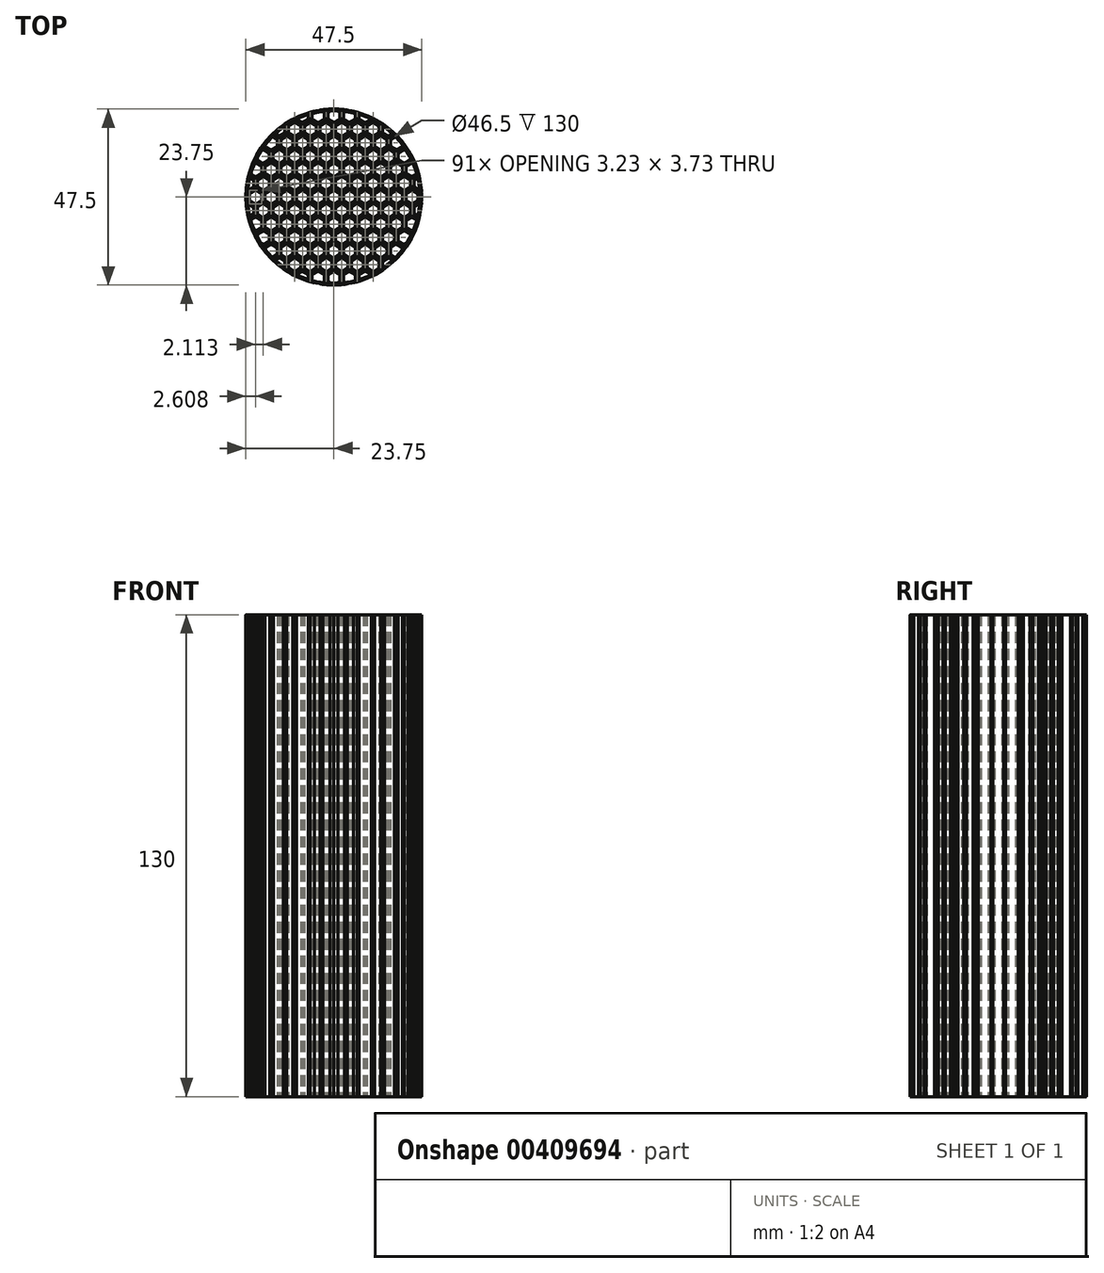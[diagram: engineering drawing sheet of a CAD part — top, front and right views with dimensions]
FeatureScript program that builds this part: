
annotation { "Feature Type Name" : "Feature", "Feature Type Description" : "" }
export const myFeature = defineFeature(function(context is Context, id is Id, definition is map)
    precondition{}
    {
        {
            var Q0;
            Q0=qCreatedBy(makeId("Top.planeOp"),FACE);
            var sketch = newSketch(context, id + "F0", { "sketchPlane" : qUnion([Q0])});
            skCircle(sketch, "E0", {"center": v(0, 0) * mm, "radius": 23.75 * mm});
            skCircle(sketch, "E1.cCircle", {"center": v(0, 0) * mm, "radius": 1.61 * mm, "construction": true});
            skLineSegment(sketch, "E1.0", {"start": v(1.61, 0.93) * mm, "end": v(1.61, -0.93) * mm});
            skLineSegment(sketch, "E1.1", {"start": v(1.61, -0.93) * mm, "end": v(0, -1.86) * mm});
            skLineSegment(sketch, "E1.2", {"start": v(0, -1.86) * mm, "end": v(-1.61, -0.93) * mm});
            skLineSegment(sketch, "E1.3", {"start": v(-1.61, -0.93) * mm, "end": v(-1.61, 0.93) * mm});
            skLineSegment(sketch, "E1.4", {"start": v(-1.61, 0.93) * mm, "end": v(0, 1.86) * mm});
            skLineSegment(sketch, "E1.5", {"start": v(0, 1.86) * mm, "end": v(1.61, 0.93) * mm});
            skPoint(sketch, "E1.0.midPoint", {"position": v(1.61, 0) * mm});
            skLineSegment(sketch, "E2", {"start": v(-1.61, 0) * mm, "end": v(1.61, 0) * mm, "construction": true});
            skCircle(sketch, "E3.cCircle", {"center": v(0, 0) * mm, "radius": 2.11 * mm, "construction": true});
            skLineSegment(sketch, "E3.0", {"start": v(2.11, 1.22) * mm, "end": v(2.11, -1.22) * mm});
            skLineSegment(sketch, "E3.1", {"start": v(2.11, -1.22) * mm, "end": v(0, -2.44) * mm});
            skLineSegment(sketch, "E3.2", {"start": v(0, -2.44) * mm, "end": v(-2.11, -1.22) * mm});
            skLineSegment(sketch, "E3.3", {"start": v(-2.11, -1.22) * mm, "end": v(-2.11, 1.22) * mm});
            skLineSegment(sketch, "E3.4", {"start": v(-2.11, 1.22) * mm, "end": v(0, 2.44) * mm});
            skLineSegment(sketch, "E3.5", {"start": v(0, 2.44) * mm, "end": v(2.11, 1.22) * mm});
            skPoint(sketch, "E3.0.midPoint", {"position": v(2.11, 0) * mm});
            skLineSegment(sketch, "E4", {"start": v(1.61, 0) * mm, "end": v(2.11, 0) * mm, "construction": true});
            skCircle(sketch, "E5", {"center": v(0, 0) * mm, "radius": 23.25 * mm});
            skLineSegment(sketch, "E6", {"start": v(23.25, 0) * mm, "end": v(23.75, 0) * mm, "construction": true});
            skSolve(sketch);
        }
        {
            var Q0;
            Q0=makeQuery(id+"F0.imprint","IMPRINT",FACE,{"disambiguationData":[TD([[makeQuery(id+"F0.imprint","IMPRINT",EDGE,{"derivedFrom":sQuery(id+"F0.wireOp",EDGE,"E1.0")}),1.0]])]});
            var Q1;
            Q1=makeQuery(id+"F0.imprint","IMPRINT",FACE,{"disambiguationData":[TD([[makeQuery(id+"F0.imprint","IMPRINT",EDGE,{"derivedFrom":sQuery(id+"F0.wireOp",EDGE,"E0")}),1.0]])]});
            extrude(context, id + "F1", {"entities" : qUnion([Q0, Q1]), "depth" : 130 * mm});
        }
        {
            var Q0;
            Q0=qCreatedBy(makeId("Top.planeOp"),FACE);
            var sketch = newSketch(context, id + "F2", { "sketchPlane" : qUnion([Q0])});
            skLineSegment(sketch, "E7", {"start": v(-33.71, 0) * mm, "end": v(22.23, 0) * mm, "construction": true});
            skLineSegment(sketch, "E8", {"start": v(0, 14.5) * mm, "end": v(0, -14.97) * mm, "construction": true});
            skLineSegment(sketch, "E9", {"start": v(0, 0) * mm, "end": v(-15.04, 15.04) * mm, "construction": true});
            skLineSegment(sketch, "E10", {"start": v(0, 0) * mm, "end": v(11.03, 11.03) * mm, "construction": true});
            skLineSegment(sketch, "E11", {"start": v(-15.04, 15.04) * mm, "end": v(21.6, -21.6) * mm, "construction": true});
            skLineSegment(sketch, "E12", {"start": v(11.03, 11.03) * mm, "end": v(-14.83, -14.83) * mm, "construction": true});
            skSolve(sketch);
        }
        {
            var Q0;
            Q0=makeQuery(id+"F1.opExtrude","SWEPT_BODY",BODY,{"disambiguationData":[OSD([sQuery(id+"F0.wireOp",EDGE,"E1.0"),sQuery(id+"F0.wireOp",EDGE,"E1.1"),sQuery(id+"F0.wireOp",EDGE,"E1.2"),sQuery(id+"F0.wireOp",EDGE,"E1.3"),sQuery(id+"F0.wireOp",EDGE,"E1.4"),sQuery(id+"F0.wireOp",EDGE,"E1.5"),sQuery(id+"F0.wireOp",EDGE,"E3.0"),sQuery(id+"F0.wireOp",EDGE,"E3.1"),sQuery(id+"F0.wireOp",EDGE,"E3.2"),sQuery(id+"F0.wireOp",EDGE,"E3.3"),sQuery(id+"F0.wireOp",EDGE,"E3.4"),sQuery(id+"F0.wireOp",EDGE,"E3.5")])]});
            var Q1;
            Q1=sQuery(id+"F2.wireOp",EDGE,"E7");
            transform(context, id + "F3", {"entities" : qUnion([Q0]), "transformType" : TransformType.TRANSLATION_3D, "dx" : 4.23 * mm, "dy" : 0 * mm, "dz" : 0 * mm, "makeCopy" : true});
        }
        {
            var Q0;
            Q0=makeQuery(id+"F1.opExtrude","SWEPT_BODY",BODY,{"disambiguationData":[OSD([sQuery(id+"F0.wireOp",EDGE,"E1.0"),sQuery(id+"F0.wireOp",EDGE,"E1.1"),sQuery(id+"F0.wireOp",EDGE,"E1.2"),sQuery(id+"F0.wireOp",EDGE,"E1.3"),sQuery(id+"F0.wireOp",EDGE,"E1.4"),sQuery(id+"F0.wireOp",EDGE,"E1.5"),sQuery(id+"F0.wireOp",EDGE,"E3.0"),sQuery(id+"F0.wireOp",EDGE,"E3.1"),sQuery(id+"F0.wireOp",EDGE,"E3.2"),sQuery(id+"F0.wireOp",EDGE,"E3.3"),sQuery(id+"F0.wireOp",EDGE,"E3.4"),sQuery(id+"F0.wireOp",EDGE,"E3.5")])]});
            var Q1;
            Q1=makeQuery(id+"F3.opPattern","COPY",BODY,{"derivedFrom":makeQuery(id+"F1.opExtrude","SWEPT_BODY",BODY,{"disambiguationData":[OSD([sQuery(id+"F0.wireOp",EDGE,"E1.0"),sQuery(id+"F0.wireOp",EDGE,"E1.1"),sQuery(id+"F0.wireOp",EDGE,"E1.2"),sQuery(id+"F0.wireOp",EDGE,"E1.3"),sQuery(id+"F0.wireOp",EDGE,"E1.4"),sQuery(id+"F0.wireOp",EDGE,"E1.5"),sQuery(id+"F0.wireOp",EDGE,"E3.0"),sQuery(id+"F0.wireOp",EDGE,"E3.1"),sQuery(id+"F0.wireOp",EDGE,"E3.2"),sQuery(id+"F0.wireOp",EDGE,"E3.3"),sQuery(id+"F0.wireOp",EDGE,"E3.4"),sQuery(id+"F0.wireOp",EDGE,"E3.5")])]}),"instanceName":"1"});
            transform(context, id + "F4", {"entities" : qUnion([Q0, Q1]), "transformType" : TransformType.TRANSLATION_3D, "dx" : 8.45 * mm, "dy" : 0 * mm, "dz" : 0 * mm, "makeCopy" : true});
        }
        {
            var Q0;
            Q0=makeQuery(id+"F4.opPattern","COPY",BODY,{"derivedFrom":makeQuery(id+"F1.opExtrude","SWEPT_BODY",BODY,{"disambiguationData":[OSD([sQuery(id+"F0.wireOp",EDGE,"E1.0"),sQuery(id+"F0.wireOp",EDGE,"E1.1"),sQuery(id+"F0.wireOp",EDGE,"E1.2"),sQuery(id+"F0.wireOp",EDGE,"E1.3"),sQuery(id+"F0.wireOp",EDGE,"E1.4"),sQuery(id+"F0.wireOp",EDGE,"E1.5"),sQuery(id+"F0.wireOp",EDGE,"E3.0"),sQuery(id+"F0.wireOp",EDGE,"E3.1"),sQuery(id+"F0.wireOp",EDGE,"E3.2"),sQuery(id+"F0.wireOp",EDGE,"E3.3"),sQuery(id+"F0.wireOp",EDGE,"E3.4"),sQuery(id+"F0.wireOp",EDGE,"E3.5")])]}),"instanceName":"1"});
            var Q1;
            Q1=makeQuery(id+"F4.opPattern","COPY",BODY,{"derivedFrom":makeQuery(id+"F3.opPattern","COPY",BODY,{"derivedFrom":makeQuery(id+"F1.opExtrude","SWEPT_BODY",BODY,{"disambiguationData":[OSD([sQuery(id+"F0.wireOp",EDGE,"E1.0"),sQuery(id+"F0.wireOp",EDGE,"E1.1"),sQuery(id+"F0.wireOp",EDGE,"E1.2"),sQuery(id+"F0.wireOp",EDGE,"E1.3"),sQuery(id+"F0.wireOp",EDGE,"E1.4"),sQuery(id+"F0.wireOp",EDGE,"E1.5"),sQuery(id+"F0.wireOp",EDGE,"E3.0"),sQuery(id+"F0.wireOp",EDGE,"E3.1"),sQuery(id+"F0.wireOp",EDGE,"E3.2"),sQuery(id+"F0.wireOp",EDGE,"E3.3"),sQuery(id+"F0.wireOp",EDGE,"E3.4"),sQuery(id+"F0.wireOp",EDGE,"E3.5")])]}),"instanceName":"1"}),"instanceName":"1"});
            transform(context, id + "F5", {"entities" : qUnion([Q0, Q1]), "transformType" : TransformType.TRANSLATION_3D, "dx" : 8.45 * mm, "dy" : 0 * mm, "dz" : 0 * mm, "makeCopy" : true});
        }
        {
            var Q0;
            Q0=makeQuery(id+"F1.opExtrude","SWEPT_BODY",BODY,{"disambiguationData":[OSD([sQuery(id+"F0.wireOp",EDGE,"E1.0"),sQuery(id+"F0.wireOp",EDGE,"E1.1"),sQuery(id+"F0.wireOp",EDGE,"E1.2"),sQuery(id+"F0.wireOp",EDGE,"E1.3"),sQuery(id+"F0.wireOp",EDGE,"E1.4"),sQuery(id+"F0.wireOp",EDGE,"E1.5"),sQuery(id+"F0.wireOp",EDGE,"E3.0"),sQuery(id+"F0.wireOp",EDGE,"E3.1"),sQuery(id+"F0.wireOp",EDGE,"E3.2"),sQuery(id+"F0.wireOp",EDGE,"E3.3"),sQuery(id+"F0.wireOp",EDGE,"E3.4"),sQuery(id+"F0.wireOp",EDGE,"E3.5")])]});
            var Q1;
            Q1=makeQuery(id+"F3.opPattern","COPY",BODY,{"derivedFrom":makeQuery(id+"F1.opExtrude","SWEPT_BODY",BODY,{"disambiguationData":[OSD([sQuery(id+"F0.wireOp",EDGE,"E1.0"),sQuery(id+"F0.wireOp",EDGE,"E1.1"),sQuery(id+"F0.wireOp",EDGE,"E1.2"),sQuery(id+"F0.wireOp",EDGE,"E1.3"),sQuery(id+"F0.wireOp",EDGE,"E1.4"),sQuery(id+"F0.wireOp",EDGE,"E1.5"),sQuery(id+"F0.wireOp",EDGE,"E3.0"),sQuery(id+"F0.wireOp",EDGE,"E3.1"),sQuery(id+"F0.wireOp",EDGE,"E3.2"),sQuery(id+"F0.wireOp",EDGE,"E3.3"),sQuery(id+"F0.wireOp",EDGE,"E3.4"),sQuery(id+"F0.wireOp",EDGE,"E3.5")])]}),"instanceName":"1"});
            var Q2;
            Q2=makeQuery(id+"F4.opPattern","COPY",BODY,{"derivedFrom":makeQuery(id+"F1.opExtrude","SWEPT_BODY",BODY,{"disambiguationData":[OSD([sQuery(id+"F0.wireOp",EDGE,"E1.0"),sQuery(id+"F0.wireOp",EDGE,"E1.1"),sQuery(id+"F0.wireOp",EDGE,"E1.2"),sQuery(id+"F0.wireOp",EDGE,"E1.3"),sQuery(id+"F0.wireOp",EDGE,"E1.4"),sQuery(id+"F0.wireOp",EDGE,"E1.5"),sQuery(id+"F0.wireOp",EDGE,"E3.0"),sQuery(id+"F0.wireOp",EDGE,"E3.1"),sQuery(id+"F0.wireOp",EDGE,"E3.2"),sQuery(id+"F0.wireOp",EDGE,"E3.3"),sQuery(id+"F0.wireOp",EDGE,"E3.4"),sQuery(id+"F0.wireOp",EDGE,"E3.5")])]}),"instanceName":"1"});
            var Q3;
            Q3=makeQuery(id+"F4.opPattern","COPY",BODY,{"derivedFrom":makeQuery(id+"F3.opPattern","COPY",BODY,{"derivedFrom":makeQuery(id+"F1.opExtrude","SWEPT_BODY",BODY,{"disambiguationData":[OSD([sQuery(id+"F0.wireOp",EDGE,"E1.0"),sQuery(id+"F0.wireOp",EDGE,"E1.1"),sQuery(id+"F0.wireOp",EDGE,"E1.2"),sQuery(id+"F0.wireOp",EDGE,"E1.3"),sQuery(id+"F0.wireOp",EDGE,"E1.4"),sQuery(id+"F0.wireOp",EDGE,"E1.5"),sQuery(id+"F0.wireOp",EDGE,"E3.0"),sQuery(id+"F0.wireOp",EDGE,"E3.1"),sQuery(id+"F0.wireOp",EDGE,"E3.2"),sQuery(id+"F0.wireOp",EDGE,"E3.3"),sQuery(id+"F0.wireOp",EDGE,"E3.4"),sQuery(id+"F0.wireOp",EDGE,"E3.5")])]}),"instanceName":"1"}),"instanceName":"1"});
            var Q4;
            Q4=makeQuery(id+"F5.opPattern","COPY",BODY,{"derivedFrom":makeQuery(id+"F4.opPattern","COPY",BODY,{"derivedFrom":makeQuery(id+"F1.opExtrude","SWEPT_BODY",BODY,{"disambiguationData":[OSD([sQuery(id+"F0.wireOp",EDGE,"E1.0"),sQuery(id+"F0.wireOp",EDGE,"E1.1"),sQuery(id+"F0.wireOp",EDGE,"E1.2"),sQuery(id+"F0.wireOp",EDGE,"E1.3"),sQuery(id+"F0.wireOp",EDGE,"E1.4"),sQuery(id+"F0.wireOp",EDGE,"E1.5"),sQuery(id+"F0.wireOp",EDGE,"E3.0"),sQuery(id+"F0.wireOp",EDGE,"E3.1"),sQuery(id+"F0.wireOp",EDGE,"E3.2"),sQuery(id+"F0.wireOp",EDGE,"E3.3"),sQuery(id+"F0.wireOp",EDGE,"E3.4"),sQuery(id+"F0.wireOp",EDGE,"E3.5")])]}),"instanceName":"1"}),"instanceName":"1"});
            var Q5;
            Q5=makeQuery(id+"F5.opPattern","COPY",BODY,{"derivedFrom":makeQuery(id+"F4.opPattern","COPY",BODY,{"derivedFrom":makeQuery(id+"F3.opPattern","COPY",BODY,{"derivedFrom":makeQuery(id+"F1.opExtrude","SWEPT_BODY",BODY,{"disambiguationData":[OSD([sQuery(id+"F0.wireOp",EDGE,"E1.0"),sQuery(id+"F0.wireOp",EDGE,"E1.1"),sQuery(id+"F0.wireOp",EDGE,"E1.2"),sQuery(id+"F0.wireOp",EDGE,"E1.3"),sQuery(id+"F0.wireOp",EDGE,"E1.4"),sQuery(id+"F0.wireOp",EDGE,"E1.5"),sQuery(id+"F0.wireOp",EDGE,"E3.0"),sQuery(id+"F0.wireOp",EDGE,"E3.1"),sQuery(id+"F0.wireOp",EDGE,"E3.2"),sQuery(id+"F0.wireOp",EDGE,"E3.3"),sQuery(id+"F0.wireOp",EDGE,"E3.4"),sQuery(id+"F0.wireOp",EDGE,"E3.5")])]}),"instanceName":"1"}),"instanceName":"1"}),"instanceName":"1"});
            transform(context, id + "F6", {"entities" : qUnion([Q0, Q1, Q2, Q3, Q4, Q5]), "transformType" : TransformType.TRANSLATION_3D, "dx" : 2.1 * mm, "dy" : 3.65 * mm, "dz" : 0 * mm, "makeCopy" : true});
        }
        {
            var Q0;
            Q0=makeQuery(id+"F6.opPattern","COPY",BODY,{"derivedFrom":makeQuery(id+"F1.opExtrude","SWEPT_BODY",BODY,{"disambiguationData":[OSD([sQuery(id+"F0.wireOp",EDGE,"E1.0"),sQuery(id+"F0.wireOp",EDGE,"E1.1"),sQuery(id+"F0.wireOp",EDGE,"E1.2"),sQuery(id+"F0.wireOp",EDGE,"E1.3"),sQuery(id+"F0.wireOp",EDGE,"E1.4"),sQuery(id+"F0.wireOp",EDGE,"E1.5"),sQuery(id+"F0.wireOp",EDGE,"E3.0"),sQuery(id+"F0.wireOp",EDGE,"E3.1"),sQuery(id+"F0.wireOp",EDGE,"E3.2"),sQuery(id+"F0.wireOp",EDGE,"E3.3"),sQuery(id+"F0.wireOp",EDGE,"E3.4"),sQuery(id+"F0.wireOp",EDGE,"E3.5")])]}),"instanceName":"1"});
            var Q1;
            Q1=makeQuery(id+"F1.opExtrude","SWEPT_BODY",BODY,{"disambiguationData":[OSD([sQuery(id+"F0.wireOp",EDGE,"E1.0"),sQuery(id+"F0.wireOp",EDGE,"E1.1"),sQuery(id+"F0.wireOp",EDGE,"E1.2"),sQuery(id+"F0.wireOp",EDGE,"E1.3"),sQuery(id+"F0.wireOp",EDGE,"E1.4"),sQuery(id+"F0.wireOp",EDGE,"E1.5"),sQuery(id+"F0.wireOp",EDGE,"E3.0"),sQuery(id+"F0.wireOp",EDGE,"E3.1"),sQuery(id+"F0.wireOp",EDGE,"E3.2"),sQuery(id+"F0.wireOp",EDGE,"E3.3"),sQuery(id+"F0.wireOp",EDGE,"E3.4"),sQuery(id+"F0.wireOp",EDGE,"E3.5")])]});
            var Q2;
            Q2=makeQuery(id+"F3.opPattern","COPY",BODY,{"derivedFrom":makeQuery(id+"F1.opExtrude","SWEPT_BODY",BODY,{"disambiguationData":[OSD([sQuery(id+"F0.wireOp",EDGE,"E1.0"),sQuery(id+"F0.wireOp",EDGE,"E1.1"),sQuery(id+"F0.wireOp",EDGE,"E1.2"),sQuery(id+"F0.wireOp",EDGE,"E1.3"),sQuery(id+"F0.wireOp",EDGE,"E1.4"),sQuery(id+"F0.wireOp",EDGE,"E1.5"),sQuery(id+"F0.wireOp",EDGE,"E3.0"),sQuery(id+"F0.wireOp",EDGE,"E3.1"),sQuery(id+"F0.wireOp",EDGE,"E3.2"),sQuery(id+"F0.wireOp",EDGE,"E3.3"),sQuery(id+"F0.wireOp",EDGE,"E3.4"),sQuery(id+"F0.wireOp",EDGE,"E3.5")])]}),"instanceName":"1"});
            var Q3;
            Q3=makeQuery(id+"F6.opPattern","COPY",BODY,{"derivedFrom":makeQuery(id+"F3.opPattern","COPY",BODY,{"derivedFrom":makeQuery(id+"F1.opExtrude","SWEPT_BODY",BODY,{"disambiguationData":[OSD([sQuery(id+"F0.wireOp",EDGE,"E1.0"),sQuery(id+"F0.wireOp",EDGE,"E1.1"),sQuery(id+"F0.wireOp",EDGE,"E1.2"),sQuery(id+"F0.wireOp",EDGE,"E1.3"),sQuery(id+"F0.wireOp",EDGE,"E1.4"),sQuery(id+"F0.wireOp",EDGE,"E1.5"),sQuery(id+"F0.wireOp",EDGE,"E3.0"),sQuery(id+"F0.wireOp",EDGE,"E3.1"),sQuery(id+"F0.wireOp",EDGE,"E3.2"),sQuery(id+"F0.wireOp",EDGE,"E3.3"),sQuery(id+"F0.wireOp",EDGE,"E3.4"),sQuery(id+"F0.wireOp",EDGE,"E3.5")])]}),"instanceName":"1"}),"instanceName":"1"});
            var Q4;
            Q4=makeQuery(id+"F6.opPattern","COPY",BODY,{"derivedFrom":makeQuery(id+"F4.opPattern","COPY",BODY,{"derivedFrom":makeQuery(id+"F1.opExtrude","SWEPT_BODY",BODY,{"disambiguationData":[OSD([sQuery(id+"F0.wireOp",EDGE,"E1.0"),sQuery(id+"F0.wireOp",EDGE,"E1.1"),sQuery(id+"F0.wireOp",EDGE,"E1.2"),sQuery(id+"F0.wireOp",EDGE,"E1.3"),sQuery(id+"F0.wireOp",EDGE,"E1.4"),sQuery(id+"F0.wireOp",EDGE,"E1.5"),sQuery(id+"F0.wireOp",EDGE,"E3.0"),sQuery(id+"F0.wireOp",EDGE,"E3.1"),sQuery(id+"F0.wireOp",EDGE,"E3.2"),sQuery(id+"F0.wireOp",EDGE,"E3.3"),sQuery(id+"F0.wireOp",EDGE,"E3.4"),sQuery(id+"F0.wireOp",EDGE,"E3.5")])]}),"instanceName":"1"}),"instanceName":"1"});
            var Q5;
            Q5=makeQuery(id+"F4.opPattern","COPY",BODY,{"derivedFrom":makeQuery(id+"F1.opExtrude","SWEPT_BODY",BODY,{"disambiguationData":[OSD([sQuery(id+"F0.wireOp",EDGE,"E1.0"),sQuery(id+"F0.wireOp",EDGE,"E1.1"),sQuery(id+"F0.wireOp",EDGE,"E1.2"),sQuery(id+"F0.wireOp",EDGE,"E1.3"),sQuery(id+"F0.wireOp",EDGE,"E1.4"),sQuery(id+"F0.wireOp",EDGE,"E1.5"),sQuery(id+"F0.wireOp",EDGE,"E3.0"),sQuery(id+"F0.wireOp",EDGE,"E3.1"),sQuery(id+"F0.wireOp",EDGE,"E3.2"),sQuery(id+"F0.wireOp",EDGE,"E3.3"),sQuery(id+"F0.wireOp",EDGE,"E3.4"),sQuery(id+"F0.wireOp",EDGE,"E3.5")])]}),"instanceName":"1"});
            var Q6;
            Q6=makeQuery(id+"F4.opPattern","COPY",BODY,{"derivedFrom":makeQuery(id+"F3.opPattern","COPY",BODY,{"derivedFrom":makeQuery(id+"F1.opExtrude","SWEPT_BODY",BODY,{"disambiguationData":[OSD([sQuery(id+"F0.wireOp",EDGE,"E1.0"),sQuery(id+"F0.wireOp",EDGE,"E1.1"),sQuery(id+"F0.wireOp",EDGE,"E1.2"),sQuery(id+"F0.wireOp",EDGE,"E1.3"),sQuery(id+"F0.wireOp",EDGE,"E1.4"),sQuery(id+"F0.wireOp",EDGE,"E1.5"),sQuery(id+"F0.wireOp",EDGE,"E3.0"),sQuery(id+"F0.wireOp",EDGE,"E3.1"),sQuery(id+"F0.wireOp",EDGE,"E3.2"),sQuery(id+"F0.wireOp",EDGE,"E3.3"),sQuery(id+"F0.wireOp",EDGE,"E3.4"),sQuery(id+"F0.wireOp",EDGE,"E3.5")])]}),"instanceName":"1"}),"instanceName":"1"});
            var Q7;
            Q7=makeQuery(id+"F6.opPattern","COPY",BODY,{"derivedFrom":makeQuery(id+"F4.opPattern","COPY",BODY,{"derivedFrom":makeQuery(id+"F3.opPattern","COPY",BODY,{"derivedFrom":makeQuery(id+"F1.opExtrude","SWEPT_BODY",BODY,{"disambiguationData":[OSD([sQuery(id+"F0.wireOp",EDGE,"E1.0"),sQuery(id+"F0.wireOp",EDGE,"E1.1"),sQuery(id+"F0.wireOp",EDGE,"E1.2"),sQuery(id+"F0.wireOp",EDGE,"E1.3"),sQuery(id+"F0.wireOp",EDGE,"E1.4"),sQuery(id+"F0.wireOp",EDGE,"E1.5"),sQuery(id+"F0.wireOp",EDGE,"E3.0"),sQuery(id+"F0.wireOp",EDGE,"E3.1"),sQuery(id+"F0.wireOp",EDGE,"E3.2"),sQuery(id+"F0.wireOp",EDGE,"E3.3"),sQuery(id+"F0.wireOp",EDGE,"E3.4"),sQuery(id+"F0.wireOp",EDGE,"E3.5")])]}),"instanceName":"1"}),"instanceName":"1"}),"instanceName":"1"});
            var Q8;
            Q8=makeQuery(id+"F6.opPattern","COPY",BODY,{"derivedFrom":makeQuery(id+"F5.opPattern","COPY",BODY,{"derivedFrom":makeQuery(id+"F4.opPattern","COPY",BODY,{"derivedFrom":makeQuery(id+"F1.opExtrude","SWEPT_BODY",BODY,{"disambiguationData":[OSD([sQuery(id+"F0.wireOp",EDGE,"E1.0"),sQuery(id+"F0.wireOp",EDGE,"E1.1"),sQuery(id+"F0.wireOp",EDGE,"E1.2"),sQuery(id+"F0.wireOp",EDGE,"E1.3"),sQuery(id+"F0.wireOp",EDGE,"E1.4"),sQuery(id+"F0.wireOp",EDGE,"E1.5"),sQuery(id+"F0.wireOp",EDGE,"E3.0"),sQuery(id+"F0.wireOp",EDGE,"E3.1"),sQuery(id+"F0.wireOp",EDGE,"E3.2"),sQuery(id+"F0.wireOp",EDGE,"E3.3"),sQuery(id+"F0.wireOp",EDGE,"E3.4"),sQuery(id+"F0.wireOp",EDGE,"E3.5")])]}),"instanceName":"1"}),"instanceName":"1"}),"instanceName":"1"});
            var Q9;
            Q9=makeQuery(id+"F5.opPattern","COPY",BODY,{"derivedFrom":makeQuery(id+"F4.opPattern","COPY",BODY,{"derivedFrom":makeQuery(id+"F1.opExtrude","SWEPT_BODY",BODY,{"disambiguationData":[OSD([sQuery(id+"F0.wireOp",EDGE,"E1.0"),sQuery(id+"F0.wireOp",EDGE,"E1.1"),sQuery(id+"F0.wireOp",EDGE,"E1.2"),sQuery(id+"F0.wireOp",EDGE,"E1.3"),sQuery(id+"F0.wireOp",EDGE,"E1.4"),sQuery(id+"F0.wireOp",EDGE,"E1.5"),sQuery(id+"F0.wireOp",EDGE,"E3.0"),sQuery(id+"F0.wireOp",EDGE,"E3.1"),sQuery(id+"F0.wireOp",EDGE,"E3.2"),sQuery(id+"F0.wireOp",EDGE,"E3.3"),sQuery(id+"F0.wireOp",EDGE,"E3.4"),sQuery(id+"F0.wireOp",EDGE,"E3.5")])]}),"instanceName":"1"}),"instanceName":"1"});
            var Q10;
            Q10=makeQuery(id+"F6.opPattern","COPY",BODY,{"derivedFrom":makeQuery(id+"F5.opPattern","COPY",BODY,{"derivedFrom":makeQuery(id+"F4.opPattern","COPY",BODY,{"derivedFrom":makeQuery(id+"F3.opPattern","COPY",BODY,{"derivedFrom":makeQuery(id+"F1.opExtrude","SWEPT_BODY",BODY,{"disambiguationData":[OSD([sQuery(id+"F0.wireOp",EDGE,"E1.0"),sQuery(id+"F0.wireOp",EDGE,"E1.1"),sQuery(id+"F0.wireOp",EDGE,"E1.2"),sQuery(id+"F0.wireOp",EDGE,"E1.3"),sQuery(id+"F0.wireOp",EDGE,"E1.4"),sQuery(id+"F0.wireOp",EDGE,"E1.5"),sQuery(id+"F0.wireOp",EDGE,"E3.0"),sQuery(id+"F0.wireOp",EDGE,"E3.1"),sQuery(id+"F0.wireOp",EDGE,"E3.2"),sQuery(id+"F0.wireOp",EDGE,"E3.3"),sQuery(id+"F0.wireOp",EDGE,"E3.4"),sQuery(id+"F0.wireOp",EDGE,"E3.5")])]}),"instanceName":"1"}),"instanceName":"1"}),"instanceName":"1"}),"instanceName":"1"});
            var Q11;
            Q11=makeQuery(id+"F5.opPattern","COPY",BODY,{"derivedFrom":makeQuery(id+"F4.opPattern","COPY",BODY,{"derivedFrom":makeQuery(id+"F3.opPattern","COPY",BODY,{"derivedFrom":makeQuery(id+"F1.opExtrude","SWEPT_BODY",BODY,{"disambiguationData":[OSD([sQuery(id+"F0.wireOp",EDGE,"E1.0"),sQuery(id+"F0.wireOp",EDGE,"E1.1"),sQuery(id+"F0.wireOp",EDGE,"E1.2"),sQuery(id+"F0.wireOp",EDGE,"E1.3"),sQuery(id+"F0.wireOp",EDGE,"E1.4"),sQuery(id+"F0.wireOp",EDGE,"E1.5"),sQuery(id+"F0.wireOp",EDGE,"E3.0"),sQuery(id+"F0.wireOp",EDGE,"E3.1"),sQuery(id+"F0.wireOp",EDGE,"E3.2"),sQuery(id+"F0.wireOp",EDGE,"E3.3"),sQuery(id+"F0.wireOp",EDGE,"E3.4"),sQuery(id+"F0.wireOp",EDGE,"E3.5")])]}),"instanceName":"1"}),"instanceName":"1"}),"instanceName":"1"});
            transform(context, id + "F7", {"entities" : qUnion([Q0, Q1, Q2, Q3, Q4, Q5, Q6, Q7, Q8, Q9, Q10, Q11]), "transformType" : TransformType.TRANSLATION_3D, "dx" : 4.23 * mm, "dy" : 7.3 * mm, "dz" : 0 * mm, "makeCopy" : true});
        }
        {
            var Q0;
            Q0=makeQuery(id+"F1.opExtrude","SWEPT_BODY",BODY,{"disambiguationData":[OSD([sQuery(id+"F0.wireOp",EDGE,"E1.0"),sQuery(id+"F0.wireOp",EDGE,"E1.1"),sQuery(id+"F0.wireOp",EDGE,"E1.2"),sQuery(id+"F0.wireOp",EDGE,"E1.3"),sQuery(id+"F0.wireOp",EDGE,"E1.4"),sQuery(id+"F0.wireOp",EDGE,"E1.5"),sQuery(id+"F0.wireOp",EDGE,"E3.0"),sQuery(id+"F0.wireOp",EDGE,"E3.1"),sQuery(id+"F0.wireOp",EDGE,"E3.2"),sQuery(id+"F0.wireOp",EDGE,"E3.3"),sQuery(id+"F0.wireOp",EDGE,"E3.4"),sQuery(id+"F0.wireOp",EDGE,"E3.5")])]});
            var Q1;
            Q1=makeQuery(id+"F7.opPattern","COPY",BODY,{"derivedFrom":makeQuery(id+"F6.opPattern","COPY",BODY,{"derivedFrom":makeQuery(id+"F3.opPattern","COPY",BODY,{"derivedFrom":makeQuery(id+"F1.opExtrude","SWEPT_BODY",BODY,{"disambiguationData":[OSD([sQuery(id+"F0.wireOp",EDGE,"E1.0"),sQuery(id+"F0.wireOp",EDGE,"E1.1"),sQuery(id+"F0.wireOp",EDGE,"E1.2"),sQuery(id+"F0.wireOp",EDGE,"E1.3"),sQuery(id+"F0.wireOp",EDGE,"E1.4"),sQuery(id+"F0.wireOp",EDGE,"E1.5"),sQuery(id+"F0.wireOp",EDGE,"E3.0"),sQuery(id+"F0.wireOp",EDGE,"E3.1"),sQuery(id+"F0.wireOp",EDGE,"E3.2"),sQuery(id+"F0.wireOp",EDGE,"E3.3"),sQuery(id+"F0.wireOp",EDGE,"E3.4"),sQuery(id+"F0.wireOp",EDGE,"E3.5")])]}),"instanceName":"1"}),"instanceName":"1"}),"instanceName":"1"});
            var Q2;
            Q2=makeQuery(id+"F7.opPattern","COPY",BODY,{"derivedFrom":makeQuery(id+"F6.opPattern","COPY",BODY,{"derivedFrom":makeQuery(id+"F1.opExtrude","SWEPT_BODY",BODY,{"disambiguationData":[OSD([sQuery(id+"F0.wireOp",EDGE,"E1.0"),sQuery(id+"F0.wireOp",EDGE,"E1.1"),sQuery(id+"F0.wireOp",EDGE,"E1.2"),sQuery(id+"F0.wireOp",EDGE,"E1.3"),sQuery(id+"F0.wireOp",EDGE,"E1.4"),sQuery(id+"F0.wireOp",EDGE,"E1.5"),sQuery(id+"F0.wireOp",EDGE,"E3.0"),sQuery(id+"F0.wireOp",EDGE,"E3.1"),sQuery(id+"F0.wireOp",EDGE,"E3.2"),sQuery(id+"F0.wireOp",EDGE,"E3.3"),sQuery(id+"F0.wireOp",EDGE,"E3.4"),sQuery(id+"F0.wireOp",EDGE,"E3.5")])]}),"instanceName":"1"}),"instanceName":"1"});
            var Q3;
            Q3=makeQuery(id+"F7.opPattern","COPY",BODY,{"derivedFrom":makeQuery(id+"F4.opPattern","COPY",BODY,{"derivedFrom":makeQuery(id+"F1.opExtrude","SWEPT_BODY",BODY,{"disambiguationData":[OSD([sQuery(id+"F0.wireOp",EDGE,"E1.0"),sQuery(id+"F0.wireOp",EDGE,"E1.1"),sQuery(id+"F0.wireOp",EDGE,"E1.2"),sQuery(id+"F0.wireOp",EDGE,"E1.3"),sQuery(id+"F0.wireOp",EDGE,"E1.4"),sQuery(id+"F0.wireOp",EDGE,"E1.5"),sQuery(id+"F0.wireOp",EDGE,"E3.0"),sQuery(id+"F0.wireOp",EDGE,"E3.1"),sQuery(id+"F0.wireOp",EDGE,"E3.2"),sQuery(id+"F0.wireOp",EDGE,"E3.3"),sQuery(id+"F0.wireOp",EDGE,"E3.4"),sQuery(id+"F0.wireOp",EDGE,"E3.5")])]}),"instanceName":"1"}),"instanceName":"1"});
            var Q4;
            Q4=makeQuery(id+"F7.opPattern","COPY",BODY,{"derivedFrom":makeQuery(id+"F3.opPattern","COPY",BODY,{"derivedFrom":makeQuery(id+"F1.opExtrude","SWEPT_BODY",BODY,{"disambiguationData":[OSD([sQuery(id+"F0.wireOp",EDGE,"E1.0"),sQuery(id+"F0.wireOp",EDGE,"E1.1"),sQuery(id+"F0.wireOp",EDGE,"E1.2"),sQuery(id+"F0.wireOp",EDGE,"E1.3"),sQuery(id+"F0.wireOp",EDGE,"E1.4"),sQuery(id+"F0.wireOp",EDGE,"E1.5"),sQuery(id+"F0.wireOp",EDGE,"E3.0"),sQuery(id+"F0.wireOp",EDGE,"E3.1"),sQuery(id+"F0.wireOp",EDGE,"E3.2"),sQuery(id+"F0.wireOp",EDGE,"E3.3"),sQuery(id+"F0.wireOp",EDGE,"E3.4"),sQuery(id+"F0.wireOp",EDGE,"E3.5")])]}),"instanceName":"1"}),"instanceName":"1"});
            var Q5;
            Q5=makeQuery(id+"F7.opPattern","COPY",BODY,{"derivedFrom":makeQuery(id+"F1.opExtrude","SWEPT_BODY",BODY,{"disambiguationData":[OSD([sQuery(id+"F0.wireOp",EDGE,"E1.0"),sQuery(id+"F0.wireOp",EDGE,"E1.1"),sQuery(id+"F0.wireOp",EDGE,"E1.2"),sQuery(id+"F0.wireOp",EDGE,"E1.3"),sQuery(id+"F0.wireOp",EDGE,"E1.4"),sQuery(id+"F0.wireOp",EDGE,"E1.5"),sQuery(id+"F0.wireOp",EDGE,"E3.0"),sQuery(id+"F0.wireOp",EDGE,"E3.1"),sQuery(id+"F0.wireOp",EDGE,"E3.2"),sQuery(id+"F0.wireOp",EDGE,"E3.3"),sQuery(id+"F0.wireOp",EDGE,"E3.4"),sQuery(id+"F0.wireOp",EDGE,"E3.5")])]}),"instanceName":"1"});
            var Q6;
            Q6=makeQuery(id+"F6.opPattern","COPY",BODY,{"derivedFrom":makeQuery(id+"F4.opPattern","COPY",BODY,{"derivedFrom":makeQuery(id+"F1.opExtrude","SWEPT_BODY",BODY,{"disambiguationData":[OSD([sQuery(id+"F0.wireOp",EDGE,"E1.0"),sQuery(id+"F0.wireOp",EDGE,"E1.1"),sQuery(id+"F0.wireOp",EDGE,"E1.2"),sQuery(id+"F0.wireOp",EDGE,"E1.3"),sQuery(id+"F0.wireOp",EDGE,"E1.4"),sQuery(id+"F0.wireOp",EDGE,"E1.5"),sQuery(id+"F0.wireOp",EDGE,"E3.0"),sQuery(id+"F0.wireOp",EDGE,"E3.1"),sQuery(id+"F0.wireOp",EDGE,"E3.2"),sQuery(id+"F0.wireOp",EDGE,"E3.3"),sQuery(id+"F0.wireOp",EDGE,"E3.4"),sQuery(id+"F0.wireOp",EDGE,"E3.5")])]}),"instanceName":"1"}),"instanceName":"1"});
            var Q7;
            Q7=makeQuery(id+"F6.opPattern","COPY",BODY,{"derivedFrom":makeQuery(id+"F3.opPattern","COPY",BODY,{"derivedFrom":makeQuery(id+"F1.opExtrude","SWEPT_BODY",BODY,{"disambiguationData":[OSD([sQuery(id+"F0.wireOp",EDGE,"E1.0"),sQuery(id+"F0.wireOp",EDGE,"E1.1"),sQuery(id+"F0.wireOp",EDGE,"E1.2"),sQuery(id+"F0.wireOp",EDGE,"E1.3"),sQuery(id+"F0.wireOp",EDGE,"E1.4"),sQuery(id+"F0.wireOp",EDGE,"E1.5"),sQuery(id+"F0.wireOp",EDGE,"E3.0"),sQuery(id+"F0.wireOp",EDGE,"E3.1"),sQuery(id+"F0.wireOp",EDGE,"E3.2"),sQuery(id+"F0.wireOp",EDGE,"E3.3"),sQuery(id+"F0.wireOp",EDGE,"E3.4"),sQuery(id+"F0.wireOp",EDGE,"E3.5")])]}),"instanceName":"1"}),"instanceName":"1"});
            var Q8;
            Q8=makeQuery(id+"F6.opPattern","COPY",BODY,{"derivedFrom":makeQuery(id+"F1.opExtrude","SWEPT_BODY",BODY,{"disambiguationData":[OSD([sQuery(id+"F0.wireOp",EDGE,"E1.0"),sQuery(id+"F0.wireOp",EDGE,"E1.1"),sQuery(id+"F0.wireOp",EDGE,"E1.2"),sQuery(id+"F0.wireOp",EDGE,"E1.3"),sQuery(id+"F0.wireOp",EDGE,"E1.4"),sQuery(id+"F0.wireOp",EDGE,"E1.5"),sQuery(id+"F0.wireOp",EDGE,"E3.0"),sQuery(id+"F0.wireOp",EDGE,"E3.1"),sQuery(id+"F0.wireOp",EDGE,"E3.2"),sQuery(id+"F0.wireOp",EDGE,"E3.3"),sQuery(id+"F0.wireOp",EDGE,"E3.4"),sQuery(id+"F0.wireOp",EDGE,"E3.5")])]}),"instanceName":"1"});
            var Q9;
            Q9=makeQuery(id+"F4.opPattern","COPY",BODY,{"derivedFrom":makeQuery(id+"F3.opPattern","COPY",BODY,{"derivedFrom":makeQuery(id+"F1.opExtrude","SWEPT_BODY",BODY,{"disambiguationData":[OSD([sQuery(id+"F0.wireOp",EDGE,"E1.0"),sQuery(id+"F0.wireOp",EDGE,"E1.1"),sQuery(id+"F0.wireOp",EDGE,"E1.2"),sQuery(id+"F0.wireOp",EDGE,"E1.3"),sQuery(id+"F0.wireOp",EDGE,"E1.4"),sQuery(id+"F0.wireOp",EDGE,"E1.5"),sQuery(id+"F0.wireOp",EDGE,"E3.0"),sQuery(id+"F0.wireOp",EDGE,"E3.1"),sQuery(id+"F0.wireOp",EDGE,"E3.2"),sQuery(id+"F0.wireOp",EDGE,"E3.3"),sQuery(id+"F0.wireOp",EDGE,"E3.4"),sQuery(id+"F0.wireOp",EDGE,"E3.5")])]}),"instanceName":"1"}),"instanceName":"1"});
            var Q10;
            Q10=makeQuery(id+"F4.opPattern","COPY",BODY,{"derivedFrom":makeQuery(id+"F1.opExtrude","SWEPT_BODY",BODY,{"disambiguationData":[OSD([sQuery(id+"F0.wireOp",EDGE,"E1.0"),sQuery(id+"F0.wireOp",EDGE,"E1.1"),sQuery(id+"F0.wireOp",EDGE,"E1.2"),sQuery(id+"F0.wireOp",EDGE,"E1.3"),sQuery(id+"F0.wireOp",EDGE,"E1.4"),sQuery(id+"F0.wireOp",EDGE,"E1.5"),sQuery(id+"F0.wireOp",EDGE,"E3.0"),sQuery(id+"F0.wireOp",EDGE,"E3.1"),sQuery(id+"F0.wireOp",EDGE,"E3.2"),sQuery(id+"F0.wireOp",EDGE,"E3.3"),sQuery(id+"F0.wireOp",EDGE,"E3.4"),sQuery(id+"F0.wireOp",EDGE,"E3.5")])]}),"instanceName":"1"});
            var Q11;
            Q11=makeQuery(id+"F3.opPattern","COPY",BODY,{"derivedFrom":makeQuery(id+"F1.opExtrude","SWEPT_BODY",BODY,{"disambiguationData":[OSD([sQuery(id+"F0.wireOp",EDGE,"E1.0"),sQuery(id+"F0.wireOp",EDGE,"E1.1"),sQuery(id+"F0.wireOp",EDGE,"E1.2"),sQuery(id+"F0.wireOp",EDGE,"E1.3"),sQuery(id+"F0.wireOp",EDGE,"E1.4"),sQuery(id+"F0.wireOp",EDGE,"E1.5"),sQuery(id+"F0.wireOp",EDGE,"E3.0"),sQuery(id+"F0.wireOp",EDGE,"E3.1"),sQuery(id+"F0.wireOp",EDGE,"E3.2"),sQuery(id+"F0.wireOp",EDGE,"E3.3"),sQuery(id+"F0.wireOp",EDGE,"E3.4"),sQuery(id+"F0.wireOp",EDGE,"E3.5")])]}),"instanceName":"1"});
            var Q12;
            Q12=makeQuery(id+"F6.opPattern","COPY",BODY,{"derivedFrom":makeQuery(id+"F4.opPattern","COPY",BODY,{"derivedFrom":makeQuery(id+"F3.opPattern","COPY",BODY,{"derivedFrom":makeQuery(id+"F1.opExtrude","SWEPT_BODY",BODY,{"disambiguationData":[OSD([sQuery(id+"F0.wireOp",EDGE,"E1.0"),sQuery(id+"F0.wireOp",EDGE,"E1.1"),sQuery(id+"F0.wireOp",EDGE,"E1.2"),sQuery(id+"F0.wireOp",EDGE,"E1.3"),sQuery(id+"F0.wireOp",EDGE,"E1.4"),sQuery(id+"F0.wireOp",EDGE,"E1.5"),sQuery(id+"F0.wireOp",EDGE,"E3.0"),sQuery(id+"F0.wireOp",EDGE,"E3.1"),sQuery(id+"F0.wireOp",EDGE,"E3.2"),sQuery(id+"F0.wireOp",EDGE,"E3.3"),sQuery(id+"F0.wireOp",EDGE,"E3.4"),sQuery(id+"F0.wireOp",EDGE,"E3.5")])]}),"instanceName":"1"}),"instanceName":"1"}),"instanceName":"1"});
            var Q13;
            Q13=makeQuery(id+"F7.opPattern","COPY",BODY,{"derivedFrom":makeQuery(id+"F4.opPattern","COPY",BODY,{"derivedFrom":makeQuery(id+"F3.opPattern","COPY",BODY,{"derivedFrom":makeQuery(id+"F1.opExtrude","SWEPT_BODY",BODY,{"disambiguationData":[OSD([sQuery(id+"F0.wireOp",EDGE,"E1.0"),sQuery(id+"F0.wireOp",EDGE,"E1.1"),sQuery(id+"F0.wireOp",EDGE,"E1.2"),sQuery(id+"F0.wireOp",EDGE,"E1.3"),sQuery(id+"F0.wireOp",EDGE,"E1.4"),sQuery(id+"F0.wireOp",EDGE,"E1.5"),sQuery(id+"F0.wireOp",EDGE,"E3.0"),sQuery(id+"F0.wireOp",EDGE,"E3.1"),sQuery(id+"F0.wireOp",EDGE,"E3.2"),sQuery(id+"F0.wireOp",EDGE,"E3.3"),sQuery(id+"F0.wireOp",EDGE,"E3.4"),sQuery(id+"F0.wireOp",EDGE,"E3.5")])]}),"instanceName":"1"}),"instanceName":"1"}),"instanceName":"1"});
            var Q14;
            Q14=makeQuery(id+"F7.opPattern","COPY",BODY,{"derivedFrom":makeQuery(id+"F6.opPattern","COPY",BODY,{"derivedFrom":makeQuery(id+"F4.opPattern","COPY",BODY,{"derivedFrom":makeQuery(id+"F1.opExtrude","SWEPT_BODY",BODY,{"disambiguationData":[OSD([sQuery(id+"F0.wireOp",EDGE,"E1.0"),sQuery(id+"F0.wireOp",EDGE,"E1.1"),sQuery(id+"F0.wireOp",EDGE,"E1.2"),sQuery(id+"F0.wireOp",EDGE,"E1.3"),sQuery(id+"F0.wireOp",EDGE,"E1.4"),sQuery(id+"F0.wireOp",EDGE,"E1.5"),sQuery(id+"F0.wireOp",EDGE,"E3.0"),sQuery(id+"F0.wireOp",EDGE,"E3.1"),sQuery(id+"F0.wireOp",EDGE,"E3.2"),sQuery(id+"F0.wireOp",EDGE,"E3.3"),sQuery(id+"F0.wireOp",EDGE,"E3.4"),sQuery(id+"F0.wireOp",EDGE,"E3.5")])]}),"instanceName":"1"}),"instanceName":"1"}),"instanceName":"1"});
            var Q15;
            Q15=makeQuery(id+"F7.opPattern","COPY",BODY,{"derivedFrom":makeQuery(id+"F6.opPattern","COPY",BODY,{"derivedFrom":makeQuery(id+"F4.opPattern","COPY",BODY,{"derivedFrom":makeQuery(id+"F3.opPattern","COPY",BODY,{"derivedFrom":makeQuery(id+"F1.opExtrude","SWEPT_BODY",BODY,{"disambiguationData":[OSD([sQuery(id+"F0.wireOp",EDGE,"E1.0"),sQuery(id+"F0.wireOp",EDGE,"E1.1"),sQuery(id+"F0.wireOp",EDGE,"E1.2"),sQuery(id+"F0.wireOp",EDGE,"E1.3"),sQuery(id+"F0.wireOp",EDGE,"E1.4"),sQuery(id+"F0.wireOp",EDGE,"E1.5"),sQuery(id+"F0.wireOp",EDGE,"E3.0"),sQuery(id+"F0.wireOp",EDGE,"E3.1"),sQuery(id+"F0.wireOp",EDGE,"E3.2"),sQuery(id+"F0.wireOp",EDGE,"E3.3"),sQuery(id+"F0.wireOp",EDGE,"E3.4"),sQuery(id+"F0.wireOp",EDGE,"E3.5")])]}),"instanceName":"1"}),"instanceName":"1"}),"instanceName":"1"}),"instanceName":"1"});
            var Q16;
            Q16=makeQuery(id+"F7.opPattern","COPY",BODY,{"derivedFrom":makeQuery(id+"F5.opPattern","COPY",BODY,{"derivedFrom":makeQuery(id+"F4.opPattern","COPY",BODY,{"derivedFrom":makeQuery(id+"F1.opExtrude","SWEPT_BODY",BODY,{"disambiguationData":[OSD([sQuery(id+"F0.wireOp",EDGE,"E1.0"),sQuery(id+"F0.wireOp",EDGE,"E1.1"),sQuery(id+"F0.wireOp",EDGE,"E1.2"),sQuery(id+"F0.wireOp",EDGE,"E1.3"),sQuery(id+"F0.wireOp",EDGE,"E1.4"),sQuery(id+"F0.wireOp",EDGE,"E1.5"),sQuery(id+"F0.wireOp",EDGE,"E3.0"),sQuery(id+"F0.wireOp",EDGE,"E3.1"),sQuery(id+"F0.wireOp",EDGE,"E3.2"),sQuery(id+"F0.wireOp",EDGE,"E3.3"),sQuery(id+"F0.wireOp",EDGE,"E3.4"),sQuery(id+"F0.wireOp",EDGE,"E3.5")])]}),"instanceName":"1"}),"instanceName":"1"}),"instanceName":"1"});
            var Q17;
            Q17=makeQuery(id+"F6.opPattern","COPY",BODY,{"derivedFrom":makeQuery(id+"F5.opPattern","COPY",BODY,{"derivedFrom":makeQuery(id+"F4.opPattern","COPY",BODY,{"derivedFrom":makeQuery(id+"F1.opExtrude","SWEPT_BODY",BODY,{"disambiguationData":[OSD([sQuery(id+"F0.wireOp",EDGE,"E1.0"),sQuery(id+"F0.wireOp",EDGE,"E1.1"),sQuery(id+"F0.wireOp",EDGE,"E1.2"),sQuery(id+"F0.wireOp",EDGE,"E1.3"),sQuery(id+"F0.wireOp",EDGE,"E1.4"),sQuery(id+"F0.wireOp",EDGE,"E1.5"),sQuery(id+"F0.wireOp",EDGE,"E3.0"),sQuery(id+"F0.wireOp",EDGE,"E3.1"),sQuery(id+"F0.wireOp",EDGE,"E3.2"),sQuery(id+"F0.wireOp",EDGE,"E3.3"),sQuery(id+"F0.wireOp",EDGE,"E3.4"),sQuery(id+"F0.wireOp",EDGE,"E3.5")])]}),"instanceName":"1"}),"instanceName":"1"}),"instanceName":"1"});
            var Q18;
            Q18=makeQuery(id+"F5.opPattern","COPY",BODY,{"derivedFrom":makeQuery(id+"F4.opPattern","COPY",BODY,{"derivedFrom":makeQuery(id+"F1.opExtrude","SWEPT_BODY",BODY,{"disambiguationData":[OSD([sQuery(id+"F0.wireOp",EDGE,"E1.0"),sQuery(id+"F0.wireOp",EDGE,"E1.1"),sQuery(id+"F0.wireOp",EDGE,"E1.2"),sQuery(id+"F0.wireOp",EDGE,"E1.3"),sQuery(id+"F0.wireOp",EDGE,"E1.4"),sQuery(id+"F0.wireOp",EDGE,"E1.5"),sQuery(id+"F0.wireOp",EDGE,"E3.0"),sQuery(id+"F0.wireOp",EDGE,"E3.1"),sQuery(id+"F0.wireOp",EDGE,"E3.2"),sQuery(id+"F0.wireOp",EDGE,"E3.3"),sQuery(id+"F0.wireOp",EDGE,"E3.4"),sQuery(id+"F0.wireOp",EDGE,"E3.5")])]}),"instanceName":"1"}),"instanceName":"1"});
            var Q19;
            Q19=makeQuery(id+"F5.opPattern","COPY",BODY,{"derivedFrom":makeQuery(id+"F4.opPattern","COPY",BODY,{"derivedFrom":makeQuery(id+"F3.opPattern","COPY",BODY,{"derivedFrom":makeQuery(id+"F1.opExtrude","SWEPT_BODY",BODY,{"disambiguationData":[OSD([sQuery(id+"F0.wireOp",EDGE,"E1.0"),sQuery(id+"F0.wireOp",EDGE,"E1.1"),sQuery(id+"F0.wireOp",EDGE,"E1.2"),sQuery(id+"F0.wireOp",EDGE,"E1.3"),sQuery(id+"F0.wireOp",EDGE,"E1.4"),sQuery(id+"F0.wireOp",EDGE,"E1.5"),sQuery(id+"F0.wireOp",EDGE,"E3.0"),sQuery(id+"F0.wireOp",EDGE,"E3.1"),sQuery(id+"F0.wireOp",EDGE,"E3.2"),sQuery(id+"F0.wireOp",EDGE,"E3.3"),sQuery(id+"F0.wireOp",EDGE,"E3.4"),sQuery(id+"F0.wireOp",EDGE,"E3.5")])]}),"instanceName":"1"}),"instanceName":"1"}),"instanceName":"1"});
            var Q20;
            Q20=makeQuery(id+"F6.opPattern","COPY",BODY,{"derivedFrom":makeQuery(id+"F5.opPattern","COPY",BODY,{"derivedFrom":makeQuery(id+"F4.opPattern","COPY",BODY,{"derivedFrom":makeQuery(id+"F3.opPattern","COPY",BODY,{"derivedFrom":makeQuery(id+"F1.opExtrude","SWEPT_BODY",BODY,{"disambiguationData":[OSD([sQuery(id+"F0.wireOp",EDGE,"E1.0"),sQuery(id+"F0.wireOp",EDGE,"E1.1"),sQuery(id+"F0.wireOp",EDGE,"E1.2"),sQuery(id+"F0.wireOp",EDGE,"E1.3"),sQuery(id+"F0.wireOp",EDGE,"E1.4"),sQuery(id+"F0.wireOp",EDGE,"E1.5"),sQuery(id+"F0.wireOp",EDGE,"E3.0"),sQuery(id+"F0.wireOp",EDGE,"E3.1"),sQuery(id+"F0.wireOp",EDGE,"E3.2"),sQuery(id+"F0.wireOp",EDGE,"E3.3"),sQuery(id+"F0.wireOp",EDGE,"E3.4"),sQuery(id+"F0.wireOp",EDGE,"E3.5")])]}),"instanceName":"1"}),"instanceName":"1"}),"instanceName":"1"}),"instanceName":"1"});
            var Q21;
            Q21=makeQuery(id+"F7.opPattern","COPY",BODY,{"derivedFrom":makeQuery(id+"F5.opPattern","COPY",BODY,{"derivedFrom":makeQuery(id+"F4.opPattern","COPY",BODY,{"derivedFrom":makeQuery(id+"F3.opPattern","COPY",BODY,{"derivedFrom":makeQuery(id+"F1.opExtrude","SWEPT_BODY",BODY,{"disambiguationData":[OSD([sQuery(id+"F0.wireOp",EDGE,"E1.0"),sQuery(id+"F0.wireOp",EDGE,"E1.1"),sQuery(id+"F0.wireOp",EDGE,"E1.2"),sQuery(id+"F0.wireOp",EDGE,"E1.3"),sQuery(id+"F0.wireOp",EDGE,"E1.4"),sQuery(id+"F0.wireOp",EDGE,"E1.5"),sQuery(id+"F0.wireOp",EDGE,"E3.0"),sQuery(id+"F0.wireOp",EDGE,"E3.1"),sQuery(id+"F0.wireOp",EDGE,"E3.2"),sQuery(id+"F0.wireOp",EDGE,"E3.3"),sQuery(id+"F0.wireOp",EDGE,"E3.4"),sQuery(id+"F0.wireOp",EDGE,"E3.5")])]}),"instanceName":"1"}),"instanceName":"1"}),"instanceName":"1"}),"instanceName":"1"});
            var Q22;
            Q22=makeQuery(id+"F7.opPattern","COPY",BODY,{"derivedFrom":makeQuery(id+"F6.opPattern","COPY",BODY,{"derivedFrom":makeQuery(id+"F5.opPattern","COPY",BODY,{"derivedFrom":makeQuery(id+"F4.opPattern","COPY",BODY,{"derivedFrom":makeQuery(id+"F1.opExtrude","SWEPT_BODY",BODY,{"disambiguationData":[OSD([sQuery(id+"F0.wireOp",EDGE,"E1.0"),sQuery(id+"F0.wireOp",EDGE,"E1.1"),sQuery(id+"F0.wireOp",EDGE,"E1.2"),sQuery(id+"F0.wireOp",EDGE,"E1.3"),sQuery(id+"F0.wireOp",EDGE,"E1.4"),sQuery(id+"F0.wireOp",EDGE,"E1.5"),sQuery(id+"F0.wireOp",EDGE,"E3.0"),sQuery(id+"F0.wireOp",EDGE,"E3.1"),sQuery(id+"F0.wireOp",EDGE,"E3.2"),sQuery(id+"F0.wireOp",EDGE,"E3.3"),sQuery(id+"F0.wireOp",EDGE,"E3.4"),sQuery(id+"F0.wireOp",EDGE,"E3.5")])]}),"instanceName":"1"}),"instanceName":"1"}),"instanceName":"1"}),"instanceName":"1"});
            transform(context, id + "F8", {"entities" : qUnion([Q0, Q1, Q2, Q3, Q4, Q5, Q6, Q7, Q8, Q9, Q10, Q11, Q12, Q13, Q14, Q15, Q16, Q17, Q18, Q19, Q20, Q21, Q22]), "transformType" : TransformType.TRANSLATION_3D, "dx" : -4.23 * mm, "dy" : -14.6 * mm, "dz" : 0 * mm, "makeCopy" : true});
        }
        {
            var Q0;
            Q0=makeQuery(id+"F8.opPattern","COPY",BODY,{"derivedFrom":makeQuery(id+"F6.opPattern","COPY",BODY,{"derivedFrom":makeQuery(id+"F1.opExtrude","SWEPT_BODY",BODY,{"disambiguationData":[OSD([sQuery(id+"F0.wireOp",EDGE,"E1.0"),sQuery(id+"F0.wireOp",EDGE,"E1.1"),sQuery(id+"F0.wireOp",EDGE,"E1.2"),sQuery(id+"F0.wireOp",EDGE,"E1.3"),sQuery(id+"F0.wireOp",EDGE,"E1.4"),sQuery(id+"F0.wireOp",EDGE,"E1.5"),sQuery(id+"F0.wireOp",EDGE,"E3.0"),sQuery(id+"F0.wireOp",EDGE,"E3.1"),sQuery(id+"F0.wireOp",EDGE,"E3.2"),sQuery(id+"F0.wireOp",EDGE,"E3.3"),sQuery(id+"F0.wireOp",EDGE,"E3.4"),sQuery(id+"F0.wireOp",EDGE,"E3.5")])]}),"instanceName":"1"}),"instanceName":"1"});
            var Q1;
            Q1=makeQuery(id+"F1.opExtrude","SWEPT_BODY",BODY,{"disambiguationData":[OSD([sQuery(id+"F0.wireOp",EDGE,"E1.0"),sQuery(id+"F0.wireOp",EDGE,"E1.1"),sQuery(id+"F0.wireOp",EDGE,"E1.2"),sQuery(id+"F0.wireOp",EDGE,"E1.3"),sQuery(id+"F0.wireOp",EDGE,"E1.4"),sQuery(id+"F0.wireOp",EDGE,"E1.5"),sQuery(id+"F0.wireOp",EDGE,"E3.0"),sQuery(id+"F0.wireOp",EDGE,"E3.1"),sQuery(id+"F0.wireOp",EDGE,"E3.2"),sQuery(id+"F0.wireOp",EDGE,"E3.3"),sQuery(id+"F0.wireOp",EDGE,"E3.4"),sQuery(id+"F0.wireOp",EDGE,"E3.5")])]});
            var Q2;
            Q2=makeQuery(id+"F8.opPattern","COPY",BODY,{"derivedFrom":makeQuery(id+"F6.opPattern","COPY",BODY,{"derivedFrom":makeQuery(id+"F3.opPattern","COPY",BODY,{"derivedFrom":makeQuery(id+"F1.opExtrude","SWEPT_BODY",BODY,{"disambiguationData":[OSD([sQuery(id+"F0.wireOp",EDGE,"E1.0"),sQuery(id+"F0.wireOp",EDGE,"E1.1"),sQuery(id+"F0.wireOp",EDGE,"E1.2"),sQuery(id+"F0.wireOp",EDGE,"E1.3"),sQuery(id+"F0.wireOp",EDGE,"E1.4"),sQuery(id+"F0.wireOp",EDGE,"E1.5"),sQuery(id+"F0.wireOp",EDGE,"E3.0"),sQuery(id+"F0.wireOp",EDGE,"E3.1"),sQuery(id+"F0.wireOp",EDGE,"E3.2"),sQuery(id+"F0.wireOp",EDGE,"E3.3"),sQuery(id+"F0.wireOp",EDGE,"E3.4"),sQuery(id+"F0.wireOp",EDGE,"E3.5")])]}),"instanceName":"1"}),"instanceName":"1"}),"instanceName":"1"});
            var Q3;
            Q3=makeQuery(id+"F8.opPattern","COPY",BODY,{"derivedFrom":makeQuery(id+"F7.opPattern","COPY",BODY,{"derivedFrom":makeQuery(id+"F4.opPattern","COPY",BODY,{"derivedFrom":makeQuery(id+"F1.opExtrude","SWEPT_BODY",BODY,{"disambiguationData":[OSD([sQuery(id+"F0.wireOp",EDGE,"E1.0"),sQuery(id+"F0.wireOp",EDGE,"E1.1"),sQuery(id+"F0.wireOp",EDGE,"E1.2"),sQuery(id+"F0.wireOp",EDGE,"E1.3"),sQuery(id+"F0.wireOp",EDGE,"E1.4"),sQuery(id+"F0.wireOp",EDGE,"E1.5"),sQuery(id+"F0.wireOp",EDGE,"E3.0"),sQuery(id+"F0.wireOp",EDGE,"E3.1"),sQuery(id+"F0.wireOp",EDGE,"E3.2"),sQuery(id+"F0.wireOp",EDGE,"E3.3"),sQuery(id+"F0.wireOp",EDGE,"E3.4"),sQuery(id+"F0.wireOp",EDGE,"E3.5")])]}),"instanceName":"1"}),"instanceName":"1"}),"instanceName":"1"});
            var Q4;
            Q4=makeQuery(id+"F7.opPattern","COPY",BODY,{"derivedFrom":makeQuery(id+"F6.opPattern","COPY",BODY,{"derivedFrom":makeQuery(id+"F3.opPattern","COPY",BODY,{"derivedFrom":makeQuery(id+"F1.opExtrude","SWEPT_BODY",BODY,{"disambiguationData":[OSD([sQuery(id+"F0.wireOp",EDGE,"E1.0"),sQuery(id+"F0.wireOp",EDGE,"E1.1"),sQuery(id+"F0.wireOp",EDGE,"E1.2"),sQuery(id+"F0.wireOp",EDGE,"E1.3"),sQuery(id+"F0.wireOp",EDGE,"E1.4"),sQuery(id+"F0.wireOp",EDGE,"E1.5"),sQuery(id+"F0.wireOp",EDGE,"E3.0"),sQuery(id+"F0.wireOp",EDGE,"E3.1"),sQuery(id+"F0.wireOp",EDGE,"E3.2"),sQuery(id+"F0.wireOp",EDGE,"E3.3"),sQuery(id+"F0.wireOp",EDGE,"E3.4"),sQuery(id+"F0.wireOp",EDGE,"E3.5")])]}),"instanceName":"1"}),"instanceName":"1"}),"instanceName":"1"});
            var Q5;
            Q5=makeQuery(id+"F8.opPattern","COPY",BODY,{"derivedFrom":makeQuery(id+"F7.opPattern","COPY",BODY,{"derivedFrom":makeQuery(id+"F3.opPattern","COPY",BODY,{"derivedFrom":makeQuery(id+"F1.opExtrude","SWEPT_BODY",BODY,{"disambiguationData":[OSD([sQuery(id+"F0.wireOp",EDGE,"E1.0"),sQuery(id+"F0.wireOp",EDGE,"E1.1"),sQuery(id+"F0.wireOp",EDGE,"E1.2"),sQuery(id+"F0.wireOp",EDGE,"E1.3"),sQuery(id+"F0.wireOp",EDGE,"E1.4"),sQuery(id+"F0.wireOp",EDGE,"E1.5"),sQuery(id+"F0.wireOp",EDGE,"E3.0"),sQuery(id+"F0.wireOp",EDGE,"E3.1"),sQuery(id+"F0.wireOp",EDGE,"E3.2"),sQuery(id+"F0.wireOp",EDGE,"E3.3"),sQuery(id+"F0.wireOp",EDGE,"E3.4"),sQuery(id+"F0.wireOp",EDGE,"E3.5")])]}),"instanceName":"1"}),"instanceName":"1"}),"instanceName":"1"});
            var Q6;
            Q6=makeQuery(id+"F8.opPattern","COPY",BODY,{"derivedFrom":makeQuery(id+"F6.opPattern","COPY",BODY,{"derivedFrom":makeQuery(id+"F4.opPattern","COPY",BODY,{"derivedFrom":makeQuery(id+"F3.opPattern","COPY",BODY,{"derivedFrom":makeQuery(id+"F1.opExtrude","SWEPT_BODY",BODY,{"disambiguationData":[OSD([sQuery(id+"F0.wireOp",EDGE,"E1.0"),sQuery(id+"F0.wireOp",EDGE,"E1.1"),sQuery(id+"F0.wireOp",EDGE,"E1.2"),sQuery(id+"F0.wireOp",EDGE,"E1.3"),sQuery(id+"F0.wireOp",EDGE,"E1.4"),sQuery(id+"F0.wireOp",EDGE,"E1.5"),sQuery(id+"F0.wireOp",EDGE,"E3.0"),sQuery(id+"F0.wireOp",EDGE,"E3.1"),sQuery(id+"F0.wireOp",EDGE,"E3.2"),sQuery(id+"F0.wireOp",EDGE,"E3.3"),sQuery(id+"F0.wireOp",EDGE,"E3.4"),sQuery(id+"F0.wireOp",EDGE,"E3.5")])]}),"instanceName":"1"}),"instanceName":"1"}),"instanceName":"1"}),"instanceName":"1"});
            var Q7;
            Q7=makeQuery(id+"F8.opPattern","COPY",BODY,{"derivedFrom":makeQuery(id+"F7.opPattern","COPY",BODY,{"derivedFrom":makeQuery(id+"F1.opExtrude","SWEPT_BODY",BODY,{"disambiguationData":[OSD([sQuery(id+"F0.wireOp",EDGE,"E1.0"),sQuery(id+"F0.wireOp",EDGE,"E1.1"),sQuery(id+"F0.wireOp",EDGE,"E1.2"),sQuery(id+"F0.wireOp",EDGE,"E1.3"),sQuery(id+"F0.wireOp",EDGE,"E1.4"),sQuery(id+"F0.wireOp",EDGE,"E1.5"),sQuery(id+"F0.wireOp",EDGE,"E3.0"),sQuery(id+"F0.wireOp",EDGE,"E3.1"),sQuery(id+"F0.wireOp",EDGE,"E3.2"),sQuery(id+"F0.wireOp",EDGE,"E3.3"),sQuery(id+"F0.wireOp",EDGE,"E3.4"),sQuery(id+"F0.wireOp",EDGE,"E3.5")])]}),"instanceName":"1"}),"instanceName":"1"});
            var Q8;
            Q8=makeQuery(id+"F8.opPattern","COPY",BODY,{"derivedFrom":makeQuery(id+"F7.opPattern","COPY",BODY,{"derivedFrom":makeQuery(id+"F6.opPattern","COPY",BODY,{"derivedFrom":makeQuery(id+"F1.opExtrude","SWEPT_BODY",BODY,{"disambiguationData":[OSD([sQuery(id+"F0.wireOp",EDGE,"E1.0"),sQuery(id+"F0.wireOp",EDGE,"E1.1"),sQuery(id+"F0.wireOp",EDGE,"E1.2"),sQuery(id+"F0.wireOp",EDGE,"E1.3"),sQuery(id+"F0.wireOp",EDGE,"E1.4"),sQuery(id+"F0.wireOp",EDGE,"E1.5"),sQuery(id+"F0.wireOp",EDGE,"E3.0"),sQuery(id+"F0.wireOp",EDGE,"E3.1"),sQuery(id+"F0.wireOp",EDGE,"E3.2"),sQuery(id+"F0.wireOp",EDGE,"E3.3"),sQuery(id+"F0.wireOp",EDGE,"E3.4"),sQuery(id+"F0.wireOp",EDGE,"E3.5")])]}),"instanceName":"1"}),"instanceName":"1"}),"instanceName":"1"});
            var Q9;
            Q9=makeQuery(id+"F7.opPattern","COPY",BODY,{"derivedFrom":makeQuery(id+"F6.opPattern","COPY",BODY,{"derivedFrom":makeQuery(id+"F1.opExtrude","SWEPT_BODY",BODY,{"disambiguationData":[OSD([sQuery(id+"F0.wireOp",EDGE,"E1.0"),sQuery(id+"F0.wireOp",EDGE,"E1.1"),sQuery(id+"F0.wireOp",EDGE,"E1.2"),sQuery(id+"F0.wireOp",EDGE,"E1.3"),sQuery(id+"F0.wireOp",EDGE,"E1.4"),sQuery(id+"F0.wireOp",EDGE,"E1.5"),sQuery(id+"F0.wireOp",EDGE,"E3.0"),sQuery(id+"F0.wireOp",EDGE,"E3.1"),sQuery(id+"F0.wireOp",EDGE,"E3.2"),sQuery(id+"F0.wireOp",EDGE,"E3.3"),sQuery(id+"F0.wireOp",EDGE,"E3.4"),sQuery(id+"F0.wireOp",EDGE,"E3.5")])]}),"instanceName":"1"}),"instanceName":"1"});
            var Q10;
            Q10=makeQuery(id+"F7.opPattern","COPY",BODY,{"derivedFrom":makeQuery(id+"F3.opPattern","COPY",BODY,{"derivedFrom":makeQuery(id+"F1.opExtrude","SWEPT_BODY",BODY,{"disambiguationData":[OSD([sQuery(id+"F0.wireOp",EDGE,"E1.0"),sQuery(id+"F0.wireOp",EDGE,"E1.1"),sQuery(id+"F0.wireOp",EDGE,"E1.2"),sQuery(id+"F0.wireOp",EDGE,"E1.3"),sQuery(id+"F0.wireOp",EDGE,"E1.4"),sQuery(id+"F0.wireOp",EDGE,"E1.5"),sQuery(id+"F0.wireOp",EDGE,"E3.0"),sQuery(id+"F0.wireOp",EDGE,"E3.1"),sQuery(id+"F0.wireOp",EDGE,"E3.2"),sQuery(id+"F0.wireOp",EDGE,"E3.3"),sQuery(id+"F0.wireOp",EDGE,"E3.4"),sQuery(id+"F0.wireOp",EDGE,"E3.5")])]}),"instanceName":"1"}),"instanceName":"1"});
            var Q11;
            Q11=makeQuery(id+"F7.opPattern","COPY",BODY,{"derivedFrom":makeQuery(id+"F1.opExtrude","SWEPT_BODY",BODY,{"disambiguationData":[OSD([sQuery(id+"F0.wireOp",EDGE,"E1.0"),sQuery(id+"F0.wireOp",EDGE,"E1.1"),sQuery(id+"F0.wireOp",EDGE,"E1.2"),sQuery(id+"F0.wireOp",EDGE,"E1.3"),sQuery(id+"F0.wireOp",EDGE,"E1.4"),sQuery(id+"F0.wireOp",EDGE,"E1.5"),sQuery(id+"F0.wireOp",EDGE,"E3.0"),sQuery(id+"F0.wireOp",EDGE,"E3.1"),sQuery(id+"F0.wireOp",EDGE,"E3.2"),sQuery(id+"F0.wireOp",EDGE,"E3.3"),sQuery(id+"F0.wireOp",EDGE,"E3.4"),sQuery(id+"F0.wireOp",EDGE,"E3.5")])]}),"instanceName":"1"});
            var Q12;
            Q12=makeQuery(id+"F6.opPattern","COPY",BODY,{"derivedFrom":makeQuery(id+"F4.opPattern","COPY",BODY,{"derivedFrom":makeQuery(id+"F1.opExtrude","SWEPT_BODY",BODY,{"disambiguationData":[OSD([sQuery(id+"F0.wireOp",EDGE,"E1.0"),sQuery(id+"F0.wireOp",EDGE,"E1.1"),sQuery(id+"F0.wireOp",EDGE,"E1.2"),sQuery(id+"F0.wireOp",EDGE,"E1.3"),sQuery(id+"F0.wireOp",EDGE,"E1.4"),sQuery(id+"F0.wireOp",EDGE,"E1.5"),sQuery(id+"F0.wireOp",EDGE,"E3.0"),sQuery(id+"F0.wireOp",EDGE,"E3.1"),sQuery(id+"F0.wireOp",EDGE,"E3.2"),sQuery(id+"F0.wireOp",EDGE,"E3.3"),sQuery(id+"F0.wireOp",EDGE,"E3.4"),sQuery(id+"F0.wireOp",EDGE,"E3.5")])]}),"instanceName":"1"}),"instanceName":"1"});
            var Q13;
            Q13=makeQuery(id+"F6.opPattern","COPY",BODY,{"derivedFrom":makeQuery(id+"F3.opPattern","COPY",BODY,{"derivedFrom":makeQuery(id+"F1.opExtrude","SWEPT_BODY",BODY,{"disambiguationData":[OSD([sQuery(id+"F0.wireOp",EDGE,"E1.0"),sQuery(id+"F0.wireOp",EDGE,"E1.1"),sQuery(id+"F0.wireOp",EDGE,"E1.2"),sQuery(id+"F0.wireOp",EDGE,"E1.3"),sQuery(id+"F0.wireOp",EDGE,"E1.4"),sQuery(id+"F0.wireOp",EDGE,"E1.5"),sQuery(id+"F0.wireOp",EDGE,"E3.0"),sQuery(id+"F0.wireOp",EDGE,"E3.1"),sQuery(id+"F0.wireOp",EDGE,"E3.2"),sQuery(id+"F0.wireOp",EDGE,"E3.3"),sQuery(id+"F0.wireOp",EDGE,"E3.4"),sQuery(id+"F0.wireOp",EDGE,"E3.5")])]}),"instanceName":"1"}),"instanceName":"1"});
            var Q14;
            Q14=makeQuery(id+"F6.opPattern","COPY",BODY,{"derivedFrom":makeQuery(id+"F1.opExtrude","SWEPT_BODY",BODY,{"disambiguationData":[OSD([sQuery(id+"F0.wireOp",EDGE,"E1.0"),sQuery(id+"F0.wireOp",EDGE,"E1.1"),sQuery(id+"F0.wireOp",EDGE,"E1.2"),sQuery(id+"F0.wireOp",EDGE,"E1.3"),sQuery(id+"F0.wireOp",EDGE,"E1.4"),sQuery(id+"F0.wireOp",EDGE,"E1.5"),sQuery(id+"F0.wireOp",EDGE,"E3.0"),sQuery(id+"F0.wireOp",EDGE,"E3.1"),sQuery(id+"F0.wireOp",EDGE,"E3.2"),sQuery(id+"F0.wireOp",EDGE,"E3.3"),sQuery(id+"F0.wireOp",EDGE,"E3.4"),sQuery(id+"F0.wireOp",EDGE,"E3.5")])]}),"instanceName":"1"});
            var Q15;
            Q15=makeQuery(id+"F4.opPattern","COPY",BODY,{"derivedFrom":makeQuery(id+"F1.opExtrude","SWEPT_BODY",BODY,{"disambiguationData":[OSD([sQuery(id+"F0.wireOp",EDGE,"E1.0"),sQuery(id+"F0.wireOp",EDGE,"E1.1"),sQuery(id+"F0.wireOp",EDGE,"E1.2"),sQuery(id+"F0.wireOp",EDGE,"E1.3"),sQuery(id+"F0.wireOp",EDGE,"E1.4"),sQuery(id+"F0.wireOp",EDGE,"E1.5"),sQuery(id+"F0.wireOp",EDGE,"E3.0"),sQuery(id+"F0.wireOp",EDGE,"E3.1"),sQuery(id+"F0.wireOp",EDGE,"E3.2"),sQuery(id+"F0.wireOp",EDGE,"E3.3"),sQuery(id+"F0.wireOp",EDGE,"E3.4"),sQuery(id+"F0.wireOp",EDGE,"E3.5")])]}),"instanceName":"1"});
            var Q16;
            Q16=makeQuery(id+"F3.opPattern","COPY",BODY,{"derivedFrom":makeQuery(id+"F1.opExtrude","SWEPT_BODY",BODY,{"disambiguationData":[OSD([sQuery(id+"F0.wireOp",EDGE,"E1.0"),sQuery(id+"F0.wireOp",EDGE,"E1.1"),sQuery(id+"F0.wireOp",EDGE,"E1.2"),sQuery(id+"F0.wireOp",EDGE,"E1.3"),sQuery(id+"F0.wireOp",EDGE,"E1.4"),sQuery(id+"F0.wireOp",EDGE,"E1.5"),sQuery(id+"F0.wireOp",EDGE,"E3.0"),sQuery(id+"F0.wireOp",EDGE,"E3.1"),sQuery(id+"F0.wireOp",EDGE,"E3.2"),sQuery(id+"F0.wireOp",EDGE,"E3.3"),sQuery(id+"F0.wireOp",EDGE,"E3.4"),sQuery(id+"F0.wireOp",EDGE,"E3.5")])]}),"instanceName":"1"});
            var Q17;
            Q17=makeQuery(id+"F8.opPattern","COPY",BODY,{"derivedFrom":makeQuery(id+"F7.opPattern","COPY",BODY,{"derivedFrom":makeQuery(id+"F6.opPattern","COPY",BODY,{"derivedFrom":makeQuery(id+"F3.opPattern","COPY",BODY,{"derivedFrom":makeQuery(id+"F1.opExtrude","SWEPT_BODY",BODY,{"disambiguationData":[OSD([sQuery(id+"F0.wireOp",EDGE,"E1.0"),sQuery(id+"F0.wireOp",EDGE,"E1.1"),sQuery(id+"F0.wireOp",EDGE,"E1.2"),sQuery(id+"F0.wireOp",EDGE,"E1.3"),sQuery(id+"F0.wireOp",EDGE,"E1.4"),sQuery(id+"F0.wireOp",EDGE,"E1.5"),sQuery(id+"F0.wireOp",EDGE,"E3.0"),sQuery(id+"F0.wireOp",EDGE,"E3.1"),sQuery(id+"F0.wireOp",EDGE,"E3.2"),sQuery(id+"F0.wireOp",EDGE,"E3.3"),sQuery(id+"F0.wireOp",EDGE,"E3.4"),sQuery(id+"F0.wireOp",EDGE,"E3.5")])]}),"instanceName":"1"}),"instanceName":"1"}),"instanceName":"1"}),"instanceName":"1"});
            var Q18;
            Q18=makeQuery(id+"F8.opPattern","COPY",BODY,{"derivedFrom":makeQuery(id+"F6.opPattern","COPY",BODY,{"derivedFrom":makeQuery(id+"F4.opPattern","COPY",BODY,{"derivedFrom":makeQuery(id+"F1.opExtrude","SWEPT_BODY",BODY,{"disambiguationData":[OSD([sQuery(id+"F0.wireOp",EDGE,"E1.0"),sQuery(id+"F0.wireOp",EDGE,"E1.1"),sQuery(id+"F0.wireOp",EDGE,"E1.2"),sQuery(id+"F0.wireOp",EDGE,"E1.3"),sQuery(id+"F0.wireOp",EDGE,"E1.4"),sQuery(id+"F0.wireOp",EDGE,"E1.5"),sQuery(id+"F0.wireOp",EDGE,"E3.0"),sQuery(id+"F0.wireOp",EDGE,"E3.1"),sQuery(id+"F0.wireOp",EDGE,"E3.2"),sQuery(id+"F0.wireOp",EDGE,"E3.3"),sQuery(id+"F0.wireOp",EDGE,"E3.4"),sQuery(id+"F0.wireOp",EDGE,"E3.5")])]}),"instanceName":"1"}),"instanceName":"1"}),"instanceName":"1"});
            var Q19;
            Q19=makeQuery(id+"F8.opPattern","COPY",BODY,{"derivedFrom":makeQuery(id+"F7.opPattern","COPY",BODY,{"derivedFrom":makeQuery(id+"F6.opPattern","COPY",BODY,{"derivedFrom":makeQuery(id+"F4.opPattern","COPY",BODY,{"derivedFrom":makeQuery(id+"F1.opExtrude","SWEPT_BODY",BODY,{"disambiguationData":[OSD([sQuery(id+"F0.wireOp",EDGE,"E1.0"),sQuery(id+"F0.wireOp",EDGE,"E1.1"),sQuery(id+"F0.wireOp",EDGE,"E1.2"),sQuery(id+"F0.wireOp",EDGE,"E1.3"),sQuery(id+"F0.wireOp",EDGE,"E1.4"),sQuery(id+"F0.wireOp",EDGE,"E1.5"),sQuery(id+"F0.wireOp",EDGE,"E3.0"),sQuery(id+"F0.wireOp",EDGE,"E3.1"),sQuery(id+"F0.wireOp",EDGE,"E3.2"),sQuery(id+"F0.wireOp",EDGE,"E3.3"),sQuery(id+"F0.wireOp",EDGE,"E3.4"),sQuery(id+"F0.wireOp",EDGE,"E3.5")])]}),"instanceName":"1"}),"instanceName":"1"}),"instanceName":"1"}),"instanceName":"1"});
            var Q20;
            Q20=makeQuery(id+"F8.opPattern","COPY",BODY,{"derivedFrom":makeQuery(id+"F1.opExtrude","SWEPT_BODY",BODY,{"disambiguationData":[OSD([sQuery(id+"F0.wireOp",EDGE,"E1.0"),sQuery(id+"F0.wireOp",EDGE,"E1.1"),sQuery(id+"F0.wireOp",EDGE,"E1.2"),sQuery(id+"F0.wireOp",EDGE,"E1.3"),sQuery(id+"F0.wireOp",EDGE,"E1.4"),sQuery(id+"F0.wireOp",EDGE,"E1.5"),sQuery(id+"F0.wireOp",EDGE,"E3.0"),sQuery(id+"F0.wireOp",EDGE,"E3.1"),sQuery(id+"F0.wireOp",EDGE,"E3.2"),sQuery(id+"F0.wireOp",EDGE,"E3.3"),sQuery(id+"F0.wireOp",EDGE,"E3.4"),sQuery(id+"F0.wireOp",EDGE,"E3.5")])]}),"instanceName":"1"});
            var Q21;
            Q21=makeQuery(id+"F8.opPattern","COPY",BODY,{"derivedFrom":makeQuery(id+"F3.opPattern","COPY",BODY,{"derivedFrom":makeQuery(id+"F1.opExtrude","SWEPT_BODY",BODY,{"disambiguationData":[OSD([sQuery(id+"F0.wireOp",EDGE,"E1.0"),sQuery(id+"F0.wireOp",EDGE,"E1.1"),sQuery(id+"F0.wireOp",EDGE,"E1.2"),sQuery(id+"F0.wireOp",EDGE,"E1.3"),sQuery(id+"F0.wireOp",EDGE,"E1.4"),sQuery(id+"F0.wireOp",EDGE,"E1.5"),sQuery(id+"F0.wireOp",EDGE,"E3.0"),sQuery(id+"F0.wireOp",EDGE,"E3.1"),sQuery(id+"F0.wireOp",EDGE,"E3.2"),sQuery(id+"F0.wireOp",EDGE,"E3.3"),sQuery(id+"F0.wireOp",EDGE,"E3.4"),sQuery(id+"F0.wireOp",EDGE,"E3.5")])]}),"instanceName":"1"}),"instanceName":"1"});
            var Q22;
            Q22=makeQuery(id+"F8.opPattern","COPY",BODY,{"derivedFrom":makeQuery(id+"F4.opPattern","COPY",BODY,{"derivedFrom":makeQuery(id+"F1.opExtrude","SWEPT_BODY",BODY,{"disambiguationData":[OSD([sQuery(id+"F0.wireOp",EDGE,"E1.0"),sQuery(id+"F0.wireOp",EDGE,"E1.1"),sQuery(id+"F0.wireOp",EDGE,"E1.2"),sQuery(id+"F0.wireOp",EDGE,"E1.3"),sQuery(id+"F0.wireOp",EDGE,"E1.4"),sQuery(id+"F0.wireOp",EDGE,"E1.5"),sQuery(id+"F0.wireOp",EDGE,"E3.0"),sQuery(id+"F0.wireOp",EDGE,"E3.1"),sQuery(id+"F0.wireOp",EDGE,"E3.2"),sQuery(id+"F0.wireOp",EDGE,"E3.3"),sQuery(id+"F0.wireOp",EDGE,"E3.4"),sQuery(id+"F0.wireOp",EDGE,"E3.5")])]}),"instanceName":"1"}),"instanceName":"1"});
            var Q23;
            Q23=makeQuery(id+"F8.opPattern","COPY",BODY,{"derivedFrom":makeQuery(id+"F4.opPattern","COPY",BODY,{"derivedFrom":makeQuery(id+"F3.opPattern","COPY",BODY,{"derivedFrom":makeQuery(id+"F1.opExtrude","SWEPT_BODY",BODY,{"disambiguationData":[OSD([sQuery(id+"F0.wireOp",EDGE,"E1.0"),sQuery(id+"F0.wireOp",EDGE,"E1.1"),sQuery(id+"F0.wireOp",EDGE,"E1.2"),sQuery(id+"F0.wireOp",EDGE,"E1.3"),sQuery(id+"F0.wireOp",EDGE,"E1.4"),sQuery(id+"F0.wireOp",EDGE,"E1.5"),sQuery(id+"F0.wireOp",EDGE,"E3.0"),sQuery(id+"F0.wireOp",EDGE,"E3.1"),sQuery(id+"F0.wireOp",EDGE,"E3.2"),sQuery(id+"F0.wireOp",EDGE,"E3.3"),sQuery(id+"F0.wireOp",EDGE,"E3.4"),sQuery(id+"F0.wireOp",EDGE,"E3.5")])]}),"instanceName":"1"}),"instanceName":"1"}),"instanceName":"1"});
            var Q24;
            Q24=makeQuery(id+"F8.opPattern","COPY",BODY,{"derivedFrom":makeQuery(id+"F5.opPattern","COPY",BODY,{"derivedFrom":makeQuery(id+"F4.opPattern","COPY",BODY,{"derivedFrom":makeQuery(id+"F3.opPattern","COPY",BODY,{"derivedFrom":makeQuery(id+"F1.opExtrude","SWEPT_BODY",BODY,{"disambiguationData":[OSD([sQuery(id+"F0.wireOp",EDGE,"E1.0"),sQuery(id+"F0.wireOp",EDGE,"E1.1"),sQuery(id+"F0.wireOp",EDGE,"E1.2"),sQuery(id+"F0.wireOp",EDGE,"E1.3"),sQuery(id+"F0.wireOp",EDGE,"E1.4"),sQuery(id+"F0.wireOp",EDGE,"E1.5"),sQuery(id+"F0.wireOp",EDGE,"E3.0"),sQuery(id+"F0.wireOp",EDGE,"E3.1"),sQuery(id+"F0.wireOp",EDGE,"E3.2"),sQuery(id+"F0.wireOp",EDGE,"E3.3"),sQuery(id+"F0.wireOp",EDGE,"E3.4"),sQuery(id+"F0.wireOp",EDGE,"E3.5")])]}),"instanceName":"1"}),"instanceName":"1"}),"instanceName":"1"}),"instanceName":"1"});
            var Q25;
            Q25=makeQuery(id+"F7.opPattern","COPY",BODY,{"derivedFrom":makeQuery(id+"F6.opPattern","COPY",BODY,{"derivedFrom":makeQuery(id+"F5.opPattern","COPY",BODY,{"derivedFrom":makeQuery(id+"F4.opPattern","COPY",BODY,{"derivedFrom":makeQuery(id+"F3.opPattern","COPY",BODY,{"derivedFrom":makeQuery(id+"F1.opExtrude","SWEPT_BODY",BODY,{"disambiguationData":[OSD([sQuery(id+"F0.wireOp",EDGE,"E1.0"),sQuery(id+"F0.wireOp",EDGE,"E1.1"),sQuery(id+"F0.wireOp",EDGE,"E1.2"),sQuery(id+"F0.wireOp",EDGE,"E1.3"),sQuery(id+"F0.wireOp",EDGE,"E1.4"),sQuery(id+"F0.wireOp",EDGE,"E1.5"),sQuery(id+"F0.wireOp",EDGE,"E3.0"),sQuery(id+"F0.wireOp",EDGE,"E3.1"),sQuery(id+"F0.wireOp",EDGE,"E3.2"),sQuery(id+"F0.wireOp",EDGE,"E3.3"),sQuery(id+"F0.wireOp",EDGE,"E3.4"),sQuery(id+"F0.wireOp",EDGE,"E3.5")])]}),"instanceName":"1"}),"instanceName":"1"}),"instanceName":"1"}),"instanceName":"1"}),"instanceName":"1"});
            var Q26;
            Q26=makeQuery(id+"F8.opPattern","COPY",BODY,{"derivedFrom":makeQuery(id+"F7.opPattern","COPY",BODY,{"derivedFrom":makeQuery(id+"F4.opPattern","COPY",BODY,{"derivedFrom":makeQuery(id+"F3.opPattern","COPY",BODY,{"derivedFrom":makeQuery(id+"F1.opExtrude","SWEPT_BODY",BODY,{"disambiguationData":[OSD([sQuery(id+"F0.wireOp",EDGE,"E1.0"),sQuery(id+"F0.wireOp",EDGE,"E1.1"),sQuery(id+"F0.wireOp",EDGE,"E1.2"),sQuery(id+"F0.wireOp",EDGE,"E1.3"),sQuery(id+"F0.wireOp",EDGE,"E1.4"),sQuery(id+"F0.wireOp",EDGE,"E1.5"),sQuery(id+"F0.wireOp",EDGE,"E3.0"),sQuery(id+"F0.wireOp",EDGE,"E3.1"),sQuery(id+"F0.wireOp",EDGE,"E3.2"),sQuery(id+"F0.wireOp",EDGE,"E3.3"),sQuery(id+"F0.wireOp",EDGE,"E3.4"),sQuery(id+"F0.wireOp",EDGE,"E3.5")])]}),"instanceName":"1"}),"instanceName":"1"}),"instanceName":"1"}),"instanceName":"1"});
            var Q27;
            Q27=makeQuery(id+"F7.opPattern","COPY",BODY,{"derivedFrom":makeQuery(id+"F6.opPattern","COPY",BODY,{"derivedFrom":makeQuery(id+"F4.opPattern","COPY",BODY,{"derivedFrom":makeQuery(id+"F1.opExtrude","SWEPT_BODY",BODY,{"disambiguationData":[OSD([sQuery(id+"F0.wireOp",EDGE,"E1.0"),sQuery(id+"F0.wireOp",EDGE,"E1.1"),sQuery(id+"F0.wireOp",EDGE,"E1.2"),sQuery(id+"F0.wireOp",EDGE,"E1.3"),sQuery(id+"F0.wireOp",EDGE,"E1.4"),sQuery(id+"F0.wireOp",EDGE,"E1.5"),sQuery(id+"F0.wireOp",EDGE,"E3.0"),sQuery(id+"F0.wireOp",EDGE,"E3.1"),sQuery(id+"F0.wireOp",EDGE,"E3.2"),sQuery(id+"F0.wireOp",EDGE,"E3.3"),sQuery(id+"F0.wireOp",EDGE,"E3.4"),sQuery(id+"F0.wireOp",EDGE,"E3.5")])]}),"instanceName":"1"}),"instanceName":"1"}),"instanceName":"1"});
            var Q28;
            Q28=makeQuery(id+"F7.opPattern","COPY",BODY,{"derivedFrom":makeQuery(id+"F6.opPattern","COPY",BODY,{"derivedFrom":makeQuery(id+"F4.opPattern","COPY",BODY,{"derivedFrom":makeQuery(id+"F3.opPattern","COPY",BODY,{"derivedFrom":makeQuery(id+"F1.opExtrude","SWEPT_BODY",BODY,{"disambiguationData":[OSD([sQuery(id+"F0.wireOp",EDGE,"E1.0"),sQuery(id+"F0.wireOp",EDGE,"E1.1"),sQuery(id+"F0.wireOp",EDGE,"E1.2"),sQuery(id+"F0.wireOp",EDGE,"E1.3"),sQuery(id+"F0.wireOp",EDGE,"E1.4"),sQuery(id+"F0.wireOp",EDGE,"E1.5"),sQuery(id+"F0.wireOp",EDGE,"E3.0"),sQuery(id+"F0.wireOp",EDGE,"E3.1"),sQuery(id+"F0.wireOp",EDGE,"E3.2"),sQuery(id+"F0.wireOp",EDGE,"E3.3"),sQuery(id+"F0.wireOp",EDGE,"E3.4"),sQuery(id+"F0.wireOp",EDGE,"E3.5")])]}),"instanceName":"1"}),"instanceName":"1"}),"instanceName":"1"}),"instanceName":"1"});
            var Q29;
            Q29=makeQuery(id+"F7.opPattern","COPY",BODY,{"derivedFrom":makeQuery(id+"F6.opPattern","COPY",BODY,{"derivedFrom":makeQuery(id+"F5.opPattern","COPY",BODY,{"derivedFrom":makeQuery(id+"F4.opPattern","COPY",BODY,{"derivedFrom":makeQuery(id+"F1.opExtrude","SWEPT_BODY",BODY,{"disambiguationData":[OSD([sQuery(id+"F0.wireOp",EDGE,"E1.0"),sQuery(id+"F0.wireOp",EDGE,"E1.1"),sQuery(id+"F0.wireOp",EDGE,"E1.2"),sQuery(id+"F0.wireOp",EDGE,"E1.3"),sQuery(id+"F0.wireOp",EDGE,"E1.4"),sQuery(id+"F0.wireOp",EDGE,"E1.5"),sQuery(id+"F0.wireOp",EDGE,"E3.0"),sQuery(id+"F0.wireOp",EDGE,"E3.1"),sQuery(id+"F0.wireOp",EDGE,"E3.2"),sQuery(id+"F0.wireOp",EDGE,"E3.3"),sQuery(id+"F0.wireOp",EDGE,"E3.4"),sQuery(id+"F0.wireOp",EDGE,"E3.5")])]}),"instanceName":"1"}),"instanceName":"1"}),"instanceName":"1"}),"instanceName":"1"});
            var Q30;
            Q30=makeQuery(id+"F8.opPattern","COPY",BODY,{"derivedFrom":makeQuery(id+"F6.opPattern","COPY",BODY,{"derivedFrom":makeQuery(id+"F5.opPattern","COPY",BODY,{"derivedFrom":makeQuery(id+"F4.opPattern","COPY",BODY,{"derivedFrom":makeQuery(id+"F3.opPattern","COPY",BODY,{"derivedFrom":makeQuery(id+"F1.opExtrude","SWEPT_BODY",BODY,{"disambiguationData":[OSD([sQuery(id+"F0.wireOp",EDGE,"E1.0"),sQuery(id+"F0.wireOp",EDGE,"E1.1"),sQuery(id+"F0.wireOp",EDGE,"E1.2"),sQuery(id+"F0.wireOp",EDGE,"E1.3"),sQuery(id+"F0.wireOp",EDGE,"E1.4"),sQuery(id+"F0.wireOp",EDGE,"E1.5"),sQuery(id+"F0.wireOp",EDGE,"E3.0"),sQuery(id+"F0.wireOp",EDGE,"E3.1"),sQuery(id+"F0.wireOp",EDGE,"E3.2"),sQuery(id+"F0.wireOp",EDGE,"E3.3"),sQuery(id+"F0.wireOp",EDGE,"E3.4"),sQuery(id+"F0.wireOp",EDGE,"E3.5")])]}),"instanceName":"1"}),"instanceName":"1"}),"instanceName":"1"}),"instanceName":"1"}),"instanceName":"1"});
            var Q31;
            Q31=makeQuery(id+"F7.opPattern","COPY",BODY,{"derivedFrom":makeQuery(id+"F5.opPattern","COPY",BODY,{"derivedFrom":makeQuery(id+"F4.opPattern","COPY",BODY,{"derivedFrom":makeQuery(id+"F1.opExtrude","SWEPT_BODY",BODY,{"disambiguationData":[OSD([sQuery(id+"F0.wireOp",EDGE,"E1.0"),sQuery(id+"F0.wireOp",EDGE,"E1.1"),sQuery(id+"F0.wireOp",EDGE,"E1.2"),sQuery(id+"F0.wireOp",EDGE,"E1.3"),sQuery(id+"F0.wireOp",EDGE,"E1.4"),sQuery(id+"F0.wireOp",EDGE,"E1.5"),sQuery(id+"F0.wireOp",EDGE,"E3.0"),sQuery(id+"F0.wireOp",EDGE,"E3.1"),sQuery(id+"F0.wireOp",EDGE,"E3.2"),sQuery(id+"F0.wireOp",EDGE,"E3.3"),sQuery(id+"F0.wireOp",EDGE,"E3.4"),sQuery(id+"F0.wireOp",EDGE,"E3.5")])]}),"instanceName":"1"}),"instanceName":"1"}),"instanceName":"1"});
            var Q32;
            Q32=makeQuery(id+"F7.opPattern","COPY",BODY,{"derivedFrom":makeQuery(id+"F4.opPattern","COPY",BODY,{"derivedFrom":makeQuery(id+"F3.opPattern","COPY",BODY,{"derivedFrom":makeQuery(id+"F1.opExtrude","SWEPT_BODY",BODY,{"disambiguationData":[OSD([sQuery(id+"F0.wireOp",EDGE,"E1.0"),sQuery(id+"F0.wireOp",EDGE,"E1.1"),sQuery(id+"F0.wireOp",EDGE,"E1.2"),sQuery(id+"F0.wireOp",EDGE,"E1.3"),sQuery(id+"F0.wireOp",EDGE,"E1.4"),sQuery(id+"F0.wireOp",EDGE,"E1.5"),sQuery(id+"F0.wireOp",EDGE,"E3.0"),sQuery(id+"F0.wireOp",EDGE,"E3.1"),sQuery(id+"F0.wireOp",EDGE,"E3.2"),sQuery(id+"F0.wireOp",EDGE,"E3.3"),sQuery(id+"F0.wireOp",EDGE,"E3.4"),sQuery(id+"F0.wireOp",EDGE,"E3.5")])]}),"instanceName":"1"}),"instanceName":"1"}),"instanceName":"1"});
            var Q33;
            Q33=makeQuery(id+"F8.opPattern","COPY",BODY,{"derivedFrom":makeQuery(id+"F5.opPattern","COPY",BODY,{"derivedFrom":makeQuery(id+"F4.opPattern","COPY",BODY,{"derivedFrom":makeQuery(id+"F1.opExtrude","SWEPT_BODY",BODY,{"disambiguationData":[OSD([sQuery(id+"F0.wireOp",EDGE,"E1.0"),sQuery(id+"F0.wireOp",EDGE,"E1.1"),sQuery(id+"F0.wireOp",EDGE,"E1.2"),sQuery(id+"F0.wireOp",EDGE,"E1.3"),sQuery(id+"F0.wireOp",EDGE,"E1.4"),sQuery(id+"F0.wireOp",EDGE,"E1.5"),sQuery(id+"F0.wireOp",EDGE,"E3.0"),sQuery(id+"F0.wireOp",EDGE,"E3.1"),sQuery(id+"F0.wireOp",EDGE,"E3.2"),sQuery(id+"F0.wireOp",EDGE,"E3.3"),sQuery(id+"F0.wireOp",EDGE,"E3.4"),sQuery(id+"F0.wireOp",EDGE,"E3.5")])]}),"instanceName":"1"}),"instanceName":"1"}),"instanceName":"1"});
            var Q34;
            Q34=makeQuery(id+"F7.opPattern","COPY",BODY,{"derivedFrom":makeQuery(id+"F5.opPattern","COPY",BODY,{"derivedFrom":makeQuery(id+"F4.opPattern","COPY",BODY,{"derivedFrom":makeQuery(id+"F3.opPattern","COPY",BODY,{"derivedFrom":makeQuery(id+"F1.opExtrude","SWEPT_BODY",BODY,{"disambiguationData":[OSD([sQuery(id+"F0.wireOp",EDGE,"E1.0"),sQuery(id+"F0.wireOp",EDGE,"E1.1"),sQuery(id+"F0.wireOp",EDGE,"E1.2"),sQuery(id+"F0.wireOp",EDGE,"E1.3"),sQuery(id+"F0.wireOp",EDGE,"E1.4"),sQuery(id+"F0.wireOp",EDGE,"E1.5"),sQuery(id+"F0.wireOp",EDGE,"E3.0"),sQuery(id+"F0.wireOp",EDGE,"E3.1"),sQuery(id+"F0.wireOp",EDGE,"E3.2"),sQuery(id+"F0.wireOp",EDGE,"E3.3"),sQuery(id+"F0.wireOp",EDGE,"E3.4"),sQuery(id+"F0.wireOp",EDGE,"E3.5")])]}),"instanceName":"1"}),"instanceName":"1"}),"instanceName":"1"}),"instanceName":"1"});
            var Q35;
            Q35=makeQuery(id+"F7.opPattern","COPY",BODY,{"derivedFrom":makeQuery(id+"F4.opPattern","COPY",BODY,{"derivedFrom":makeQuery(id+"F1.opExtrude","SWEPT_BODY",BODY,{"disambiguationData":[OSD([sQuery(id+"F0.wireOp",EDGE,"E1.0"),sQuery(id+"F0.wireOp",EDGE,"E1.1"),sQuery(id+"F0.wireOp",EDGE,"E1.2"),sQuery(id+"F0.wireOp",EDGE,"E1.3"),sQuery(id+"F0.wireOp",EDGE,"E1.4"),sQuery(id+"F0.wireOp",EDGE,"E1.5"),sQuery(id+"F0.wireOp",EDGE,"E3.0"),sQuery(id+"F0.wireOp",EDGE,"E3.1"),sQuery(id+"F0.wireOp",EDGE,"E3.2"),sQuery(id+"F0.wireOp",EDGE,"E3.3"),sQuery(id+"F0.wireOp",EDGE,"E3.4"),sQuery(id+"F0.wireOp",EDGE,"E3.5")])]}),"instanceName":"1"}),"instanceName":"1"});
            var Q36;
            Q36=makeQuery(id+"F6.opPattern","COPY",BODY,{"derivedFrom":makeQuery(id+"F4.opPattern","COPY",BODY,{"derivedFrom":makeQuery(id+"F3.opPattern","COPY",BODY,{"derivedFrom":makeQuery(id+"F1.opExtrude","SWEPT_BODY",BODY,{"disambiguationData":[OSD([sQuery(id+"F0.wireOp",EDGE,"E1.0"),sQuery(id+"F0.wireOp",EDGE,"E1.1"),sQuery(id+"F0.wireOp",EDGE,"E1.2"),sQuery(id+"F0.wireOp",EDGE,"E1.3"),sQuery(id+"F0.wireOp",EDGE,"E1.4"),sQuery(id+"F0.wireOp",EDGE,"E1.5"),sQuery(id+"F0.wireOp",EDGE,"E3.0"),sQuery(id+"F0.wireOp",EDGE,"E3.1"),sQuery(id+"F0.wireOp",EDGE,"E3.2"),sQuery(id+"F0.wireOp",EDGE,"E3.3"),sQuery(id+"F0.wireOp",EDGE,"E3.4"),sQuery(id+"F0.wireOp",EDGE,"E3.5")])]}),"instanceName":"1"}),"instanceName":"1"}),"instanceName":"1"});
            var Q37;
            Q37=makeQuery(id+"F6.opPattern","COPY",BODY,{"derivedFrom":makeQuery(id+"F5.opPattern","COPY",BODY,{"derivedFrom":makeQuery(id+"F4.opPattern","COPY",BODY,{"derivedFrom":makeQuery(id+"F1.opExtrude","SWEPT_BODY",BODY,{"disambiguationData":[OSD([sQuery(id+"F0.wireOp",EDGE,"E1.0"),sQuery(id+"F0.wireOp",EDGE,"E1.1"),sQuery(id+"F0.wireOp",EDGE,"E1.2"),sQuery(id+"F0.wireOp",EDGE,"E1.3"),sQuery(id+"F0.wireOp",EDGE,"E1.4"),sQuery(id+"F0.wireOp",EDGE,"E1.5"),sQuery(id+"F0.wireOp",EDGE,"E3.0"),sQuery(id+"F0.wireOp",EDGE,"E3.1"),sQuery(id+"F0.wireOp",EDGE,"E3.2"),sQuery(id+"F0.wireOp",EDGE,"E3.3"),sQuery(id+"F0.wireOp",EDGE,"E3.4"),sQuery(id+"F0.wireOp",EDGE,"E3.5")])]}),"instanceName":"1"}),"instanceName":"1"}),"instanceName":"1"});
            var Q38;
            Q38=makeQuery(id+"F6.opPattern","COPY",BODY,{"derivedFrom":makeQuery(id+"F5.opPattern","COPY",BODY,{"derivedFrom":makeQuery(id+"F4.opPattern","COPY",BODY,{"derivedFrom":makeQuery(id+"F3.opPattern","COPY",BODY,{"derivedFrom":makeQuery(id+"F1.opExtrude","SWEPT_BODY",BODY,{"disambiguationData":[OSD([sQuery(id+"F0.wireOp",EDGE,"E1.0"),sQuery(id+"F0.wireOp",EDGE,"E1.1"),sQuery(id+"F0.wireOp",EDGE,"E1.2"),sQuery(id+"F0.wireOp",EDGE,"E1.3"),sQuery(id+"F0.wireOp",EDGE,"E1.4"),sQuery(id+"F0.wireOp",EDGE,"E1.5"),sQuery(id+"F0.wireOp",EDGE,"E3.0"),sQuery(id+"F0.wireOp",EDGE,"E3.1"),sQuery(id+"F0.wireOp",EDGE,"E3.2"),sQuery(id+"F0.wireOp",EDGE,"E3.3"),sQuery(id+"F0.wireOp",EDGE,"E3.4"),sQuery(id+"F0.wireOp",EDGE,"E3.5")])]}),"instanceName":"1"}),"instanceName":"1"}),"instanceName":"1"}),"instanceName":"1"});
            var Q39;
            Q39=makeQuery(id+"F4.opPattern","COPY",BODY,{"derivedFrom":makeQuery(id+"F3.opPattern","COPY",BODY,{"derivedFrom":makeQuery(id+"F1.opExtrude","SWEPT_BODY",BODY,{"disambiguationData":[OSD([sQuery(id+"F0.wireOp",EDGE,"E1.0"),sQuery(id+"F0.wireOp",EDGE,"E1.1"),sQuery(id+"F0.wireOp",EDGE,"E1.2"),sQuery(id+"F0.wireOp",EDGE,"E1.3"),sQuery(id+"F0.wireOp",EDGE,"E1.4"),sQuery(id+"F0.wireOp",EDGE,"E1.5"),sQuery(id+"F0.wireOp",EDGE,"E3.0"),sQuery(id+"F0.wireOp",EDGE,"E3.1"),sQuery(id+"F0.wireOp",EDGE,"E3.2"),sQuery(id+"F0.wireOp",EDGE,"E3.3"),sQuery(id+"F0.wireOp",EDGE,"E3.4"),sQuery(id+"F0.wireOp",EDGE,"E3.5")])]}),"instanceName":"1"}),"instanceName":"1"});
            var Q40;
            Q40=makeQuery(id+"F5.opPattern","COPY",BODY,{"derivedFrom":makeQuery(id+"F4.opPattern","COPY",BODY,{"derivedFrom":makeQuery(id+"F3.opPattern","COPY",BODY,{"derivedFrom":makeQuery(id+"F1.opExtrude","SWEPT_BODY",BODY,{"disambiguationData":[OSD([sQuery(id+"F0.wireOp",EDGE,"E1.0"),sQuery(id+"F0.wireOp",EDGE,"E1.1"),sQuery(id+"F0.wireOp",EDGE,"E1.2"),sQuery(id+"F0.wireOp",EDGE,"E1.3"),sQuery(id+"F0.wireOp",EDGE,"E1.4"),sQuery(id+"F0.wireOp",EDGE,"E1.5"),sQuery(id+"F0.wireOp",EDGE,"E3.0"),sQuery(id+"F0.wireOp",EDGE,"E3.1"),sQuery(id+"F0.wireOp",EDGE,"E3.2"),sQuery(id+"F0.wireOp",EDGE,"E3.3"),sQuery(id+"F0.wireOp",EDGE,"E3.4"),sQuery(id+"F0.wireOp",EDGE,"E3.5")])]}),"instanceName":"1"}),"instanceName":"1"}),"instanceName":"1"});
            var Q41;
            Q41=makeQuery(id+"F5.opPattern","COPY",BODY,{"derivedFrom":makeQuery(id+"F4.opPattern","COPY",BODY,{"derivedFrom":makeQuery(id+"F1.opExtrude","SWEPT_BODY",BODY,{"disambiguationData":[OSD([sQuery(id+"F0.wireOp",EDGE,"E1.0"),sQuery(id+"F0.wireOp",EDGE,"E1.1"),sQuery(id+"F0.wireOp",EDGE,"E1.2"),sQuery(id+"F0.wireOp",EDGE,"E1.3"),sQuery(id+"F0.wireOp",EDGE,"E1.4"),sQuery(id+"F0.wireOp",EDGE,"E1.5"),sQuery(id+"F0.wireOp",EDGE,"E3.0"),sQuery(id+"F0.wireOp",EDGE,"E3.1"),sQuery(id+"F0.wireOp",EDGE,"E3.2"),sQuery(id+"F0.wireOp",EDGE,"E3.3"),sQuery(id+"F0.wireOp",EDGE,"E3.4"),sQuery(id+"F0.wireOp",EDGE,"E3.5")])]}),"instanceName":"1"}),"instanceName":"1"});
            var Q42;
            Q42=makeQuery(id+"F8.opPattern","COPY",BODY,{"derivedFrom":makeQuery(id+"F6.opPattern","COPY",BODY,{"derivedFrom":makeQuery(id+"F5.opPattern","COPY",BODY,{"derivedFrom":makeQuery(id+"F4.opPattern","COPY",BODY,{"derivedFrom":makeQuery(id+"F1.opExtrude","SWEPT_BODY",BODY,{"disambiguationData":[OSD([sQuery(id+"F0.wireOp",EDGE,"E1.0"),sQuery(id+"F0.wireOp",EDGE,"E1.1"),sQuery(id+"F0.wireOp",EDGE,"E1.2"),sQuery(id+"F0.wireOp",EDGE,"E1.3"),sQuery(id+"F0.wireOp",EDGE,"E1.4"),sQuery(id+"F0.wireOp",EDGE,"E1.5"),sQuery(id+"F0.wireOp",EDGE,"E3.0"),sQuery(id+"F0.wireOp",EDGE,"E3.1"),sQuery(id+"F0.wireOp",EDGE,"E3.2"),sQuery(id+"F0.wireOp",EDGE,"E3.3"),sQuery(id+"F0.wireOp",EDGE,"E3.4"),sQuery(id+"F0.wireOp",EDGE,"E3.5")])]}),"instanceName":"1"}),"instanceName":"1"}),"instanceName":"1"}),"instanceName":"1"});
            var Q43;
            Q43=makeQuery(id+"F8.opPattern","COPY",BODY,{"derivedFrom":makeQuery(id+"F7.opPattern","COPY",BODY,{"derivedFrom":makeQuery(id+"F5.opPattern","COPY",BODY,{"derivedFrom":makeQuery(id+"F4.opPattern","COPY",BODY,{"derivedFrom":makeQuery(id+"F1.opExtrude","SWEPT_BODY",BODY,{"disambiguationData":[OSD([sQuery(id+"F0.wireOp",EDGE,"E1.0"),sQuery(id+"F0.wireOp",EDGE,"E1.1"),sQuery(id+"F0.wireOp",EDGE,"E1.2"),sQuery(id+"F0.wireOp",EDGE,"E1.3"),sQuery(id+"F0.wireOp",EDGE,"E1.4"),sQuery(id+"F0.wireOp",EDGE,"E1.5"),sQuery(id+"F0.wireOp",EDGE,"E3.0"),sQuery(id+"F0.wireOp",EDGE,"E3.1"),sQuery(id+"F0.wireOp",EDGE,"E3.2"),sQuery(id+"F0.wireOp",EDGE,"E3.3"),sQuery(id+"F0.wireOp",EDGE,"E3.4"),sQuery(id+"F0.wireOp",EDGE,"E3.5")])]}),"instanceName":"1"}),"instanceName":"1"}),"instanceName":"1"}),"instanceName":"1"});
            var Q44;
            Q44=makeQuery(id+"F8.opPattern","COPY",BODY,{"derivedFrom":makeQuery(id+"F7.opPattern","COPY",BODY,{"derivedFrom":makeQuery(id+"F5.opPattern","COPY",BODY,{"derivedFrom":makeQuery(id+"F4.opPattern","COPY",BODY,{"derivedFrom":makeQuery(id+"F3.opPattern","COPY",BODY,{"derivedFrom":makeQuery(id+"F1.opExtrude","SWEPT_BODY",BODY,{"disambiguationData":[OSD([sQuery(id+"F0.wireOp",EDGE,"E1.0"),sQuery(id+"F0.wireOp",EDGE,"E1.1"),sQuery(id+"F0.wireOp",EDGE,"E1.2"),sQuery(id+"F0.wireOp",EDGE,"E1.3"),sQuery(id+"F0.wireOp",EDGE,"E1.4"),sQuery(id+"F0.wireOp",EDGE,"E1.5"),sQuery(id+"F0.wireOp",EDGE,"E3.0"),sQuery(id+"F0.wireOp",EDGE,"E3.1"),sQuery(id+"F0.wireOp",EDGE,"E3.2"),sQuery(id+"F0.wireOp",EDGE,"E3.3"),sQuery(id+"F0.wireOp",EDGE,"E3.4"),sQuery(id+"F0.wireOp",EDGE,"E3.5")])]}),"instanceName":"1"}),"instanceName":"1"}),"instanceName":"1"}),"instanceName":"1"}),"instanceName":"1"});
            var Q45;
            Q45=makeQuery(id+"F8.opPattern","COPY",BODY,{"derivedFrom":makeQuery(id+"F7.opPattern","COPY",BODY,{"derivedFrom":makeQuery(id+"F6.opPattern","COPY",BODY,{"derivedFrom":makeQuery(id+"F4.opPattern","COPY",BODY,{"derivedFrom":makeQuery(id+"F3.opPattern","COPY",BODY,{"derivedFrom":makeQuery(id+"F1.opExtrude","SWEPT_BODY",BODY,{"disambiguationData":[OSD([sQuery(id+"F0.wireOp",EDGE,"E1.0"),sQuery(id+"F0.wireOp",EDGE,"E1.1"),sQuery(id+"F0.wireOp",EDGE,"E1.2"),sQuery(id+"F0.wireOp",EDGE,"E1.3"),sQuery(id+"F0.wireOp",EDGE,"E1.4"),sQuery(id+"F0.wireOp",EDGE,"E1.5"),sQuery(id+"F0.wireOp",EDGE,"E3.0"),sQuery(id+"F0.wireOp",EDGE,"E3.1"),sQuery(id+"F0.wireOp",EDGE,"E3.2"),sQuery(id+"F0.wireOp",EDGE,"E3.3"),sQuery(id+"F0.wireOp",EDGE,"E3.4"),sQuery(id+"F0.wireOp",EDGE,"E3.5")])]}),"instanceName":"1"}),"instanceName":"1"}),"instanceName":"1"}),"instanceName":"1"}),"instanceName":"1"});
            var Q46;
            Q46=makeQuery(id+"F8.opPattern","COPY",BODY,{"derivedFrom":makeQuery(id+"F7.opPattern","COPY",BODY,{"derivedFrom":makeQuery(id+"F6.opPattern","COPY",BODY,{"derivedFrom":makeQuery(id+"F5.opPattern","COPY",BODY,{"derivedFrom":makeQuery(id+"F4.opPattern","COPY",BODY,{"derivedFrom":makeQuery(id+"F1.opExtrude","SWEPT_BODY",BODY,{"disambiguationData":[OSD([sQuery(id+"F0.wireOp",EDGE,"E1.0"),sQuery(id+"F0.wireOp",EDGE,"E1.1"),sQuery(id+"F0.wireOp",EDGE,"E1.2"),sQuery(id+"F0.wireOp",EDGE,"E1.3"),sQuery(id+"F0.wireOp",EDGE,"E1.4"),sQuery(id+"F0.wireOp",EDGE,"E1.5"),sQuery(id+"F0.wireOp",EDGE,"E3.0"),sQuery(id+"F0.wireOp",EDGE,"E3.1"),sQuery(id+"F0.wireOp",EDGE,"E3.2"),sQuery(id+"F0.wireOp",EDGE,"E3.3"),sQuery(id+"F0.wireOp",EDGE,"E3.4"),sQuery(id+"F0.wireOp",EDGE,"E3.5")])]}),"instanceName":"1"}),"instanceName":"1"}),"instanceName":"1"}),"instanceName":"1"}),"instanceName":"1"});
            transform(context, id + "F9", {"entities" : qUnion([Q0, Q1, Q2, Q3, Q4, Q5, Q6, Q7, Q8, Q9, Q10, Q11, Q12, Q13, Q14, Q15, Q16, Q17, Q18, Q19, Q20, Q21, Q22, Q23, Q24, Q25, Q26, Q27, Q28, Q29, Q30, Q31, Q32, Q33, Q34, Q35, Q36, Q37, Q38, Q39, Q40, Q41, Q42, Q43, Q44, Q45, Q46]), "transformType" : TransformType.TRANSLATION_3D, "dx" : -25.37 * mm, "dy" : 0 * mm, "dz" : 0 * mm, "makeCopy" : true});
        }
        {
            var Q0;
            Q0=makeQuery(id+"F9.opPattern","COPY",BODY,{"derivedFrom":makeQuery(id+"F8.opPattern","COPY",BODY,{"derivedFrom":makeQuery(id+"F7.opPattern","COPY",BODY,{"derivedFrom":makeQuery(id+"F6.opPattern","COPY",BODY,{"derivedFrom":makeQuery(id+"F5.opPattern","COPY",BODY,{"derivedFrom":makeQuery(id+"F4.opPattern","COPY",BODY,{"derivedFrom":makeQuery(id+"F1.opExtrude","SWEPT_BODY",BODY,{"disambiguationData":[OSD([sQuery(id+"F0.wireOp",EDGE,"E1.0"),sQuery(id+"F0.wireOp",EDGE,"E1.1"),sQuery(id+"F0.wireOp",EDGE,"E1.2"),sQuery(id+"F0.wireOp",EDGE,"E1.3"),sQuery(id+"F0.wireOp",EDGE,"E1.4"),sQuery(id+"F0.wireOp",EDGE,"E1.5"),sQuery(id+"F0.wireOp",EDGE,"E3.0"),sQuery(id+"F0.wireOp",EDGE,"E3.1"),sQuery(id+"F0.wireOp",EDGE,"E3.2"),sQuery(id+"F0.wireOp",EDGE,"E3.3"),sQuery(id+"F0.wireOp",EDGE,"E3.4"),sQuery(id+"F0.wireOp",EDGE,"E3.5")])]}),"instanceName":"1"}),"instanceName":"1"}),"instanceName":"1"}),"instanceName":"1"}),"instanceName":"1"}),"instanceName":"1"});
            transform(context, id + "F10", {"entities" : qUnion([Q0]), "transformType" : TransformType.TRANSLATION_3D, "dx" : 4.23 * mm, "dy" : 0 * mm, "dz" : 0 * mm, "makeCopy" : true});
        }
        {
            var Q0;
            Q0=makeQuery(id+"F8.opPattern","COPY",BODY,{"derivedFrom":makeQuery(id+"F1.opExtrude","SWEPT_BODY",BODY,{"disambiguationData":[OSD([sQuery(id+"F0.wireOp",EDGE,"E1.0"),sQuery(id+"F0.wireOp",EDGE,"E1.1"),sQuery(id+"F0.wireOp",EDGE,"E1.2"),sQuery(id+"F0.wireOp",EDGE,"E1.3"),sQuery(id+"F0.wireOp",EDGE,"E1.4"),sQuery(id+"F0.wireOp",EDGE,"E1.5"),sQuery(id+"F0.wireOp",EDGE,"E3.0"),sQuery(id+"F0.wireOp",EDGE,"E3.1"),sQuery(id+"F0.wireOp",EDGE,"E3.2"),sQuery(id+"F0.wireOp",EDGE,"E3.3"),sQuery(id+"F0.wireOp",EDGE,"E3.4"),sQuery(id+"F0.wireOp",EDGE,"E3.5")])]}),"instanceName":"1"});
            var Q1;
            Q1=makeQuery(id+"F8.opPattern","COPY",BODY,{"derivedFrom":makeQuery(id+"F6.opPattern","COPY",BODY,{"derivedFrom":makeQuery(id+"F1.opExtrude","SWEPT_BODY",BODY,{"disambiguationData":[OSD([sQuery(id+"F0.wireOp",EDGE,"E1.0"),sQuery(id+"F0.wireOp",EDGE,"E1.1"),sQuery(id+"F0.wireOp",EDGE,"E1.2"),sQuery(id+"F0.wireOp",EDGE,"E1.3"),sQuery(id+"F0.wireOp",EDGE,"E1.4"),sQuery(id+"F0.wireOp",EDGE,"E1.5"),sQuery(id+"F0.wireOp",EDGE,"E3.0"),sQuery(id+"F0.wireOp",EDGE,"E3.1"),sQuery(id+"F0.wireOp",EDGE,"E3.2"),sQuery(id+"F0.wireOp",EDGE,"E3.3"),sQuery(id+"F0.wireOp",EDGE,"E3.4"),sQuery(id+"F0.wireOp",EDGE,"E3.5")])]}),"instanceName":"1"}),"instanceName":"1"});
            var Q2;
            Q2=makeQuery(id+"F8.opPattern","COPY",BODY,{"derivedFrom":makeQuery(id+"F6.opPattern","COPY",BODY,{"derivedFrom":makeQuery(id+"F3.opPattern","COPY",BODY,{"derivedFrom":makeQuery(id+"F1.opExtrude","SWEPT_BODY",BODY,{"disambiguationData":[OSD([sQuery(id+"F0.wireOp",EDGE,"E1.0"),sQuery(id+"F0.wireOp",EDGE,"E1.1"),sQuery(id+"F0.wireOp",EDGE,"E1.2"),sQuery(id+"F0.wireOp",EDGE,"E1.3"),sQuery(id+"F0.wireOp",EDGE,"E1.4"),sQuery(id+"F0.wireOp",EDGE,"E1.5"),sQuery(id+"F0.wireOp",EDGE,"E3.0"),sQuery(id+"F0.wireOp",EDGE,"E3.1"),sQuery(id+"F0.wireOp",EDGE,"E3.2"),sQuery(id+"F0.wireOp",EDGE,"E3.3"),sQuery(id+"F0.wireOp",EDGE,"E3.4"),sQuery(id+"F0.wireOp",EDGE,"E3.5")])]}),"instanceName":"1"}),"instanceName":"1"}),"instanceName":"1"});
            var Q3;
            Q3=makeQuery(id+"F8.opPattern","COPY",BODY,{"derivedFrom":makeQuery(id+"F5.opPattern","COPY",BODY,{"derivedFrom":makeQuery(id+"F4.opPattern","COPY",BODY,{"derivedFrom":makeQuery(id+"F3.opPattern","COPY",BODY,{"derivedFrom":makeQuery(id+"F1.opExtrude","SWEPT_BODY",BODY,{"disambiguationData":[OSD([sQuery(id+"F0.wireOp",EDGE,"E1.0"),sQuery(id+"F0.wireOp",EDGE,"E1.1"),sQuery(id+"F0.wireOp",EDGE,"E1.2"),sQuery(id+"F0.wireOp",EDGE,"E1.3"),sQuery(id+"F0.wireOp",EDGE,"E1.4"),sQuery(id+"F0.wireOp",EDGE,"E1.5"),sQuery(id+"F0.wireOp",EDGE,"E3.0"),sQuery(id+"F0.wireOp",EDGE,"E3.1"),sQuery(id+"F0.wireOp",EDGE,"E3.2"),sQuery(id+"F0.wireOp",EDGE,"E3.3"),sQuery(id+"F0.wireOp",EDGE,"E3.4"),sQuery(id+"F0.wireOp",EDGE,"E3.5")])]}),"instanceName":"1"}),"instanceName":"1"}),"instanceName":"1"}),"instanceName":"1"});
            var Q4;
            Q4=makeQuery(id+"F8.opPattern","COPY",BODY,{"derivedFrom":makeQuery(id+"F7.opPattern","COPY",BODY,{"derivedFrom":makeQuery(id+"F4.opPattern","COPY",BODY,{"derivedFrom":makeQuery(id+"F1.opExtrude","SWEPT_BODY",BODY,{"disambiguationData":[OSD([sQuery(id+"F0.wireOp",EDGE,"E1.0"),sQuery(id+"F0.wireOp",EDGE,"E1.1"),sQuery(id+"F0.wireOp",EDGE,"E1.2"),sQuery(id+"F0.wireOp",EDGE,"E1.3"),sQuery(id+"F0.wireOp",EDGE,"E1.4"),sQuery(id+"F0.wireOp",EDGE,"E1.5"),sQuery(id+"F0.wireOp",EDGE,"E3.0"),sQuery(id+"F0.wireOp",EDGE,"E3.1"),sQuery(id+"F0.wireOp",EDGE,"E3.2"),sQuery(id+"F0.wireOp",EDGE,"E3.3"),sQuery(id+"F0.wireOp",EDGE,"E3.4"),sQuery(id+"F0.wireOp",EDGE,"E3.5")])]}),"instanceName":"1"}),"instanceName":"1"}),"instanceName":"1"});
            var Q5;
            Q5=makeQuery(id+"F8.opPattern","COPY",BODY,{"derivedFrom":makeQuery(id+"F7.opPattern","COPY",BODY,{"derivedFrom":makeQuery(id+"F4.opPattern","COPY",BODY,{"derivedFrom":makeQuery(id+"F3.opPattern","COPY",BODY,{"derivedFrom":makeQuery(id+"F1.opExtrude","SWEPT_BODY",BODY,{"disambiguationData":[OSD([sQuery(id+"F0.wireOp",EDGE,"E1.0"),sQuery(id+"F0.wireOp",EDGE,"E1.1"),sQuery(id+"F0.wireOp",EDGE,"E1.2"),sQuery(id+"F0.wireOp",EDGE,"E1.3"),sQuery(id+"F0.wireOp",EDGE,"E1.4"),sQuery(id+"F0.wireOp",EDGE,"E1.5"),sQuery(id+"F0.wireOp",EDGE,"E3.0"),sQuery(id+"F0.wireOp",EDGE,"E3.1"),sQuery(id+"F0.wireOp",EDGE,"E3.2"),sQuery(id+"F0.wireOp",EDGE,"E3.3"),sQuery(id+"F0.wireOp",EDGE,"E3.4"),sQuery(id+"F0.wireOp",EDGE,"E3.5")])]}),"instanceName":"1"}),"instanceName":"1"}),"instanceName":"1"}),"instanceName":"1"});
            var Q6;
            Q6=makeQuery(id+"F8.opPattern","COPY",BODY,{"derivedFrom":makeQuery(id+"F7.opPattern","COPY",BODY,{"derivedFrom":makeQuery(id+"F3.opPattern","COPY",BODY,{"derivedFrom":makeQuery(id+"F1.opExtrude","SWEPT_BODY",BODY,{"disambiguationData":[OSD([sQuery(id+"F0.wireOp",EDGE,"E1.0"),sQuery(id+"F0.wireOp",EDGE,"E1.1"),sQuery(id+"F0.wireOp",EDGE,"E1.2"),sQuery(id+"F0.wireOp",EDGE,"E1.3"),sQuery(id+"F0.wireOp",EDGE,"E1.4"),sQuery(id+"F0.wireOp",EDGE,"E1.5"),sQuery(id+"F0.wireOp",EDGE,"E3.0"),sQuery(id+"F0.wireOp",EDGE,"E3.1"),sQuery(id+"F0.wireOp",EDGE,"E3.2"),sQuery(id+"F0.wireOp",EDGE,"E3.3"),sQuery(id+"F0.wireOp",EDGE,"E3.4"),sQuery(id+"F0.wireOp",EDGE,"E3.5")])]}),"instanceName":"1"}),"instanceName":"1"}),"instanceName":"1"});
            var Q7;
            Q7=makeQuery(id+"F8.opPattern","COPY",BODY,{"derivedFrom":makeQuery(id+"F6.opPattern","COPY",BODY,{"derivedFrom":makeQuery(id+"F4.opPattern","COPY",BODY,{"derivedFrom":makeQuery(id+"F3.opPattern","COPY",BODY,{"derivedFrom":makeQuery(id+"F1.opExtrude","SWEPT_BODY",BODY,{"disambiguationData":[OSD([sQuery(id+"F0.wireOp",EDGE,"E1.0"),sQuery(id+"F0.wireOp",EDGE,"E1.1"),sQuery(id+"F0.wireOp",EDGE,"E1.2"),sQuery(id+"F0.wireOp",EDGE,"E1.3"),sQuery(id+"F0.wireOp",EDGE,"E1.4"),sQuery(id+"F0.wireOp",EDGE,"E1.5"),sQuery(id+"F0.wireOp",EDGE,"E3.0"),sQuery(id+"F0.wireOp",EDGE,"E3.1"),sQuery(id+"F0.wireOp",EDGE,"E3.2"),sQuery(id+"F0.wireOp",EDGE,"E3.3"),sQuery(id+"F0.wireOp",EDGE,"E3.4"),sQuery(id+"F0.wireOp",EDGE,"E3.5")])]}),"instanceName":"1"}),"instanceName":"1"}),"instanceName":"1"}),"instanceName":"1"});
            var Q8;
            Q8=makeQuery(id+"F8.opPattern","COPY",BODY,{"derivedFrom":makeQuery(id+"F6.opPattern","COPY",BODY,{"derivedFrom":makeQuery(id+"F5.opPattern","COPY",BODY,{"derivedFrom":makeQuery(id+"F4.opPattern","COPY",BODY,{"derivedFrom":makeQuery(id+"F3.opPattern","COPY",BODY,{"derivedFrom":makeQuery(id+"F1.opExtrude","SWEPT_BODY",BODY,{"disambiguationData":[OSD([sQuery(id+"F0.wireOp",EDGE,"E1.0"),sQuery(id+"F0.wireOp",EDGE,"E1.1"),sQuery(id+"F0.wireOp",EDGE,"E1.2"),sQuery(id+"F0.wireOp",EDGE,"E1.3"),sQuery(id+"F0.wireOp",EDGE,"E1.4"),sQuery(id+"F0.wireOp",EDGE,"E1.5"),sQuery(id+"F0.wireOp",EDGE,"E3.0"),sQuery(id+"F0.wireOp",EDGE,"E3.1"),sQuery(id+"F0.wireOp",EDGE,"E3.2"),sQuery(id+"F0.wireOp",EDGE,"E3.3"),sQuery(id+"F0.wireOp",EDGE,"E3.4"),sQuery(id+"F0.wireOp",EDGE,"E3.5")])]}),"instanceName":"1"}),"instanceName":"1"}),"instanceName":"1"}),"instanceName":"1"}),"instanceName":"1"});
            var Q9;
            Q9=makeQuery(id+"F8.opPattern","COPY",BODY,{"derivedFrom":makeQuery(id+"F7.opPattern","COPY",BODY,{"derivedFrom":makeQuery(id+"F1.opExtrude","SWEPT_BODY",BODY,{"disambiguationData":[OSD([sQuery(id+"F0.wireOp",EDGE,"E1.0"),sQuery(id+"F0.wireOp",EDGE,"E1.1"),sQuery(id+"F0.wireOp",EDGE,"E1.2"),sQuery(id+"F0.wireOp",EDGE,"E1.3"),sQuery(id+"F0.wireOp",EDGE,"E1.4"),sQuery(id+"F0.wireOp",EDGE,"E1.5"),sQuery(id+"F0.wireOp",EDGE,"E3.0"),sQuery(id+"F0.wireOp",EDGE,"E3.1"),sQuery(id+"F0.wireOp",EDGE,"E3.2"),sQuery(id+"F0.wireOp",EDGE,"E3.3"),sQuery(id+"F0.wireOp",EDGE,"E3.4"),sQuery(id+"F0.wireOp",EDGE,"E3.5")])]}),"instanceName":"1"}),"instanceName":"1"});
            var Q10;
            Q10=makeQuery(id+"F8.opPattern","COPY",BODY,{"derivedFrom":makeQuery(id+"F5.opPattern","COPY",BODY,{"derivedFrom":makeQuery(id+"F4.opPattern","COPY",BODY,{"derivedFrom":makeQuery(id+"F1.opExtrude","SWEPT_BODY",BODY,{"disambiguationData":[OSD([sQuery(id+"F0.wireOp",EDGE,"E1.0"),sQuery(id+"F0.wireOp",EDGE,"E1.1"),sQuery(id+"F0.wireOp",EDGE,"E1.2"),sQuery(id+"F0.wireOp",EDGE,"E1.3"),sQuery(id+"F0.wireOp",EDGE,"E1.4"),sQuery(id+"F0.wireOp",EDGE,"E1.5"),sQuery(id+"F0.wireOp",EDGE,"E3.0"),sQuery(id+"F0.wireOp",EDGE,"E3.1"),sQuery(id+"F0.wireOp",EDGE,"E3.2"),sQuery(id+"F0.wireOp",EDGE,"E3.3"),sQuery(id+"F0.wireOp",EDGE,"E3.4"),sQuery(id+"F0.wireOp",EDGE,"E3.5")])]}),"instanceName":"1"}),"instanceName":"1"}),"instanceName":"1"});
            var Q11;
            Q11=makeQuery(id+"F8.opPattern","COPY",BODY,{"derivedFrom":makeQuery(id+"F3.opPattern","COPY",BODY,{"derivedFrom":makeQuery(id+"F1.opExtrude","SWEPT_BODY",BODY,{"disambiguationData":[OSD([sQuery(id+"F0.wireOp",EDGE,"E1.0"),sQuery(id+"F0.wireOp",EDGE,"E1.1"),sQuery(id+"F0.wireOp",EDGE,"E1.2"),sQuery(id+"F0.wireOp",EDGE,"E1.3"),sQuery(id+"F0.wireOp",EDGE,"E1.4"),sQuery(id+"F0.wireOp",EDGE,"E1.5"),sQuery(id+"F0.wireOp",EDGE,"E3.0"),sQuery(id+"F0.wireOp",EDGE,"E3.1"),sQuery(id+"F0.wireOp",EDGE,"E3.2"),sQuery(id+"F0.wireOp",EDGE,"E3.3"),sQuery(id+"F0.wireOp",EDGE,"E3.4"),sQuery(id+"F0.wireOp",EDGE,"E3.5")])]}),"instanceName":"1"}),"instanceName":"1"});
            var Q12;
            Q12=makeQuery(id+"F8.opPattern","COPY",BODY,{"derivedFrom":makeQuery(id+"F4.opPattern","COPY",BODY,{"derivedFrom":makeQuery(id+"F1.opExtrude","SWEPT_BODY",BODY,{"disambiguationData":[OSD([sQuery(id+"F0.wireOp",EDGE,"E1.0"),sQuery(id+"F0.wireOp",EDGE,"E1.1"),sQuery(id+"F0.wireOp",EDGE,"E1.2"),sQuery(id+"F0.wireOp",EDGE,"E1.3"),sQuery(id+"F0.wireOp",EDGE,"E1.4"),sQuery(id+"F0.wireOp",EDGE,"E1.5"),sQuery(id+"F0.wireOp",EDGE,"E3.0"),sQuery(id+"F0.wireOp",EDGE,"E3.1"),sQuery(id+"F0.wireOp",EDGE,"E3.2"),sQuery(id+"F0.wireOp",EDGE,"E3.3"),sQuery(id+"F0.wireOp",EDGE,"E3.4"),sQuery(id+"F0.wireOp",EDGE,"E3.5")])]}),"instanceName":"1"}),"instanceName":"1"});
            var Q13;
            Q13=makeQuery(id+"F8.opPattern","COPY",BODY,{"derivedFrom":makeQuery(id+"F4.opPattern","COPY",BODY,{"derivedFrom":makeQuery(id+"F3.opPattern","COPY",BODY,{"derivedFrom":makeQuery(id+"F1.opExtrude","SWEPT_BODY",BODY,{"disambiguationData":[OSD([sQuery(id+"F0.wireOp",EDGE,"E1.0"),sQuery(id+"F0.wireOp",EDGE,"E1.1"),sQuery(id+"F0.wireOp",EDGE,"E1.2"),sQuery(id+"F0.wireOp",EDGE,"E1.3"),sQuery(id+"F0.wireOp",EDGE,"E1.4"),sQuery(id+"F0.wireOp",EDGE,"E1.5"),sQuery(id+"F0.wireOp",EDGE,"E3.0"),sQuery(id+"F0.wireOp",EDGE,"E3.1"),sQuery(id+"F0.wireOp",EDGE,"E3.2"),sQuery(id+"F0.wireOp",EDGE,"E3.3"),sQuery(id+"F0.wireOp",EDGE,"E3.4"),sQuery(id+"F0.wireOp",EDGE,"E3.5")])]}),"instanceName":"1"}),"instanceName":"1"}),"instanceName":"1"});
            var Q14;
            Q14=makeQuery(id+"F8.opPattern","COPY",BODY,{"derivedFrom":makeQuery(id+"F6.opPattern","COPY",BODY,{"derivedFrom":makeQuery(id+"F5.opPattern","COPY",BODY,{"derivedFrom":makeQuery(id+"F4.opPattern","COPY",BODY,{"derivedFrom":makeQuery(id+"F1.opExtrude","SWEPT_BODY",BODY,{"disambiguationData":[OSD([sQuery(id+"F0.wireOp",EDGE,"E1.0"),sQuery(id+"F0.wireOp",EDGE,"E1.1"),sQuery(id+"F0.wireOp",EDGE,"E1.2"),sQuery(id+"F0.wireOp",EDGE,"E1.3"),sQuery(id+"F0.wireOp",EDGE,"E1.4"),sQuery(id+"F0.wireOp",EDGE,"E1.5"),sQuery(id+"F0.wireOp",EDGE,"E3.0"),sQuery(id+"F0.wireOp",EDGE,"E3.1"),sQuery(id+"F0.wireOp",EDGE,"E3.2"),sQuery(id+"F0.wireOp",EDGE,"E3.3"),sQuery(id+"F0.wireOp",EDGE,"E3.4"),sQuery(id+"F0.wireOp",EDGE,"E3.5")])]}),"instanceName":"1"}),"instanceName":"1"}),"instanceName":"1"}),"instanceName":"1"});
            var Q15;
            Q15=makeQuery(id+"F8.opPattern","COPY",BODY,{"derivedFrom":makeQuery(id+"F6.opPattern","COPY",BODY,{"derivedFrom":makeQuery(id+"F4.opPattern","COPY",BODY,{"derivedFrom":makeQuery(id+"F1.opExtrude","SWEPT_BODY",BODY,{"disambiguationData":[OSD([sQuery(id+"F0.wireOp",EDGE,"E1.0"),sQuery(id+"F0.wireOp",EDGE,"E1.1"),sQuery(id+"F0.wireOp",EDGE,"E1.2"),sQuery(id+"F0.wireOp",EDGE,"E1.3"),sQuery(id+"F0.wireOp",EDGE,"E1.4"),sQuery(id+"F0.wireOp",EDGE,"E1.5"),sQuery(id+"F0.wireOp",EDGE,"E3.0"),sQuery(id+"F0.wireOp",EDGE,"E3.1"),sQuery(id+"F0.wireOp",EDGE,"E3.2"),sQuery(id+"F0.wireOp",EDGE,"E3.3"),sQuery(id+"F0.wireOp",EDGE,"E3.4"),sQuery(id+"F0.wireOp",EDGE,"E3.5")])]}),"instanceName":"1"}),"instanceName":"1"}),"instanceName":"1"});
            var Q16;
            Q16=makeQuery(id+"F8.opPattern","COPY",BODY,{"derivedFrom":makeQuery(id+"F7.opPattern","COPY",BODY,{"derivedFrom":makeQuery(id+"F5.opPattern","COPY",BODY,{"derivedFrom":makeQuery(id+"F4.opPattern","COPY",BODY,{"derivedFrom":makeQuery(id+"F1.opExtrude","SWEPT_BODY",BODY,{"disambiguationData":[OSD([sQuery(id+"F0.wireOp",EDGE,"E1.0"),sQuery(id+"F0.wireOp",EDGE,"E1.1"),sQuery(id+"F0.wireOp",EDGE,"E1.2"),sQuery(id+"F0.wireOp",EDGE,"E1.3"),sQuery(id+"F0.wireOp",EDGE,"E1.4"),sQuery(id+"F0.wireOp",EDGE,"E1.5"),sQuery(id+"F0.wireOp",EDGE,"E3.0"),sQuery(id+"F0.wireOp",EDGE,"E3.1"),sQuery(id+"F0.wireOp",EDGE,"E3.2"),sQuery(id+"F0.wireOp",EDGE,"E3.3"),sQuery(id+"F0.wireOp",EDGE,"E3.4"),sQuery(id+"F0.wireOp",EDGE,"E3.5")])]}),"instanceName":"1"}),"instanceName":"1"}),"instanceName":"1"}),"instanceName":"1"});
            var Q17;
            Q17=makeQuery(id+"F8.opPattern","COPY",BODY,{"derivedFrom":makeQuery(id+"F7.opPattern","COPY",BODY,{"derivedFrom":makeQuery(id+"F5.opPattern","COPY",BODY,{"derivedFrom":makeQuery(id+"F4.opPattern","COPY",BODY,{"derivedFrom":makeQuery(id+"F3.opPattern","COPY",BODY,{"derivedFrom":makeQuery(id+"F1.opExtrude","SWEPT_BODY",BODY,{"disambiguationData":[OSD([sQuery(id+"F0.wireOp",EDGE,"E1.0"),sQuery(id+"F0.wireOp",EDGE,"E1.1"),sQuery(id+"F0.wireOp",EDGE,"E1.2"),sQuery(id+"F0.wireOp",EDGE,"E1.3"),sQuery(id+"F0.wireOp",EDGE,"E1.4"),sQuery(id+"F0.wireOp",EDGE,"E1.5"),sQuery(id+"F0.wireOp",EDGE,"E3.0"),sQuery(id+"F0.wireOp",EDGE,"E3.1"),sQuery(id+"F0.wireOp",EDGE,"E3.2"),sQuery(id+"F0.wireOp",EDGE,"E3.3"),sQuery(id+"F0.wireOp",EDGE,"E3.4"),sQuery(id+"F0.wireOp",EDGE,"E3.5")])]}),"instanceName":"1"}),"instanceName":"1"}),"instanceName":"1"}),"instanceName":"1"}),"instanceName":"1"});
            var Q18;
            Q18=makeQuery(id+"F9.opPattern","COPY",BODY,{"derivedFrom":makeQuery(id+"F8.opPattern","COPY",BODY,{"derivedFrom":makeQuery(id+"F1.opExtrude","SWEPT_BODY",BODY,{"disambiguationData":[OSD([sQuery(id+"F0.wireOp",EDGE,"E1.0"),sQuery(id+"F0.wireOp",EDGE,"E1.1"),sQuery(id+"F0.wireOp",EDGE,"E1.2"),sQuery(id+"F0.wireOp",EDGE,"E1.3"),sQuery(id+"F0.wireOp",EDGE,"E1.4"),sQuery(id+"F0.wireOp",EDGE,"E1.5"),sQuery(id+"F0.wireOp",EDGE,"E3.0"),sQuery(id+"F0.wireOp",EDGE,"E3.1"),sQuery(id+"F0.wireOp",EDGE,"E3.2"),sQuery(id+"F0.wireOp",EDGE,"E3.3"),sQuery(id+"F0.wireOp",EDGE,"E3.4"),sQuery(id+"F0.wireOp",EDGE,"E3.5")])]}),"instanceName":"1"}),"instanceName":"1"});
            var Q19;
            Q19=makeQuery(id+"F9.opPattern","COPY",BODY,{"derivedFrom":makeQuery(id+"F8.opPattern","COPY",BODY,{"derivedFrom":makeQuery(id+"F3.opPattern","COPY",BODY,{"derivedFrom":makeQuery(id+"F1.opExtrude","SWEPT_BODY",BODY,{"disambiguationData":[OSD([sQuery(id+"F0.wireOp",EDGE,"E1.0"),sQuery(id+"F0.wireOp",EDGE,"E1.1"),sQuery(id+"F0.wireOp",EDGE,"E1.2"),sQuery(id+"F0.wireOp",EDGE,"E1.3"),sQuery(id+"F0.wireOp",EDGE,"E1.4"),sQuery(id+"F0.wireOp",EDGE,"E1.5"),sQuery(id+"F0.wireOp",EDGE,"E3.0"),sQuery(id+"F0.wireOp",EDGE,"E3.1"),sQuery(id+"F0.wireOp",EDGE,"E3.2"),sQuery(id+"F0.wireOp",EDGE,"E3.3"),sQuery(id+"F0.wireOp",EDGE,"E3.4"),sQuery(id+"F0.wireOp",EDGE,"E3.5")])]}),"instanceName":"1"}),"instanceName":"1"}),"instanceName":"1"});
            var Q20;
            Q20=makeQuery(id+"F9.opPattern","COPY",BODY,{"derivedFrom":makeQuery(id+"F8.opPattern","COPY",BODY,{"derivedFrom":makeQuery(id+"F4.opPattern","COPY",BODY,{"derivedFrom":makeQuery(id+"F1.opExtrude","SWEPT_BODY",BODY,{"disambiguationData":[OSD([sQuery(id+"F0.wireOp",EDGE,"E1.0"),sQuery(id+"F0.wireOp",EDGE,"E1.1"),sQuery(id+"F0.wireOp",EDGE,"E1.2"),sQuery(id+"F0.wireOp",EDGE,"E1.3"),sQuery(id+"F0.wireOp",EDGE,"E1.4"),sQuery(id+"F0.wireOp",EDGE,"E1.5"),sQuery(id+"F0.wireOp",EDGE,"E3.0"),sQuery(id+"F0.wireOp",EDGE,"E3.1"),sQuery(id+"F0.wireOp",EDGE,"E3.2"),sQuery(id+"F0.wireOp",EDGE,"E3.3"),sQuery(id+"F0.wireOp",EDGE,"E3.4"),sQuery(id+"F0.wireOp",EDGE,"E3.5")])]}),"instanceName":"1"}),"instanceName":"1"}),"instanceName":"1"});
            var Q21;
            Q21=makeQuery(id+"F9.opPattern","COPY",BODY,{"derivedFrom":makeQuery(id+"F8.opPattern","COPY",BODY,{"derivedFrom":makeQuery(id+"F4.opPattern","COPY",BODY,{"derivedFrom":makeQuery(id+"F3.opPattern","COPY",BODY,{"derivedFrom":makeQuery(id+"F1.opExtrude","SWEPT_BODY",BODY,{"disambiguationData":[OSD([sQuery(id+"F0.wireOp",EDGE,"E1.0"),sQuery(id+"F0.wireOp",EDGE,"E1.1"),sQuery(id+"F0.wireOp",EDGE,"E1.2"),sQuery(id+"F0.wireOp",EDGE,"E1.3"),sQuery(id+"F0.wireOp",EDGE,"E1.4"),sQuery(id+"F0.wireOp",EDGE,"E1.5"),sQuery(id+"F0.wireOp",EDGE,"E3.0"),sQuery(id+"F0.wireOp",EDGE,"E3.1"),sQuery(id+"F0.wireOp",EDGE,"E3.2"),sQuery(id+"F0.wireOp",EDGE,"E3.3"),sQuery(id+"F0.wireOp",EDGE,"E3.4"),sQuery(id+"F0.wireOp",EDGE,"E3.5")])]}),"instanceName":"1"}),"instanceName":"1"}),"instanceName":"1"}),"instanceName":"1"});
            var Q22;
            Q22=makeQuery(id+"F9.opPattern","COPY",BODY,{"derivedFrom":makeQuery(id+"F8.opPattern","COPY",BODY,{"derivedFrom":makeQuery(id+"F5.opPattern","COPY",BODY,{"derivedFrom":makeQuery(id+"F4.opPattern","COPY",BODY,{"derivedFrom":makeQuery(id+"F1.opExtrude","SWEPT_BODY",BODY,{"disambiguationData":[OSD([sQuery(id+"F0.wireOp",EDGE,"E1.0"),sQuery(id+"F0.wireOp",EDGE,"E1.1"),sQuery(id+"F0.wireOp",EDGE,"E1.2"),sQuery(id+"F0.wireOp",EDGE,"E1.3"),sQuery(id+"F0.wireOp",EDGE,"E1.4"),sQuery(id+"F0.wireOp",EDGE,"E1.5"),sQuery(id+"F0.wireOp",EDGE,"E3.0"),sQuery(id+"F0.wireOp",EDGE,"E3.1"),sQuery(id+"F0.wireOp",EDGE,"E3.2"),sQuery(id+"F0.wireOp",EDGE,"E3.3"),sQuery(id+"F0.wireOp",EDGE,"E3.4"),sQuery(id+"F0.wireOp",EDGE,"E3.5")])]}),"instanceName":"1"}),"instanceName":"1"}),"instanceName":"1"}),"instanceName":"1"});
            var Q23;
            Q23=makeQuery(id+"F9.opPattern","COPY",BODY,{"derivedFrom":makeQuery(id+"F8.opPattern","COPY",BODY,{"derivedFrom":makeQuery(id+"F5.opPattern","COPY",BODY,{"derivedFrom":makeQuery(id+"F4.opPattern","COPY",BODY,{"derivedFrom":makeQuery(id+"F3.opPattern","COPY",BODY,{"derivedFrom":makeQuery(id+"F1.opExtrude","SWEPT_BODY",BODY,{"disambiguationData":[OSD([sQuery(id+"F0.wireOp",EDGE,"E1.0"),sQuery(id+"F0.wireOp",EDGE,"E1.1"),sQuery(id+"F0.wireOp",EDGE,"E1.2"),sQuery(id+"F0.wireOp",EDGE,"E1.3"),sQuery(id+"F0.wireOp",EDGE,"E1.4"),sQuery(id+"F0.wireOp",EDGE,"E1.5"),sQuery(id+"F0.wireOp",EDGE,"E3.0"),sQuery(id+"F0.wireOp",EDGE,"E3.1"),sQuery(id+"F0.wireOp",EDGE,"E3.2"),sQuery(id+"F0.wireOp",EDGE,"E3.3"),sQuery(id+"F0.wireOp",EDGE,"E3.4"),sQuery(id+"F0.wireOp",EDGE,"E3.5")])]}),"instanceName":"1"}),"instanceName":"1"}),"instanceName":"1"}),"instanceName":"1"}),"instanceName":"1"});
            var Q24;
            Q24=makeQuery(id+"F9.opPattern","COPY",BODY,{"derivedFrom":makeQuery(id+"F8.opPattern","COPY",BODY,{"derivedFrom":makeQuery(id+"F6.opPattern","COPY",BODY,{"derivedFrom":makeQuery(id+"F1.opExtrude","SWEPT_BODY",BODY,{"disambiguationData":[OSD([sQuery(id+"F0.wireOp",EDGE,"E1.0"),sQuery(id+"F0.wireOp",EDGE,"E1.1"),sQuery(id+"F0.wireOp",EDGE,"E1.2"),sQuery(id+"F0.wireOp",EDGE,"E1.3"),sQuery(id+"F0.wireOp",EDGE,"E1.4"),sQuery(id+"F0.wireOp",EDGE,"E1.5"),sQuery(id+"F0.wireOp",EDGE,"E3.0"),sQuery(id+"F0.wireOp",EDGE,"E3.1"),sQuery(id+"F0.wireOp",EDGE,"E3.2"),sQuery(id+"F0.wireOp",EDGE,"E3.3"),sQuery(id+"F0.wireOp",EDGE,"E3.4"),sQuery(id+"F0.wireOp",EDGE,"E3.5")])]}),"instanceName":"1"}),"instanceName":"1"}),"instanceName":"1"});
            var Q25;
            Q25=makeQuery(id+"F9.opPattern","COPY",BODY,{"derivedFrom":makeQuery(id+"F8.opPattern","COPY",BODY,{"derivedFrom":makeQuery(id+"F6.opPattern","COPY",BODY,{"derivedFrom":makeQuery(id+"F3.opPattern","COPY",BODY,{"derivedFrom":makeQuery(id+"F1.opExtrude","SWEPT_BODY",BODY,{"disambiguationData":[OSD([sQuery(id+"F0.wireOp",EDGE,"E1.0"),sQuery(id+"F0.wireOp",EDGE,"E1.1"),sQuery(id+"F0.wireOp",EDGE,"E1.2"),sQuery(id+"F0.wireOp",EDGE,"E1.3"),sQuery(id+"F0.wireOp",EDGE,"E1.4"),sQuery(id+"F0.wireOp",EDGE,"E1.5"),sQuery(id+"F0.wireOp",EDGE,"E3.0"),sQuery(id+"F0.wireOp",EDGE,"E3.1"),sQuery(id+"F0.wireOp",EDGE,"E3.2"),sQuery(id+"F0.wireOp",EDGE,"E3.3"),sQuery(id+"F0.wireOp",EDGE,"E3.4"),sQuery(id+"F0.wireOp",EDGE,"E3.5")])]}),"instanceName":"1"}),"instanceName":"1"}),"instanceName":"1"}),"instanceName":"1"});
            var Q26;
            Q26=makeQuery(id+"F9.opPattern","COPY",BODY,{"derivedFrom":makeQuery(id+"F8.opPattern","COPY",BODY,{"derivedFrom":makeQuery(id+"F6.opPattern","COPY",BODY,{"derivedFrom":makeQuery(id+"F4.opPattern","COPY",BODY,{"derivedFrom":makeQuery(id+"F1.opExtrude","SWEPT_BODY",BODY,{"disambiguationData":[OSD([sQuery(id+"F0.wireOp",EDGE,"E1.0"),sQuery(id+"F0.wireOp",EDGE,"E1.1"),sQuery(id+"F0.wireOp",EDGE,"E1.2"),sQuery(id+"F0.wireOp",EDGE,"E1.3"),sQuery(id+"F0.wireOp",EDGE,"E1.4"),sQuery(id+"F0.wireOp",EDGE,"E1.5"),sQuery(id+"F0.wireOp",EDGE,"E3.0"),sQuery(id+"F0.wireOp",EDGE,"E3.1"),sQuery(id+"F0.wireOp",EDGE,"E3.2"),sQuery(id+"F0.wireOp",EDGE,"E3.3"),sQuery(id+"F0.wireOp",EDGE,"E3.4"),sQuery(id+"F0.wireOp",EDGE,"E3.5")])]}),"instanceName":"1"}),"instanceName":"1"}),"instanceName":"1"}),"instanceName":"1"});
            var Q27;
            Q27=makeQuery(id+"F9.opPattern","COPY",BODY,{"derivedFrom":makeQuery(id+"F8.opPattern","COPY",BODY,{"derivedFrom":makeQuery(id+"F6.opPattern","COPY",BODY,{"derivedFrom":makeQuery(id+"F4.opPattern","COPY",BODY,{"derivedFrom":makeQuery(id+"F3.opPattern","COPY",BODY,{"derivedFrom":makeQuery(id+"F1.opExtrude","SWEPT_BODY",BODY,{"disambiguationData":[OSD([sQuery(id+"F0.wireOp",EDGE,"E1.0"),sQuery(id+"F0.wireOp",EDGE,"E1.1"),sQuery(id+"F0.wireOp",EDGE,"E1.2"),sQuery(id+"F0.wireOp",EDGE,"E1.3"),sQuery(id+"F0.wireOp",EDGE,"E1.4"),sQuery(id+"F0.wireOp",EDGE,"E1.5"),sQuery(id+"F0.wireOp",EDGE,"E3.0"),sQuery(id+"F0.wireOp",EDGE,"E3.1"),sQuery(id+"F0.wireOp",EDGE,"E3.2"),sQuery(id+"F0.wireOp",EDGE,"E3.3"),sQuery(id+"F0.wireOp",EDGE,"E3.4"),sQuery(id+"F0.wireOp",EDGE,"E3.5")])]}),"instanceName":"1"}),"instanceName":"1"}),"instanceName":"1"}),"instanceName":"1"}),"instanceName":"1"});
            var Q28;
            Q28=makeQuery(id+"F9.opPattern","COPY",BODY,{"derivedFrom":makeQuery(id+"F8.opPattern","COPY",BODY,{"derivedFrom":makeQuery(id+"F6.opPattern","COPY",BODY,{"derivedFrom":makeQuery(id+"F5.opPattern","COPY",BODY,{"derivedFrom":makeQuery(id+"F4.opPattern","COPY",BODY,{"derivedFrom":makeQuery(id+"F1.opExtrude","SWEPT_BODY",BODY,{"disambiguationData":[OSD([sQuery(id+"F0.wireOp",EDGE,"E1.0"),sQuery(id+"F0.wireOp",EDGE,"E1.1"),sQuery(id+"F0.wireOp",EDGE,"E1.2"),sQuery(id+"F0.wireOp",EDGE,"E1.3"),sQuery(id+"F0.wireOp",EDGE,"E1.4"),sQuery(id+"F0.wireOp",EDGE,"E1.5"),sQuery(id+"F0.wireOp",EDGE,"E3.0"),sQuery(id+"F0.wireOp",EDGE,"E3.1"),sQuery(id+"F0.wireOp",EDGE,"E3.2"),sQuery(id+"F0.wireOp",EDGE,"E3.3"),sQuery(id+"F0.wireOp",EDGE,"E3.4"),sQuery(id+"F0.wireOp",EDGE,"E3.5")])]}),"instanceName":"1"}),"instanceName":"1"}),"instanceName":"1"}),"instanceName":"1"}),"instanceName":"1"});
            var Q29;
            Q29=makeQuery(id+"F9.opPattern","COPY",BODY,{"derivedFrom":makeQuery(id+"F8.opPattern","COPY",BODY,{"derivedFrom":makeQuery(id+"F6.opPattern","COPY",BODY,{"derivedFrom":makeQuery(id+"F5.opPattern","COPY",BODY,{"derivedFrom":makeQuery(id+"F4.opPattern","COPY",BODY,{"derivedFrom":makeQuery(id+"F3.opPattern","COPY",BODY,{"derivedFrom":makeQuery(id+"F1.opExtrude","SWEPT_BODY",BODY,{"disambiguationData":[OSD([sQuery(id+"F0.wireOp",EDGE,"E1.0"),sQuery(id+"F0.wireOp",EDGE,"E1.1"),sQuery(id+"F0.wireOp",EDGE,"E1.2"),sQuery(id+"F0.wireOp",EDGE,"E1.3"),sQuery(id+"F0.wireOp",EDGE,"E1.4"),sQuery(id+"F0.wireOp",EDGE,"E1.5"),sQuery(id+"F0.wireOp",EDGE,"E3.0"),sQuery(id+"F0.wireOp",EDGE,"E3.1"),sQuery(id+"F0.wireOp",EDGE,"E3.2"),sQuery(id+"F0.wireOp",EDGE,"E3.3"),sQuery(id+"F0.wireOp",EDGE,"E3.4"),sQuery(id+"F0.wireOp",EDGE,"E3.5")])]}),"instanceName":"1"}),"instanceName":"1"}),"instanceName":"1"}),"instanceName":"1"}),"instanceName":"1"}),"instanceName":"1"});
            var Q30;
            Q30=makeQuery(id+"F9.opPattern","COPY",BODY,{"derivedFrom":makeQuery(id+"F8.opPattern","COPY",BODY,{"derivedFrom":makeQuery(id+"F7.opPattern","COPY",BODY,{"derivedFrom":makeQuery(id+"F1.opExtrude","SWEPT_BODY",BODY,{"disambiguationData":[OSD([sQuery(id+"F0.wireOp",EDGE,"E1.0"),sQuery(id+"F0.wireOp",EDGE,"E1.1"),sQuery(id+"F0.wireOp",EDGE,"E1.2"),sQuery(id+"F0.wireOp",EDGE,"E1.3"),sQuery(id+"F0.wireOp",EDGE,"E1.4"),sQuery(id+"F0.wireOp",EDGE,"E1.5"),sQuery(id+"F0.wireOp",EDGE,"E3.0"),sQuery(id+"F0.wireOp",EDGE,"E3.1"),sQuery(id+"F0.wireOp",EDGE,"E3.2"),sQuery(id+"F0.wireOp",EDGE,"E3.3"),sQuery(id+"F0.wireOp",EDGE,"E3.4"),sQuery(id+"F0.wireOp",EDGE,"E3.5")])]}),"instanceName":"1"}),"instanceName":"1"}),"instanceName":"1"});
            var Q31;
            Q31=makeQuery(id+"F9.opPattern","COPY",BODY,{"derivedFrom":makeQuery(id+"F8.opPattern","COPY",BODY,{"derivedFrom":makeQuery(id+"F7.opPattern","COPY",BODY,{"derivedFrom":makeQuery(id+"F3.opPattern","COPY",BODY,{"derivedFrom":makeQuery(id+"F1.opExtrude","SWEPT_BODY",BODY,{"disambiguationData":[OSD([sQuery(id+"F0.wireOp",EDGE,"E1.0"),sQuery(id+"F0.wireOp",EDGE,"E1.1"),sQuery(id+"F0.wireOp",EDGE,"E1.2"),sQuery(id+"F0.wireOp",EDGE,"E1.3"),sQuery(id+"F0.wireOp",EDGE,"E1.4"),sQuery(id+"F0.wireOp",EDGE,"E1.5"),sQuery(id+"F0.wireOp",EDGE,"E3.0"),sQuery(id+"F0.wireOp",EDGE,"E3.1"),sQuery(id+"F0.wireOp",EDGE,"E3.2"),sQuery(id+"F0.wireOp",EDGE,"E3.3"),sQuery(id+"F0.wireOp",EDGE,"E3.4"),sQuery(id+"F0.wireOp",EDGE,"E3.5")])]}),"instanceName":"1"}),"instanceName":"1"}),"instanceName":"1"}),"instanceName":"1"});
            var Q32;
            Q32=makeQuery(id+"F9.opPattern","COPY",BODY,{"derivedFrom":makeQuery(id+"F8.opPattern","COPY",BODY,{"derivedFrom":makeQuery(id+"F7.opPattern","COPY",BODY,{"derivedFrom":makeQuery(id+"F4.opPattern","COPY",BODY,{"derivedFrom":makeQuery(id+"F1.opExtrude","SWEPT_BODY",BODY,{"disambiguationData":[OSD([sQuery(id+"F0.wireOp",EDGE,"E1.0"),sQuery(id+"F0.wireOp",EDGE,"E1.1"),sQuery(id+"F0.wireOp",EDGE,"E1.2"),sQuery(id+"F0.wireOp",EDGE,"E1.3"),sQuery(id+"F0.wireOp",EDGE,"E1.4"),sQuery(id+"F0.wireOp",EDGE,"E1.5"),sQuery(id+"F0.wireOp",EDGE,"E3.0"),sQuery(id+"F0.wireOp",EDGE,"E3.1"),sQuery(id+"F0.wireOp",EDGE,"E3.2"),sQuery(id+"F0.wireOp",EDGE,"E3.3"),sQuery(id+"F0.wireOp",EDGE,"E3.4"),sQuery(id+"F0.wireOp",EDGE,"E3.5")])]}),"instanceName":"1"}),"instanceName":"1"}),"instanceName":"1"}),"instanceName":"1"});
            var Q33;
            Q33=makeQuery(id+"F9.opPattern","COPY",BODY,{"derivedFrom":makeQuery(id+"F8.opPattern","COPY",BODY,{"derivedFrom":makeQuery(id+"F7.opPattern","COPY",BODY,{"derivedFrom":makeQuery(id+"F4.opPattern","COPY",BODY,{"derivedFrom":makeQuery(id+"F3.opPattern","COPY",BODY,{"derivedFrom":makeQuery(id+"F1.opExtrude","SWEPT_BODY",BODY,{"disambiguationData":[OSD([sQuery(id+"F0.wireOp",EDGE,"E1.0"),sQuery(id+"F0.wireOp",EDGE,"E1.1"),sQuery(id+"F0.wireOp",EDGE,"E1.2"),sQuery(id+"F0.wireOp",EDGE,"E1.3"),sQuery(id+"F0.wireOp",EDGE,"E1.4"),sQuery(id+"F0.wireOp",EDGE,"E1.5"),sQuery(id+"F0.wireOp",EDGE,"E3.0"),sQuery(id+"F0.wireOp",EDGE,"E3.1"),sQuery(id+"F0.wireOp",EDGE,"E3.2"),sQuery(id+"F0.wireOp",EDGE,"E3.3"),sQuery(id+"F0.wireOp",EDGE,"E3.4"),sQuery(id+"F0.wireOp",EDGE,"E3.5")])]}),"instanceName":"1"}),"instanceName":"1"}),"instanceName":"1"}),"instanceName":"1"}),"instanceName":"1"});
            var Q34;
            Q34=makeQuery(id+"F9.opPattern","COPY",BODY,{"derivedFrom":makeQuery(id+"F8.opPattern","COPY",BODY,{"derivedFrom":makeQuery(id+"F7.opPattern","COPY",BODY,{"derivedFrom":makeQuery(id+"F5.opPattern","COPY",BODY,{"derivedFrom":makeQuery(id+"F4.opPattern","COPY",BODY,{"derivedFrom":makeQuery(id+"F1.opExtrude","SWEPT_BODY",BODY,{"disambiguationData":[OSD([sQuery(id+"F0.wireOp",EDGE,"E1.0"),sQuery(id+"F0.wireOp",EDGE,"E1.1"),sQuery(id+"F0.wireOp",EDGE,"E1.2"),sQuery(id+"F0.wireOp",EDGE,"E1.3"),sQuery(id+"F0.wireOp",EDGE,"E1.4"),sQuery(id+"F0.wireOp",EDGE,"E1.5"),sQuery(id+"F0.wireOp",EDGE,"E3.0"),sQuery(id+"F0.wireOp",EDGE,"E3.1"),sQuery(id+"F0.wireOp",EDGE,"E3.2"),sQuery(id+"F0.wireOp",EDGE,"E3.3"),sQuery(id+"F0.wireOp",EDGE,"E3.4"),sQuery(id+"F0.wireOp",EDGE,"E3.5")])]}),"instanceName":"1"}),"instanceName":"1"}),"instanceName":"1"}),"instanceName":"1"}),"instanceName":"1"});
            var Q35;
            Q35=makeQuery(id+"F9.opPattern","COPY",BODY,{"derivedFrom":makeQuery(id+"F8.opPattern","COPY",BODY,{"derivedFrom":makeQuery(id+"F7.opPattern","COPY",BODY,{"derivedFrom":makeQuery(id+"F5.opPattern","COPY",BODY,{"derivedFrom":makeQuery(id+"F4.opPattern","COPY",BODY,{"derivedFrom":makeQuery(id+"F3.opPattern","COPY",BODY,{"derivedFrom":makeQuery(id+"F1.opExtrude","SWEPT_BODY",BODY,{"disambiguationData":[OSD([sQuery(id+"F0.wireOp",EDGE,"E1.0"),sQuery(id+"F0.wireOp",EDGE,"E1.1"),sQuery(id+"F0.wireOp",EDGE,"E1.2"),sQuery(id+"F0.wireOp",EDGE,"E1.3"),sQuery(id+"F0.wireOp",EDGE,"E1.4"),sQuery(id+"F0.wireOp",EDGE,"E1.5"),sQuery(id+"F0.wireOp",EDGE,"E3.0"),sQuery(id+"F0.wireOp",EDGE,"E3.1"),sQuery(id+"F0.wireOp",EDGE,"E3.2"),sQuery(id+"F0.wireOp",EDGE,"E3.3"),sQuery(id+"F0.wireOp",EDGE,"E3.4"),sQuery(id+"F0.wireOp",EDGE,"E3.5")])]}),"instanceName":"1"}),"instanceName":"1"}),"instanceName":"1"}),"instanceName":"1"}),"instanceName":"1"}),"instanceName":"1"});
            var Q36;
            Q36=makeQuery(id+"F8.opPattern","COPY",BODY,{"derivedFrom":makeQuery(id+"F7.opPattern","COPY",BODY,{"derivedFrom":makeQuery(id+"F6.opPattern","COPY",BODY,{"derivedFrom":makeQuery(id+"F1.opExtrude","SWEPT_BODY",BODY,{"disambiguationData":[OSD([sQuery(id+"F0.wireOp",EDGE,"E1.0"),sQuery(id+"F0.wireOp",EDGE,"E1.1"),sQuery(id+"F0.wireOp",EDGE,"E1.2"),sQuery(id+"F0.wireOp",EDGE,"E1.3"),sQuery(id+"F0.wireOp",EDGE,"E1.4"),sQuery(id+"F0.wireOp",EDGE,"E1.5"),sQuery(id+"F0.wireOp",EDGE,"E3.0"),sQuery(id+"F0.wireOp",EDGE,"E3.1"),sQuery(id+"F0.wireOp",EDGE,"E3.2"),sQuery(id+"F0.wireOp",EDGE,"E3.3"),sQuery(id+"F0.wireOp",EDGE,"E3.4"),sQuery(id+"F0.wireOp",EDGE,"E3.5")])]}),"instanceName":"1"}),"instanceName":"1"}),"instanceName":"1"});
            var Q37;
            Q37=makeQuery(id+"F8.opPattern","COPY",BODY,{"derivedFrom":makeQuery(id+"F7.opPattern","COPY",BODY,{"derivedFrom":makeQuery(id+"F6.opPattern","COPY",BODY,{"derivedFrom":makeQuery(id+"F3.opPattern","COPY",BODY,{"derivedFrom":makeQuery(id+"F1.opExtrude","SWEPT_BODY",BODY,{"disambiguationData":[OSD([sQuery(id+"F0.wireOp",EDGE,"E1.0"),sQuery(id+"F0.wireOp",EDGE,"E1.1"),sQuery(id+"F0.wireOp",EDGE,"E1.2"),sQuery(id+"F0.wireOp",EDGE,"E1.3"),sQuery(id+"F0.wireOp",EDGE,"E1.4"),sQuery(id+"F0.wireOp",EDGE,"E1.5"),sQuery(id+"F0.wireOp",EDGE,"E3.0"),sQuery(id+"F0.wireOp",EDGE,"E3.1"),sQuery(id+"F0.wireOp",EDGE,"E3.2"),sQuery(id+"F0.wireOp",EDGE,"E3.3"),sQuery(id+"F0.wireOp",EDGE,"E3.4"),sQuery(id+"F0.wireOp",EDGE,"E3.5")])]}),"instanceName":"1"}),"instanceName":"1"}),"instanceName":"1"}),"instanceName":"1"});
            var Q38;
            Q38=makeQuery(id+"F8.opPattern","COPY",BODY,{"derivedFrom":makeQuery(id+"F7.opPattern","COPY",BODY,{"derivedFrom":makeQuery(id+"F6.opPattern","COPY",BODY,{"derivedFrom":makeQuery(id+"F4.opPattern","COPY",BODY,{"derivedFrom":makeQuery(id+"F1.opExtrude","SWEPT_BODY",BODY,{"disambiguationData":[OSD([sQuery(id+"F0.wireOp",EDGE,"E1.0"),sQuery(id+"F0.wireOp",EDGE,"E1.1"),sQuery(id+"F0.wireOp",EDGE,"E1.2"),sQuery(id+"F0.wireOp",EDGE,"E1.3"),sQuery(id+"F0.wireOp",EDGE,"E1.4"),sQuery(id+"F0.wireOp",EDGE,"E1.5"),sQuery(id+"F0.wireOp",EDGE,"E3.0"),sQuery(id+"F0.wireOp",EDGE,"E3.1"),sQuery(id+"F0.wireOp",EDGE,"E3.2"),sQuery(id+"F0.wireOp",EDGE,"E3.3"),sQuery(id+"F0.wireOp",EDGE,"E3.4"),sQuery(id+"F0.wireOp",EDGE,"E3.5")])]}),"instanceName":"1"}),"instanceName":"1"}),"instanceName":"1"}),"instanceName":"1"});
            var Q39;
            Q39=makeQuery(id+"F8.opPattern","COPY",BODY,{"derivedFrom":makeQuery(id+"F7.opPattern","COPY",BODY,{"derivedFrom":makeQuery(id+"F6.opPattern","COPY",BODY,{"derivedFrom":makeQuery(id+"F4.opPattern","COPY",BODY,{"derivedFrom":makeQuery(id+"F3.opPattern","COPY",BODY,{"derivedFrom":makeQuery(id+"F1.opExtrude","SWEPT_BODY",BODY,{"disambiguationData":[OSD([sQuery(id+"F0.wireOp",EDGE,"E1.0"),sQuery(id+"F0.wireOp",EDGE,"E1.1"),sQuery(id+"F0.wireOp",EDGE,"E1.2"),sQuery(id+"F0.wireOp",EDGE,"E1.3"),sQuery(id+"F0.wireOp",EDGE,"E1.4"),sQuery(id+"F0.wireOp",EDGE,"E1.5"),sQuery(id+"F0.wireOp",EDGE,"E3.0"),sQuery(id+"F0.wireOp",EDGE,"E3.1"),sQuery(id+"F0.wireOp",EDGE,"E3.2"),sQuery(id+"F0.wireOp",EDGE,"E3.3"),sQuery(id+"F0.wireOp",EDGE,"E3.4"),sQuery(id+"F0.wireOp",EDGE,"E3.5")])]}),"instanceName":"1"}),"instanceName":"1"}),"instanceName":"1"}),"instanceName":"1"}),"instanceName":"1"});
            var Q40;
            Q40=makeQuery(id+"F8.opPattern","COPY",BODY,{"derivedFrom":makeQuery(id+"F7.opPattern","COPY",BODY,{"derivedFrom":makeQuery(id+"F6.opPattern","COPY",BODY,{"derivedFrom":makeQuery(id+"F5.opPattern","COPY",BODY,{"derivedFrom":makeQuery(id+"F4.opPattern","COPY",BODY,{"derivedFrom":makeQuery(id+"F1.opExtrude","SWEPT_BODY",BODY,{"disambiguationData":[OSD([sQuery(id+"F0.wireOp",EDGE,"E1.0"),sQuery(id+"F0.wireOp",EDGE,"E1.1"),sQuery(id+"F0.wireOp",EDGE,"E1.2"),sQuery(id+"F0.wireOp",EDGE,"E1.3"),sQuery(id+"F0.wireOp",EDGE,"E1.4"),sQuery(id+"F0.wireOp",EDGE,"E1.5"),sQuery(id+"F0.wireOp",EDGE,"E3.0"),sQuery(id+"F0.wireOp",EDGE,"E3.1"),sQuery(id+"F0.wireOp",EDGE,"E3.2"),sQuery(id+"F0.wireOp",EDGE,"E3.3"),sQuery(id+"F0.wireOp",EDGE,"E3.4"),sQuery(id+"F0.wireOp",EDGE,"E3.5")])]}),"instanceName":"1"}),"instanceName":"1"}),"instanceName":"1"}),"instanceName":"1"}),"instanceName":"1"});
            var Q41;
            Q41=makeQuery(id+"F9.opPattern","COPY",BODY,{"derivedFrom":makeQuery(id+"F8.opPattern","COPY",BODY,{"derivedFrom":makeQuery(id+"F7.opPattern","COPY",BODY,{"derivedFrom":makeQuery(id+"F6.opPattern","COPY",BODY,{"derivedFrom":makeQuery(id+"F1.opExtrude","SWEPT_BODY",BODY,{"disambiguationData":[OSD([sQuery(id+"F0.wireOp",EDGE,"E1.0"),sQuery(id+"F0.wireOp",EDGE,"E1.1"),sQuery(id+"F0.wireOp",EDGE,"E1.2"),sQuery(id+"F0.wireOp",EDGE,"E1.3"),sQuery(id+"F0.wireOp",EDGE,"E1.4"),sQuery(id+"F0.wireOp",EDGE,"E1.5"),sQuery(id+"F0.wireOp",EDGE,"E3.0"),sQuery(id+"F0.wireOp",EDGE,"E3.1"),sQuery(id+"F0.wireOp",EDGE,"E3.2"),sQuery(id+"F0.wireOp",EDGE,"E3.3"),sQuery(id+"F0.wireOp",EDGE,"E3.4"),sQuery(id+"F0.wireOp",EDGE,"E3.5")])]}),"instanceName":"1"}),"instanceName":"1"}),"instanceName":"1"}),"instanceName":"1"});
            var Q42;
            Q42=makeQuery(id+"F9.opPattern","COPY",BODY,{"derivedFrom":makeQuery(id+"F8.opPattern","COPY",BODY,{"derivedFrom":makeQuery(id+"F7.opPattern","COPY",BODY,{"derivedFrom":makeQuery(id+"F6.opPattern","COPY",BODY,{"derivedFrom":makeQuery(id+"F3.opPattern","COPY",BODY,{"derivedFrom":makeQuery(id+"F1.opExtrude","SWEPT_BODY",BODY,{"disambiguationData":[OSD([sQuery(id+"F0.wireOp",EDGE,"E1.0"),sQuery(id+"F0.wireOp",EDGE,"E1.1"),sQuery(id+"F0.wireOp",EDGE,"E1.2"),sQuery(id+"F0.wireOp",EDGE,"E1.3"),sQuery(id+"F0.wireOp",EDGE,"E1.4"),sQuery(id+"F0.wireOp",EDGE,"E1.5"),sQuery(id+"F0.wireOp",EDGE,"E3.0"),sQuery(id+"F0.wireOp",EDGE,"E3.1"),sQuery(id+"F0.wireOp",EDGE,"E3.2"),sQuery(id+"F0.wireOp",EDGE,"E3.3"),sQuery(id+"F0.wireOp",EDGE,"E3.4"),sQuery(id+"F0.wireOp",EDGE,"E3.5")])]}),"instanceName":"1"}),"instanceName":"1"}),"instanceName":"1"}),"instanceName":"1"}),"instanceName":"1"});
            var Q43;
            Q43=makeQuery(id+"F9.opPattern","COPY",BODY,{"derivedFrom":makeQuery(id+"F8.opPattern","COPY",BODY,{"derivedFrom":makeQuery(id+"F7.opPattern","COPY",BODY,{"derivedFrom":makeQuery(id+"F6.opPattern","COPY",BODY,{"derivedFrom":makeQuery(id+"F4.opPattern","COPY",BODY,{"derivedFrom":makeQuery(id+"F1.opExtrude","SWEPT_BODY",BODY,{"disambiguationData":[OSD([sQuery(id+"F0.wireOp",EDGE,"E1.0"),sQuery(id+"F0.wireOp",EDGE,"E1.1"),sQuery(id+"F0.wireOp",EDGE,"E1.2"),sQuery(id+"F0.wireOp",EDGE,"E1.3"),sQuery(id+"F0.wireOp",EDGE,"E1.4"),sQuery(id+"F0.wireOp",EDGE,"E1.5"),sQuery(id+"F0.wireOp",EDGE,"E3.0"),sQuery(id+"F0.wireOp",EDGE,"E3.1"),sQuery(id+"F0.wireOp",EDGE,"E3.2"),sQuery(id+"F0.wireOp",EDGE,"E3.3"),sQuery(id+"F0.wireOp",EDGE,"E3.4"),sQuery(id+"F0.wireOp",EDGE,"E3.5")])]}),"instanceName":"1"}),"instanceName":"1"}),"instanceName":"1"}),"instanceName":"1"}),"instanceName":"1"});
            var Q44;
            Q44=makeQuery(id+"F9.opPattern","COPY",BODY,{"derivedFrom":makeQuery(id+"F8.opPattern","COPY",BODY,{"derivedFrom":makeQuery(id+"F7.opPattern","COPY",BODY,{"derivedFrom":makeQuery(id+"F6.opPattern","COPY",BODY,{"derivedFrom":makeQuery(id+"F4.opPattern","COPY",BODY,{"derivedFrom":makeQuery(id+"F3.opPattern","COPY",BODY,{"derivedFrom":makeQuery(id+"F1.opExtrude","SWEPT_BODY",BODY,{"disambiguationData":[OSD([sQuery(id+"F0.wireOp",EDGE,"E1.0"),sQuery(id+"F0.wireOp",EDGE,"E1.1"),sQuery(id+"F0.wireOp",EDGE,"E1.2"),sQuery(id+"F0.wireOp",EDGE,"E1.3"),sQuery(id+"F0.wireOp",EDGE,"E1.4"),sQuery(id+"F0.wireOp",EDGE,"E1.5"),sQuery(id+"F0.wireOp",EDGE,"E3.0"),sQuery(id+"F0.wireOp",EDGE,"E3.1"),sQuery(id+"F0.wireOp",EDGE,"E3.2"),sQuery(id+"F0.wireOp",EDGE,"E3.3"),sQuery(id+"F0.wireOp",EDGE,"E3.4"),sQuery(id+"F0.wireOp",EDGE,"E3.5")])]}),"instanceName":"1"}),"instanceName":"1"}),"instanceName":"1"}),"instanceName":"1"}),"instanceName":"1"}),"instanceName":"1"});
            var Q45;
            Q45=makeQuery(id+"F9.opPattern","COPY",BODY,{"derivedFrom":makeQuery(id+"F8.opPattern","COPY",BODY,{"derivedFrom":makeQuery(id+"F7.opPattern","COPY",BODY,{"derivedFrom":makeQuery(id+"F6.opPattern","COPY",BODY,{"derivedFrom":makeQuery(id+"F5.opPattern","COPY",BODY,{"derivedFrom":makeQuery(id+"F4.opPattern","COPY",BODY,{"derivedFrom":makeQuery(id+"F1.opExtrude","SWEPT_BODY",BODY,{"disambiguationData":[OSD([sQuery(id+"F0.wireOp",EDGE,"E1.0"),sQuery(id+"F0.wireOp",EDGE,"E1.1"),sQuery(id+"F0.wireOp",EDGE,"E1.2"),sQuery(id+"F0.wireOp",EDGE,"E1.3"),sQuery(id+"F0.wireOp",EDGE,"E1.4"),sQuery(id+"F0.wireOp",EDGE,"E1.5"),sQuery(id+"F0.wireOp",EDGE,"E3.0"),sQuery(id+"F0.wireOp",EDGE,"E3.1"),sQuery(id+"F0.wireOp",EDGE,"E3.2"),sQuery(id+"F0.wireOp",EDGE,"E3.3"),sQuery(id+"F0.wireOp",EDGE,"E3.4"),sQuery(id+"F0.wireOp",EDGE,"E3.5")])]}),"instanceName":"1"}),"instanceName":"1"}),"instanceName":"1"}),"instanceName":"1"}),"instanceName":"1"}),"instanceName":"1"});
            var Q46;
            Q46=makeQuery(id+"F10.opPattern","COPY",BODY,{"derivedFrom":makeQuery(id+"F9.opPattern","COPY",BODY,{"derivedFrom":makeQuery(id+"F8.opPattern","COPY",BODY,{"derivedFrom":makeQuery(id+"F7.opPattern","COPY",BODY,{"derivedFrom":makeQuery(id+"F6.opPattern","COPY",BODY,{"derivedFrom":makeQuery(id+"F5.opPattern","COPY",BODY,{"derivedFrom":makeQuery(id+"F4.opPattern","COPY",BODY,{"derivedFrom":makeQuery(id+"F1.opExtrude","SWEPT_BODY",BODY,{"disambiguationData":[OSD([sQuery(id+"F0.wireOp",EDGE,"E1.0"),sQuery(id+"F0.wireOp",EDGE,"E1.1"),sQuery(id+"F0.wireOp",EDGE,"E1.2"),sQuery(id+"F0.wireOp",EDGE,"E1.3"),sQuery(id+"F0.wireOp",EDGE,"E1.4"),sQuery(id+"F0.wireOp",EDGE,"E1.5"),sQuery(id+"F0.wireOp",EDGE,"E3.0"),sQuery(id+"F0.wireOp",EDGE,"E3.1"),sQuery(id+"F0.wireOp",EDGE,"E3.2"),sQuery(id+"F0.wireOp",EDGE,"E3.3"),sQuery(id+"F0.wireOp",EDGE,"E3.4"),sQuery(id+"F0.wireOp",EDGE,"E3.5")])]}),"instanceName":"1"}),"instanceName":"1"}),"instanceName":"1"}),"instanceName":"1"}),"instanceName":"1"}),"instanceName":"1"}),"instanceName":"1"});
            transform(context, id + "F11", {"entities" : qUnion([Q0, Q1, Q2, Q3, Q4, Q5, Q6, Q7, Q8, Q9, Q10, Q11, Q12, Q13, Q14, Q15, Q16, Q17, Q18, Q19, Q20, Q21, Q22, Q23, Q24, Q25, Q26, Q27, Q28, Q29, Q30, Q31, Q32, Q33, Q34, Q35, Q36, Q37, Q38, Q39, Q40, Q41, Q42, Q43, Q44, Q45, Q46]), "transformType" : TransformType.TRANSLATION_3D, "dx" : 0 * mm, "dy" : -14.6 * mm, "dz" : 0 * mm, "makeCopy" : true});
        }
        {
            var Q0;
            Q0=makeQuery(id+"F7.opPattern","COPY",BODY,{"derivedFrom":makeQuery(id+"F6.opPattern","COPY",BODY,{"derivedFrom":makeQuery(id+"F5.opPattern","COPY",BODY,{"derivedFrom":makeQuery(id+"F4.opPattern","COPY",BODY,{"derivedFrom":makeQuery(id+"F3.opPattern","COPY",BODY,{"derivedFrom":makeQuery(id+"F1.opExtrude","SWEPT_BODY",BODY,{"disambiguationData":[OSD([sQuery(id+"F0.wireOp",EDGE,"E1.0"),sQuery(id+"F0.wireOp",EDGE,"E1.1"),sQuery(id+"F0.wireOp",EDGE,"E1.2"),sQuery(id+"F0.wireOp",EDGE,"E1.3"),sQuery(id+"F0.wireOp",EDGE,"E1.4"),sQuery(id+"F0.wireOp",EDGE,"E1.5"),sQuery(id+"F0.wireOp",EDGE,"E3.0"),sQuery(id+"F0.wireOp",EDGE,"E3.1"),sQuery(id+"F0.wireOp",EDGE,"E3.2"),sQuery(id+"F0.wireOp",EDGE,"E3.3"),sQuery(id+"F0.wireOp",EDGE,"E3.4"),sQuery(id+"F0.wireOp",EDGE,"E3.5")])]}),"instanceName":"1"}),"instanceName":"1"}),"instanceName":"1"}),"instanceName":"1"}),"instanceName":"1"});
            var Q1;
            Q1=makeQuery(id+"F7.opPattern","COPY",BODY,{"derivedFrom":makeQuery(id+"F6.opPattern","COPY",BODY,{"derivedFrom":makeQuery(id+"F3.opPattern","COPY",BODY,{"derivedFrom":makeQuery(id+"F1.opExtrude","SWEPT_BODY",BODY,{"disambiguationData":[OSD([sQuery(id+"F0.wireOp",EDGE,"E1.0"),sQuery(id+"F0.wireOp",EDGE,"E1.1"),sQuery(id+"F0.wireOp",EDGE,"E1.2"),sQuery(id+"F0.wireOp",EDGE,"E1.3"),sQuery(id+"F0.wireOp",EDGE,"E1.4"),sQuery(id+"F0.wireOp",EDGE,"E1.5"),sQuery(id+"F0.wireOp",EDGE,"E3.0"),sQuery(id+"F0.wireOp",EDGE,"E3.1"),sQuery(id+"F0.wireOp",EDGE,"E3.2"),sQuery(id+"F0.wireOp",EDGE,"E3.3"),sQuery(id+"F0.wireOp",EDGE,"E3.4"),sQuery(id+"F0.wireOp",EDGE,"E3.5")])]}),"instanceName":"1"}),"instanceName":"1"}),"instanceName":"1"});
            var Q2;
            Q2=makeQuery(id+"F7.opPattern","COPY",BODY,{"derivedFrom":makeQuery(id+"F6.opPattern","COPY",BODY,{"derivedFrom":makeQuery(id+"F4.opPattern","COPY",BODY,{"derivedFrom":makeQuery(id+"F1.opExtrude","SWEPT_BODY",BODY,{"disambiguationData":[OSD([sQuery(id+"F0.wireOp",EDGE,"E1.0"),sQuery(id+"F0.wireOp",EDGE,"E1.1"),sQuery(id+"F0.wireOp",EDGE,"E1.2"),sQuery(id+"F0.wireOp",EDGE,"E1.3"),sQuery(id+"F0.wireOp",EDGE,"E1.4"),sQuery(id+"F0.wireOp",EDGE,"E1.5"),sQuery(id+"F0.wireOp",EDGE,"E3.0"),sQuery(id+"F0.wireOp",EDGE,"E3.1"),sQuery(id+"F0.wireOp",EDGE,"E3.2"),sQuery(id+"F0.wireOp",EDGE,"E3.3"),sQuery(id+"F0.wireOp",EDGE,"E3.4"),sQuery(id+"F0.wireOp",EDGE,"E3.5")])]}),"instanceName":"1"}),"instanceName":"1"}),"instanceName":"1"});
            var Q3;
            Q3=makeQuery(id+"F7.opPattern","COPY",BODY,{"derivedFrom":makeQuery(id+"F6.opPattern","COPY",BODY,{"derivedFrom":makeQuery(id+"F4.opPattern","COPY",BODY,{"derivedFrom":makeQuery(id+"F3.opPattern","COPY",BODY,{"derivedFrom":makeQuery(id+"F1.opExtrude","SWEPT_BODY",BODY,{"disambiguationData":[OSD([sQuery(id+"F0.wireOp",EDGE,"E1.0"),sQuery(id+"F0.wireOp",EDGE,"E1.1"),sQuery(id+"F0.wireOp",EDGE,"E1.2"),sQuery(id+"F0.wireOp",EDGE,"E1.3"),sQuery(id+"F0.wireOp",EDGE,"E1.4"),sQuery(id+"F0.wireOp",EDGE,"E1.5"),sQuery(id+"F0.wireOp",EDGE,"E3.0"),sQuery(id+"F0.wireOp",EDGE,"E3.1"),sQuery(id+"F0.wireOp",EDGE,"E3.2"),sQuery(id+"F0.wireOp",EDGE,"E3.3"),sQuery(id+"F0.wireOp",EDGE,"E3.4"),sQuery(id+"F0.wireOp",EDGE,"E3.5")])]}),"instanceName":"1"}),"instanceName":"1"}),"instanceName":"1"}),"instanceName":"1"});
            var Q4;
            Q4=makeQuery(id+"F7.opPattern","COPY",BODY,{"derivedFrom":makeQuery(id+"F6.opPattern","COPY",BODY,{"derivedFrom":makeQuery(id+"F5.opPattern","COPY",BODY,{"derivedFrom":makeQuery(id+"F4.opPattern","COPY",BODY,{"derivedFrom":makeQuery(id+"F1.opExtrude","SWEPT_BODY",BODY,{"disambiguationData":[OSD([sQuery(id+"F0.wireOp",EDGE,"E1.0"),sQuery(id+"F0.wireOp",EDGE,"E1.1"),sQuery(id+"F0.wireOp",EDGE,"E1.2"),sQuery(id+"F0.wireOp",EDGE,"E1.3"),sQuery(id+"F0.wireOp",EDGE,"E1.4"),sQuery(id+"F0.wireOp",EDGE,"E1.5"),sQuery(id+"F0.wireOp",EDGE,"E3.0"),sQuery(id+"F0.wireOp",EDGE,"E3.1"),sQuery(id+"F0.wireOp",EDGE,"E3.2"),sQuery(id+"F0.wireOp",EDGE,"E3.3"),sQuery(id+"F0.wireOp",EDGE,"E3.4"),sQuery(id+"F0.wireOp",EDGE,"E3.5")])]}),"instanceName":"1"}),"instanceName":"1"}),"instanceName":"1"}),"instanceName":"1"});
            var Q5;
            Q5=makeQuery(id+"F7.opPattern","COPY",BODY,{"derivedFrom":makeQuery(id+"F5.opPattern","COPY",BODY,{"derivedFrom":makeQuery(id+"F4.opPattern","COPY",BODY,{"derivedFrom":makeQuery(id+"F1.opExtrude","SWEPT_BODY",BODY,{"disambiguationData":[OSD([sQuery(id+"F0.wireOp",EDGE,"E1.0"),sQuery(id+"F0.wireOp",EDGE,"E1.1"),sQuery(id+"F0.wireOp",EDGE,"E1.2"),sQuery(id+"F0.wireOp",EDGE,"E1.3"),sQuery(id+"F0.wireOp",EDGE,"E1.4"),sQuery(id+"F0.wireOp",EDGE,"E1.5"),sQuery(id+"F0.wireOp",EDGE,"E3.0"),sQuery(id+"F0.wireOp",EDGE,"E3.1"),sQuery(id+"F0.wireOp",EDGE,"E3.2"),sQuery(id+"F0.wireOp",EDGE,"E3.3"),sQuery(id+"F0.wireOp",EDGE,"E3.4"),sQuery(id+"F0.wireOp",EDGE,"E3.5")])]}),"instanceName":"1"}),"instanceName":"1"}),"instanceName":"1"});
            var Q6;
            Q6=makeQuery(id+"F7.opPattern","COPY",BODY,{"derivedFrom":makeQuery(id+"F4.opPattern","COPY",BODY,{"derivedFrom":makeQuery(id+"F3.opPattern","COPY",BODY,{"derivedFrom":makeQuery(id+"F1.opExtrude","SWEPT_BODY",BODY,{"disambiguationData":[OSD([sQuery(id+"F0.wireOp",EDGE,"E1.0"),sQuery(id+"F0.wireOp",EDGE,"E1.1"),sQuery(id+"F0.wireOp",EDGE,"E1.2"),sQuery(id+"F0.wireOp",EDGE,"E1.3"),sQuery(id+"F0.wireOp",EDGE,"E1.4"),sQuery(id+"F0.wireOp",EDGE,"E1.5"),sQuery(id+"F0.wireOp",EDGE,"E3.0"),sQuery(id+"F0.wireOp",EDGE,"E3.1"),sQuery(id+"F0.wireOp",EDGE,"E3.2"),sQuery(id+"F0.wireOp",EDGE,"E3.3"),sQuery(id+"F0.wireOp",EDGE,"E3.4"),sQuery(id+"F0.wireOp",EDGE,"E3.5")])]}),"instanceName":"1"}),"instanceName":"1"}),"instanceName":"1"});
            var Q7;
            Q7=makeQuery(id+"F7.opPattern","COPY",BODY,{"derivedFrom":makeQuery(id+"F5.opPattern","COPY",BODY,{"derivedFrom":makeQuery(id+"F4.opPattern","COPY",BODY,{"derivedFrom":makeQuery(id+"F3.opPattern","COPY",BODY,{"derivedFrom":makeQuery(id+"F1.opExtrude","SWEPT_BODY",BODY,{"disambiguationData":[OSD([sQuery(id+"F0.wireOp",EDGE,"E1.0"),sQuery(id+"F0.wireOp",EDGE,"E1.1"),sQuery(id+"F0.wireOp",EDGE,"E1.2"),sQuery(id+"F0.wireOp",EDGE,"E1.3"),sQuery(id+"F0.wireOp",EDGE,"E1.4"),sQuery(id+"F0.wireOp",EDGE,"E1.5"),sQuery(id+"F0.wireOp",EDGE,"E3.0"),sQuery(id+"F0.wireOp",EDGE,"E3.1"),sQuery(id+"F0.wireOp",EDGE,"E3.2"),sQuery(id+"F0.wireOp",EDGE,"E3.3"),sQuery(id+"F0.wireOp",EDGE,"E3.4"),sQuery(id+"F0.wireOp",EDGE,"E3.5")])]}),"instanceName":"1"}),"instanceName":"1"}),"instanceName":"1"}),"instanceName":"1"});
            var Q8;
            Q8=makeQuery(id+"F7.opPattern","COPY",BODY,{"derivedFrom":makeQuery(id+"F6.opPattern","COPY",BODY,{"derivedFrom":makeQuery(id+"F1.opExtrude","SWEPT_BODY",BODY,{"disambiguationData":[OSD([sQuery(id+"F0.wireOp",EDGE,"E1.0"),sQuery(id+"F0.wireOp",EDGE,"E1.1"),sQuery(id+"F0.wireOp",EDGE,"E1.2"),sQuery(id+"F0.wireOp",EDGE,"E1.3"),sQuery(id+"F0.wireOp",EDGE,"E1.4"),sQuery(id+"F0.wireOp",EDGE,"E1.5"),sQuery(id+"F0.wireOp",EDGE,"E3.0"),sQuery(id+"F0.wireOp",EDGE,"E3.1"),sQuery(id+"F0.wireOp",EDGE,"E3.2"),sQuery(id+"F0.wireOp",EDGE,"E3.3"),sQuery(id+"F0.wireOp",EDGE,"E3.4"),sQuery(id+"F0.wireOp",EDGE,"E3.5")])]}),"instanceName":"1"}),"instanceName":"1"});
            var Q9;
            Q9=makeQuery(id+"F7.opPattern","COPY",BODY,{"derivedFrom":makeQuery(id+"F4.opPattern","COPY",BODY,{"derivedFrom":makeQuery(id+"F1.opExtrude","SWEPT_BODY",BODY,{"disambiguationData":[OSD([sQuery(id+"F0.wireOp",EDGE,"E1.0"),sQuery(id+"F0.wireOp",EDGE,"E1.1"),sQuery(id+"F0.wireOp",EDGE,"E1.2"),sQuery(id+"F0.wireOp",EDGE,"E1.3"),sQuery(id+"F0.wireOp",EDGE,"E1.4"),sQuery(id+"F0.wireOp",EDGE,"E1.5"),sQuery(id+"F0.wireOp",EDGE,"E3.0"),sQuery(id+"F0.wireOp",EDGE,"E3.1"),sQuery(id+"F0.wireOp",EDGE,"E3.2"),sQuery(id+"F0.wireOp",EDGE,"E3.3"),sQuery(id+"F0.wireOp",EDGE,"E3.4"),sQuery(id+"F0.wireOp",EDGE,"E3.5")])]}),"instanceName":"1"}),"instanceName":"1"});
            var Q10;
            Q10=makeQuery(id+"F7.opPattern","COPY",BODY,{"derivedFrom":makeQuery(id+"F3.opPattern","COPY",BODY,{"derivedFrom":makeQuery(id+"F1.opExtrude","SWEPT_BODY",BODY,{"disambiguationData":[OSD([sQuery(id+"F0.wireOp",EDGE,"E1.0"),sQuery(id+"F0.wireOp",EDGE,"E1.1"),sQuery(id+"F0.wireOp",EDGE,"E1.2"),sQuery(id+"F0.wireOp",EDGE,"E1.3"),sQuery(id+"F0.wireOp",EDGE,"E1.4"),sQuery(id+"F0.wireOp",EDGE,"E1.5"),sQuery(id+"F0.wireOp",EDGE,"E3.0"),sQuery(id+"F0.wireOp",EDGE,"E3.1"),sQuery(id+"F0.wireOp",EDGE,"E3.2"),sQuery(id+"F0.wireOp",EDGE,"E3.3"),sQuery(id+"F0.wireOp",EDGE,"E3.4"),sQuery(id+"F0.wireOp",EDGE,"E3.5")])]}),"instanceName":"1"}),"instanceName":"1"});
            var Q11;
            Q11=makeQuery(id+"F7.opPattern","COPY",BODY,{"derivedFrom":makeQuery(id+"F1.opExtrude","SWEPT_BODY",BODY,{"disambiguationData":[OSD([sQuery(id+"F0.wireOp",EDGE,"E1.0"),sQuery(id+"F0.wireOp",EDGE,"E1.1"),sQuery(id+"F0.wireOp",EDGE,"E1.2"),sQuery(id+"F0.wireOp",EDGE,"E1.3"),sQuery(id+"F0.wireOp",EDGE,"E1.4"),sQuery(id+"F0.wireOp",EDGE,"E1.5"),sQuery(id+"F0.wireOp",EDGE,"E3.0"),sQuery(id+"F0.wireOp",EDGE,"E3.1"),sQuery(id+"F0.wireOp",EDGE,"E3.2"),sQuery(id+"F0.wireOp",EDGE,"E3.3"),sQuery(id+"F0.wireOp",EDGE,"E3.4"),sQuery(id+"F0.wireOp",EDGE,"E3.5")])]}),"instanceName":"1"});
            var Q12;
            Q12=makeQuery(id+"F9.opPattern","COPY",BODY,{"derivedFrom":makeQuery(id+"F7.opPattern","COPY",BODY,{"derivedFrom":makeQuery(id+"F1.opExtrude","SWEPT_BODY",BODY,{"disambiguationData":[OSD([sQuery(id+"F0.wireOp",EDGE,"E1.0"),sQuery(id+"F0.wireOp",EDGE,"E1.1"),sQuery(id+"F0.wireOp",EDGE,"E1.2"),sQuery(id+"F0.wireOp",EDGE,"E1.3"),sQuery(id+"F0.wireOp",EDGE,"E1.4"),sQuery(id+"F0.wireOp",EDGE,"E1.5"),sQuery(id+"F0.wireOp",EDGE,"E3.0"),sQuery(id+"F0.wireOp",EDGE,"E3.1"),sQuery(id+"F0.wireOp",EDGE,"E3.2"),sQuery(id+"F0.wireOp",EDGE,"E3.3"),sQuery(id+"F0.wireOp",EDGE,"E3.4"),sQuery(id+"F0.wireOp",EDGE,"E3.5")])]}),"instanceName":"1"}),"instanceName":"1"});
            var Q13;
            Q13=makeQuery(id+"F9.opPattern","COPY",BODY,{"derivedFrom":makeQuery(id+"F7.opPattern","COPY",BODY,{"derivedFrom":makeQuery(id+"F3.opPattern","COPY",BODY,{"derivedFrom":makeQuery(id+"F1.opExtrude","SWEPT_BODY",BODY,{"disambiguationData":[OSD([sQuery(id+"F0.wireOp",EDGE,"E1.0"),sQuery(id+"F0.wireOp",EDGE,"E1.1"),sQuery(id+"F0.wireOp",EDGE,"E1.2"),sQuery(id+"F0.wireOp",EDGE,"E1.3"),sQuery(id+"F0.wireOp",EDGE,"E1.4"),sQuery(id+"F0.wireOp",EDGE,"E1.5"),sQuery(id+"F0.wireOp",EDGE,"E3.0"),sQuery(id+"F0.wireOp",EDGE,"E3.1"),sQuery(id+"F0.wireOp",EDGE,"E3.2"),sQuery(id+"F0.wireOp",EDGE,"E3.3"),sQuery(id+"F0.wireOp",EDGE,"E3.4"),sQuery(id+"F0.wireOp",EDGE,"E3.5")])]}),"instanceName":"1"}),"instanceName":"1"}),"instanceName":"1"});
            var Q14;
            Q14=makeQuery(id+"F9.opPattern","COPY",BODY,{"derivedFrom":makeQuery(id+"F7.opPattern","COPY",BODY,{"derivedFrom":makeQuery(id+"F4.opPattern","COPY",BODY,{"derivedFrom":makeQuery(id+"F1.opExtrude","SWEPT_BODY",BODY,{"disambiguationData":[OSD([sQuery(id+"F0.wireOp",EDGE,"E1.0"),sQuery(id+"F0.wireOp",EDGE,"E1.1"),sQuery(id+"F0.wireOp",EDGE,"E1.2"),sQuery(id+"F0.wireOp",EDGE,"E1.3"),sQuery(id+"F0.wireOp",EDGE,"E1.4"),sQuery(id+"F0.wireOp",EDGE,"E1.5"),sQuery(id+"F0.wireOp",EDGE,"E3.0"),sQuery(id+"F0.wireOp",EDGE,"E3.1"),sQuery(id+"F0.wireOp",EDGE,"E3.2"),sQuery(id+"F0.wireOp",EDGE,"E3.3"),sQuery(id+"F0.wireOp",EDGE,"E3.4"),sQuery(id+"F0.wireOp",EDGE,"E3.5")])]}),"instanceName":"1"}),"instanceName":"1"}),"instanceName":"1"});
            var Q15;
            Q15=makeQuery(id+"F9.opPattern","COPY",BODY,{"derivedFrom":makeQuery(id+"F7.opPattern","COPY",BODY,{"derivedFrom":makeQuery(id+"F4.opPattern","COPY",BODY,{"derivedFrom":makeQuery(id+"F3.opPattern","COPY",BODY,{"derivedFrom":makeQuery(id+"F1.opExtrude","SWEPT_BODY",BODY,{"disambiguationData":[OSD([sQuery(id+"F0.wireOp",EDGE,"E1.0"),sQuery(id+"F0.wireOp",EDGE,"E1.1"),sQuery(id+"F0.wireOp",EDGE,"E1.2"),sQuery(id+"F0.wireOp",EDGE,"E1.3"),sQuery(id+"F0.wireOp",EDGE,"E1.4"),sQuery(id+"F0.wireOp",EDGE,"E1.5"),sQuery(id+"F0.wireOp",EDGE,"E3.0"),sQuery(id+"F0.wireOp",EDGE,"E3.1"),sQuery(id+"F0.wireOp",EDGE,"E3.2"),sQuery(id+"F0.wireOp",EDGE,"E3.3"),sQuery(id+"F0.wireOp",EDGE,"E3.4"),sQuery(id+"F0.wireOp",EDGE,"E3.5")])]}),"instanceName":"1"}),"instanceName":"1"}),"instanceName":"1"}),"instanceName":"1"});
            var Q16;
            Q16=makeQuery(id+"F9.opPattern","COPY",BODY,{"derivedFrom":makeQuery(id+"F7.opPattern","COPY",BODY,{"derivedFrom":makeQuery(id+"F5.opPattern","COPY",BODY,{"derivedFrom":makeQuery(id+"F4.opPattern","COPY",BODY,{"derivedFrom":makeQuery(id+"F1.opExtrude","SWEPT_BODY",BODY,{"disambiguationData":[OSD([sQuery(id+"F0.wireOp",EDGE,"E1.0"),sQuery(id+"F0.wireOp",EDGE,"E1.1"),sQuery(id+"F0.wireOp",EDGE,"E1.2"),sQuery(id+"F0.wireOp",EDGE,"E1.3"),sQuery(id+"F0.wireOp",EDGE,"E1.4"),sQuery(id+"F0.wireOp",EDGE,"E1.5"),sQuery(id+"F0.wireOp",EDGE,"E3.0"),sQuery(id+"F0.wireOp",EDGE,"E3.1"),sQuery(id+"F0.wireOp",EDGE,"E3.2"),sQuery(id+"F0.wireOp",EDGE,"E3.3"),sQuery(id+"F0.wireOp",EDGE,"E3.4"),sQuery(id+"F0.wireOp",EDGE,"E3.5")])]}),"instanceName":"1"}),"instanceName":"1"}),"instanceName":"1"}),"instanceName":"1"});
            var Q17;
            Q17=makeQuery(id+"F9.opPattern","COPY",BODY,{"derivedFrom":makeQuery(id+"F7.opPattern","COPY",BODY,{"derivedFrom":makeQuery(id+"F5.opPattern","COPY",BODY,{"derivedFrom":makeQuery(id+"F4.opPattern","COPY",BODY,{"derivedFrom":makeQuery(id+"F3.opPattern","COPY",BODY,{"derivedFrom":makeQuery(id+"F1.opExtrude","SWEPT_BODY",BODY,{"disambiguationData":[OSD([sQuery(id+"F0.wireOp",EDGE,"E1.0"),sQuery(id+"F0.wireOp",EDGE,"E1.1"),sQuery(id+"F0.wireOp",EDGE,"E1.2"),sQuery(id+"F0.wireOp",EDGE,"E1.3"),sQuery(id+"F0.wireOp",EDGE,"E1.4"),sQuery(id+"F0.wireOp",EDGE,"E1.5"),sQuery(id+"F0.wireOp",EDGE,"E3.0"),sQuery(id+"F0.wireOp",EDGE,"E3.1"),sQuery(id+"F0.wireOp",EDGE,"E3.2"),sQuery(id+"F0.wireOp",EDGE,"E3.3"),sQuery(id+"F0.wireOp",EDGE,"E3.4"),sQuery(id+"F0.wireOp",EDGE,"E3.5")])]}),"instanceName":"1"}),"instanceName":"1"}),"instanceName":"1"}),"instanceName":"1"}),"instanceName":"1"});
            var Q18;
            Q18=makeQuery(id+"F9.opPattern","COPY",BODY,{"derivedFrom":makeQuery(id+"F7.opPattern","COPY",BODY,{"derivedFrom":makeQuery(id+"F6.opPattern","COPY",BODY,{"derivedFrom":makeQuery(id+"F1.opExtrude","SWEPT_BODY",BODY,{"disambiguationData":[OSD([sQuery(id+"F0.wireOp",EDGE,"E1.0"),sQuery(id+"F0.wireOp",EDGE,"E1.1"),sQuery(id+"F0.wireOp",EDGE,"E1.2"),sQuery(id+"F0.wireOp",EDGE,"E1.3"),sQuery(id+"F0.wireOp",EDGE,"E1.4"),sQuery(id+"F0.wireOp",EDGE,"E1.5"),sQuery(id+"F0.wireOp",EDGE,"E3.0"),sQuery(id+"F0.wireOp",EDGE,"E3.1"),sQuery(id+"F0.wireOp",EDGE,"E3.2"),sQuery(id+"F0.wireOp",EDGE,"E3.3"),sQuery(id+"F0.wireOp",EDGE,"E3.4"),sQuery(id+"F0.wireOp",EDGE,"E3.5")])]}),"instanceName":"1"}),"instanceName":"1"}),"instanceName":"1"});
            var Q19;
            Q19=makeQuery(id+"F9.opPattern","COPY",BODY,{"derivedFrom":makeQuery(id+"F7.opPattern","COPY",BODY,{"derivedFrom":makeQuery(id+"F6.opPattern","COPY",BODY,{"derivedFrom":makeQuery(id+"F3.opPattern","COPY",BODY,{"derivedFrom":makeQuery(id+"F1.opExtrude","SWEPT_BODY",BODY,{"disambiguationData":[OSD([sQuery(id+"F0.wireOp",EDGE,"E1.0"),sQuery(id+"F0.wireOp",EDGE,"E1.1"),sQuery(id+"F0.wireOp",EDGE,"E1.2"),sQuery(id+"F0.wireOp",EDGE,"E1.3"),sQuery(id+"F0.wireOp",EDGE,"E1.4"),sQuery(id+"F0.wireOp",EDGE,"E1.5"),sQuery(id+"F0.wireOp",EDGE,"E3.0"),sQuery(id+"F0.wireOp",EDGE,"E3.1"),sQuery(id+"F0.wireOp",EDGE,"E3.2"),sQuery(id+"F0.wireOp",EDGE,"E3.3"),sQuery(id+"F0.wireOp",EDGE,"E3.4"),sQuery(id+"F0.wireOp",EDGE,"E3.5")])]}),"instanceName":"1"}),"instanceName":"1"}),"instanceName":"1"}),"instanceName":"1"});
            var Q20;
            Q20=makeQuery(id+"F9.opPattern","COPY",BODY,{"derivedFrom":makeQuery(id+"F7.opPattern","COPY",BODY,{"derivedFrom":makeQuery(id+"F6.opPattern","COPY",BODY,{"derivedFrom":makeQuery(id+"F4.opPattern","COPY",BODY,{"derivedFrom":makeQuery(id+"F1.opExtrude","SWEPT_BODY",BODY,{"disambiguationData":[OSD([sQuery(id+"F0.wireOp",EDGE,"E1.0"),sQuery(id+"F0.wireOp",EDGE,"E1.1"),sQuery(id+"F0.wireOp",EDGE,"E1.2"),sQuery(id+"F0.wireOp",EDGE,"E1.3"),sQuery(id+"F0.wireOp",EDGE,"E1.4"),sQuery(id+"F0.wireOp",EDGE,"E1.5"),sQuery(id+"F0.wireOp",EDGE,"E3.0"),sQuery(id+"F0.wireOp",EDGE,"E3.1"),sQuery(id+"F0.wireOp",EDGE,"E3.2"),sQuery(id+"F0.wireOp",EDGE,"E3.3"),sQuery(id+"F0.wireOp",EDGE,"E3.4"),sQuery(id+"F0.wireOp",EDGE,"E3.5")])]}),"instanceName":"1"}),"instanceName":"1"}),"instanceName":"1"}),"instanceName":"1"});
            var Q21;
            Q21=makeQuery(id+"F9.opPattern","COPY",BODY,{"derivedFrom":makeQuery(id+"F7.opPattern","COPY",BODY,{"derivedFrom":makeQuery(id+"F6.opPattern","COPY",BODY,{"derivedFrom":makeQuery(id+"F4.opPattern","COPY",BODY,{"derivedFrom":makeQuery(id+"F3.opPattern","COPY",BODY,{"derivedFrom":makeQuery(id+"F1.opExtrude","SWEPT_BODY",BODY,{"disambiguationData":[OSD([sQuery(id+"F0.wireOp",EDGE,"E1.0"),sQuery(id+"F0.wireOp",EDGE,"E1.1"),sQuery(id+"F0.wireOp",EDGE,"E1.2"),sQuery(id+"F0.wireOp",EDGE,"E1.3"),sQuery(id+"F0.wireOp",EDGE,"E1.4"),sQuery(id+"F0.wireOp",EDGE,"E1.5"),sQuery(id+"F0.wireOp",EDGE,"E3.0"),sQuery(id+"F0.wireOp",EDGE,"E3.1"),sQuery(id+"F0.wireOp",EDGE,"E3.2"),sQuery(id+"F0.wireOp",EDGE,"E3.3"),sQuery(id+"F0.wireOp",EDGE,"E3.4"),sQuery(id+"F0.wireOp",EDGE,"E3.5")])]}),"instanceName":"1"}),"instanceName":"1"}),"instanceName":"1"}),"instanceName":"1"}),"instanceName":"1"});
            var Q22;
            Q22=makeQuery(id+"F9.opPattern","COPY",BODY,{"derivedFrom":makeQuery(id+"F7.opPattern","COPY",BODY,{"derivedFrom":makeQuery(id+"F6.opPattern","COPY",BODY,{"derivedFrom":makeQuery(id+"F5.opPattern","COPY",BODY,{"derivedFrom":makeQuery(id+"F4.opPattern","COPY",BODY,{"derivedFrom":makeQuery(id+"F1.opExtrude","SWEPT_BODY",BODY,{"disambiguationData":[OSD([sQuery(id+"F0.wireOp",EDGE,"E1.0"),sQuery(id+"F0.wireOp",EDGE,"E1.1"),sQuery(id+"F0.wireOp",EDGE,"E1.2"),sQuery(id+"F0.wireOp",EDGE,"E1.3"),sQuery(id+"F0.wireOp",EDGE,"E1.4"),sQuery(id+"F0.wireOp",EDGE,"E1.5"),sQuery(id+"F0.wireOp",EDGE,"E3.0"),sQuery(id+"F0.wireOp",EDGE,"E3.1"),sQuery(id+"F0.wireOp",EDGE,"E3.2"),sQuery(id+"F0.wireOp",EDGE,"E3.3"),sQuery(id+"F0.wireOp",EDGE,"E3.4"),sQuery(id+"F0.wireOp",EDGE,"E3.5")])]}),"instanceName":"1"}),"instanceName":"1"}),"instanceName":"1"}),"instanceName":"1"}),"instanceName":"1"});
            var Q23;
            Q23=makeQuery(id+"F9.opPattern","COPY",BODY,{"derivedFrom":makeQuery(id+"F7.opPattern","COPY",BODY,{"derivedFrom":makeQuery(id+"F6.opPattern","COPY",BODY,{"derivedFrom":makeQuery(id+"F5.opPattern","COPY",BODY,{"derivedFrom":makeQuery(id+"F4.opPattern","COPY",BODY,{"derivedFrom":makeQuery(id+"F3.opPattern","COPY",BODY,{"derivedFrom":makeQuery(id+"F1.opExtrude","SWEPT_BODY",BODY,{"disambiguationData":[OSD([sQuery(id+"F0.wireOp",EDGE,"E1.0"),sQuery(id+"F0.wireOp",EDGE,"E1.1"),sQuery(id+"F0.wireOp",EDGE,"E1.2"),sQuery(id+"F0.wireOp",EDGE,"E1.3"),sQuery(id+"F0.wireOp",EDGE,"E1.4"),sQuery(id+"F0.wireOp",EDGE,"E1.5"),sQuery(id+"F0.wireOp",EDGE,"E3.0"),sQuery(id+"F0.wireOp",EDGE,"E3.1"),sQuery(id+"F0.wireOp",EDGE,"E3.2"),sQuery(id+"F0.wireOp",EDGE,"E3.3"),sQuery(id+"F0.wireOp",EDGE,"E3.4"),sQuery(id+"F0.wireOp",EDGE,"E3.5")])]}),"instanceName":"1"}),"instanceName":"1"}),"instanceName":"1"}),"instanceName":"1"}),"instanceName":"1"}),"instanceName":"1"});
            var Q24;
            Q24=makeQuery(id+"F9.opPattern","COPY",BODY,{"derivedFrom":makeQuery(id+"F6.opPattern","COPY",BODY,{"derivedFrom":makeQuery(id+"F1.opExtrude","SWEPT_BODY",BODY,{"disambiguationData":[OSD([sQuery(id+"F0.wireOp",EDGE,"E1.0"),sQuery(id+"F0.wireOp",EDGE,"E1.1"),sQuery(id+"F0.wireOp",EDGE,"E1.2"),sQuery(id+"F0.wireOp",EDGE,"E1.3"),sQuery(id+"F0.wireOp",EDGE,"E1.4"),sQuery(id+"F0.wireOp",EDGE,"E1.5"),sQuery(id+"F0.wireOp",EDGE,"E3.0"),sQuery(id+"F0.wireOp",EDGE,"E3.1"),sQuery(id+"F0.wireOp",EDGE,"E3.2"),sQuery(id+"F0.wireOp",EDGE,"E3.3"),sQuery(id+"F0.wireOp",EDGE,"E3.4"),sQuery(id+"F0.wireOp",EDGE,"E3.5")])]}),"instanceName":"1"}),"instanceName":"1"});
            var Q25;
            Q25=makeQuery(id+"F9.opPattern","COPY",BODY,{"derivedFrom":makeQuery(id+"F6.opPattern","COPY",BODY,{"derivedFrom":makeQuery(id+"F3.opPattern","COPY",BODY,{"derivedFrom":makeQuery(id+"F1.opExtrude","SWEPT_BODY",BODY,{"disambiguationData":[OSD([sQuery(id+"F0.wireOp",EDGE,"E1.0"),sQuery(id+"F0.wireOp",EDGE,"E1.1"),sQuery(id+"F0.wireOp",EDGE,"E1.2"),sQuery(id+"F0.wireOp",EDGE,"E1.3"),sQuery(id+"F0.wireOp",EDGE,"E1.4"),sQuery(id+"F0.wireOp",EDGE,"E1.5"),sQuery(id+"F0.wireOp",EDGE,"E3.0"),sQuery(id+"F0.wireOp",EDGE,"E3.1"),sQuery(id+"F0.wireOp",EDGE,"E3.2"),sQuery(id+"F0.wireOp",EDGE,"E3.3"),sQuery(id+"F0.wireOp",EDGE,"E3.4"),sQuery(id+"F0.wireOp",EDGE,"E3.5")])]}),"instanceName":"1"}),"instanceName":"1"}),"instanceName":"1"});
            var Q26;
            Q26=makeQuery(id+"F9.opPattern","COPY",BODY,{"derivedFrom":makeQuery(id+"F6.opPattern","COPY",BODY,{"derivedFrom":makeQuery(id+"F4.opPattern","COPY",BODY,{"derivedFrom":makeQuery(id+"F1.opExtrude","SWEPT_BODY",BODY,{"disambiguationData":[OSD([sQuery(id+"F0.wireOp",EDGE,"E1.0"),sQuery(id+"F0.wireOp",EDGE,"E1.1"),sQuery(id+"F0.wireOp",EDGE,"E1.2"),sQuery(id+"F0.wireOp",EDGE,"E1.3"),sQuery(id+"F0.wireOp",EDGE,"E1.4"),sQuery(id+"F0.wireOp",EDGE,"E1.5"),sQuery(id+"F0.wireOp",EDGE,"E3.0"),sQuery(id+"F0.wireOp",EDGE,"E3.1"),sQuery(id+"F0.wireOp",EDGE,"E3.2"),sQuery(id+"F0.wireOp",EDGE,"E3.3"),sQuery(id+"F0.wireOp",EDGE,"E3.4"),sQuery(id+"F0.wireOp",EDGE,"E3.5")])]}),"instanceName":"1"}),"instanceName":"1"}),"instanceName":"1"});
            var Q27;
            Q27=makeQuery(id+"F9.opPattern","COPY",BODY,{"derivedFrom":makeQuery(id+"F6.opPattern","COPY",BODY,{"derivedFrom":makeQuery(id+"F4.opPattern","COPY",BODY,{"derivedFrom":makeQuery(id+"F3.opPattern","COPY",BODY,{"derivedFrom":makeQuery(id+"F1.opExtrude","SWEPT_BODY",BODY,{"disambiguationData":[OSD([sQuery(id+"F0.wireOp",EDGE,"E1.0"),sQuery(id+"F0.wireOp",EDGE,"E1.1"),sQuery(id+"F0.wireOp",EDGE,"E1.2"),sQuery(id+"F0.wireOp",EDGE,"E1.3"),sQuery(id+"F0.wireOp",EDGE,"E1.4"),sQuery(id+"F0.wireOp",EDGE,"E1.5"),sQuery(id+"F0.wireOp",EDGE,"E3.0"),sQuery(id+"F0.wireOp",EDGE,"E3.1"),sQuery(id+"F0.wireOp",EDGE,"E3.2"),sQuery(id+"F0.wireOp",EDGE,"E3.3"),sQuery(id+"F0.wireOp",EDGE,"E3.4"),sQuery(id+"F0.wireOp",EDGE,"E3.5")])]}),"instanceName":"1"}),"instanceName":"1"}),"instanceName":"1"}),"instanceName":"1"});
            var Q28;
            Q28=makeQuery(id+"F9.opPattern","COPY",BODY,{"derivedFrom":makeQuery(id+"F6.opPattern","COPY",BODY,{"derivedFrom":makeQuery(id+"F5.opPattern","COPY",BODY,{"derivedFrom":makeQuery(id+"F4.opPattern","COPY",BODY,{"derivedFrom":makeQuery(id+"F1.opExtrude","SWEPT_BODY",BODY,{"disambiguationData":[OSD([sQuery(id+"F0.wireOp",EDGE,"E1.0"),sQuery(id+"F0.wireOp",EDGE,"E1.1"),sQuery(id+"F0.wireOp",EDGE,"E1.2"),sQuery(id+"F0.wireOp",EDGE,"E1.3"),sQuery(id+"F0.wireOp",EDGE,"E1.4"),sQuery(id+"F0.wireOp",EDGE,"E1.5"),sQuery(id+"F0.wireOp",EDGE,"E3.0"),sQuery(id+"F0.wireOp",EDGE,"E3.1"),sQuery(id+"F0.wireOp",EDGE,"E3.2"),sQuery(id+"F0.wireOp",EDGE,"E3.3"),sQuery(id+"F0.wireOp",EDGE,"E3.4"),sQuery(id+"F0.wireOp",EDGE,"E3.5")])]}),"instanceName":"1"}),"instanceName":"1"}),"instanceName":"1"}),"instanceName":"1"});
            var Q29;
            Q29=makeQuery(id+"F9.opPattern","COPY",BODY,{"derivedFrom":makeQuery(id+"F6.opPattern","COPY",BODY,{"derivedFrom":makeQuery(id+"F5.opPattern","COPY",BODY,{"derivedFrom":makeQuery(id+"F4.opPattern","COPY",BODY,{"derivedFrom":makeQuery(id+"F3.opPattern","COPY",BODY,{"derivedFrom":makeQuery(id+"F1.opExtrude","SWEPT_BODY",BODY,{"disambiguationData":[OSD([sQuery(id+"F0.wireOp",EDGE,"E1.0"),sQuery(id+"F0.wireOp",EDGE,"E1.1"),sQuery(id+"F0.wireOp",EDGE,"E1.2"),sQuery(id+"F0.wireOp",EDGE,"E1.3"),sQuery(id+"F0.wireOp",EDGE,"E1.4"),sQuery(id+"F0.wireOp",EDGE,"E1.5"),sQuery(id+"F0.wireOp",EDGE,"E3.0"),sQuery(id+"F0.wireOp",EDGE,"E3.1"),sQuery(id+"F0.wireOp",EDGE,"E3.2"),sQuery(id+"F0.wireOp",EDGE,"E3.3"),sQuery(id+"F0.wireOp",EDGE,"E3.4"),sQuery(id+"F0.wireOp",EDGE,"E3.5")])]}),"instanceName":"1"}),"instanceName":"1"}),"instanceName":"1"}),"instanceName":"1"}),"instanceName":"1"});
            var Q30;
            Q30=makeQuery(id+"F6.opPattern","COPY",BODY,{"derivedFrom":makeQuery(id+"F1.opExtrude","SWEPT_BODY",BODY,{"disambiguationData":[OSD([sQuery(id+"F0.wireOp",EDGE,"E1.0"),sQuery(id+"F0.wireOp",EDGE,"E1.1"),sQuery(id+"F0.wireOp",EDGE,"E1.2"),sQuery(id+"F0.wireOp",EDGE,"E1.3"),sQuery(id+"F0.wireOp",EDGE,"E1.4"),sQuery(id+"F0.wireOp",EDGE,"E1.5"),sQuery(id+"F0.wireOp",EDGE,"E3.0"),sQuery(id+"F0.wireOp",EDGE,"E3.1"),sQuery(id+"F0.wireOp",EDGE,"E3.2"),sQuery(id+"F0.wireOp",EDGE,"E3.3"),sQuery(id+"F0.wireOp",EDGE,"E3.4"),sQuery(id+"F0.wireOp",EDGE,"E3.5")])]}),"instanceName":"1"});
            var Q31;
            Q31=makeQuery(id+"F6.opPattern","COPY",BODY,{"derivedFrom":makeQuery(id+"F3.opPattern","COPY",BODY,{"derivedFrom":makeQuery(id+"F1.opExtrude","SWEPT_BODY",BODY,{"disambiguationData":[OSD([sQuery(id+"F0.wireOp",EDGE,"E1.0"),sQuery(id+"F0.wireOp",EDGE,"E1.1"),sQuery(id+"F0.wireOp",EDGE,"E1.2"),sQuery(id+"F0.wireOp",EDGE,"E1.3"),sQuery(id+"F0.wireOp",EDGE,"E1.4"),sQuery(id+"F0.wireOp",EDGE,"E1.5"),sQuery(id+"F0.wireOp",EDGE,"E3.0"),sQuery(id+"F0.wireOp",EDGE,"E3.1"),sQuery(id+"F0.wireOp",EDGE,"E3.2"),sQuery(id+"F0.wireOp",EDGE,"E3.3"),sQuery(id+"F0.wireOp",EDGE,"E3.4"),sQuery(id+"F0.wireOp",EDGE,"E3.5")])]}),"instanceName":"1"}),"instanceName":"1"});
            var Q32;
            Q32=makeQuery(id+"F6.opPattern","COPY",BODY,{"derivedFrom":makeQuery(id+"F4.opPattern","COPY",BODY,{"derivedFrom":makeQuery(id+"F1.opExtrude","SWEPT_BODY",BODY,{"disambiguationData":[OSD([sQuery(id+"F0.wireOp",EDGE,"E1.0"),sQuery(id+"F0.wireOp",EDGE,"E1.1"),sQuery(id+"F0.wireOp",EDGE,"E1.2"),sQuery(id+"F0.wireOp",EDGE,"E1.3"),sQuery(id+"F0.wireOp",EDGE,"E1.4"),sQuery(id+"F0.wireOp",EDGE,"E1.5"),sQuery(id+"F0.wireOp",EDGE,"E3.0"),sQuery(id+"F0.wireOp",EDGE,"E3.1"),sQuery(id+"F0.wireOp",EDGE,"E3.2"),sQuery(id+"F0.wireOp",EDGE,"E3.3"),sQuery(id+"F0.wireOp",EDGE,"E3.4"),sQuery(id+"F0.wireOp",EDGE,"E3.5")])]}),"instanceName":"1"}),"instanceName":"1"});
            var Q33;
            Q33=makeQuery(id+"F1.opExtrude","SWEPT_BODY",BODY,{"disambiguationData":[OSD([sQuery(id+"F0.wireOp",EDGE,"E1.0"),sQuery(id+"F0.wireOp",EDGE,"E1.1"),sQuery(id+"F0.wireOp",EDGE,"E1.2"),sQuery(id+"F0.wireOp",EDGE,"E1.3"),sQuery(id+"F0.wireOp",EDGE,"E1.4"),sQuery(id+"F0.wireOp",EDGE,"E1.5"),sQuery(id+"F0.wireOp",EDGE,"E3.0"),sQuery(id+"F0.wireOp",EDGE,"E3.1"),sQuery(id+"F0.wireOp",EDGE,"E3.2"),sQuery(id+"F0.wireOp",EDGE,"E3.3"),sQuery(id+"F0.wireOp",EDGE,"E3.4"),sQuery(id+"F0.wireOp",EDGE,"E3.5")])]});
            var Q34;
            Q34=makeQuery(id+"F6.opPattern","COPY",BODY,{"derivedFrom":makeQuery(id+"F4.opPattern","COPY",BODY,{"derivedFrom":makeQuery(id+"F3.opPattern","COPY",BODY,{"derivedFrom":makeQuery(id+"F1.opExtrude","SWEPT_BODY",BODY,{"disambiguationData":[OSD([sQuery(id+"F0.wireOp",EDGE,"E1.0"),sQuery(id+"F0.wireOp",EDGE,"E1.1"),sQuery(id+"F0.wireOp",EDGE,"E1.2"),sQuery(id+"F0.wireOp",EDGE,"E1.3"),sQuery(id+"F0.wireOp",EDGE,"E1.4"),sQuery(id+"F0.wireOp",EDGE,"E1.5"),sQuery(id+"F0.wireOp",EDGE,"E3.0"),sQuery(id+"F0.wireOp",EDGE,"E3.1"),sQuery(id+"F0.wireOp",EDGE,"E3.2"),sQuery(id+"F0.wireOp",EDGE,"E3.3"),sQuery(id+"F0.wireOp",EDGE,"E3.4"),sQuery(id+"F0.wireOp",EDGE,"E3.5")])]}),"instanceName":"1"}),"instanceName":"1"}),"instanceName":"1"});
            var Q35;
            Q35=makeQuery(id+"F6.opPattern","COPY",BODY,{"derivedFrom":makeQuery(id+"F5.opPattern","COPY",BODY,{"derivedFrom":makeQuery(id+"F4.opPattern","COPY",BODY,{"derivedFrom":makeQuery(id+"F1.opExtrude","SWEPT_BODY",BODY,{"disambiguationData":[OSD([sQuery(id+"F0.wireOp",EDGE,"E1.0"),sQuery(id+"F0.wireOp",EDGE,"E1.1"),sQuery(id+"F0.wireOp",EDGE,"E1.2"),sQuery(id+"F0.wireOp",EDGE,"E1.3"),sQuery(id+"F0.wireOp",EDGE,"E1.4"),sQuery(id+"F0.wireOp",EDGE,"E1.5"),sQuery(id+"F0.wireOp",EDGE,"E3.0"),sQuery(id+"F0.wireOp",EDGE,"E3.1"),sQuery(id+"F0.wireOp",EDGE,"E3.2"),sQuery(id+"F0.wireOp",EDGE,"E3.3"),sQuery(id+"F0.wireOp",EDGE,"E3.4"),sQuery(id+"F0.wireOp",EDGE,"E3.5")])]}),"instanceName":"1"}),"instanceName":"1"}),"instanceName":"1"});
            var Q36;
            Q36=makeQuery(id+"F6.opPattern","COPY",BODY,{"derivedFrom":makeQuery(id+"F5.opPattern","COPY",BODY,{"derivedFrom":makeQuery(id+"F4.opPattern","COPY",BODY,{"derivedFrom":makeQuery(id+"F3.opPattern","COPY",BODY,{"derivedFrom":makeQuery(id+"F1.opExtrude","SWEPT_BODY",BODY,{"disambiguationData":[OSD([sQuery(id+"F0.wireOp",EDGE,"E1.0"),sQuery(id+"F0.wireOp",EDGE,"E1.1"),sQuery(id+"F0.wireOp",EDGE,"E1.2"),sQuery(id+"F0.wireOp",EDGE,"E1.3"),sQuery(id+"F0.wireOp",EDGE,"E1.4"),sQuery(id+"F0.wireOp",EDGE,"E1.5"),sQuery(id+"F0.wireOp",EDGE,"E3.0"),sQuery(id+"F0.wireOp",EDGE,"E3.1"),sQuery(id+"F0.wireOp",EDGE,"E3.2"),sQuery(id+"F0.wireOp",EDGE,"E3.3"),sQuery(id+"F0.wireOp",EDGE,"E3.4"),sQuery(id+"F0.wireOp",EDGE,"E3.5")])]}),"instanceName":"1"}),"instanceName":"1"}),"instanceName":"1"}),"instanceName":"1"});
            var Q37;
            Q37=makeQuery(id+"F4.opPattern","COPY",BODY,{"derivedFrom":makeQuery(id+"F3.opPattern","COPY",BODY,{"derivedFrom":makeQuery(id+"F1.opExtrude","SWEPT_BODY",BODY,{"disambiguationData":[OSD([sQuery(id+"F0.wireOp",EDGE,"E1.0"),sQuery(id+"F0.wireOp",EDGE,"E1.1"),sQuery(id+"F0.wireOp",EDGE,"E1.2"),sQuery(id+"F0.wireOp",EDGE,"E1.3"),sQuery(id+"F0.wireOp",EDGE,"E1.4"),sQuery(id+"F0.wireOp",EDGE,"E1.5"),sQuery(id+"F0.wireOp",EDGE,"E3.0"),sQuery(id+"F0.wireOp",EDGE,"E3.1"),sQuery(id+"F0.wireOp",EDGE,"E3.2"),sQuery(id+"F0.wireOp",EDGE,"E3.3"),sQuery(id+"F0.wireOp",EDGE,"E3.4"),sQuery(id+"F0.wireOp",EDGE,"E3.5")])]}),"instanceName":"1"}),"instanceName":"1"});
            var Q38;
            Q38=makeQuery(id+"F5.opPattern","COPY",BODY,{"derivedFrom":makeQuery(id+"F4.opPattern","COPY",BODY,{"derivedFrom":makeQuery(id+"F3.opPattern","COPY",BODY,{"derivedFrom":makeQuery(id+"F1.opExtrude","SWEPT_BODY",BODY,{"disambiguationData":[OSD([sQuery(id+"F0.wireOp",EDGE,"E1.0"),sQuery(id+"F0.wireOp",EDGE,"E1.1"),sQuery(id+"F0.wireOp",EDGE,"E1.2"),sQuery(id+"F0.wireOp",EDGE,"E1.3"),sQuery(id+"F0.wireOp",EDGE,"E1.4"),sQuery(id+"F0.wireOp",EDGE,"E1.5"),sQuery(id+"F0.wireOp",EDGE,"E3.0"),sQuery(id+"F0.wireOp",EDGE,"E3.1"),sQuery(id+"F0.wireOp",EDGE,"E3.2"),sQuery(id+"F0.wireOp",EDGE,"E3.3"),sQuery(id+"F0.wireOp",EDGE,"E3.4"),sQuery(id+"F0.wireOp",EDGE,"E3.5")])]}),"instanceName":"1"}),"instanceName":"1"}),"instanceName":"1"});
            var Q39;
            Q39=makeQuery(id+"F4.opPattern","COPY",BODY,{"derivedFrom":makeQuery(id+"F1.opExtrude","SWEPT_BODY",BODY,{"disambiguationData":[OSD([sQuery(id+"F0.wireOp",EDGE,"E1.0"),sQuery(id+"F0.wireOp",EDGE,"E1.1"),sQuery(id+"F0.wireOp",EDGE,"E1.2"),sQuery(id+"F0.wireOp",EDGE,"E1.3"),sQuery(id+"F0.wireOp",EDGE,"E1.4"),sQuery(id+"F0.wireOp",EDGE,"E1.5"),sQuery(id+"F0.wireOp",EDGE,"E3.0"),sQuery(id+"F0.wireOp",EDGE,"E3.1"),sQuery(id+"F0.wireOp",EDGE,"E3.2"),sQuery(id+"F0.wireOp",EDGE,"E3.3"),sQuery(id+"F0.wireOp",EDGE,"E3.4"),sQuery(id+"F0.wireOp",EDGE,"E3.5")])]}),"instanceName":"1"});
            var Q40;
            Q40=makeQuery(id+"F5.opPattern","COPY",BODY,{"derivedFrom":makeQuery(id+"F4.opPattern","COPY",BODY,{"derivedFrom":makeQuery(id+"F1.opExtrude","SWEPT_BODY",BODY,{"disambiguationData":[OSD([sQuery(id+"F0.wireOp",EDGE,"E1.0"),sQuery(id+"F0.wireOp",EDGE,"E1.1"),sQuery(id+"F0.wireOp",EDGE,"E1.2"),sQuery(id+"F0.wireOp",EDGE,"E1.3"),sQuery(id+"F0.wireOp",EDGE,"E1.4"),sQuery(id+"F0.wireOp",EDGE,"E1.5"),sQuery(id+"F0.wireOp",EDGE,"E3.0"),sQuery(id+"F0.wireOp",EDGE,"E3.1"),sQuery(id+"F0.wireOp",EDGE,"E3.2"),sQuery(id+"F0.wireOp",EDGE,"E3.3"),sQuery(id+"F0.wireOp",EDGE,"E3.4"),sQuery(id+"F0.wireOp",EDGE,"E3.5")])]}),"instanceName":"1"}),"instanceName":"1"});
            var Q41;
            Q41=makeQuery(id+"F3.opPattern","COPY",BODY,{"derivedFrom":makeQuery(id+"F1.opExtrude","SWEPT_BODY",BODY,{"disambiguationData":[OSD([sQuery(id+"F0.wireOp",EDGE,"E1.0"),sQuery(id+"F0.wireOp",EDGE,"E1.1"),sQuery(id+"F0.wireOp",EDGE,"E1.2"),sQuery(id+"F0.wireOp",EDGE,"E1.3"),sQuery(id+"F0.wireOp",EDGE,"E1.4"),sQuery(id+"F0.wireOp",EDGE,"E1.5"),sQuery(id+"F0.wireOp",EDGE,"E3.0"),sQuery(id+"F0.wireOp",EDGE,"E3.1"),sQuery(id+"F0.wireOp",EDGE,"E3.2"),sQuery(id+"F0.wireOp",EDGE,"E3.3"),sQuery(id+"F0.wireOp",EDGE,"E3.4"),sQuery(id+"F0.wireOp",EDGE,"E3.5")])]}),"instanceName":"1"});
            var Q42;
            Q42=makeQuery(id+"F9.opPattern","COPY",BODY,{"derivedFrom":makeQuery(id+"F1.opExtrude","SWEPT_BODY",BODY,{"disambiguationData":[OSD([sQuery(id+"F0.wireOp",EDGE,"E1.0"),sQuery(id+"F0.wireOp",EDGE,"E1.1"),sQuery(id+"F0.wireOp",EDGE,"E1.2"),sQuery(id+"F0.wireOp",EDGE,"E1.3"),sQuery(id+"F0.wireOp",EDGE,"E1.4"),sQuery(id+"F0.wireOp",EDGE,"E1.5"),sQuery(id+"F0.wireOp",EDGE,"E3.0"),sQuery(id+"F0.wireOp",EDGE,"E3.1"),sQuery(id+"F0.wireOp",EDGE,"E3.2"),sQuery(id+"F0.wireOp",EDGE,"E3.3"),sQuery(id+"F0.wireOp",EDGE,"E3.4"),sQuery(id+"F0.wireOp",EDGE,"E3.5")])]}),"instanceName":"1"});
            var Q43;
            Q43=makeQuery(id+"F9.opPattern","COPY",BODY,{"derivedFrom":makeQuery(id+"F3.opPattern","COPY",BODY,{"derivedFrom":makeQuery(id+"F1.opExtrude","SWEPT_BODY",BODY,{"disambiguationData":[OSD([sQuery(id+"F0.wireOp",EDGE,"E1.0"),sQuery(id+"F0.wireOp",EDGE,"E1.1"),sQuery(id+"F0.wireOp",EDGE,"E1.2"),sQuery(id+"F0.wireOp",EDGE,"E1.3"),sQuery(id+"F0.wireOp",EDGE,"E1.4"),sQuery(id+"F0.wireOp",EDGE,"E1.5"),sQuery(id+"F0.wireOp",EDGE,"E3.0"),sQuery(id+"F0.wireOp",EDGE,"E3.1"),sQuery(id+"F0.wireOp",EDGE,"E3.2"),sQuery(id+"F0.wireOp",EDGE,"E3.3"),sQuery(id+"F0.wireOp",EDGE,"E3.4"),sQuery(id+"F0.wireOp",EDGE,"E3.5")])]}),"instanceName":"1"}),"instanceName":"1"});
            var Q44;
            Q44=makeQuery(id+"F9.opPattern","COPY",BODY,{"derivedFrom":makeQuery(id+"F4.opPattern","COPY",BODY,{"derivedFrom":makeQuery(id+"F1.opExtrude","SWEPT_BODY",BODY,{"disambiguationData":[OSD([sQuery(id+"F0.wireOp",EDGE,"E1.0"),sQuery(id+"F0.wireOp",EDGE,"E1.1"),sQuery(id+"F0.wireOp",EDGE,"E1.2"),sQuery(id+"F0.wireOp",EDGE,"E1.3"),sQuery(id+"F0.wireOp",EDGE,"E1.4"),sQuery(id+"F0.wireOp",EDGE,"E1.5"),sQuery(id+"F0.wireOp",EDGE,"E3.0"),sQuery(id+"F0.wireOp",EDGE,"E3.1"),sQuery(id+"F0.wireOp",EDGE,"E3.2"),sQuery(id+"F0.wireOp",EDGE,"E3.3"),sQuery(id+"F0.wireOp",EDGE,"E3.4"),sQuery(id+"F0.wireOp",EDGE,"E3.5")])]}),"instanceName":"1"}),"instanceName":"1"});
            var Q45;
            Q45=makeQuery(id+"F9.opPattern","COPY",BODY,{"derivedFrom":makeQuery(id+"F4.opPattern","COPY",BODY,{"derivedFrom":makeQuery(id+"F3.opPattern","COPY",BODY,{"derivedFrom":makeQuery(id+"F1.opExtrude","SWEPT_BODY",BODY,{"disambiguationData":[OSD([sQuery(id+"F0.wireOp",EDGE,"E1.0"),sQuery(id+"F0.wireOp",EDGE,"E1.1"),sQuery(id+"F0.wireOp",EDGE,"E1.2"),sQuery(id+"F0.wireOp",EDGE,"E1.3"),sQuery(id+"F0.wireOp",EDGE,"E1.4"),sQuery(id+"F0.wireOp",EDGE,"E1.5"),sQuery(id+"F0.wireOp",EDGE,"E3.0"),sQuery(id+"F0.wireOp",EDGE,"E3.1"),sQuery(id+"F0.wireOp",EDGE,"E3.2"),sQuery(id+"F0.wireOp",EDGE,"E3.3"),sQuery(id+"F0.wireOp",EDGE,"E3.4"),sQuery(id+"F0.wireOp",EDGE,"E3.5")])]}),"instanceName":"1"}),"instanceName":"1"}),"instanceName":"1"});
            var Q46;
            Q46=makeQuery(id+"F9.opPattern","COPY",BODY,{"derivedFrom":makeQuery(id+"F5.opPattern","COPY",BODY,{"derivedFrom":makeQuery(id+"F4.opPattern","COPY",BODY,{"derivedFrom":makeQuery(id+"F1.opExtrude","SWEPT_BODY",BODY,{"disambiguationData":[OSD([sQuery(id+"F0.wireOp",EDGE,"E1.0"),sQuery(id+"F0.wireOp",EDGE,"E1.1"),sQuery(id+"F0.wireOp",EDGE,"E1.2"),sQuery(id+"F0.wireOp",EDGE,"E1.3"),sQuery(id+"F0.wireOp",EDGE,"E1.4"),sQuery(id+"F0.wireOp",EDGE,"E1.5"),sQuery(id+"F0.wireOp",EDGE,"E3.0"),sQuery(id+"F0.wireOp",EDGE,"E3.1"),sQuery(id+"F0.wireOp",EDGE,"E3.2"),sQuery(id+"F0.wireOp",EDGE,"E3.3"),sQuery(id+"F0.wireOp",EDGE,"E3.4"),sQuery(id+"F0.wireOp",EDGE,"E3.5")])]}),"instanceName":"1"}),"instanceName":"1"}),"instanceName":"1"});
            var Q47;
            Q47=makeQuery(id+"F9.opPattern","COPY",BODY,{"derivedFrom":makeQuery(id+"F5.opPattern","COPY",BODY,{"derivedFrom":makeQuery(id+"F4.opPattern","COPY",BODY,{"derivedFrom":makeQuery(id+"F3.opPattern","COPY",BODY,{"derivedFrom":makeQuery(id+"F1.opExtrude","SWEPT_BODY",BODY,{"disambiguationData":[OSD([sQuery(id+"F0.wireOp",EDGE,"E1.0"),sQuery(id+"F0.wireOp",EDGE,"E1.1"),sQuery(id+"F0.wireOp",EDGE,"E1.2"),sQuery(id+"F0.wireOp",EDGE,"E1.3"),sQuery(id+"F0.wireOp",EDGE,"E1.4"),sQuery(id+"F0.wireOp",EDGE,"E1.5"),sQuery(id+"F0.wireOp",EDGE,"E3.0"),sQuery(id+"F0.wireOp",EDGE,"E3.1"),sQuery(id+"F0.wireOp",EDGE,"E3.2"),sQuery(id+"F0.wireOp",EDGE,"E3.3"),sQuery(id+"F0.wireOp",EDGE,"E3.4"),sQuery(id+"F0.wireOp",EDGE,"E3.5")])]}),"instanceName":"1"}),"instanceName":"1"}),"instanceName":"1"}),"instanceName":"1"});
            transform(context, id + "F12", {"entities" : qUnion([Q0, Q1, Q2, Q3, Q4, Q5, Q6, Q7, Q8, Q9, Q10, Q11, Q12, Q13, Q14, Q15, Q16, Q17, Q18, Q19, Q20, Q21, Q22, Q23, Q24, Q25, Q26, Q27, Q28, Q29, Q30, Q31, Q32, Q33, Q34, Q35, Q36, Q37, Q38, Q39, Q40, Q41, Q42, Q43, Q44, Q45, Q46, Q47]), "transformType" : TransformType.TRANSLATION_3D, "dx" : 0 * mm, "dy" : 14.6 * mm, "dz" : 0 * mm, "makeCopy" : true});
        }
        {
            var Q0;
            Q0=makeQuery(id+"F8.opPattern","COPY",BODY,{"derivedFrom":makeQuery(id+"F7.opPattern","COPY",BODY,{"derivedFrom":makeQuery(id+"F6.opPattern","COPY",BODY,{"derivedFrom":makeQuery(id+"F5.opPattern","COPY",BODY,{"derivedFrom":makeQuery(id+"F4.opPattern","COPY",BODY,{"derivedFrom":makeQuery(id+"F1.opExtrude","SWEPT_BODY",BODY,{"disambiguationData":[OSD([sQuery(id+"F0.wireOp",EDGE,"E1.0"),sQuery(id+"F0.wireOp",EDGE,"E1.1"),sQuery(id+"F0.wireOp",EDGE,"E1.2"),sQuery(id+"F0.wireOp",EDGE,"E1.3"),sQuery(id+"F0.wireOp",EDGE,"E1.4"),sQuery(id+"F0.wireOp",EDGE,"E1.5"),sQuery(id+"F0.wireOp",EDGE,"E3.0"),sQuery(id+"F0.wireOp",EDGE,"E3.1"),sQuery(id+"F0.wireOp",EDGE,"E3.2"),sQuery(id+"F0.wireOp",EDGE,"E3.3"),sQuery(id+"F0.wireOp",EDGE,"E3.4"),sQuery(id+"F0.wireOp",EDGE,"E3.5")])]}),"instanceName":"1"}),"instanceName":"1"}),"instanceName":"1"}),"instanceName":"1"}),"instanceName":"1"});
            transform(context, id + "F13", {"entities" : qUnion([Q0]), "transformType" : TransformType.TRANSLATION_3D, "dx" : 4.23 * mm, "dy" : 0 * mm, "dz" : 0 * mm, "makeCopy" : true});
        }
        {
            var Q0;
            Q0=qCreatedBy(makeId("Top.planeOp"),FACE);
            var sketch = newSketch(context, id + "F14", { "sketchPlane" : qUnion([Q0])});
            skCircle(sketch, "E13.0", {"center": v(0, 0) * mm, "radius": 23.75 * mm});
            skCircle(sketch, "E14", {"center": v(0, 0) * mm, "radius": 45.82 * mm});
            skSolve(sketch);
        }
        {
            var Q0;
            Q0=makeQuery(id+"F14.imprint","IMPRINT",FACE,{"disambiguationData":[TD([[makeQuery(id+"F14.imprint","IMPRINT",EDGE,{"derivedFrom":sQuery(id+"F14.wireOp",EDGE,"E13.0")}),-1.0]])]});
            extrude(context, id + "F15", {"entities" : qUnion([Q0]), "depth" : 130 * mm});
        }
        {
            var Q0;
            Q0=makeQuery(id+"F15.opExtrude","SWEPT_BODY",BODY,{"disambiguationData":[OSD([sQuery(id+"F14.wireOp",EDGE,"E13.0"),sQuery(id+"F14.wireOp",EDGE,"E14")])]});
            var Q1;
            Q1=makeQuery(id+"F12.opPattern","COPY",BODY,{"derivedFrom":makeQuery(id+"F7.opPattern","COPY",BODY,{"derivedFrom":makeQuery(id+"F6.opPattern","COPY",BODY,{"derivedFrom":makeQuery(id+"F5.opPattern","COPY",BODY,{"derivedFrom":makeQuery(id+"F4.opPattern","COPY",BODY,{"derivedFrom":makeQuery(id+"F1.opExtrude","SWEPT_BODY",BODY,{"disambiguationData":[OSD([sQuery(id+"F0.wireOp",EDGE,"E1.0"),sQuery(id+"F0.wireOp",EDGE,"E1.1"),sQuery(id+"F0.wireOp",EDGE,"E1.2"),sQuery(id+"F0.wireOp",EDGE,"E1.3"),sQuery(id+"F0.wireOp",EDGE,"E1.4"),sQuery(id+"F0.wireOp",EDGE,"E1.5"),sQuery(id+"F0.wireOp",EDGE,"E3.0"),sQuery(id+"F0.wireOp",EDGE,"E3.1"),sQuery(id+"F0.wireOp",EDGE,"E3.2"),sQuery(id+"F0.wireOp",EDGE,"E3.3"),sQuery(id+"F0.wireOp",EDGE,"E3.4"),sQuery(id+"F0.wireOp",EDGE,"E3.5")])]}),"instanceName":"1"}),"instanceName":"1"}),"instanceName":"1"}),"instanceName":"1"}),"instanceName":"1"});
            var Q2;
            Q2=makeQuery(id+"F12.opPattern","COPY",BODY,{"derivedFrom":makeQuery(id+"F7.opPattern","COPY",BODY,{"derivedFrom":makeQuery(id+"F5.opPattern","COPY",BODY,{"derivedFrom":makeQuery(id+"F4.opPattern","COPY",BODY,{"derivedFrom":makeQuery(id+"F1.opExtrude","SWEPT_BODY",BODY,{"disambiguationData":[OSD([sQuery(id+"F0.wireOp",EDGE,"E1.0"),sQuery(id+"F0.wireOp",EDGE,"E1.1"),sQuery(id+"F0.wireOp",EDGE,"E1.2"),sQuery(id+"F0.wireOp",EDGE,"E1.3"),sQuery(id+"F0.wireOp",EDGE,"E1.4"),sQuery(id+"F0.wireOp",EDGE,"E1.5"),sQuery(id+"F0.wireOp",EDGE,"E3.0"),sQuery(id+"F0.wireOp",EDGE,"E3.1"),sQuery(id+"F0.wireOp",EDGE,"E3.2"),sQuery(id+"F0.wireOp",EDGE,"E3.3"),sQuery(id+"F0.wireOp",EDGE,"E3.4"),sQuery(id+"F0.wireOp",EDGE,"E3.5")])]}),"instanceName":"1"}),"instanceName":"1"}),"instanceName":"1"}),"instanceName":"1"});
            var Q3;
            Q3=makeQuery(id+"F1.opExtrude","SWEPT_BODY",BODY,{"disambiguationData":[OSD([sQuery(id+"F0.wireOp",EDGE,"E0"),sQuery(id+"F0.wireOp",EDGE,"E5")])]});
            var Q4;
            Q4=makeQuery(id+"F12.opPattern","COPY",BODY,{"derivedFrom":makeQuery(id+"F7.opPattern","COPY",BODY,{"derivedFrom":makeQuery(id+"F4.opPattern","COPY",BODY,{"derivedFrom":makeQuery(id+"F3.opPattern","COPY",BODY,{"derivedFrom":makeQuery(id+"F1.opExtrude","SWEPT_BODY",BODY,{"disambiguationData":[OSD([sQuery(id+"F0.wireOp",EDGE,"E1.0"),sQuery(id+"F0.wireOp",EDGE,"E1.1"),sQuery(id+"F0.wireOp",EDGE,"E1.2"),sQuery(id+"F0.wireOp",EDGE,"E1.3"),sQuery(id+"F0.wireOp",EDGE,"E1.4"),sQuery(id+"F0.wireOp",EDGE,"E1.5"),sQuery(id+"F0.wireOp",EDGE,"E3.0"),sQuery(id+"F0.wireOp",EDGE,"E3.1"),sQuery(id+"F0.wireOp",EDGE,"E3.2"),sQuery(id+"F0.wireOp",EDGE,"E3.3"),sQuery(id+"F0.wireOp",EDGE,"E3.4"),sQuery(id+"F0.wireOp",EDGE,"E3.5")])]}),"instanceName":"1"}),"instanceName":"1"}),"instanceName":"1"}),"instanceName":"1"});
            var Q5;
            Q5=makeQuery(id+"F12.opPattern","COPY",BODY,{"derivedFrom":makeQuery(id+"F7.opPattern","COPY",BODY,{"derivedFrom":makeQuery(id+"F5.opPattern","COPY",BODY,{"derivedFrom":makeQuery(id+"F4.opPattern","COPY",BODY,{"derivedFrom":makeQuery(id+"F3.opPattern","COPY",BODY,{"derivedFrom":makeQuery(id+"F1.opExtrude","SWEPT_BODY",BODY,{"disambiguationData":[OSD([sQuery(id+"F0.wireOp",EDGE,"E1.0"),sQuery(id+"F0.wireOp",EDGE,"E1.1"),sQuery(id+"F0.wireOp",EDGE,"E1.2"),sQuery(id+"F0.wireOp",EDGE,"E1.3"),sQuery(id+"F0.wireOp",EDGE,"E1.4"),sQuery(id+"F0.wireOp",EDGE,"E1.5"),sQuery(id+"F0.wireOp",EDGE,"E3.0"),sQuery(id+"F0.wireOp",EDGE,"E3.1"),sQuery(id+"F0.wireOp",EDGE,"E3.2"),sQuery(id+"F0.wireOp",EDGE,"E3.3"),sQuery(id+"F0.wireOp",EDGE,"E3.4"),sQuery(id+"F0.wireOp",EDGE,"E3.5")])]}),"instanceName":"1"}),"instanceName":"1"}),"instanceName":"1"}),"instanceName":"1"}),"instanceName":"1"});
            var Q6;
            Q6=makeQuery(id+"F12.opPattern","COPY",BODY,{"derivedFrom":makeQuery(id+"F7.opPattern","COPY",BODY,{"derivedFrom":makeQuery(id+"F6.opPattern","COPY",BODY,{"derivedFrom":makeQuery(id+"F5.opPattern","COPY",BODY,{"derivedFrom":makeQuery(id+"F4.opPattern","COPY",BODY,{"derivedFrom":makeQuery(id+"F3.opPattern","COPY",BODY,{"derivedFrom":makeQuery(id+"F1.opExtrude","SWEPT_BODY",BODY,{"disambiguationData":[OSD([sQuery(id+"F0.wireOp",EDGE,"E1.0"),sQuery(id+"F0.wireOp",EDGE,"E1.1"),sQuery(id+"F0.wireOp",EDGE,"E1.2"),sQuery(id+"F0.wireOp",EDGE,"E1.3"),sQuery(id+"F0.wireOp",EDGE,"E1.4"),sQuery(id+"F0.wireOp",EDGE,"E1.5"),sQuery(id+"F0.wireOp",EDGE,"E3.0"),sQuery(id+"F0.wireOp",EDGE,"E3.1"),sQuery(id+"F0.wireOp",EDGE,"E3.2"),sQuery(id+"F0.wireOp",EDGE,"E3.3"),sQuery(id+"F0.wireOp",EDGE,"E3.4"),sQuery(id+"F0.wireOp",EDGE,"E3.5")])]}),"instanceName":"1"}),"instanceName":"1"}),"instanceName":"1"}),"instanceName":"1"}),"instanceName":"1"}),"instanceName":"1"});
            var Q7;
            Q7=makeQuery(id+"F12.opPattern","COPY",BODY,{"derivedFrom":makeQuery(id+"F6.opPattern","COPY",BODY,{"derivedFrom":makeQuery(id+"F4.opPattern","COPY",BODY,{"derivedFrom":makeQuery(id+"F1.opExtrude","SWEPT_BODY",BODY,{"disambiguationData":[OSD([sQuery(id+"F0.wireOp",EDGE,"E1.0"),sQuery(id+"F0.wireOp",EDGE,"E1.1"),sQuery(id+"F0.wireOp",EDGE,"E1.2"),sQuery(id+"F0.wireOp",EDGE,"E1.3"),sQuery(id+"F0.wireOp",EDGE,"E1.4"),sQuery(id+"F0.wireOp",EDGE,"E1.5"),sQuery(id+"F0.wireOp",EDGE,"E3.0"),sQuery(id+"F0.wireOp",EDGE,"E3.1"),sQuery(id+"F0.wireOp",EDGE,"E3.2"),sQuery(id+"F0.wireOp",EDGE,"E3.3"),sQuery(id+"F0.wireOp",EDGE,"E3.4"),sQuery(id+"F0.wireOp",EDGE,"E3.5")])]}),"instanceName":"1"}),"instanceName":"1"}),"instanceName":"1"});
            var Q8;
            Q8=makeQuery(id+"F12.opPattern","COPY",BODY,{"derivedFrom":makeQuery(id+"F9.opPattern","COPY",BODY,{"derivedFrom":makeQuery(id+"F4.opPattern","COPY",BODY,{"derivedFrom":makeQuery(id+"F3.opPattern","COPY",BODY,{"derivedFrom":makeQuery(id+"F1.opExtrude","SWEPT_BODY",BODY,{"disambiguationData":[OSD([sQuery(id+"F0.wireOp",EDGE,"E1.0"),sQuery(id+"F0.wireOp",EDGE,"E1.1"),sQuery(id+"F0.wireOp",EDGE,"E1.2"),sQuery(id+"F0.wireOp",EDGE,"E1.3"),sQuery(id+"F0.wireOp",EDGE,"E1.4"),sQuery(id+"F0.wireOp",EDGE,"E1.5"),sQuery(id+"F0.wireOp",EDGE,"E3.0"),sQuery(id+"F0.wireOp",EDGE,"E3.1"),sQuery(id+"F0.wireOp",EDGE,"E3.2"),sQuery(id+"F0.wireOp",EDGE,"E3.3"),sQuery(id+"F0.wireOp",EDGE,"E3.4"),sQuery(id+"F0.wireOp",EDGE,"E3.5")])]}),"instanceName":"1"}),"instanceName":"1"}),"instanceName":"1"}),"instanceName":"1"});
            var Q9;
            Q9=makeQuery(id+"F12.opPattern","COPY",BODY,{"derivedFrom":makeQuery(id+"F6.opPattern","COPY",BODY,{"derivedFrom":makeQuery(id+"F3.opPattern","COPY",BODY,{"derivedFrom":makeQuery(id+"F1.opExtrude","SWEPT_BODY",BODY,{"disambiguationData":[OSD([sQuery(id+"F0.wireOp",EDGE,"E1.0"),sQuery(id+"F0.wireOp",EDGE,"E1.1"),sQuery(id+"F0.wireOp",EDGE,"E1.2"),sQuery(id+"F0.wireOp",EDGE,"E1.3"),sQuery(id+"F0.wireOp",EDGE,"E1.4"),sQuery(id+"F0.wireOp",EDGE,"E1.5"),sQuery(id+"F0.wireOp",EDGE,"E3.0"),sQuery(id+"F0.wireOp",EDGE,"E3.1"),sQuery(id+"F0.wireOp",EDGE,"E3.2"),sQuery(id+"F0.wireOp",EDGE,"E3.3"),sQuery(id+"F0.wireOp",EDGE,"E3.4"),sQuery(id+"F0.wireOp",EDGE,"E3.5")])]}),"instanceName":"1"}),"instanceName":"1"}),"instanceName":"1"});
            var Q10;
            Q10=makeQuery(id+"F12.opPattern","COPY",BODY,{"derivedFrom":makeQuery(id+"F6.opPattern","COPY",BODY,{"derivedFrom":makeQuery(id+"F4.opPattern","COPY",BODY,{"derivedFrom":makeQuery(id+"F3.opPattern","COPY",BODY,{"derivedFrom":makeQuery(id+"F1.opExtrude","SWEPT_BODY",BODY,{"disambiguationData":[OSD([sQuery(id+"F0.wireOp",EDGE,"E1.0"),sQuery(id+"F0.wireOp",EDGE,"E1.1"),sQuery(id+"F0.wireOp",EDGE,"E1.2"),sQuery(id+"F0.wireOp",EDGE,"E1.3"),sQuery(id+"F0.wireOp",EDGE,"E1.4"),sQuery(id+"F0.wireOp",EDGE,"E1.5"),sQuery(id+"F0.wireOp",EDGE,"E3.0"),sQuery(id+"F0.wireOp",EDGE,"E3.1"),sQuery(id+"F0.wireOp",EDGE,"E3.2"),sQuery(id+"F0.wireOp",EDGE,"E3.3"),sQuery(id+"F0.wireOp",EDGE,"E3.4"),sQuery(id+"F0.wireOp",EDGE,"E3.5")])]}),"instanceName":"1"}),"instanceName":"1"}),"instanceName":"1"}),"instanceName":"1"});
            var Q11;
            Q11=makeQuery(id+"F12.opPattern","COPY",BODY,{"derivedFrom":makeQuery(id+"F9.opPattern","COPY",BODY,{"derivedFrom":makeQuery(id+"F4.opPattern","COPY",BODY,{"derivedFrom":makeQuery(id+"F1.opExtrude","SWEPT_BODY",BODY,{"disambiguationData":[OSD([sQuery(id+"F0.wireOp",EDGE,"E1.0"),sQuery(id+"F0.wireOp",EDGE,"E1.1"),sQuery(id+"F0.wireOp",EDGE,"E1.2"),sQuery(id+"F0.wireOp",EDGE,"E1.3"),sQuery(id+"F0.wireOp",EDGE,"E1.4"),sQuery(id+"F0.wireOp",EDGE,"E1.5"),sQuery(id+"F0.wireOp",EDGE,"E3.0"),sQuery(id+"F0.wireOp",EDGE,"E3.1"),sQuery(id+"F0.wireOp",EDGE,"E3.2"),sQuery(id+"F0.wireOp",EDGE,"E3.3"),sQuery(id+"F0.wireOp",EDGE,"E3.4"),sQuery(id+"F0.wireOp",EDGE,"E3.5")])]}),"instanceName":"1"}),"instanceName":"1"}),"instanceName":"1"});
            var Q12;
            Q12=makeQuery(id+"F12.opPattern","COPY",BODY,{"derivedFrom":makeQuery(id+"F9.opPattern","COPY",BODY,{"derivedFrom":makeQuery(id+"F3.opPattern","COPY",BODY,{"derivedFrom":makeQuery(id+"F1.opExtrude","SWEPT_BODY",BODY,{"disambiguationData":[OSD([sQuery(id+"F0.wireOp",EDGE,"E1.0"),sQuery(id+"F0.wireOp",EDGE,"E1.1"),sQuery(id+"F0.wireOp",EDGE,"E1.2"),sQuery(id+"F0.wireOp",EDGE,"E1.3"),sQuery(id+"F0.wireOp",EDGE,"E1.4"),sQuery(id+"F0.wireOp",EDGE,"E1.5"),sQuery(id+"F0.wireOp",EDGE,"E3.0"),sQuery(id+"F0.wireOp",EDGE,"E3.1"),sQuery(id+"F0.wireOp",EDGE,"E3.2"),sQuery(id+"F0.wireOp",EDGE,"E3.3"),sQuery(id+"F0.wireOp",EDGE,"E3.4"),sQuery(id+"F0.wireOp",EDGE,"E3.5")])]}),"instanceName":"1"}),"instanceName":"1"}),"instanceName":"1"});
            var Q13;
            Q13=makeQuery(id+"F12.opPattern","COPY",BODY,{"derivedFrom":makeQuery(id+"F9.opPattern","COPY",BODY,{"derivedFrom":makeQuery(id+"F1.opExtrude","SWEPT_BODY",BODY,{"disambiguationData":[OSD([sQuery(id+"F0.wireOp",EDGE,"E1.0"),sQuery(id+"F0.wireOp",EDGE,"E1.1"),sQuery(id+"F0.wireOp",EDGE,"E1.2"),sQuery(id+"F0.wireOp",EDGE,"E1.3"),sQuery(id+"F0.wireOp",EDGE,"E1.4"),sQuery(id+"F0.wireOp",EDGE,"E1.5"),sQuery(id+"F0.wireOp",EDGE,"E3.0"),sQuery(id+"F0.wireOp",EDGE,"E3.1"),sQuery(id+"F0.wireOp",EDGE,"E3.2"),sQuery(id+"F0.wireOp",EDGE,"E3.3"),sQuery(id+"F0.wireOp",EDGE,"E3.4"),sQuery(id+"F0.wireOp",EDGE,"E3.5")])]}),"instanceName":"1"}),"instanceName":"1"});
            var Q14;
            Q14=makeQuery(id+"F12.opPattern","COPY",BODY,{"derivedFrom":makeQuery(id+"F7.opPattern","COPY",BODY,{"derivedFrom":makeQuery(id+"F3.opPattern","COPY",BODY,{"derivedFrom":makeQuery(id+"F1.opExtrude","SWEPT_BODY",BODY,{"disambiguationData":[OSD([sQuery(id+"F0.wireOp",EDGE,"E1.0"),sQuery(id+"F0.wireOp",EDGE,"E1.1"),sQuery(id+"F0.wireOp",EDGE,"E1.2"),sQuery(id+"F0.wireOp",EDGE,"E1.3"),sQuery(id+"F0.wireOp",EDGE,"E1.4"),sQuery(id+"F0.wireOp",EDGE,"E1.5"),sQuery(id+"F0.wireOp",EDGE,"E3.0"),sQuery(id+"F0.wireOp",EDGE,"E3.1"),sQuery(id+"F0.wireOp",EDGE,"E3.2"),sQuery(id+"F0.wireOp",EDGE,"E3.3"),sQuery(id+"F0.wireOp",EDGE,"E3.4"),sQuery(id+"F0.wireOp",EDGE,"E3.5")])]}),"instanceName":"1"}),"instanceName":"1"}),"instanceName":"1"});
            var Q15;
            Q15=makeQuery(id+"F12.opPattern","COPY",BODY,{"derivedFrom":makeQuery(id+"F6.opPattern","COPY",BODY,{"derivedFrom":makeQuery(id+"F5.opPattern","COPY",BODY,{"derivedFrom":makeQuery(id+"F4.opPattern","COPY",BODY,{"derivedFrom":makeQuery(id+"F3.opPattern","COPY",BODY,{"derivedFrom":makeQuery(id+"F1.opExtrude","SWEPT_BODY",BODY,{"disambiguationData":[OSD([sQuery(id+"F0.wireOp",EDGE,"E1.0"),sQuery(id+"F0.wireOp",EDGE,"E1.1"),sQuery(id+"F0.wireOp",EDGE,"E1.2"),sQuery(id+"F0.wireOp",EDGE,"E1.3"),sQuery(id+"F0.wireOp",EDGE,"E1.4"),sQuery(id+"F0.wireOp",EDGE,"E1.5"),sQuery(id+"F0.wireOp",EDGE,"E3.0"),sQuery(id+"F0.wireOp",EDGE,"E3.1"),sQuery(id+"F0.wireOp",EDGE,"E3.2"),sQuery(id+"F0.wireOp",EDGE,"E3.3"),sQuery(id+"F0.wireOp",EDGE,"E3.4"),sQuery(id+"F0.wireOp",EDGE,"E3.5")])]}),"instanceName":"1"}),"instanceName":"1"}),"instanceName":"1"}),"instanceName":"1"}),"instanceName":"1"});
            var Q16;
            Q16=makeQuery(id+"F12.opPattern","COPY",BODY,{"derivedFrom":makeQuery(id+"F6.opPattern","COPY",BODY,{"derivedFrom":makeQuery(id+"F5.opPattern","COPY",BODY,{"derivedFrom":makeQuery(id+"F4.opPattern","COPY",BODY,{"derivedFrom":makeQuery(id+"F1.opExtrude","SWEPT_BODY",BODY,{"disambiguationData":[OSD([sQuery(id+"F0.wireOp",EDGE,"E1.0"),sQuery(id+"F0.wireOp",EDGE,"E1.1"),sQuery(id+"F0.wireOp",EDGE,"E1.2"),sQuery(id+"F0.wireOp",EDGE,"E1.3"),sQuery(id+"F0.wireOp",EDGE,"E1.4"),sQuery(id+"F0.wireOp",EDGE,"E1.5"),sQuery(id+"F0.wireOp",EDGE,"E3.0"),sQuery(id+"F0.wireOp",EDGE,"E3.1"),sQuery(id+"F0.wireOp",EDGE,"E3.2"),sQuery(id+"F0.wireOp",EDGE,"E3.3"),sQuery(id+"F0.wireOp",EDGE,"E3.4"),sQuery(id+"F0.wireOp",EDGE,"E3.5")])]}),"instanceName":"1"}),"instanceName":"1"}),"instanceName":"1"}),"instanceName":"1"});
            var Q17;
            Q17=makeQuery(id+"F12.opPattern","COPY",BODY,{"derivedFrom":makeQuery(id+"F9.opPattern","COPY",BODY,{"derivedFrom":makeQuery(id+"F6.opPattern","COPY",BODY,{"derivedFrom":makeQuery(id+"F1.opExtrude","SWEPT_BODY",BODY,{"disambiguationData":[OSD([sQuery(id+"F0.wireOp",EDGE,"E1.0"),sQuery(id+"F0.wireOp",EDGE,"E1.1"),sQuery(id+"F0.wireOp",EDGE,"E1.2"),sQuery(id+"F0.wireOp",EDGE,"E1.3"),sQuery(id+"F0.wireOp",EDGE,"E1.4"),sQuery(id+"F0.wireOp",EDGE,"E1.5"),sQuery(id+"F0.wireOp",EDGE,"E3.0"),sQuery(id+"F0.wireOp",EDGE,"E3.1"),sQuery(id+"F0.wireOp",EDGE,"E3.2"),sQuery(id+"F0.wireOp",EDGE,"E3.3"),sQuery(id+"F0.wireOp",EDGE,"E3.4"),sQuery(id+"F0.wireOp",EDGE,"E3.5")])]}),"instanceName":"1"}),"instanceName":"1"}),"instanceName":"1"});
            var Q18;
            Q18=makeQuery(id+"F12.opPattern","COPY",BODY,{"derivedFrom":makeQuery(id+"F5.opPattern","COPY",BODY,{"derivedFrom":makeQuery(id+"F4.opPattern","COPY",BODY,{"derivedFrom":makeQuery(id+"F1.opExtrude","SWEPT_BODY",BODY,{"disambiguationData":[OSD([sQuery(id+"F0.wireOp",EDGE,"E1.0"),sQuery(id+"F0.wireOp",EDGE,"E1.1"),sQuery(id+"F0.wireOp",EDGE,"E1.2"),sQuery(id+"F0.wireOp",EDGE,"E1.3"),sQuery(id+"F0.wireOp",EDGE,"E1.4"),sQuery(id+"F0.wireOp",EDGE,"E1.5"),sQuery(id+"F0.wireOp",EDGE,"E3.0"),sQuery(id+"F0.wireOp",EDGE,"E3.1"),sQuery(id+"F0.wireOp",EDGE,"E3.2"),sQuery(id+"F0.wireOp",EDGE,"E3.3"),sQuery(id+"F0.wireOp",EDGE,"E3.4"),sQuery(id+"F0.wireOp",EDGE,"E3.5")])]}),"instanceName":"1"}),"instanceName":"1"}),"instanceName":"1"});
            var Q19;
            Q19=makeQuery(id+"F12.opPattern","COPY",BODY,{"derivedFrom":makeQuery(id+"F9.opPattern","COPY",BODY,{"derivedFrom":makeQuery(id+"F6.opPattern","COPY",BODY,{"derivedFrom":makeQuery(id+"F3.opPattern","COPY",BODY,{"derivedFrom":makeQuery(id+"F1.opExtrude","SWEPT_BODY",BODY,{"disambiguationData":[OSD([sQuery(id+"F0.wireOp",EDGE,"E1.0"),sQuery(id+"F0.wireOp",EDGE,"E1.1"),sQuery(id+"F0.wireOp",EDGE,"E1.2"),sQuery(id+"F0.wireOp",EDGE,"E1.3"),sQuery(id+"F0.wireOp",EDGE,"E1.4"),sQuery(id+"F0.wireOp",EDGE,"E1.5"),sQuery(id+"F0.wireOp",EDGE,"E3.0"),sQuery(id+"F0.wireOp",EDGE,"E3.1"),sQuery(id+"F0.wireOp",EDGE,"E3.2"),sQuery(id+"F0.wireOp",EDGE,"E3.3"),sQuery(id+"F0.wireOp",EDGE,"E3.4"),sQuery(id+"F0.wireOp",EDGE,"E3.5")])]}),"instanceName":"1"}),"instanceName":"1"}),"instanceName":"1"}),"instanceName":"1"});
            var Q20;
            Q20=makeQuery(id+"F12.opPattern","COPY",BODY,{"derivedFrom":makeQuery(id+"F7.opPattern","COPY",BODY,{"derivedFrom":makeQuery(id+"F6.opPattern","COPY",BODY,{"derivedFrom":makeQuery(id+"F1.opExtrude","SWEPT_BODY",BODY,{"disambiguationData":[OSD([sQuery(id+"F0.wireOp",EDGE,"E1.0"),sQuery(id+"F0.wireOp",EDGE,"E1.1"),sQuery(id+"F0.wireOp",EDGE,"E1.2"),sQuery(id+"F0.wireOp",EDGE,"E1.3"),sQuery(id+"F0.wireOp",EDGE,"E1.4"),sQuery(id+"F0.wireOp",EDGE,"E1.5"),sQuery(id+"F0.wireOp",EDGE,"E3.0"),sQuery(id+"F0.wireOp",EDGE,"E3.1"),sQuery(id+"F0.wireOp",EDGE,"E3.2"),sQuery(id+"F0.wireOp",EDGE,"E3.3"),sQuery(id+"F0.wireOp",EDGE,"E3.4"),sQuery(id+"F0.wireOp",EDGE,"E3.5")])]}),"instanceName":"1"}),"instanceName":"1"}),"instanceName":"1"});
            var Q21;
            Q21=makeQuery(id+"F12.opPattern","COPY",BODY,{"derivedFrom":makeQuery(id+"F7.opPattern","COPY",BODY,{"derivedFrom":makeQuery(id+"F6.opPattern","COPY",BODY,{"derivedFrom":makeQuery(id+"F4.opPattern","COPY",BODY,{"derivedFrom":makeQuery(id+"F3.opPattern","COPY",BODY,{"derivedFrom":makeQuery(id+"F1.opExtrude","SWEPT_BODY",BODY,{"disambiguationData":[OSD([sQuery(id+"F0.wireOp",EDGE,"E1.0"),sQuery(id+"F0.wireOp",EDGE,"E1.1"),sQuery(id+"F0.wireOp",EDGE,"E1.2"),sQuery(id+"F0.wireOp",EDGE,"E1.3"),sQuery(id+"F0.wireOp",EDGE,"E1.4"),sQuery(id+"F0.wireOp",EDGE,"E1.5"),sQuery(id+"F0.wireOp",EDGE,"E3.0"),sQuery(id+"F0.wireOp",EDGE,"E3.1"),sQuery(id+"F0.wireOp",EDGE,"E3.2"),sQuery(id+"F0.wireOp",EDGE,"E3.3"),sQuery(id+"F0.wireOp",EDGE,"E3.4"),sQuery(id+"F0.wireOp",EDGE,"E3.5")])]}),"instanceName":"1"}),"instanceName":"1"}),"instanceName":"1"}),"instanceName":"1"}),"instanceName":"1"});
            var Q22;
            Q22=makeQuery(id+"F12.opPattern","COPY",BODY,{"derivedFrom":makeQuery(id+"F7.opPattern","COPY",BODY,{"derivedFrom":makeQuery(id+"F6.opPattern","COPY",BODY,{"derivedFrom":makeQuery(id+"F4.opPattern","COPY",BODY,{"derivedFrom":makeQuery(id+"F1.opExtrude","SWEPT_BODY",BODY,{"disambiguationData":[OSD([sQuery(id+"F0.wireOp",EDGE,"E1.0"),sQuery(id+"F0.wireOp",EDGE,"E1.1"),sQuery(id+"F0.wireOp",EDGE,"E1.2"),sQuery(id+"F0.wireOp",EDGE,"E1.3"),sQuery(id+"F0.wireOp",EDGE,"E1.4"),sQuery(id+"F0.wireOp",EDGE,"E1.5"),sQuery(id+"F0.wireOp",EDGE,"E3.0"),sQuery(id+"F0.wireOp",EDGE,"E3.1"),sQuery(id+"F0.wireOp",EDGE,"E3.2"),sQuery(id+"F0.wireOp",EDGE,"E3.3"),sQuery(id+"F0.wireOp",EDGE,"E3.4"),sQuery(id+"F0.wireOp",EDGE,"E3.5")])]}),"instanceName":"1"}),"instanceName":"1"}),"instanceName":"1"}),"instanceName":"1"});
            var Q23;
            Q23=makeQuery(id+"F12.opPattern","COPY",BODY,{"derivedFrom":makeQuery(id+"F7.opPattern","COPY",BODY,{"derivedFrom":makeQuery(id+"F6.opPattern","COPY",BODY,{"derivedFrom":makeQuery(id+"F3.opPattern","COPY",BODY,{"derivedFrom":makeQuery(id+"F1.opExtrude","SWEPT_BODY",BODY,{"disambiguationData":[OSD([sQuery(id+"F0.wireOp",EDGE,"E1.0"),sQuery(id+"F0.wireOp",EDGE,"E1.1"),sQuery(id+"F0.wireOp",EDGE,"E1.2"),sQuery(id+"F0.wireOp",EDGE,"E1.3"),sQuery(id+"F0.wireOp",EDGE,"E1.4"),sQuery(id+"F0.wireOp",EDGE,"E1.5"),sQuery(id+"F0.wireOp",EDGE,"E3.0"),sQuery(id+"F0.wireOp",EDGE,"E3.1"),sQuery(id+"F0.wireOp",EDGE,"E3.2"),sQuery(id+"F0.wireOp",EDGE,"E3.3"),sQuery(id+"F0.wireOp",EDGE,"E3.4"),sQuery(id+"F0.wireOp",EDGE,"E3.5")])]}),"instanceName":"1"}),"instanceName":"1"}),"instanceName":"1"}),"instanceName":"1"});
            var Q24;
            Q24=makeQuery(id+"F12.opPattern","COPY",BODY,{"derivedFrom":makeQuery(id+"F9.opPattern","COPY",BODY,{"derivedFrom":makeQuery(id+"F5.opPattern","COPY",BODY,{"derivedFrom":makeQuery(id+"F4.opPattern","COPY",BODY,{"derivedFrom":makeQuery(id+"F3.opPattern","COPY",BODY,{"derivedFrom":makeQuery(id+"F1.opExtrude","SWEPT_BODY",BODY,{"disambiguationData":[OSD([sQuery(id+"F0.wireOp",EDGE,"E1.0"),sQuery(id+"F0.wireOp",EDGE,"E1.1"),sQuery(id+"F0.wireOp",EDGE,"E1.2"),sQuery(id+"F0.wireOp",EDGE,"E1.3"),sQuery(id+"F0.wireOp",EDGE,"E1.4"),sQuery(id+"F0.wireOp",EDGE,"E1.5"),sQuery(id+"F0.wireOp",EDGE,"E3.0"),sQuery(id+"F0.wireOp",EDGE,"E3.1"),sQuery(id+"F0.wireOp",EDGE,"E3.2"),sQuery(id+"F0.wireOp",EDGE,"E3.3"),sQuery(id+"F0.wireOp",EDGE,"E3.4"),sQuery(id+"F0.wireOp",EDGE,"E3.5")])]}),"instanceName":"1"}),"instanceName":"1"}),"instanceName":"1"}),"instanceName":"1"}),"instanceName":"1"});
            var Q25;
            Q25=makeQuery(id+"F12.opPattern","COPY",BODY,{"derivedFrom":makeQuery(id+"F9.opPattern","COPY",BODY,{"derivedFrom":makeQuery(id+"F5.opPattern","COPY",BODY,{"derivedFrom":makeQuery(id+"F4.opPattern","COPY",BODY,{"derivedFrom":makeQuery(id+"F1.opExtrude","SWEPT_BODY",BODY,{"disambiguationData":[OSD([sQuery(id+"F0.wireOp",EDGE,"E1.0"),sQuery(id+"F0.wireOp",EDGE,"E1.1"),sQuery(id+"F0.wireOp",EDGE,"E1.2"),sQuery(id+"F0.wireOp",EDGE,"E1.3"),sQuery(id+"F0.wireOp",EDGE,"E1.4"),sQuery(id+"F0.wireOp",EDGE,"E1.5"),sQuery(id+"F0.wireOp",EDGE,"E3.0"),sQuery(id+"F0.wireOp",EDGE,"E3.1"),sQuery(id+"F0.wireOp",EDGE,"E3.2"),sQuery(id+"F0.wireOp",EDGE,"E3.3"),sQuery(id+"F0.wireOp",EDGE,"E3.4"),sQuery(id+"F0.wireOp",EDGE,"E3.5")])]}),"instanceName":"1"}),"instanceName":"1"}),"instanceName":"1"}),"instanceName":"1"});
            var Q26;
            Q26=makeQuery(id+"F12.opPattern","COPY",BODY,{"derivedFrom":makeQuery(id+"F9.opPattern","COPY",BODY,{"derivedFrom":makeQuery(id+"F6.opPattern","COPY",BODY,{"derivedFrom":makeQuery(id+"F4.opPattern","COPY",BODY,{"derivedFrom":makeQuery(id+"F1.opExtrude","SWEPT_BODY",BODY,{"disambiguationData":[OSD([sQuery(id+"F0.wireOp",EDGE,"E1.0"),sQuery(id+"F0.wireOp",EDGE,"E1.1"),sQuery(id+"F0.wireOp",EDGE,"E1.2"),sQuery(id+"F0.wireOp",EDGE,"E1.3"),sQuery(id+"F0.wireOp",EDGE,"E1.4"),sQuery(id+"F0.wireOp",EDGE,"E1.5"),sQuery(id+"F0.wireOp",EDGE,"E3.0"),sQuery(id+"F0.wireOp",EDGE,"E3.1"),sQuery(id+"F0.wireOp",EDGE,"E3.2"),sQuery(id+"F0.wireOp",EDGE,"E3.3"),sQuery(id+"F0.wireOp",EDGE,"E3.4"),sQuery(id+"F0.wireOp",EDGE,"E3.5")])]}),"instanceName":"1"}),"instanceName":"1"}),"instanceName":"1"}),"instanceName":"1"});
            var Q27;
            Q27=makeQuery(id+"F12.opPattern","COPY",BODY,{"derivedFrom":makeQuery(id+"F9.opPattern","COPY",BODY,{"derivedFrom":makeQuery(id+"F6.opPattern","COPY",BODY,{"derivedFrom":makeQuery(id+"F4.opPattern","COPY",BODY,{"derivedFrom":makeQuery(id+"F3.opPattern","COPY",BODY,{"derivedFrom":makeQuery(id+"F1.opExtrude","SWEPT_BODY",BODY,{"disambiguationData":[OSD([sQuery(id+"F0.wireOp",EDGE,"E1.0"),sQuery(id+"F0.wireOp",EDGE,"E1.1"),sQuery(id+"F0.wireOp",EDGE,"E1.2"),sQuery(id+"F0.wireOp",EDGE,"E1.3"),sQuery(id+"F0.wireOp",EDGE,"E1.4"),sQuery(id+"F0.wireOp",EDGE,"E1.5"),sQuery(id+"F0.wireOp",EDGE,"E3.0"),sQuery(id+"F0.wireOp",EDGE,"E3.1"),sQuery(id+"F0.wireOp",EDGE,"E3.2"),sQuery(id+"F0.wireOp",EDGE,"E3.3"),sQuery(id+"F0.wireOp",EDGE,"E3.4"),sQuery(id+"F0.wireOp",EDGE,"E3.5")])]}),"instanceName":"1"}),"instanceName":"1"}),"instanceName":"1"}),"instanceName":"1"}),"instanceName":"1"});
            var Q28;
            Q28=makeQuery(id+"F12.opPattern","COPY",BODY,{"derivedFrom":makeQuery(id+"F9.opPattern","COPY",BODY,{"derivedFrom":makeQuery(id+"F6.opPattern","COPY",BODY,{"derivedFrom":makeQuery(id+"F5.opPattern","COPY",BODY,{"derivedFrom":makeQuery(id+"F4.opPattern","COPY",BODY,{"derivedFrom":makeQuery(id+"F1.opExtrude","SWEPT_BODY",BODY,{"disambiguationData":[OSD([sQuery(id+"F0.wireOp",EDGE,"E1.0"),sQuery(id+"F0.wireOp",EDGE,"E1.1"),sQuery(id+"F0.wireOp",EDGE,"E1.2"),sQuery(id+"F0.wireOp",EDGE,"E1.3"),sQuery(id+"F0.wireOp",EDGE,"E1.4"),sQuery(id+"F0.wireOp",EDGE,"E1.5"),sQuery(id+"F0.wireOp",EDGE,"E3.0"),sQuery(id+"F0.wireOp",EDGE,"E3.1"),sQuery(id+"F0.wireOp",EDGE,"E3.2"),sQuery(id+"F0.wireOp",EDGE,"E3.3"),sQuery(id+"F0.wireOp",EDGE,"E3.4"),sQuery(id+"F0.wireOp",EDGE,"E3.5")])]}),"instanceName":"1"}),"instanceName":"1"}),"instanceName":"1"}),"instanceName":"1"}),"instanceName":"1"});
            var Q29;
            Q29=makeQuery(id+"F12.opPattern","COPY",BODY,{"derivedFrom":makeQuery(id+"F9.opPattern","COPY",BODY,{"derivedFrom":makeQuery(id+"F7.opPattern","COPY",BODY,{"derivedFrom":makeQuery(id+"F3.opPattern","COPY",BODY,{"derivedFrom":makeQuery(id+"F1.opExtrude","SWEPT_BODY",BODY,{"disambiguationData":[OSD([sQuery(id+"F0.wireOp",EDGE,"E1.0"),sQuery(id+"F0.wireOp",EDGE,"E1.1"),sQuery(id+"F0.wireOp",EDGE,"E1.2"),sQuery(id+"F0.wireOp",EDGE,"E1.3"),sQuery(id+"F0.wireOp",EDGE,"E1.4"),sQuery(id+"F0.wireOp",EDGE,"E1.5"),sQuery(id+"F0.wireOp",EDGE,"E3.0"),sQuery(id+"F0.wireOp",EDGE,"E3.1"),sQuery(id+"F0.wireOp",EDGE,"E3.2"),sQuery(id+"F0.wireOp",EDGE,"E3.3"),sQuery(id+"F0.wireOp",EDGE,"E3.4"),sQuery(id+"F0.wireOp",EDGE,"E3.5")])]}),"instanceName":"1"}),"instanceName":"1"}),"instanceName":"1"}),"instanceName":"1"});
            var Q30;
            Q30=makeQuery(id+"F12.opPattern","COPY",BODY,{"derivedFrom":makeQuery(id+"F9.opPattern","COPY",BODY,{"derivedFrom":makeQuery(id+"F7.opPattern","COPY",BODY,{"derivedFrom":makeQuery(id+"F1.opExtrude","SWEPT_BODY",BODY,{"disambiguationData":[OSD([sQuery(id+"F0.wireOp",EDGE,"E1.0"),sQuery(id+"F0.wireOp",EDGE,"E1.1"),sQuery(id+"F0.wireOp",EDGE,"E1.2"),sQuery(id+"F0.wireOp",EDGE,"E1.3"),sQuery(id+"F0.wireOp",EDGE,"E1.4"),sQuery(id+"F0.wireOp",EDGE,"E1.5"),sQuery(id+"F0.wireOp",EDGE,"E3.0"),sQuery(id+"F0.wireOp",EDGE,"E3.1"),sQuery(id+"F0.wireOp",EDGE,"E3.2"),sQuery(id+"F0.wireOp",EDGE,"E3.3"),sQuery(id+"F0.wireOp",EDGE,"E3.4"),sQuery(id+"F0.wireOp",EDGE,"E3.5")])]}),"instanceName":"1"}),"instanceName":"1"}),"instanceName":"1"});
            var Q31;
            Q31=makeQuery(id+"F12.opPattern","COPY",BODY,{"derivedFrom":makeQuery(id+"F9.opPattern","COPY",BODY,{"derivedFrom":makeQuery(id+"F6.opPattern","COPY",BODY,{"derivedFrom":makeQuery(id+"F5.opPattern","COPY",BODY,{"derivedFrom":makeQuery(id+"F4.opPattern","COPY",BODY,{"derivedFrom":makeQuery(id+"F3.opPattern","COPY",BODY,{"derivedFrom":makeQuery(id+"F1.opExtrude","SWEPT_BODY",BODY,{"disambiguationData":[OSD([sQuery(id+"F0.wireOp",EDGE,"E1.0"),sQuery(id+"F0.wireOp",EDGE,"E1.1"),sQuery(id+"F0.wireOp",EDGE,"E1.2"),sQuery(id+"F0.wireOp",EDGE,"E1.3"),sQuery(id+"F0.wireOp",EDGE,"E1.4"),sQuery(id+"F0.wireOp",EDGE,"E1.5"),sQuery(id+"F0.wireOp",EDGE,"E3.0"),sQuery(id+"F0.wireOp",EDGE,"E3.1"),sQuery(id+"F0.wireOp",EDGE,"E3.2"),sQuery(id+"F0.wireOp",EDGE,"E3.3"),sQuery(id+"F0.wireOp",EDGE,"E3.4"),sQuery(id+"F0.wireOp",EDGE,"E3.5")])]}),"instanceName":"1"}),"instanceName":"1"}),"instanceName":"1"}),"instanceName":"1"}),"instanceName":"1"}),"instanceName":"1"});
            var Q32;
            Q32=makeQuery(id+"F12.opPattern","COPY",BODY,{"derivedFrom":makeQuery(id+"F9.opPattern","COPY",BODY,{"derivedFrom":makeQuery(id+"F7.opPattern","COPY",BODY,{"derivedFrom":makeQuery(id+"F4.opPattern","COPY",BODY,{"derivedFrom":makeQuery(id+"F1.opExtrude","SWEPT_BODY",BODY,{"disambiguationData":[OSD([sQuery(id+"F0.wireOp",EDGE,"E1.0"),sQuery(id+"F0.wireOp",EDGE,"E1.1"),sQuery(id+"F0.wireOp",EDGE,"E1.2"),sQuery(id+"F0.wireOp",EDGE,"E1.3"),sQuery(id+"F0.wireOp",EDGE,"E1.4"),sQuery(id+"F0.wireOp",EDGE,"E1.5"),sQuery(id+"F0.wireOp",EDGE,"E3.0"),sQuery(id+"F0.wireOp",EDGE,"E3.1"),sQuery(id+"F0.wireOp",EDGE,"E3.2"),sQuery(id+"F0.wireOp",EDGE,"E3.3"),sQuery(id+"F0.wireOp",EDGE,"E3.4"),sQuery(id+"F0.wireOp",EDGE,"E3.5")])]}),"instanceName":"1"}),"instanceName":"1"}),"instanceName":"1"}),"instanceName":"1"});
            var Q33;
            Q33=makeQuery(id+"F12.opPattern","COPY",BODY,{"derivedFrom":makeQuery(id+"F9.opPattern","COPY",BODY,{"derivedFrom":makeQuery(id+"F7.opPattern","COPY",BODY,{"derivedFrom":makeQuery(id+"F4.opPattern","COPY",BODY,{"derivedFrom":makeQuery(id+"F3.opPattern","COPY",BODY,{"derivedFrom":makeQuery(id+"F1.opExtrude","SWEPT_BODY",BODY,{"disambiguationData":[OSD([sQuery(id+"F0.wireOp",EDGE,"E1.0"),sQuery(id+"F0.wireOp",EDGE,"E1.1"),sQuery(id+"F0.wireOp",EDGE,"E1.2"),sQuery(id+"F0.wireOp",EDGE,"E1.3"),sQuery(id+"F0.wireOp",EDGE,"E1.4"),sQuery(id+"F0.wireOp",EDGE,"E1.5"),sQuery(id+"F0.wireOp",EDGE,"E3.0"),sQuery(id+"F0.wireOp",EDGE,"E3.1"),sQuery(id+"F0.wireOp",EDGE,"E3.2"),sQuery(id+"F0.wireOp",EDGE,"E3.3"),sQuery(id+"F0.wireOp",EDGE,"E3.4"),sQuery(id+"F0.wireOp",EDGE,"E3.5")])]}),"instanceName":"1"}),"instanceName":"1"}),"instanceName":"1"}),"instanceName":"1"}),"instanceName":"1"});
            var Q34;
            Q34=makeQuery(id+"F12.opPattern","COPY",BODY,{"derivedFrom":makeQuery(id+"F9.opPattern","COPY",BODY,{"derivedFrom":makeQuery(id+"F7.opPattern","COPY",BODY,{"derivedFrom":makeQuery(id+"F5.opPattern","COPY",BODY,{"derivedFrom":makeQuery(id+"F4.opPattern","COPY",BODY,{"derivedFrom":makeQuery(id+"F1.opExtrude","SWEPT_BODY",BODY,{"disambiguationData":[OSD([sQuery(id+"F0.wireOp",EDGE,"E1.0"),sQuery(id+"F0.wireOp",EDGE,"E1.1"),sQuery(id+"F0.wireOp",EDGE,"E1.2"),sQuery(id+"F0.wireOp",EDGE,"E1.3"),sQuery(id+"F0.wireOp",EDGE,"E1.4"),sQuery(id+"F0.wireOp",EDGE,"E1.5"),sQuery(id+"F0.wireOp",EDGE,"E3.0"),sQuery(id+"F0.wireOp",EDGE,"E3.1"),sQuery(id+"F0.wireOp",EDGE,"E3.2"),sQuery(id+"F0.wireOp",EDGE,"E3.3"),sQuery(id+"F0.wireOp",EDGE,"E3.4"),sQuery(id+"F0.wireOp",EDGE,"E3.5")])]}),"instanceName":"1"}),"instanceName":"1"}),"instanceName":"1"}),"instanceName":"1"}),"instanceName":"1"});
            var Q35;
            Q35=makeQuery(id+"F12.opPattern","COPY",BODY,{"derivedFrom":makeQuery(id+"F9.opPattern","COPY",BODY,{"derivedFrom":makeQuery(id+"F7.opPattern","COPY",BODY,{"derivedFrom":makeQuery(id+"F6.opPattern","COPY",BODY,{"derivedFrom":makeQuery(id+"F3.opPattern","COPY",BODY,{"derivedFrom":makeQuery(id+"F1.opExtrude","SWEPT_BODY",BODY,{"disambiguationData":[OSD([sQuery(id+"F0.wireOp",EDGE,"E1.0"),sQuery(id+"F0.wireOp",EDGE,"E1.1"),sQuery(id+"F0.wireOp",EDGE,"E1.2"),sQuery(id+"F0.wireOp",EDGE,"E1.3"),sQuery(id+"F0.wireOp",EDGE,"E1.4"),sQuery(id+"F0.wireOp",EDGE,"E1.5"),sQuery(id+"F0.wireOp",EDGE,"E3.0"),sQuery(id+"F0.wireOp",EDGE,"E3.1"),sQuery(id+"F0.wireOp",EDGE,"E3.2"),sQuery(id+"F0.wireOp",EDGE,"E3.3"),sQuery(id+"F0.wireOp",EDGE,"E3.4"),sQuery(id+"F0.wireOp",EDGE,"E3.5")])]}),"instanceName":"1"}),"instanceName":"1"}),"instanceName":"1"}),"instanceName":"1"}),"instanceName":"1"});
            var Q36;
            Q36=makeQuery(id+"F12.opPattern","COPY",BODY,{"derivedFrom":makeQuery(id+"F9.opPattern","COPY",BODY,{"derivedFrom":makeQuery(id+"F7.opPattern","COPY",BODY,{"derivedFrom":makeQuery(id+"F5.opPattern","COPY",BODY,{"derivedFrom":makeQuery(id+"F4.opPattern","COPY",BODY,{"derivedFrom":makeQuery(id+"F3.opPattern","COPY",BODY,{"derivedFrom":makeQuery(id+"F1.opExtrude","SWEPT_BODY",BODY,{"disambiguationData":[OSD([sQuery(id+"F0.wireOp",EDGE,"E1.0"),sQuery(id+"F0.wireOp",EDGE,"E1.1"),sQuery(id+"F0.wireOp",EDGE,"E1.2"),sQuery(id+"F0.wireOp",EDGE,"E1.3"),sQuery(id+"F0.wireOp",EDGE,"E1.4"),sQuery(id+"F0.wireOp",EDGE,"E1.5"),sQuery(id+"F0.wireOp",EDGE,"E3.0"),sQuery(id+"F0.wireOp",EDGE,"E3.1"),sQuery(id+"F0.wireOp",EDGE,"E3.2"),sQuery(id+"F0.wireOp",EDGE,"E3.3"),sQuery(id+"F0.wireOp",EDGE,"E3.4"),sQuery(id+"F0.wireOp",EDGE,"E3.5")])]}),"instanceName":"1"}),"instanceName":"1"}),"instanceName":"1"}),"instanceName":"1"}),"instanceName":"1"}),"instanceName":"1"});
            var Q37;
            Q37=makeQuery(id+"F12.opPattern","COPY",BODY,{"derivedFrom":makeQuery(id+"F9.opPattern","COPY",BODY,{"derivedFrom":makeQuery(id+"F7.opPattern","COPY",BODY,{"derivedFrom":makeQuery(id+"F6.opPattern","COPY",BODY,{"derivedFrom":makeQuery(id+"F5.opPattern","COPY",BODY,{"derivedFrom":makeQuery(id+"F4.opPattern","COPY",BODY,{"derivedFrom":makeQuery(id+"F1.opExtrude","SWEPT_BODY",BODY,{"disambiguationData":[OSD([sQuery(id+"F0.wireOp",EDGE,"E1.0"),sQuery(id+"F0.wireOp",EDGE,"E1.1"),sQuery(id+"F0.wireOp",EDGE,"E1.2"),sQuery(id+"F0.wireOp",EDGE,"E1.3"),sQuery(id+"F0.wireOp",EDGE,"E1.4"),sQuery(id+"F0.wireOp",EDGE,"E1.5"),sQuery(id+"F0.wireOp",EDGE,"E3.0"),sQuery(id+"F0.wireOp",EDGE,"E3.1"),sQuery(id+"F0.wireOp",EDGE,"E3.2"),sQuery(id+"F0.wireOp",EDGE,"E3.3"),sQuery(id+"F0.wireOp",EDGE,"E3.4"),sQuery(id+"F0.wireOp",EDGE,"E3.5")])]}),"instanceName":"1"}),"instanceName":"1"}),"instanceName":"1"}),"instanceName":"1"}),"instanceName":"1"}),"instanceName":"1"});
            var Q38;
            Q38=makeQuery(id+"F12.opPattern","COPY",BODY,{"derivedFrom":makeQuery(id+"F9.opPattern","COPY",BODY,{"derivedFrom":makeQuery(id+"F7.opPattern","COPY",BODY,{"derivedFrom":makeQuery(id+"F6.opPattern","COPY",BODY,{"derivedFrom":makeQuery(id+"F4.opPattern","COPY",BODY,{"derivedFrom":makeQuery(id+"F1.opExtrude","SWEPT_BODY",BODY,{"disambiguationData":[OSD([sQuery(id+"F0.wireOp",EDGE,"E1.0"),sQuery(id+"F0.wireOp",EDGE,"E1.1"),sQuery(id+"F0.wireOp",EDGE,"E1.2"),sQuery(id+"F0.wireOp",EDGE,"E1.3"),sQuery(id+"F0.wireOp",EDGE,"E1.4"),sQuery(id+"F0.wireOp",EDGE,"E1.5"),sQuery(id+"F0.wireOp",EDGE,"E3.0"),sQuery(id+"F0.wireOp",EDGE,"E3.1"),sQuery(id+"F0.wireOp",EDGE,"E3.2"),sQuery(id+"F0.wireOp",EDGE,"E3.3"),sQuery(id+"F0.wireOp",EDGE,"E3.4"),sQuery(id+"F0.wireOp",EDGE,"E3.5")])]}),"instanceName":"1"}),"instanceName":"1"}),"instanceName":"1"}),"instanceName":"1"}),"instanceName":"1"});
            var Q39;
            Q39=makeQuery(id+"F12.opPattern","COPY",BODY,{"derivedFrom":makeQuery(id+"F9.opPattern","COPY",BODY,{"derivedFrom":makeQuery(id+"F7.opPattern","COPY",BODY,{"derivedFrom":makeQuery(id+"F6.opPattern","COPY",BODY,{"derivedFrom":makeQuery(id+"F1.opExtrude","SWEPT_BODY",BODY,{"disambiguationData":[OSD([sQuery(id+"F0.wireOp",EDGE,"E1.0"),sQuery(id+"F0.wireOp",EDGE,"E1.1"),sQuery(id+"F0.wireOp",EDGE,"E1.2"),sQuery(id+"F0.wireOp",EDGE,"E1.3"),sQuery(id+"F0.wireOp",EDGE,"E1.4"),sQuery(id+"F0.wireOp",EDGE,"E1.5"),sQuery(id+"F0.wireOp",EDGE,"E3.0"),sQuery(id+"F0.wireOp",EDGE,"E3.1"),sQuery(id+"F0.wireOp",EDGE,"E3.2"),sQuery(id+"F0.wireOp",EDGE,"E3.3"),sQuery(id+"F0.wireOp",EDGE,"E3.4"),sQuery(id+"F0.wireOp",EDGE,"E3.5")])]}),"instanceName":"1"}),"instanceName":"1"}),"instanceName":"1"}),"instanceName":"1"});
            var Q40;
            Q40=makeQuery(id+"F12.opPattern","COPY",BODY,{"derivedFrom":makeQuery(id+"F9.opPattern","COPY",BODY,{"derivedFrom":makeQuery(id+"F7.opPattern","COPY",BODY,{"derivedFrom":makeQuery(id+"F6.opPattern","COPY",BODY,{"derivedFrom":makeQuery(id+"F4.opPattern","COPY",BODY,{"derivedFrom":makeQuery(id+"F3.opPattern","COPY",BODY,{"derivedFrom":makeQuery(id+"F1.opExtrude","SWEPT_BODY",BODY,{"disambiguationData":[OSD([sQuery(id+"F0.wireOp",EDGE,"E1.0"),sQuery(id+"F0.wireOp",EDGE,"E1.1"),sQuery(id+"F0.wireOp",EDGE,"E1.2"),sQuery(id+"F0.wireOp",EDGE,"E1.3"),sQuery(id+"F0.wireOp",EDGE,"E1.4"),sQuery(id+"F0.wireOp",EDGE,"E1.5"),sQuery(id+"F0.wireOp",EDGE,"E3.0"),sQuery(id+"F0.wireOp",EDGE,"E3.1"),sQuery(id+"F0.wireOp",EDGE,"E3.2"),sQuery(id+"F0.wireOp",EDGE,"E3.3"),sQuery(id+"F0.wireOp",EDGE,"E3.4"),sQuery(id+"F0.wireOp",EDGE,"E3.5")])]}),"instanceName":"1"}),"instanceName":"1"}),"instanceName":"1"}),"instanceName":"1"}),"instanceName":"1"}),"instanceName":"1"});
            var Q41;
            Q41=makeQuery(id+"F12.opPattern","COPY",BODY,{"derivedFrom":makeQuery(id+"F9.opPattern","COPY",BODY,{"derivedFrom":makeQuery(id+"F7.opPattern","COPY",BODY,{"derivedFrom":makeQuery(id+"F6.opPattern","COPY",BODY,{"derivedFrom":makeQuery(id+"F5.opPattern","COPY",BODY,{"derivedFrom":makeQuery(id+"F4.opPattern","COPY",BODY,{"derivedFrom":makeQuery(id+"F3.opPattern","COPY",BODY,{"derivedFrom":makeQuery(id+"F1.opExtrude","SWEPT_BODY",BODY,{"disambiguationData":[OSD([sQuery(id+"F0.wireOp",EDGE,"E1.0"),sQuery(id+"F0.wireOp",EDGE,"E1.1"),sQuery(id+"F0.wireOp",EDGE,"E1.2"),sQuery(id+"F0.wireOp",EDGE,"E1.3"),sQuery(id+"F0.wireOp",EDGE,"E1.4"),sQuery(id+"F0.wireOp",EDGE,"E1.5"),sQuery(id+"F0.wireOp",EDGE,"E3.0"),sQuery(id+"F0.wireOp",EDGE,"E3.1"),sQuery(id+"F0.wireOp",EDGE,"E3.2"),sQuery(id+"F0.wireOp",EDGE,"E3.3"),sQuery(id+"F0.wireOp",EDGE,"E3.4"),sQuery(id+"F0.wireOp",EDGE,"E3.5")])]}),"instanceName":"1"}),"instanceName":"1"}),"instanceName":"1"}),"instanceName":"1"}),"instanceName":"1"}),"instanceName":"1"}),"instanceName":"1"});
            var Q42;
            Q42=makeQuery(id+"F12.opPattern","COPY",BODY,{"derivedFrom":makeQuery(id+"F4.opPattern","COPY",BODY,{"derivedFrom":makeQuery(id+"F3.opPattern","COPY",BODY,{"derivedFrom":makeQuery(id+"F1.opExtrude","SWEPT_BODY",BODY,{"disambiguationData":[OSD([sQuery(id+"F0.wireOp",EDGE,"E1.0"),sQuery(id+"F0.wireOp",EDGE,"E1.1"),sQuery(id+"F0.wireOp",EDGE,"E1.2"),sQuery(id+"F0.wireOp",EDGE,"E1.3"),sQuery(id+"F0.wireOp",EDGE,"E1.4"),sQuery(id+"F0.wireOp",EDGE,"E1.5"),sQuery(id+"F0.wireOp",EDGE,"E3.0"),sQuery(id+"F0.wireOp",EDGE,"E3.1"),sQuery(id+"F0.wireOp",EDGE,"E3.2"),sQuery(id+"F0.wireOp",EDGE,"E3.3"),sQuery(id+"F0.wireOp",EDGE,"E3.4"),sQuery(id+"F0.wireOp",EDGE,"E3.5")])]}),"instanceName":"1"}),"instanceName":"1"}),"instanceName":"1"});
            var Q43;
            Q43=makeQuery(id+"F12.opPattern","COPY",BODY,{"derivedFrom":makeQuery(id+"F7.opPattern","COPY",BODY,{"derivedFrom":makeQuery(id+"F1.opExtrude","SWEPT_BODY",BODY,{"disambiguationData":[OSD([sQuery(id+"F0.wireOp",EDGE,"E1.0"),sQuery(id+"F0.wireOp",EDGE,"E1.1"),sQuery(id+"F0.wireOp",EDGE,"E1.2"),sQuery(id+"F0.wireOp",EDGE,"E1.3"),sQuery(id+"F0.wireOp",EDGE,"E1.4"),sQuery(id+"F0.wireOp",EDGE,"E1.5"),sQuery(id+"F0.wireOp",EDGE,"E3.0"),sQuery(id+"F0.wireOp",EDGE,"E3.1"),sQuery(id+"F0.wireOp",EDGE,"E3.2"),sQuery(id+"F0.wireOp",EDGE,"E3.3"),sQuery(id+"F0.wireOp",EDGE,"E3.4"),sQuery(id+"F0.wireOp",EDGE,"E3.5")])]}),"instanceName":"1"}),"instanceName":"1"});
            var Q44;
            Q44=makeQuery(id+"F12.opPattern","COPY",BODY,{"derivedFrom":makeQuery(id+"F7.opPattern","COPY",BODY,{"derivedFrom":makeQuery(id+"F4.opPattern","COPY",BODY,{"derivedFrom":makeQuery(id+"F1.opExtrude","SWEPT_BODY",BODY,{"disambiguationData":[OSD([sQuery(id+"F0.wireOp",EDGE,"E1.0"),sQuery(id+"F0.wireOp",EDGE,"E1.1"),sQuery(id+"F0.wireOp",EDGE,"E1.2"),sQuery(id+"F0.wireOp",EDGE,"E1.3"),sQuery(id+"F0.wireOp",EDGE,"E1.4"),sQuery(id+"F0.wireOp",EDGE,"E1.5"),sQuery(id+"F0.wireOp",EDGE,"E3.0"),sQuery(id+"F0.wireOp",EDGE,"E3.1"),sQuery(id+"F0.wireOp",EDGE,"E3.2"),sQuery(id+"F0.wireOp",EDGE,"E3.3"),sQuery(id+"F0.wireOp",EDGE,"E3.4"),sQuery(id+"F0.wireOp",EDGE,"E3.5")])]}),"instanceName":"1"}),"instanceName":"1"}),"instanceName":"1"});
            var Q45;
            Q45=makeQuery(id+"F12.opPattern","COPY",BODY,{"derivedFrom":makeQuery(id+"F6.opPattern","COPY",BODY,{"derivedFrom":makeQuery(id+"F1.opExtrude","SWEPT_BODY",BODY,{"disambiguationData":[OSD([sQuery(id+"F0.wireOp",EDGE,"E1.0"),sQuery(id+"F0.wireOp",EDGE,"E1.1"),sQuery(id+"F0.wireOp",EDGE,"E1.2"),sQuery(id+"F0.wireOp",EDGE,"E1.3"),sQuery(id+"F0.wireOp",EDGE,"E1.4"),sQuery(id+"F0.wireOp",EDGE,"E1.5"),sQuery(id+"F0.wireOp",EDGE,"E3.0"),sQuery(id+"F0.wireOp",EDGE,"E3.1"),sQuery(id+"F0.wireOp",EDGE,"E3.2"),sQuery(id+"F0.wireOp",EDGE,"E3.3"),sQuery(id+"F0.wireOp",EDGE,"E3.4"),sQuery(id+"F0.wireOp",EDGE,"E3.5")])]}),"instanceName":"1"}),"instanceName":"1"});
            var Q46;
            Q46=makeQuery(id+"F12.opPattern","COPY",BODY,{"derivedFrom":makeQuery(id+"F5.opPattern","COPY",BODY,{"derivedFrom":makeQuery(id+"F4.opPattern","COPY",BODY,{"derivedFrom":makeQuery(id+"F3.opPattern","COPY",BODY,{"derivedFrom":makeQuery(id+"F1.opExtrude","SWEPT_BODY",BODY,{"disambiguationData":[OSD([sQuery(id+"F0.wireOp",EDGE,"E1.0"),sQuery(id+"F0.wireOp",EDGE,"E1.1"),sQuery(id+"F0.wireOp",EDGE,"E1.2"),sQuery(id+"F0.wireOp",EDGE,"E1.3"),sQuery(id+"F0.wireOp",EDGE,"E1.4"),sQuery(id+"F0.wireOp",EDGE,"E1.5"),sQuery(id+"F0.wireOp",EDGE,"E3.0"),sQuery(id+"F0.wireOp",EDGE,"E3.1"),sQuery(id+"F0.wireOp",EDGE,"E3.2"),sQuery(id+"F0.wireOp",EDGE,"E3.3"),sQuery(id+"F0.wireOp",EDGE,"E3.4"),sQuery(id+"F0.wireOp",EDGE,"E3.5")])]}),"instanceName":"1"}),"instanceName":"1"}),"instanceName":"1"}),"instanceName":"1"});
            var Q47;
            Q47=makeQuery(id+"F12.opPattern","COPY",BODY,{"derivedFrom":makeQuery(id+"F4.opPattern","COPY",BODY,{"derivedFrom":makeQuery(id+"F1.opExtrude","SWEPT_BODY",BODY,{"disambiguationData":[OSD([sQuery(id+"F0.wireOp",EDGE,"E1.0"),sQuery(id+"F0.wireOp",EDGE,"E1.1"),sQuery(id+"F0.wireOp",EDGE,"E1.2"),sQuery(id+"F0.wireOp",EDGE,"E1.3"),sQuery(id+"F0.wireOp",EDGE,"E1.4"),sQuery(id+"F0.wireOp",EDGE,"E1.5"),sQuery(id+"F0.wireOp",EDGE,"E3.0"),sQuery(id+"F0.wireOp",EDGE,"E3.1"),sQuery(id+"F0.wireOp",EDGE,"E3.2"),sQuery(id+"F0.wireOp",EDGE,"E3.3"),sQuery(id+"F0.wireOp",EDGE,"E3.4"),sQuery(id+"F0.wireOp",EDGE,"E3.5")])]}),"instanceName":"1"}),"instanceName":"1"});
            var Q48;
            Q48=makeQuery(id+"F12.opPattern","COPY",BODY,{"derivedFrom":makeQuery(id+"F3.opPattern","COPY",BODY,{"derivedFrom":makeQuery(id+"F1.opExtrude","SWEPT_BODY",BODY,{"disambiguationData":[OSD([sQuery(id+"F0.wireOp",EDGE,"E1.0"),sQuery(id+"F0.wireOp",EDGE,"E1.1"),sQuery(id+"F0.wireOp",EDGE,"E1.2"),sQuery(id+"F0.wireOp",EDGE,"E1.3"),sQuery(id+"F0.wireOp",EDGE,"E1.4"),sQuery(id+"F0.wireOp",EDGE,"E1.5"),sQuery(id+"F0.wireOp",EDGE,"E3.0"),sQuery(id+"F0.wireOp",EDGE,"E3.1"),sQuery(id+"F0.wireOp",EDGE,"E3.2"),sQuery(id+"F0.wireOp",EDGE,"E3.3"),sQuery(id+"F0.wireOp",EDGE,"E3.4"),sQuery(id+"F0.wireOp",EDGE,"E3.5")])]}),"instanceName":"1"}),"instanceName":"1"});
            var Q49;
            Q49=makeQuery(id+"F12.opPattern","COPY",BODY,{"derivedFrom":makeQuery(id+"F1.opExtrude","SWEPT_BODY",BODY,{"disambiguationData":[OSD([sQuery(id+"F0.wireOp",EDGE,"E1.0"),sQuery(id+"F0.wireOp",EDGE,"E1.1"),sQuery(id+"F0.wireOp",EDGE,"E1.2"),sQuery(id+"F0.wireOp",EDGE,"E1.3"),sQuery(id+"F0.wireOp",EDGE,"E1.4"),sQuery(id+"F0.wireOp",EDGE,"E1.5"),sQuery(id+"F0.wireOp",EDGE,"E3.0"),sQuery(id+"F0.wireOp",EDGE,"E3.1"),sQuery(id+"F0.wireOp",EDGE,"E3.2"),sQuery(id+"F0.wireOp",EDGE,"E3.3"),sQuery(id+"F0.wireOp",EDGE,"E3.4"),sQuery(id+"F0.wireOp",EDGE,"E3.5")])]}),"instanceName":"1"});
            var Q50;
            Q50=makeQuery(id+"F11.opPattern","COPY",BODY,{"derivedFrom":makeQuery(id+"F10.opPattern","COPY",BODY,{"derivedFrom":makeQuery(id+"F9.opPattern","COPY",BODY,{"derivedFrom":makeQuery(id+"F8.opPattern","COPY",BODY,{"derivedFrom":makeQuery(id+"F7.opPattern","COPY",BODY,{"derivedFrom":makeQuery(id+"F6.opPattern","COPY",BODY,{"derivedFrom":makeQuery(id+"F5.opPattern","COPY",BODY,{"derivedFrom":makeQuery(id+"F4.opPattern","COPY",BODY,{"derivedFrom":makeQuery(id+"F1.opExtrude","SWEPT_BODY",BODY,{"disambiguationData":[OSD([sQuery(id+"F0.wireOp",EDGE,"E1.0"),sQuery(id+"F0.wireOp",EDGE,"E1.1"),sQuery(id+"F0.wireOp",EDGE,"E1.2"),sQuery(id+"F0.wireOp",EDGE,"E1.3"),sQuery(id+"F0.wireOp",EDGE,"E1.4"),sQuery(id+"F0.wireOp",EDGE,"E1.5"),sQuery(id+"F0.wireOp",EDGE,"E3.0"),sQuery(id+"F0.wireOp",EDGE,"E3.1"),sQuery(id+"F0.wireOp",EDGE,"E3.2"),sQuery(id+"F0.wireOp",EDGE,"E3.3"),sQuery(id+"F0.wireOp",EDGE,"E3.4"),sQuery(id+"F0.wireOp",EDGE,"E3.5")])]}),"instanceName":"1"}),"instanceName":"1"}),"instanceName":"1"}),"instanceName":"1"}),"instanceName":"1"}),"instanceName":"1"}),"instanceName":"1"}),"instanceName":"1"});
            var Q51;
            Q51=makeQuery(id+"F11.opPattern","COPY",BODY,{"derivedFrom":makeQuery(id+"F9.opPattern","COPY",BODY,{"derivedFrom":makeQuery(id+"F8.opPattern","COPY",BODY,{"derivedFrom":makeQuery(id+"F7.opPattern","COPY",BODY,{"derivedFrom":makeQuery(id+"F6.opPattern","COPY",BODY,{"derivedFrom":makeQuery(id+"F5.opPattern","COPY",BODY,{"derivedFrom":makeQuery(id+"F4.opPattern","COPY",BODY,{"derivedFrom":makeQuery(id+"F1.opExtrude","SWEPT_BODY",BODY,{"disambiguationData":[OSD([sQuery(id+"F0.wireOp",EDGE,"E1.0"),sQuery(id+"F0.wireOp",EDGE,"E1.1"),sQuery(id+"F0.wireOp",EDGE,"E1.2"),sQuery(id+"F0.wireOp",EDGE,"E1.3"),sQuery(id+"F0.wireOp",EDGE,"E1.4"),sQuery(id+"F0.wireOp",EDGE,"E1.5"),sQuery(id+"F0.wireOp",EDGE,"E3.0"),sQuery(id+"F0.wireOp",EDGE,"E3.1"),sQuery(id+"F0.wireOp",EDGE,"E3.2"),sQuery(id+"F0.wireOp",EDGE,"E3.3"),sQuery(id+"F0.wireOp",EDGE,"E3.4"),sQuery(id+"F0.wireOp",EDGE,"E3.5")])]}),"instanceName":"1"}),"instanceName":"1"}),"instanceName":"1"}),"instanceName":"1"}),"instanceName":"1"}),"instanceName":"1"}),"instanceName":"1"});
            var Q52;
            Q52=makeQuery(id+"F11.opPattern","COPY",BODY,{"derivedFrom":makeQuery(id+"F9.opPattern","COPY",BODY,{"derivedFrom":makeQuery(id+"F8.opPattern","COPY",BODY,{"derivedFrom":makeQuery(id+"F7.opPattern","COPY",BODY,{"derivedFrom":makeQuery(id+"F6.opPattern","COPY",BODY,{"derivedFrom":makeQuery(id+"F4.opPattern","COPY",BODY,{"derivedFrom":makeQuery(id+"F3.opPattern","COPY",BODY,{"derivedFrom":makeQuery(id+"F1.opExtrude","SWEPT_BODY",BODY,{"disambiguationData":[OSD([sQuery(id+"F0.wireOp",EDGE,"E1.0"),sQuery(id+"F0.wireOp",EDGE,"E1.1"),sQuery(id+"F0.wireOp",EDGE,"E1.2"),sQuery(id+"F0.wireOp",EDGE,"E1.3"),sQuery(id+"F0.wireOp",EDGE,"E1.4"),sQuery(id+"F0.wireOp",EDGE,"E1.5"),sQuery(id+"F0.wireOp",EDGE,"E3.0"),sQuery(id+"F0.wireOp",EDGE,"E3.1"),sQuery(id+"F0.wireOp",EDGE,"E3.2"),sQuery(id+"F0.wireOp",EDGE,"E3.3"),sQuery(id+"F0.wireOp",EDGE,"E3.4"),sQuery(id+"F0.wireOp",EDGE,"E3.5")])]}),"instanceName":"1"}),"instanceName":"1"}),"instanceName":"1"}),"instanceName":"1"}),"instanceName":"1"}),"instanceName":"1"}),"instanceName":"1"});
            var Q53;
            Q53=makeQuery(id+"F11.opPattern","COPY",BODY,{"derivedFrom":makeQuery(id+"F9.opPattern","COPY",BODY,{"derivedFrom":makeQuery(id+"F8.opPattern","COPY",BODY,{"derivedFrom":makeQuery(id+"F7.opPattern","COPY",BODY,{"derivedFrom":makeQuery(id+"F6.opPattern","COPY",BODY,{"derivedFrom":makeQuery(id+"F4.opPattern","COPY",BODY,{"derivedFrom":makeQuery(id+"F1.opExtrude","SWEPT_BODY",BODY,{"disambiguationData":[OSD([sQuery(id+"F0.wireOp",EDGE,"E1.0"),sQuery(id+"F0.wireOp",EDGE,"E1.1"),sQuery(id+"F0.wireOp",EDGE,"E1.2"),sQuery(id+"F0.wireOp",EDGE,"E1.3"),sQuery(id+"F0.wireOp",EDGE,"E1.4"),sQuery(id+"F0.wireOp",EDGE,"E1.5"),sQuery(id+"F0.wireOp",EDGE,"E3.0"),sQuery(id+"F0.wireOp",EDGE,"E3.1"),sQuery(id+"F0.wireOp",EDGE,"E3.2"),sQuery(id+"F0.wireOp",EDGE,"E3.3"),sQuery(id+"F0.wireOp",EDGE,"E3.4"),sQuery(id+"F0.wireOp",EDGE,"E3.5")])]}),"instanceName":"1"}),"instanceName":"1"}),"instanceName":"1"}),"instanceName":"1"}),"instanceName":"1"}),"instanceName":"1"});
            var Q54;
            Q54=makeQuery(id+"F11.opPattern","COPY",BODY,{"derivedFrom":makeQuery(id+"F9.opPattern","COPY",BODY,{"derivedFrom":makeQuery(id+"F8.opPattern","COPY",BODY,{"derivedFrom":makeQuery(id+"F7.opPattern","COPY",BODY,{"derivedFrom":makeQuery(id+"F6.opPattern","COPY",BODY,{"derivedFrom":makeQuery(id+"F3.opPattern","COPY",BODY,{"derivedFrom":makeQuery(id+"F1.opExtrude","SWEPT_BODY",BODY,{"disambiguationData":[OSD([sQuery(id+"F0.wireOp",EDGE,"E1.0"),sQuery(id+"F0.wireOp",EDGE,"E1.1"),sQuery(id+"F0.wireOp",EDGE,"E1.2"),sQuery(id+"F0.wireOp",EDGE,"E1.3"),sQuery(id+"F0.wireOp",EDGE,"E1.4"),sQuery(id+"F0.wireOp",EDGE,"E1.5"),sQuery(id+"F0.wireOp",EDGE,"E3.0"),sQuery(id+"F0.wireOp",EDGE,"E3.1"),sQuery(id+"F0.wireOp",EDGE,"E3.2"),sQuery(id+"F0.wireOp",EDGE,"E3.3"),sQuery(id+"F0.wireOp",EDGE,"E3.4"),sQuery(id+"F0.wireOp",EDGE,"E3.5")])]}),"instanceName":"1"}),"instanceName":"1"}),"instanceName":"1"}),"instanceName":"1"}),"instanceName":"1"}),"instanceName":"1"});
            var Q55;
            Q55=makeQuery(id+"F11.opPattern","COPY",BODY,{"derivedFrom":makeQuery(id+"F9.opPattern","COPY",BODY,{"derivedFrom":makeQuery(id+"F8.opPattern","COPY",BODY,{"derivedFrom":makeQuery(id+"F7.opPattern","COPY",BODY,{"derivedFrom":makeQuery(id+"F6.opPattern","COPY",BODY,{"derivedFrom":makeQuery(id+"F1.opExtrude","SWEPT_BODY",BODY,{"disambiguationData":[OSD([sQuery(id+"F0.wireOp",EDGE,"E1.0"),sQuery(id+"F0.wireOp",EDGE,"E1.1"),sQuery(id+"F0.wireOp",EDGE,"E1.2"),sQuery(id+"F0.wireOp",EDGE,"E1.3"),sQuery(id+"F0.wireOp",EDGE,"E1.4"),sQuery(id+"F0.wireOp",EDGE,"E1.5"),sQuery(id+"F0.wireOp",EDGE,"E3.0"),sQuery(id+"F0.wireOp",EDGE,"E3.1"),sQuery(id+"F0.wireOp",EDGE,"E3.2"),sQuery(id+"F0.wireOp",EDGE,"E3.3"),sQuery(id+"F0.wireOp",EDGE,"E3.4"),sQuery(id+"F0.wireOp",EDGE,"E3.5")])]}),"instanceName":"1"}),"instanceName":"1"}),"instanceName":"1"}),"instanceName":"1"}),"instanceName":"1"});
            var Q56;
            Q56=makeQuery(id+"F11.opPattern","COPY",BODY,{"derivedFrom":makeQuery(id+"F9.opPattern","COPY",BODY,{"derivedFrom":makeQuery(id+"F8.opPattern","COPY",BODY,{"derivedFrom":makeQuery(id+"F7.opPattern","COPY",BODY,{"derivedFrom":makeQuery(id+"F5.opPattern","COPY",BODY,{"derivedFrom":makeQuery(id+"F4.opPattern","COPY",BODY,{"derivedFrom":makeQuery(id+"F3.opPattern","COPY",BODY,{"derivedFrom":makeQuery(id+"F1.opExtrude","SWEPT_BODY",BODY,{"disambiguationData":[OSD([sQuery(id+"F0.wireOp",EDGE,"E1.0"),sQuery(id+"F0.wireOp",EDGE,"E1.1"),sQuery(id+"F0.wireOp",EDGE,"E1.2"),sQuery(id+"F0.wireOp",EDGE,"E1.3"),sQuery(id+"F0.wireOp",EDGE,"E1.4"),sQuery(id+"F0.wireOp",EDGE,"E1.5"),sQuery(id+"F0.wireOp",EDGE,"E3.0"),sQuery(id+"F0.wireOp",EDGE,"E3.1"),sQuery(id+"F0.wireOp",EDGE,"E3.2"),sQuery(id+"F0.wireOp",EDGE,"E3.3"),sQuery(id+"F0.wireOp",EDGE,"E3.4"),sQuery(id+"F0.wireOp",EDGE,"E3.5")])]}),"instanceName":"1"}),"instanceName":"1"}),"instanceName":"1"}),"instanceName":"1"}),"instanceName":"1"}),"instanceName":"1"}),"instanceName":"1"});
            var Q57;
            Q57=makeQuery(id+"F11.opPattern","COPY",BODY,{"derivedFrom":makeQuery(id+"F9.opPattern","COPY",BODY,{"derivedFrom":makeQuery(id+"F8.opPattern","COPY",BODY,{"derivedFrom":makeQuery(id+"F7.opPattern","COPY",BODY,{"derivedFrom":makeQuery(id+"F5.opPattern","COPY",BODY,{"derivedFrom":makeQuery(id+"F4.opPattern","COPY",BODY,{"derivedFrom":makeQuery(id+"F1.opExtrude","SWEPT_BODY",BODY,{"disambiguationData":[OSD([sQuery(id+"F0.wireOp",EDGE,"E1.0"),sQuery(id+"F0.wireOp",EDGE,"E1.1"),sQuery(id+"F0.wireOp",EDGE,"E1.2"),sQuery(id+"F0.wireOp",EDGE,"E1.3"),sQuery(id+"F0.wireOp",EDGE,"E1.4"),sQuery(id+"F0.wireOp",EDGE,"E1.5"),sQuery(id+"F0.wireOp",EDGE,"E3.0"),sQuery(id+"F0.wireOp",EDGE,"E3.1"),sQuery(id+"F0.wireOp",EDGE,"E3.2"),sQuery(id+"F0.wireOp",EDGE,"E3.3"),sQuery(id+"F0.wireOp",EDGE,"E3.4"),sQuery(id+"F0.wireOp",EDGE,"E3.5")])]}),"instanceName":"1"}),"instanceName":"1"}),"instanceName":"1"}),"instanceName":"1"}),"instanceName":"1"}),"instanceName":"1"});
            var Q58;
            Q58=makeQuery(id+"F11.opPattern","COPY",BODY,{"derivedFrom":makeQuery(id+"F9.opPattern","COPY",BODY,{"derivedFrom":makeQuery(id+"F8.opPattern","COPY",BODY,{"derivedFrom":makeQuery(id+"F7.opPattern","COPY",BODY,{"derivedFrom":makeQuery(id+"F4.opPattern","COPY",BODY,{"derivedFrom":makeQuery(id+"F3.opPattern","COPY",BODY,{"derivedFrom":makeQuery(id+"F1.opExtrude","SWEPT_BODY",BODY,{"disambiguationData":[OSD([sQuery(id+"F0.wireOp",EDGE,"E1.0"),sQuery(id+"F0.wireOp",EDGE,"E1.1"),sQuery(id+"F0.wireOp",EDGE,"E1.2"),sQuery(id+"F0.wireOp",EDGE,"E1.3"),sQuery(id+"F0.wireOp",EDGE,"E1.4"),sQuery(id+"F0.wireOp",EDGE,"E1.5"),sQuery(id+"F0.wireOp",EDGE,"E3.0"),sQuery(id+"F0.wireOp",EDGE,"E3.1"),sQuery(id+"F0.wireOp",EDGE,"E3.2"),sQuery(id+"F0.wireOp",EDGE,"E3.3"),sQuery(id+"F0.wireOp",EDGE,"E3.4"),sQuery(id+"F0.wireOp",EDGE,"E3.5")])]}),"instanceName":"1"}),"instanceName":"1"}),"instanceName":"1"}),"instanceName":"1"}),"instanceName":"1"}),"instanceName":"1"});
            var Q59;
            Q59=makeQuery(id+"F11.opPattern","COPY",BODY,{"derivedFrom":makeQuery(id+"F9.opPattern","COPY",BODY,{"derivedFrom":makeQuery(id+"F8.opPattern","COPY",BODY,{"derivedFrom":makeQuery(id+"F7.opPattern","COPY",BODY,{"derivedFrom":makeQuery(id+"F4.opPattern","COPY",BODY,{"derivedFrom":makeQuery(id+"F1.opExtrude","SWEPT_BODY",BODY,{"disambiguationData":[OSD([sQuery(id+"F0.wireOp",EDGE,"E1.0"),sQuery(id+"F0.wireOp",EDGE,"E1.1"),sQuery(id+"F0.wireOp",EDGE,"E1.2"),sQuery(id+"F0.wireOp",EDGE,"E1.3"),sQuery(id+"F0.wireOp",EDGE,"E1.4"),sQuery(id+"F0.wireOp",EDGE,"E1.5"),sQuery(id+"F0.wireOp",EDGE,"E3.0"),sQuery(id+"F0.wireOp",EDGE,"E3.1"),sQuery(id+"F0.wireOp",EDGE,"E3.2"),sQuery(id+"F0.wireOp",EDGE,"E3.3"),sQuery(id+"F0.wireOp",EDGE,"E3.4"),sQuery(id+"F0.wireOp",EDGE,"E3.5")])]}),"instanceName":"1"}),"instanceName":"1"}),"instanceName":"1"}),"instanceName":"1"}),"instanceName":"1"});
            var Q60;
            Q60=makeQuery(id+"F11.opPattern","COPY",BODY,{"derivedFrom":makeQuery(id+"F9.opPattern","COPY",BODY,{"derivedFrom":makeQuery(id+"F8.opPattern","COPY",BODY,{"derivedFrom":makeQuery(id+"F7.opPattern","COPY",BODY,{"derivedFrom":makeQuery(id+"F3.opPattern","COPY",BODY,{"derivedFrom":makeQuery(id+"F1.opExtrude","SWEPT_BODY",BODY,{"disambiguationData":[OSD([sQuery(id+"F0.wireOp",EDGE,"E1.0"),sQuery(id+"F0.wireOp",EDGE,"E1.1"),sQuery(id+"F0.wireOp",EDGE,"E1.2"),sQuery(id+"F0.wireOp",EDGE,"E1.3"),sQuery(id+"F0.wireOp",EDGE,"E1.4"),sQuery(id+"F0.wireOp",EDGE,"E1.5"),sQuery(id+"F0.wireOp",EDGE,"E3.0"),sQuery(id+"F0.wireOp",EDGE,"E3.1"),sQuery(id+"F0.wireOp",EDGE,"E3.2"),sQuery(id+"F0.wireOp",EDGE,"E3.3"),sQuery(id+"F0.wireOp",EDGE,"E3.4"),sQuery(id+"F0.wireOp",EDGE,"E3.5")])]}),"instanceName":"1"}),"instanceName":"1"}),"instanceName":"1"}),"instanceName":"1"}),"instanceName":"1"});
            var Q61;
            Q61=makeQuery(id+"F11.opPattern","COPY",BODY,{"derivedFrom":makeQuery(id+"F9.opPattern","COPY",BODY,{"derivedFrom":makeQuery(id+"F8.opPattern","COPY",BODY,{"derivedFrom":makeQuery(id+"F7.opPattern","COPY",BODY,{"derivedFrom":makeQuery(id+"F1.opExtrude","SWEPT_BODY",BODY,{"disambiguationData":[OSD([sQuery(id+"F0.wireOp",EDGE,"E1.0"),sQuery(id+"F0.wireOp",EDGE,"E1.1"),sQuery(id+"F0.wireOp",EDGE,"E1.2"),sQuery(id+"F0.wireOp",EDGE,"E1.3"),sQuery(id+"F0.wireOp",EDGE,"E1.4"),sQuery(id+"F0.wireOp",EDGE,"E1.5"),sQuery(id+"F0.wireOp",EDGE,"E3.0"),sQuery(id+"F0.wireOp",EDGE,"E3.1"),sQuery(id+"F0.wireOp",EDGE,"E3.2"),sQuery(id+"F0.wireOp",EDGE,"E3.3"),sQuery(id+"F0.wireOp",EDGE,"E3.4"),sQuery(id+"F0.wireOp",EDGE,"E3.5")])]}),"instanceName":"1"}),"instanceName":"1"}),"instanceName":"1"}),"instanceName":"1"});
            var Q62;
            Q62=makeQuery(id+"F11.opPattern","COPY",BODY,{"derivedFrom":makeQuery(id+"F9.opPattern","COPY",BODY,{"derivedFrom":makeQuery(id+"F8.opPattern","COPY",BODY,{"derivedFrom":makeQuery(id+"F6.opPattern","COPY",BODY,{"derivedFrom":makeQuery(id+"F5.opPattern","COPY",BODY,{"derivedFrom":makeQuery(id+"F4.opPattern","COPY",BODY,{"derivedFrom":makeQuery(id+"F3.opPattern","COPY",BODY,{"derivedFrom":makeQuery(id+"F1.opExtrude","SWEPT_BODY",BODY,{"disambiguationData":[OSD([sQuery(id+"F0.wireOp",EDGE,"E1.0"),sQuery(id+"F0.wireOp",EDGE,"E1.1"),sQuery(id+"F0.wireOp",EDGE,"E1.2"),sQuery(id+"F0.wireOp",EDGE,"E1.3"),sQuery(id+"F0.wireOp",EDGE,"E1.4"),sQuery(id+"F0.wireOp",EDGE,"E1.5"),sQuery(id+"F0.wireOp",EDGE,"E3.0"),sQuery(id+"F0.wireOp",EDGE,"E3.1"),sQuery(id+"F0.wireOp",EDGE,"E3.2"),sQuery(id+"F0.wireOp",EDGE,"E3.3"),sQuery(id+"F0.wireOp",EDGE,"E3.4"),sQuery(id+"F0.wireOp",EDGE,"E3.5")])]}),"instanceName":"1"}),"instanceName":"1"}),"instanceName":"1"}),"instanceName":"1"}),"instanceName":"1"}),"instanceName":"1"}),"instanceName":"1"});
            var Q63;
            Q63=makeQuery(id+"F11.opPattern","COPY",BODY,{"derivedFrom":makeQuery(id+"F9.opPattern","COPY",BODY,{"derivedFrom":makeQuery(id+"F8.opPattern","COPY",BODY,{"derivedFrom":makeQuery(id+"F6.opPattern","COPY",BODY,{"derivedFrom":makeQuery(id+"F5.opPattern","COPY",BODY,{"derivedFrom":makeQuery(id+"F4.opPattern","COPY",BODY,{"derivedFrom":makeQuery(id+"F1.opExtrude","SWEPT_BODY",BODY,{"disambiguationData":[OSD([sQuery(id+"F0.wireOp",EDGE,"E1.0"),sQuery(id+"F0.wireOp",EDGE,"E1.1"),sQuery(id+"F0.wireOp",EDGE,"E1.2"),sQuery(id+"F0.wireOp",EDGE,"E1.3"),sQuery(id+"F0.wireOp",EDGE,"E1.4"),sQuery(id+"F0.wireOp",EDGE,"E1.5"),sQuery(id+"F0.wireOp",EDGE,"E3.0"),sQuery(id+"F0.wireOp",EDGE,"E3.1"),sQuery(id+"F0.wireOp",EDGE,"E3.2"),sQuery(id+"F0.wireOp",EDGE,"E3.3"),sQuery(id+"F0.wireOp",EDGE,"E3.4"),sQuery(id+"F0.wireOp",EDGE,"E3.5")])]}),"instanceName":"1"}),"instanceName":"1"}),"instanceName":"1"}),"instanceName":"1"}),"instanceName":"1"}),"instanceName":"1"});
            var Q64;
            Q64=makeQuery(id+"F11.opPattern","COPY",BODY,{"derivedFrom":makeQuery(id+"F9.opPattern","COPY",BODY,{"derivedFrom":makeQuery(id+"F8.opPattern","COPY",BODY,{"derivedFrom":makeQuery(id+"F6.opPattern","COPY",BODY,{"derivedFrom":makeQuery(id+"F4.opPattern","COPY",BODY,{"derivedFrom":makeQuery(id+"F3.opPattern","COPY",BODY,{"derivedFrom":makeQuery(id+"F1.opExtrude","SWEPT_BODY",BODY,{"disambiguationData":[OSD([sQuery(id+"F0.wireOp",EDGE,"E1.0"),sQuery(id+"F0.wireOp",EDGE,"E1.1"),sQuery(id+"F0.wireOp",EDGE,"E1.2"),sQuery(id+"F0.wireOp",EDGE,"E1.3"),sQuery(id+"F0.wireOp",EDGE,"E1.4"),sQuery(id+"F0.wireOp",EDGE,"E1.5"),sQuery(id+"F0.wireOp",EDGE,"E3.0"),sQuery(id+"F0.wireOp",EDGE,"E3.1"),sQuery(id+"F0.wireOp",EDGE,"E3.2"),sQuery(id+"F0.wireOp",EDGE,"E3.3"),sQuery(id+"F0.wireOp",EDGE,"E3.4"),sQuery(id+"F0.wireOp",EDGE,"E3.5")])]}),"instanceName":"1"}),"instanceName":"1"}),"instanceName":"1"}),"instanceName":"1"}),"instanceName":"1"}),"instanceName":"1"});
            var Q65;
            Q65=makeQuery(id+"F11.opPattern","COPY",BODY,{"derivedFrom":makeQuery(id+"F9.opPattern","COPY",BODY,{"derivedFrom":makeQuery(id+"F8.opPattern","COPY",BODY,{"derivedFrom":makeQuery(id+"F6.opPattern","COPY",BODY,{"derivedFrom":makeQuery(id+"F4.opPattern","COPY",BODY,{"derivedFrom":makeQuery(id+"F1.opExtrude","SWEPT_BODY",BODY,{"disambiguationData":[OSD([sQuery(id+"F0.wireOp",EDGE,"E1.0"),sQuery(id+"F0.wireOp",EDGE,"E1.1"),sQuery(id+"F0.wireOp",EDGE,"E1.2"),sQuery(id+"F0.wireOp",EDGE,"E1.3"),sQuery(id+"F0.wireOp",EDGE,"E1.4"),sQuery(id+"F0.wireOp",EDGE,"E1.5"),sQuery(id+"F0.wireOp",EDGE,"E3.0"),sQuery(id+"F0.wireOp",EDGE,"E3.1"),sQuery(id+"F0.wireOp",EDGE,"E3.2"),sQuery(id+"F0.wireOp",EDGE,"E3.3"),sQuery(id+"F0.wireOp",EDGE,"E3.4"),sQuery(id+"F0.wireOp",EDGE,"E3.5")])]}),"instanceName":"1"}),"instanceName":"1"}),"instanceName":"1"}),"instanceName":"1"}),"instanceName":"1"});
            var Q66;
            Q66=makeQuery(id+"F11.opPattern","COPY",BODY,{"derivedFrom":makeQuery(id+"F9.opPattern","COPY",BODY,{"derivedFrom":makeQuery(id+"F8.opPattern","COPY",BODY,{"derivedFrom":makeQuery(id+"F6.opPattern","COPY",BODY,{"derivedFrom":makeQuery(id+"F3.opPattern","COPY",BODY,{"derivedFrom":makeQuery(id+"F1.opExtrude","SWEPT_BODY",BODY,{"disambiguationData":[OSD([sQuery(id+"F0.wireOp",EDGE,"E1.0"),sQuery(id+"F0.wireOp",EDGE,"E1.1"),sQuery(id+"F0.wireOp",EDGE,"E1.2"),sQuery(id+"F0.wireOp",EDGE,"E1.3"),sQuery(id+"F0.wireOp",EDGE,"E1.4"),sQuery(id+"F0.wireOp",EDGE,"E1.5"),sQuery(id+"F0.wireOp",EDGE,"E3.0"),sQuery(id+"F0.wireOp",EDGE,"E3.1"),sQuery(id+"F0.wireOp",EDGE,"E3.2"),sQuery(id+"F0.wireOp",EDGE,"E3.3"),sQuery(id+"F0.wireOp",EDGE,"E3.4"),sQuery(id+"F0.wireOp",EDGE,"E3.5")])]}),"instanceName":"1"}),"instanceName":"1"}),"instanceName":"1"}),"instanceName":"1"}),"instanceName":"1"});
            var Q67;
            Q67=makeQuery(id+"F11.opPattern","COPY",BODY,{"derivedFrom":makeQuery(id+"F9.opPattern","COPY",BODY,{"derivedFrom":makeQuery(id+"F8.opPattern","COPY",BODY,{"derivedFrom":makeQuery(id+"F6.opPattern","COPY",BODY,{"derivedFrom":makeQuery(id+"F1.opExtrude","SWEPT_BODY",BODY,{"disambiguationData":[OSD([sQuery(id+"F0.wireOp",EDGE,"E1.0"),sQuery(id+"F0.wireOp",EDGE,"E1.1"),sQuery(id+"F0.wireOp",EDGE,"E1.2"),sQuery(id+"F0.wireOp",EDGE,"E1.3"),sQuery(id+"F0.wireOp",EDGE,"E1.4"),sQuery(id+"F0.wireOp",EDGE,"E1.5"),sQuery(id+"F0.wireOp",EDGE,"E3.0"),sQuery(id+"F0.wireOp",EDGE,"E3.1"),sQuery(id+"F0.wireOp",EDGE,"E3.2"),sQuery(id+"F0.wireOp",EDGE,"E3.3"),sQuery(id+"F0.wireOp",EDGE,"E3.4"),sQuery(id+"F0.wireOp",EDGE,"E3.5")])]}),"instanceName":"1"}),"instanceName":"1"}),"instanceName":"1"}),"instanceName":"1"});
            var Q68;
            Q68=makeQuery(id+"F11.opPattern","COPY",BODY,{"derivedFrom":makeQuery(id+"F9.opPattern","COPY",BODY,{"derivedFrom":makeQuery(id+"F8.opPattern","COPY",BODY,{"derivedFrom":makeQuery(id+"F5.opPattern","COPY",BODY,{"derivedFrom":makeQuery(id+"F4.opPattern","COPY",BODY,{"derivedFrom":makeQuery(id+"F3.opPattern","COPY",BODY,{"derivedFrom":makeQuery(id+"F1.opExtrude","SWEPT_BODY",BODY,{"disambiguationData":[OSD([sQuery(id+"F0.wireOp",EDGE,"E1.0"),sQuery(id+"F0.wireOp",EDGE,"E1.1"),sQuery(id+"F0.wireOp",EDGE,"E1.2"),sQuery(id+"F0.wireOp",EDGE,"E1.3"),sQuery(id+"F0.wireOp",EDGE,"E1.4"),sQuery(id+"F0.wireOp",EDGE,"E1.5"),sQuery(id+"F0.wireOp",EDGE,"E3.0"),sQuery(id+"F0.wireOp",EDGE,"E3.1"),sQuery(id+"F0.wireOp",EDGE,"E3.2"),sQuery(id+"F0.wireOp",EDGE,"E3.3"),sQuery(id+"F0.wireOp",EDGE,"E3.4"),sQuery(id+"F0.wireOp",EDGE,"E3.5")])]}),"instanceName":"1"}),"instanceName":"1"}),"instanceName":"1"}),"instanceName":"1"}),"instanceName":"1"}),"instanceName":"1"});
            var Q69;
            Q69=makeQuery(id+"F11.opPattern","COPY",BODY,{"derivedFrom":makeQuery(id+"F9.opPattern","COPY",BODY,{"derivedFrom":makeQuery(id+"F8.opPattern","COPY",BODY,{"derivedFrom":makeQuery(id+"F5.opPattern","COPY",BODY,{"derivedFrom":makeQuery(id+"F4.opPattern","COPY",BODY,{"derivedFrom":makeQuery(id+"F1.opExtrude","SWEPT_BODY",BODY,{"disambiguationData":[OSD([sQuery(id+"F0.wireOp",EDGE,"E1.0"),sQuery(id+"F0.wireOp",EDGE,"E1.1"),sQuery(id+"F0.wireOp",EDGE,"E1.2"),sQuery(id+"F0.wireOp",EDGE,"E1.3"),sQuery(id+"F0.wireOp",EDGE,"E1.4"),sQuery(id+"F0.wireOp",EDGE,"E1.5"),sQuery(id+"F0.wireOp",EDGE,"E3.0"),sQuery(id+"F0.wireOp",EDGE,"E3.1"),sQuery(id+"F0.wireOp",EDGE,"E3.2"),sQuery(id+"F0.wireOp",EDGE,"E3.3"),sQuery(id+"F0.wireOp",EDGE,"E3.4"),sQuery(id+"F0.wireOp",EDGE,"E3.5")])]}),"instanceName":"1"}),"instanceName":"1"}),"instanceName":"1"}),"instanceName":"1"}),"instanceName":"1"});
            var Q70;
            Q70=makeQuery(id+"F11.opPattern","COPY",BODY,{"derivedFrom":makeQuery(id+"F9.opPattern","COPY",BODY,{"derivedFrom":makeQuery(id+"F8.opPattern","COPY",BODY,{"derivedFrom":makeQuery(id+"F4.opPattern","COPY",BODY,{"derivedFrom":makeQuery(id+"F3.opPattern","COPY",BODY,{"derivedFrom":makeQuery(id+"F1.opExtrude","SWEPT_BODY",BODY,{"disambiguationData":[OSD([sQuery(id+"F0.wireOp",EDGE,"E1.0"),sQuery(id+"F0.wireOp",EDGE,"E1.1"),sQuery(id+"F0.wireOp",EDGE,"E1.2"),sQuery(id+"F0.wireOp",EDGE,"E1.3"),sQuery(id+"F0.wireOp",EDGE,"E1.4"),sQuery(id+"F0.wireOp",EDGE,"E1.5"),sQuery(id+"F0.wireOp",EDGE,"E3.0"),sQuery(id+"F0.wireOp",EDGE,"E3.1"),sQuery(id+"F0.wireOp",EDGE,"E3.2"),sQuery(id+"F0.wireOp",EDGE,"E3.3"),sQuery(id+"F0.wireOp",EDGE,"E3.4"),sQuery(id+"F0.wireOp",EDGE,"E3.5")])]}),"instanceName":"1"}),"instanceName":"1"}),"instanceName":"1"}),"instanceName":"1"}),"instanceName":"1"});
            var Q71;
            Q71=makeQuery(id+"F11.opPattern","COPY",BODY,{"derivedFrom":makeQuery(id+"F9.opPattern","COPY",BODY,{"derivedFrom":makeQuery(id+"F8.opPattern","COPY",BODY,{"derivedFrom":makeQuery(id+"F4.opPattern","COPY",BODY,{"derivedFrom":makeQuery(id+"F1.opExtrude","SWEPT_BODY",BODY,{"disambiguationData":[OSD([sQuery(id+"F0.wireOp",EDGE,"E1.0"),sQuery(id+"F0.wireOp",EDGE,"E1.1"),sQuery(id+"F0.wireOp",EDGE,"E1.2"),sQuery(id+"F0.wireOp",EDGE,"E1.3"),sQuery(id+"F0.wireOp",EDGE,"E1.4"),sQuery(id+"F0.wireOp",EDGE,"E1.5"),sQuery(id+"F0.wireOp",EDGE,"E3.0"),sQuery(id+"F0.wireOp",EDGE,"E3.1"),sQuery(id+"F0.wireOp",EDGE,"E3.2"),sQuery(id+"F0.wireOp",EDGE,"E3.3"),sQuery(id+"F0.wireOp",EDGE,"E3.4"),sQuery(id+"F0.wireOp",EDGE,"E3.5")])]}),"instanceName":"1"}),"instanceName":"1"}),"instanceName":"1"}),"instanceName":"1"});
            var Q72;
            Q72=makeQuery(id+"F11.opPattern","COPY",BODY,{"derivedFrom":makeQuery(id+"F9.opPattern","COPY",BODY,{"derivedFrom":makeQuery(id+"F8.opPattern","COPY",BODY,{"derivedFrom":makeQuery(id+"F3.opPattern","COPY",BODY,{"derivedFrom":makeQuery(id+"F1.opExtrude","SWEPT_BODY",BODY,{"disambiguationData":[OSD([sQuery(id+"F0.wireOp",EDGE,"E1.0"),sQuery(id+"F0.wireOp",EDGE,"E1.1"),sQuery(id+"F0.wireOp",EDGE,"E1.2"),sQuery(id+"F0.wireOp",EDGE,"E1.3"),sQuery(id+"F0.wireOp",EDGE,"E1.4"),sQuery(id+"F0.wireOp",EDGE,"E1.5"),sQuery(id+"F0.wireOp",EDGE,"E3.0"),sQuery(id+"F0.wireOp",EDGE,"E3.1"),sQuery(id+"F0.wireOp",EDGE,"E3.2"),sQuery(id+"F0.wireOp",EDGE,"E3.3"),sQuery(id+"F0.wireOp",EDGE,"E3.4"),sQuery(id+"F0.wireOp",EDGE,"E3.5")])]}),"instanceName":"1"}),"instanceName":"1"}),"instanceName":"1"}),"instanceName":"1"});
            var Q73;
            Q73=makeQuery(id+"F11.opPattern","COPY",BODY,{"derivedFrom":makeQuery(id+"F9.opPattern","COPY",BODY,{"derivedFrom":makeQuery(id+"F8.opPattern","COPY",BODY,{"derivedFrom":makeQuery(id+"F1.opExtrude","SWEPT_BODY",BODY,{"disambiguationData":[OSD([sQuery(id+"F0.wireOp",EDGE,"E1.0"),sQuery(id+"F0.wireOp",EDGE,"E1.1"),sQuery(id+"F0.wireOp",EDGE,"E1.2"),sQuery(id+"F0.wireOp",EDGE,"E1.3"),sQuery(id+"F0.wireOp",EDGE,"E1.4"),sQuery(id+"F0.wireOp",EDGE,"E1.5"),sQuery(id+"F0.wireOp",EDGE,"E3.0"),sQuery(id+"F0.wireOp",EDGE,"E3.1"),sQuery(id+"F0.wireOp",EDGE,"E3.2"),sQuery(id+"F0.wireOp",EDGE,"E3.3"),sQuery(id+"F0.wireOp",EDGE,"E3.4"),sQuery(id+"F0.wireOp",EDGE,"E3.5")])]}),"instanceName":"1"}),"instanceName":"1"}),"instanceName":"1"});
            var Q74;
            Q74=makeQuery(id+"F11.opPattern","COPY",BODY,{"derivedFrom":makeQuery(id+"F8.opPattern","COPY",BODY,{"derivedFrom":makeQuery(id+"F7.opPattern","COPY",BODY,{"derivedFrom":makeQuery(id+"F6.opPattern","COPY",BODY,{"derivedFrom":makeQuery(id+"F5.opPattern","COPY",BODY,{"derivedFrom":makeQuery(id+"F4.opPattern","COPY",BODY,{"derivedFrom":makeQuery(id+"F1.opExtrude","SWEPT_BODY",BODY,{"disambiguationData":[OSD([sQuery(id+"F0.wireOp",EDGE,"E1.0"),sQuery(id+"F0.wireOp",EDGE,"E1.1"),sQuery(id+"F0.wireOp",EDGE,"E1.2"),sQuery(id+"F0.wireOp",EDGE,"E1.3"),sQuery(id+"F0.wireOp",EDGE,"E1.4"),sQuery(id+"F0.wireOp",EDGE,"E1.5"),sQuery(id+"F0.wireOp",EDGE,"E3.0"),sQuery(id+"F0.wireOp",EDGE,"E3.1"),sQuery(id+"F0.wireOp",EDGE,"E3.2"),sQuery(id+"F0.wireOp",EDGE,"E3.3"),sQuery(id+"F0.wireOp",EDGE,"E3.4"),sQuery(id+"F0.wireOp",EDGE,"E3.5")])]}),"instanceName":"1"}),"instanceName":"1"}),"instanceName":"1"}),"instanceName":"1"}),"instanceName":"1"}),"instanceName":"1"});
            var Q75;
            Q75=makeQuery(id+"F11.opPattern","COPY",BODY,{"derivedFrom":makeQuery(id+"F8.opPattern","COPY",BODY,{"derivedFrom":makeQuery(id+"F7.opPattern","COPY",BODY,{"derivedFrom":makeQuery(id+"F6.opPattern","COPY",BODY,{"derivedFrom":makeQuery(id+"F4.opPattern","COPY",BODY,{"derivedFrom":makeQuery(id+"F3.opPattern","COPY",BODY,{"derivedFrom":makeQuery(id+"F1.opExtrude","SWEPT_BODY",BODY,{"disambiguationData":[OSD([sQuery(id+"F0.wireOp",EDGE,"E1.0"),sQuery(id+"F0.wireOp",EDGE,"E1.1"),sQuery(id+"F0.wireOp",EDGE,"E1.2"),sQuery(id+"F0.wireOp",EDGE,"E1.3"),sQuery(id+"F0.wireOp",EDGE,"E1.4"),sQuery(id+"F0.wireOp",EDGE,"E1.5"),sQuery(id+"F0.wireOp",EDGE,"E3.0"),sQuery(id+"F0.wireOp",EDGE,"E3.1"),sQuery(id+"F0.wireOp",EDGE,"E3.2"),sQuery(id+"F0.wireOp",EDGE,"E3.3"),sQuery(id+"F0.wireOp",EDGE,"E3.4"),sQuery(id+"F0.wireOp",EDGE,"E3.5")])]}),"instanceName":"1"}),"instanceName":"1"}),"instanceName":"1"}),"instanceName":"1"}),"instanceName":"1"}),"instanceName":"1"});
            var Q76;
            Q76=makeQuery(id+"F11.opPattern","COPY",BODY,{"derivedFrom":makeQuery(id+"F8.opPattern","COPY",BODY,{"derivedFrom":makeQuery(id+"F7.opPattern","COPY",BODY,{"derivedFrom":makeQuery(id+"F6.opPattern","COPY",BODY,{"derivedFrom":makeQuery(id+"F4.opPattern","COPY",BODY,{"derivedFrom":makeQuery(id+"F1.opExtrude","SWEPT_BODY",BODY,{"disambiguationData":[OSD([sQuery(id+"F0.wireOp",EDGE,"E1.0"),sQuery(id+"F0.wireOp",EDGE,"E1.1"),sQuery(id+"F0.wireOp",EDGE,"E1.2"),sQuery(id+"F0.wireOp",EDGE,"E1.3"),sQuery(id+"F0.wireOp",EDGE,"E1.4"),sQuery(id+"F0.wireOp",EDGE,"E1.5"),sQuery(id+"F0.wireOp",EDGE,"E3.0"),sQuery(id+"F0.wireOp",EDGE,"E3.1"),sQuery(id+"F0.wireOp",EDGE,"E3.2"),sQuery(id+"F0.wireOp",EDGE,"E3.3"),sQuery(id+"F0.wireOp",EDGE,"E3.4"),sQuery(id+"F0.wireOp",EDGE,"E3.5")])]}),"instanceName":"1"}),"instanceName":"1"}),"instanceName":"1"}),"instanceName":"1"}),"instanceName":"1"});
            var Q77;
            Q77=makeQuery(id+"F11.opPattern","COPY",BODY,{"derivedFrom":makeQuery(id+"F8.opPattern","COPY",BODY,{"derivedFrom":makeQuery(id+"F7.opPattern","COPY",BODY,{"derivedFrom":makeQuery(id+"F6.opPattern","COPY",BODY,{"derivedFrom":makeQuery(id+"F3.opPattern","COPY",BODY,{"derivedFrom":makeQuery(id+"F1.opExtrude","SWEPT_BODY",BODY,{"disambiguationData":[OSD([sQuery(id+"F0.wireOp",EDGE,"E1.0"),sQuery(id+"F0.wireOp",EDGE,"E1.1"),sQuery(id+"F0.wireOp",EDGE,"E1.2"),sQuery(id+"F0.wireOp",EDGE,"E1.3"),sQuery(id+"F0.wireOp",EDGE,"E1.4"),sQuery(id+"F0.wireOp",EDGE,"E1.5"),sQuery(id+"F0.wireOp",EDGE,"E3.0"),sQuery(id+"F0.wireOp",EDGE,"E3.1"),sQuery(id+"F0.wireOp",EDGE,"E3.2"),sQuery(id+"F0.wireOp",EDGE,"E3.3"),sQuery(id+"F0.wireOp",EDGE,"E3.4"),sQuery(id+"F0.wireOp",EDGE,"E3.5")])]}),"instanceName":"1"}),"instanceName":"1"}),"instanceName":"1"}),"instanceName":"1"}),"instanceName":"1"});
            var Q78;
            Q78=makeQuery(id+"F11.opPattern","COPY",BODY,{"derivedFrom":makeQuery(id+"F8.opPattern","COPY",BODY,{"derivedFrom":makeQuery(id+"F7.opPattern","COPY",BODY,{"derivedFrom":makeQuery(id+"F6.opPattern","COPY",BODY,{"derivedFrom":makeQuery(id+"F1.opExtrude","SWEPT_BODY",BODY,{"disambiguationData":[OSD([sQuery(id+"F0.wireOp",EDGE,"E1.0"),sQuery(id+"F0.wireOp",EDGE,"E1.1"),sQuery(id+"F0.wireOp",EDGE,"E1.2"),sQuery(id+"F0.wireOp",EDGE,"E1.3"),sQuery(id+"F0.wireOp",EDGE,"E1.4"),sQuery(id+"F0.wireOp",EDGE,"E1.5"),sQuery(id+"F0.wireOp",EDGE,"E3.0"),sQuery(id+"F0.wireOp",EDGE,"E3.1"),sQuery(id+"F0.wireOp",EDGE,"E3.2"),sQuery(id+"F0.wireOp",EDGE,"E3.3"),sQuery(id+"F0.wireOp",EDGE,"E3.4"),sQuery(id+"F0.wireOp",EDGE,"E3.5")])]}),"instanceName":"1"}),"instanceName":"1"}),"instanceName":"1"}),"instanceName":"1"});
            var Q79;
            Q79=makeQuery(id+"F11.opPattern","COPY",BODY,{"derivedFrom":makeQuery(id+"F8.opPattern","COPY",BODY,{"derivedFrom":makeQuery(id+"F7.opPattern","COPY",BODY,{"derivedFrom":makeQuery(id+"F5.opPattern","COPY",BODY,{"derivedFrom":makeQuery(id+"F4.opPattern","COPY",BODY,{"derivedFrom":makeQuery(id+"F3.opPattern","COPY",BODY,{"derivedFrom":makeQuery(id+"F1.opExtrude","SWEPT_BODY",BODY,{"disambiguationData":[OSD([sQuery(id+"F0.wireOp",EDGE,"E1.0"),sQuery(id+"F0.wireOp",EDGE,"E1.1"),sQuery(id+"F0.wireOp",EDGE,"E1.2"),sQuery(id+"F0.wireOp",EDGE,"E1.3"),sQuery(id+"F0.wireOp",EDGE,"E1.4"),sQuery(id+"F0.wireOp",EDGE,"E1.5"),sQuery(id+"F0.wireOp",EDGE,"E3.0"),sQuery(id+"F0.wireOp",EDGE,"E3.1"),sQuery(id+"F0.wireOp",EDGE,"E3.2"),sQuery(id+"F0.wireOp",EDGE,"E3.3"),sQuery(id+"F0.wireOp",EDGE,"E3.4"),sQuery(id+"F0.wireOp",EDGE,"E3.5")])]}),"instanceName":"1"}),"instanceName":"1"}),"instanceName":"1"}),"instanceName":"1"}),"instanceName":"1"}),"instanceName":"1"});
            var Q80;
            Q80=makeQuery(id+"F11.opPattern","COPY",BODY,{"derivedFrom":makeQuery(id+"F8.opPattern","COPY",BODY,{"derivedFrom":makeQuery(id+"F7.opPattern","COPY",BODY,{"derivedFrom":makeQuery(id+"F5.opPattern","COPY",BODY,{"derivedFrom":makeQuery(id+"F4.opPattern","COPY",BODY,{"derivedFrom":makeQuery(id+"F1.opExtrude","SWEPT_BODY",BODY,{"disambiguationData":[OSD([sQuery(id+"F0.wireOp",EDGE,"E1.0"),sQuery(id+"F0.wireOp",EDGE,"E1.1"),sQuery(id+"F0.wireOp",EDGE,"E1.2"),sQuery(id+"F0.wireOp",EDGE,"E1.3"),sQuery(id+"F0.wireOp",EDGE,"E1.4"),sQuery(id+"F0.wireOp",EDGE,"E1.5"),sQuery(id+"F0.wireOp",EDGE,"E3.0"),sQuery(id+"F0.wireOp",EDGE,"E3.1"),sQuery(id+"F0.wireOp",EDGE,"E3.2"),sQuery(id+"F0.wireOp",EDGE,"E3.3"),sQuery(id+"F0.wireOp",EDGE,"E3.4"),sQuery(id+"F0.wireOp",EDGE,"E3.5")])]}),"instanceName":"1"}),"instanceName":"1"}),"instanceName":"1"}),"instanceName":"1"}),"instanceName":"1"});
            var Q81;
            Q81=makeQuery(id+"F11.opPattern","COPY",BODY,{"derivedFrom":makeQuery(id+"F8.opPattern","COPY",BODY,{"derivedFrom":makeQuery(id+"F7.opPattern","COPY",BODY,{"derivedFrom":makeQuery(id+"F4.opPattern","COPY",BODY,{"derivedFrom":makeQuery(id+"F3.opPattern","COPY",BODY,{"derivedFrom":makeQuery(id+"F1.opExtrude","SWEPT_BODY",BODY,{"disambiguationData":[OSD([sQuery(id+"F0.wireOp",EDGE,"E1.0"),sQuery(id+"F0.wireOp",EDGE,"E1.1"),sQuery(id+"F0.wireOp",EDGE,"E1.2"),sQuery(id+"F0.wireOp",EDGE,"E1.3"),sQuery(id+"F0.wireOp",EDGE,"E1.4"),sQuery(id+"F0.wireOp",EDGE,"E1.5"),sQuery(id+"F0.wireOp",EDGE,"E3.0"),sQuery(id+"F0.wireOp",EDGE,"E3.1"),sQuery(id+"F0.wireOp",EDGE,"E3.2"),sQuery(id+"F0.wireOp",EDGE,"E3.3"),sQuery(id+"F0.wireOp",EDGE,"E3.4"),sQuery(id+"F0.wireOp",EDGE,"E3.5")])]}),"instanceName":"1"}),"instanceName":"1"}),"instanceName":"1"}),"instanceName":"1"}),"instanceName":"1"});
            var Q82;
            Q82=makeQuery(id+"F11.opPattern","COPY",BODY,{"derivedFrom":makeQuery(id+"F8.opPattern","COPY",BODY,{"derivedFrom":makeQuery(id+"F7.opPattern","COPY",BODY,{"derivedFrom":makeQuery(id+"F4.opPattern","COPY",BODY,{"derivedFrom":makeQuery(id+"F1.opExtrude","SWEPT_BODY",BODY,{"disambiguationData":[OSD([sQuery(id+"F0.wireOp",EDGE,"E1.0"),sQuery(id+"F0.wireOp",EDGE,"E1.1"),sQuery(id+"F0.wireOp",EDGE,"E1.2"),sQuery(id+"F0.wireOp",EDGE,"E1.3"),sQuery(id+"F0.wireOp",EDGE,"E1.4"),sQuery(id+"F0.wireOp",EDGE,"E1.5"),sQuery(id+"F0.wireOp",EDGE,"E3.0"),sQuery(id+"F0.wireOp",EDGE,"E3.1"),sQuery(id+"F0.wireOp",EDGE,"E3.2"),sQuery(id+"F0.wireOp",EDGE,"E3.3"),sQuery(id+"F0.wireOp",EDGE,"E3.4"),sQuery(id+"F0.wireOp",EDGE,"E3.5")])]}),"instanceName":"1"}),"instanceName":"1"}),"instanceName":"1"}),"instanceName":"1"});
            var Q83;
            Q83=makeQuery(id+"F11.opPattern","COPY",BODY,{"derivedFrom":makeQuery(id+"F8.opPattern","COPY",BODY,{"derivedFrom":makeQuery(id+"F7.opPattern","COPY",BODY,{"derivedFrom":makeQuery(id+"F3.opPattern","COPY",BODY,{"derivedFrom":makeQuery(id+"F1.opExtrude","SWEPT_BODY",BODY,{"disambiguationData":[OSD([sQuery(id+"F0.wireOp",EDGE,"E1.0"),sQuery(id+"F0.wireOp",EDGE,"E1.1"),sQuery(id+"F0.wireOp",EDGE,"E1.2"),sQuery(id+"F0.wireOp",EDGE,"E1.3"),sQuery(id+"F0.wireOp",EDGE,"E1.4"),sQuery(id+"F0.wireOp",EDGE,"E1.5"),sQuery(id+"F0.wireOp",EDGE,"E3.0"),sQuery(id+"F0.wireOp",EDGE,"E3.1"),sQuery(id+"F0.wireOp",EDGE,"E3.2"),sQuery(id+"F0.wireOp",EDGE,"E3.3"),sQuery(id+"F0.wireOp",EDGE,"E3.4"),sQuery(id+"F0.wireOp",EDGE,"E3.5")])]}),"instanceName":"1"}),"instanceName":"1"}),"instanceName":"1"}),"instanceName":"1"});
            var Q84;
            Q84=makeQuery(id+"F11.opPattern","COPY",BODY,{"derivedFrom":makeQuery(id+"F8.opPattern","COPY",BODY,{"derivedFrom":makeQuery(id+"F7.opPattern","COPY",BODY,{"derivedFrom":makeQuery(id+"F1.opExtrude","SWEPT_BODY",BODY,{"disambiguationData":[OSD([sQuery(id+"F0.wireOp",EDGE,"E1.0"),sQuery(id+"F0.wireOp",EDGE,"E1.1"),sQuery(id+"F0.wireOp",EDGE,"E1.2"),sQuery(id+"F0.wireOp",EDGE,"E1.3"),sQuery(id+"F0.wireOp",EDGE,"E1.4"),sQuery(id+"F0.wireOp",EDGE,"E1.5"),sQuery(id+"F0.wireOp",EDGE,"E3.0"),sQuery(id+"F0.wireOp",EDGE,"E3.1"),sQuery(id+"F0.wireOp",EDGE,"E3.2"),sQuery(id+"F0.wireOp",EDGE,"E3.3"),sQuery(id+"F0.wireOp",EDGE,"E3.4"),sQuery(id+"F0.wireOp",EDGE,"E3.5")])]}),"instanceName":"1"}),"instanceName":"1"}),"instanceName":"1"});
            var Q85;
            Q85=makeQuery(id+"F11.opPattern","COPY",BODY,{"derivedFrom":makeQuery(id+"F8.opPattern","COPY",BODY,{"derivedFrom":makeQuery(id+"F6.opPattern","COPY",BODY,{"derivedFrom":makeQuery(id+"F5.opPattern","COPY",BODY,{"derivedFrom":makeQuery(id+"F4.opPattern","COPY",BODY,{"derivedFrom":makeQuery(id+"F3.opPattern","COPY",BODY,{"derivedFrom":makeQuery(id+"F1.opExtrude","SWEPT_BODY",BODY,{"disambiguationData":[OSD([sQuery(id+"F0.wireOp",EDGE,"E1.0"),sQuery(id+"F0.wireOp",EDGE,"E1.1"),sQuery(id+"F0.wireOp",EDGE,"E1.2"),sQuery(id+"F0.wireOp",EDGE,"E1.3"),sQuery(id+"F0.wireOp",EDGE,"E1.4"),sQuery(id+"F0.wireOp",EDGE,"E1.5"),sQuery(id+"F0.wireOp",EDGE,"E3.0"),sQuery(id+"F0.wireOp",EDGE,"E3.1"),sQuery(id+"F0.wireOp",EDGE,"E3.2"),sQuery(id+"F0.wireOp",EDGE,"E3.3"),sQuery(id+"F0.wireOp",EDGE,"E3.4"),sQuery(id+"F0.wireOp",EDGE,"E3.5")])]}),"instanceName":"1"}),"instanceName":"1"}),"instanceName":"1"}),"instanceName":"1"}),"instanceName":"1"}),"instanceName":"1"});
            var Q86;
            Q86=makeQuery(id+"F11.opPattern","COPY",BODY,{"derivedFrom":makeQuery(id+"F8.opPattern","COPY",BODY,{"derivedFrom":makeQuery(id+"F6.opPattern","COPY",BODY,{"derivedFrom":makeQuery(id+"F5.opPattern","COPY",BODY,{"derivedFrom":makeQuery(id+"F4.opPattern","COPY",BODY,{"derivedFrom":makeQuery(id+"F1.opExtrude","SWEPT_BODY",BODY,{"disambiguationData":[OSD([sQuery(id+"F0.wireOp",EDGE,"E1.0"),sQuery(id+"F0.wireOp",EDGE,"E1.1"),sQuery(id+"F0.wireOp",EDGE,"E1.2"),sQuery(id+"F0.wireOp",EDGE,"E1.3"),sQuery(id+"F0.wireOp",EDGE,"E1.4"),sQuery(id+"F0.wireOp",EDGE,"E1.5"),sQuery(id+"F0.wireOp",EDGE,"E3.0"),sQuery(id+"F0.wireOp",EDGE,"E3.1"),sQuery(id+"F0.wireOp",EDGE,"E3.2"),sQuery(id+"F0.wireOp",EDGE,"E3.3"),sQuery(id+"F0.wireOp",EDGE,"E3.4"),sQuery(id+"F0.wireOp",EDGE,"E3.5")])]}),"instanceName":"1"}),"instanceName":"1"}),"instanceName":"1"}),"instanceName":"1"}),"instanceName":"1"});
            var Q87;
            Q87=makeQuery(id+"F11.opPattern","COPY",BODY,{"derivedFrom":makeQuery(id+"F8.opPattern","COPY",BODY,{"derivedFrom":makeQuery(id+"F6.opPattern","COPY",BODY,{"derivedFrom":makeQuery(id+"F4.opPattern","COPY",BODY,{"derivedFrom":makeQuery(id+"F3.opPattern","COPY",BODY,{"derivedFrom":makeQuery(id+"F1.opExtrude","SWEPT_BODY",BODY,{"disambiguationData":[OSD([sQuery(id+"F0.wireOp",EDGE,"E1.0"),sQuery(id+"F0.wireOp",EDGE,"E1.1"),sQuery(id+"F0.wireOp",EDGE,"E1.2"),sQuery(id+"F0.wireOp",EDGE,"E1.3"),sQuery(id+"F0.wireOp",EDGE,"E1.4"),sQuery(id+"F0.wireOp",EDGE,"E1.5"),sQuery(id+"F0.wireOp",EDGE,"E3.0"),sQuery(id+"F0.wireOp",EDGE,"E3.1"),sQuery(id+"F0.wireOp",EDGE,"E3.2"),sQuery(id+"F0.wireOp",EDGE,"E3.3"),sQuery(id+"F0.wireOp",EDGE,"E3.4"),sQuery(id+"F0.wireOp",EDGE,"E3.5")])]}),"instanceName":"1"}),"instanceName":"1"}),"instanceName":"1"}),"instanceName":"1"}),"instanceName":"1"});
            var Q88;
            Q88=makeQuery(id+"F11.opPattern","COPY",BODY,{"derivedFrom":makeQuery(id+"F8.opPattern","COPY",BODY,{"derivedFrom":makeQuery(id+"F6.opPattern","COPY",BODY,{"derivedFrom":makeQuery(id+"F4.opPattern","COPY",BODY,{"derivedFrom":makeQuery(id+"F1.opExtrude","SWEPT_BODY",BODY,{"disambiguationData":[OSD([sQuery(id+"F0.wireOp",EDGE,"E1.0"),sQuery(id+"F0.wireOp",EDGE,"E1.1"),sQuery(id+"F0.wireOp",EDGE,"E1.2"),sQuery(id+"F0.wireOp",EDGE,"E1.3"),sQuery(id+"F0.wireOp",EDGE,"E1.4"),sQuery(id+"F0.wireOp",EDGE,"E1.5"),sQuery(id+"F0.wireOp",EDGE,"E3.0"),sQuery(id+"F0.wireOp",EDGE,"E3.1"),sQuery(id+"F0.wireOp",EDGE,"E3.2"),sQuery(id+"F0.wireOp",EDGE,"E3.3"),sQuery(id+"F0.wireOp",EDGE,"E3.4"),sQuery(id+"F0.wireOp",EDGE,"E3.5")])]}),"instanceName":"1"}),"instanceName":"1"}),"instanceName":"1"}),"instanceName":"1"});
            var Q89;
            Q89=makeQuery(id+"F11.opPattern","COPY",BODY,{"derivedFrom":makeQuery(id+"F8.opPattern","COPY",BODY,{"derivedFrom":makeQuery(id+"F6.opPattern","COPY",BODY,{"derivedFrom":makeQuery(id+"F3.opPattern","COPY",BODY,{"derivedFrom":makeQuery(id+"F1.opExtrude","SWEPT_BODY",BODY,{"disambiguationData":[OSD([sQuery(id+"F0.wireOp",EDGE,"E1.0"),sQuery(id+"F0.wireOp",EDGE,"E1.1"),sQuery(id+"F0.wireOp",EDGE,"E1.2"),sQuery(id+"F0.wireOp",EDGE,"E1.3"),sQuery(id+"F0.wireOp",EDGE,"E1.4"),sQuery(id+"F0.wireOp",EDGE,"E1.5"),sQuery(id+"F0.wireOp",EDGE,"E3.0"),sQuery(id+"F0.wireOp",EDGE,"E3.1"),sQuery(id+"F0.wireOp",EDGE,"E3.2"),sQuery(id+"F0.wireOp",EDGE,"E3.3"),sQuery(id+"F0.wireOp",EDGE,"E3.4"),sQuery(id+"F0.wireOp",EDGE,"E3.5")])]}),"instanceName":"1"}),"instanceName":"1"}),"instanceName":"1"}),"instanceName":"1"});
            var Q90;
            Q90=makeQuery(id+"F11.opPattern","COPY",BODY,{"derivedFrom":makeQuery(id+"F8.opPattern","COPY",BODY,{"derivedFrom":makeQuery(id+"F6.opPattern","COPY",BODY,{"derivedFrom":makeQuery(id+"F1.opExtrude","SWEPT_BODY",BODY,{"disambiguationData":[OSD([sQuery(id+"F0.wireOp",EDGE,"E1.0"),sQuery(id+"F0.wireOp",EDGE,"E1.1"),sQuery(id+"F0.wireOp",EDGE,"E1.2"),sQuery(id+"F0.wireOp",EDGE,"E1.3"),sQuery(id+"F0.wireOp",EDGE,"E1.4"),sQuery(id+"F0.wireOp",EDGE,"E1.5"),sQuery(id+"F0.wireOp",EDGE,"E3.0"),sQuery(id+"F0.wireOp",EDGE,"E3.1"),sQuery(id+"F0.wireOp",EDGE,"E3.2"),sQuery(id+"F0.wireOp",EDGE,"E3.3"),sQuery(id+"F0.wireOp",EDGE,"E3.4"),sQuery(id+"F0.wireOp",EDGE,"E3.5")])]}),"instanceName":"1"}),"instanceName":"1"}),"instanceName":"1"});
            var Q91;
            Q91=makeQuery(id+"F11.opPattern","COPY",BODY,{"derivedFrom":makeQuery(id+"F8.opPattern","COPY",BODY,{"derivedFrom":makeQuery(id+"F5.opPattern","COPY",BODY,{"derivedFrom":makeQuery(id+"F4.opPattern","COPY",BODY,{"derivedFrom":makeQuery(id+"F3.opPattern","COPY",BODY,{"derivedFrom":makeQuery(id+"F1.opExtrude","SWEPT_BODY",BODY,{"disambiguationData":[OSD([sQuery(id+"F0.wireOp",EDGE,"E1.0"),sQuery(id+"F0.wireOp",EDGE,"E1.1"),sQuery(id+"F0.wireOp",EDGE,"E1.2"),sQuery(id+"F0.wireOp",EDGE,"E1.3"),sQuery(id+"F0.wireOp",EDGE,"E1.4"),sQuery(id+"F0.wireOp",EDGE,"E1.5"),sQuery(id+"F0.wireOp",EDGE,"E3.0"),sQuery(id+"F0.wireOp",EDGE,"E3.1"),sQuery(id+"F0.wireOp",EDGE,"E3.2"),sQuery(id+"F0.wireOp",EDGE,"E3.3"),sQuery(id+"F0.wireOp",EDGE,"E3.4"),sQuery(id+"F0.wireOp",EDGE,"E3.5")])]}),"instanceName":"1"}),"instanceName":"1"}),"instanceName":"1"}),"instanceName":"1"}),"instanceName":"1"});
            var Q92;
            Q92=makeQuery(id+"F11.opPattern","COPY",BODY,{"derivedFrom":makeQuery(id+"F8.opPattern","COPY",BODY,{"derivedFrom":makeQuery(id+"F5.opPattern","COPY",BODY,{"derivedFrom":makeQuery(id+"F4.opPattern","COPY",BODY,{"derivedFrom":makeQuery(id+"F1.opExtrude","SWEPT_BODY",BODY,{"disambiguationData":[OSD([sQuery(id+"F0.wireOp",EDGE,"E1.0"),sQuery(id+"F0.wireOp",EDGE,"E1.1"),sQuery(id+"F0.wireOp",EDGE,"E1.2"),sQuery(id+"F0.wireOp",EDGE,"E1.3"),sQuery(id+"F0.wireOp",EDGE,"E1.4"),sQuery(id+"F0.wireOp",EDGE,"E1.5"),sQuery(id+"F0.wireOp",EDGE,"E3.0"),sQuery(id+"F0.wireOp",EDGE,"E3.1"),sQuery(id+"F0.wireOp",EDGE,"E3.2"),sQuery(id+"F0.wireOp",EDGE,"E3.3"),sQuery(id+"F0.wireOp",EDGE,"E3.4"),sQuery(id+"F0.wireOp",EDGE,"E3.5")])]}),"instanceName":"1"}),"instanceName":"1"}),"instanceName":"1"}),"instanceName":"1"});
            var Q93;
            Q93=makeQuery(id+"F11.opPattern","COPY",BODY,{"derivedFrom":makeQuery(id+"F8.opPattern","COPY",BODY,{"derivedFrom":makeQuery(id+"F4.opPattern","COPY",BODY,{"derivedFrom":makeQuery(id+"F3.opPattern","COPY",BODY,{"derivedFrom":makeQuery(id+"F1.opExtrude","SWEPT_BODY",BODY,{"disambiguationData":[OSD([sQuery(id+"F0.wireOp",EDGE,"E1.0"),sQuery(id+"F0.wireOp",EDGE,"E1.1"),sQuery(id+"F0.wireOp",EDGE,"E1.2"),sQuery(id+"F0.wireOp",EDGE,"E1.3"),sQuery(id+"F0.wireOp",EDGE,"E1.4"),sQuery(id+"F0.wireOp",EDGE,"E1.5"),sQuery(id+"F0.wireOp",EDGE,"E3.0"),sQuery(id+"F0.wireOp",EDGE,"E3.1"),sQuery(id+"F0.wireOp",EDGE,"E3.2"),sQuery(id+"F0.wireOp",EDGE,"E3.3"),sQuery(id+"F0.wireOp",EDGE,"E3.4"),sQuery(id+"F0.wireOp",EDGE,"E3.5")])]}),"instanceName":"1"}),"instanceName":"1"}),"instanceName":"1"}),"instanceName":"1"});
            var Q94;
            Q94=makeQuery(id+"F11.opPattern","COPY",BODY,{"derivedFrom":makeQuery(id+"F8.opPattern","COPY",BODY,{"derivedFrom":makeQuery(id+"F4.opPattern","COPY",BODY,{"derivedFrom":makeQuery(id+"F1.opExtrude","SWEPT_BODY",BODY,{"disambiguationData":[OSD([sQuery(id+"F0.wireOp",EDGE,"E1.0"),sQuery(id+"F0.wireOp",EDGE,"E1.1"),sQuery(id+"F0.wireOp",EDGE,"E1.2"),sQuery(id+"F0.wireOp",EDGE,"E1.3"),sQuery(id+"F0.wireOp",EDGE,"E1.4"),sQuery(id+"F0.wireOp",EDGE,"E1.5"),sQuery(id+"F0.wireOp",EDGE,"E3.0"),sQuery(id+"F0.wireOp",EDGE,"E3.1"),sQuery(id+"F0.wireOp",EDGE,"E3.2"),sQuery(id+"F0.wireOp",EDGE,"E3.3"),sQuery(id+"F0.wireOp",EDGE,"E3.4"),sQuery(id+"F0.wireOp",EDGE,"E3.5")])]}),"instanceName":"1"}),"instanceName":"1"}),"instanceName":"1"});
            var Q95;
            Q95=makeQuery(id+"F11.opPattern","COPY",BODY,{"derivedFrom":makeQuery(id+"F8.opPattern","COPY",BODY,{"derivedFrom":makeQuery(id+"F3.opPattern","COPY",BODY,{"derivedFrom":makeQuery(id+"F1.opExtrude","SWEPT_BODY",BODY,{"disambiguationData":[OSD([sQuery(id+"F0.wireOp",EDGE,"E1.0"),sQuery(id+"F0.wireOp",EDGE,"E1.1"),sQuery(id+"F0.wireOp",EDGE,"E1.2"),sQuery(id+"F0.wireOp",EDGE,"E1.3"),sQuery(id+"F0.wireOp",EDGE,"E1.4"),sQuery(id+"F0.wireOp",EDGE,"E1.5"),sQuery(id+"F0.wireOp",EDGE,"E3.0"),sQuery(id+"F0.wireOp",EDGE,"E3.1"),sQuery(id+"F0.wireOp",EDGE,"E3.2"),sQuery(id+"F0.wireOp",EDGE,"E3.3"),sQuery(id+"F0.wireOp",EDGE,"E3.4"),sQuery(id+"F0.wireOp",EDGE,"E3.5")])]}),"instanceName":"1"}),"instanceName":"1"}),"instanceName":"1"});
            var Q96;
            Q96=makeQuery(id+"F11.opPattern","COPY",BODY,{"derivedFrom":makeQuery(id+"F8.opPattern","COPY",BODY,{"derivedFrom":makeQuery(id+"F1.opExtrude","SWEPT_BODY",BODY,{"disambiguationData":[OSD([sQuery(id+"F0.wireOp",EDGE,"E1.0"),sQuery(id+"F0.wireOp",EDGE,"E1.1"),sQuery(id+"F0.wireOp",EDGE,"E1.2"),sQuery(id+"F0.wireOp",EDGE,"E1.3"),sQuery(id+"F0.wireOp",EDGE,"E1.4"),sQuery(id+"F0.wireOp",EDGE,"E1.5"),sQuery(id+"F0.wireOp",EDGE,"E3.0"),sQuery(id+"F0.wireOp",EDGE,"E3.1"),sQuery(id+"F0.wireOp",EDGE,"E3.2"),sQuery(id+"F0.wireOp",EDGE,"E3.3"),sQuery(id+"F0.wireOp",EDGE,"E3.4"),sQuery(id+"F0.wireOp",EDGE,"E3.5")])]}),"instanceName":"1"}),"instanceName":"1"});
            var Q97;
            Q97=makeQuery(id+"F10.opPattern","COPY",BODY,{"derivedFrom":makeQuery(id+"F9.opPattern","COPY",BODY,{"derivedFrom":makeQuery(id+"F8.opPattern","COPY",BODY,{"derivedFrom":makeQuery(id+"F7.opPattern","COPY",BODY,{"derivedFrom":makeQuery(id+"F6.opPattern","COPY",BODY,{"derivedFrom":makeQuery(id+"F5.opPattern","COPY",BODY,{"derivedFrom":makeQuery(id+"F4.opPattern","COPY",BODY,{"derivedFrom":makeQuery(id+"F1.opExtrude","SWEPT_BODY",BODY,{"disambiguationData":[OSD([sQuery(id+"F0.wireOp",EDGE,"E1.0"),sQuery(id+"F0.wireOp",EDGE,"E1.1"),sQuery(id+"F0.wireOp",EDGE,"E1.2"),sQuery(id+"F0.wireOp",EDGE,"E1.3"),sQuery(id+"F0.wireOp",EDGE,"E1.4"),sQuery(id+"F0.wireOp",EDGE,"E1.5"),sQuery(id+"F0.wireOp",EDGE,"E3.0"),sQuery(id+"F0.wireOp",EDGE,"E3.1"),sQuery(id+"F0.wireOp",EDGE,"E3.2"),sQuery(id+"F0.wireOp",EDGE,"E3.3"),sQuery(id+"F0.wireOp",EDGE,"E3.4"),sQuery(id+"F0.wireOp",EDGE,"E3.5")])]}),"instanceName":"1"}),"instanceName":"1"}),"instanceName":"1"}),"instanceName":"1"}),"instanceName":"1"}),"instanceName":"1"}),"instanceName":"1"});
            var Q98;
            Q98=makeQuery(id+"F9.opPattern","COPY",BODY,{"derivedFrom":makeQuery(id+"F8.opPattern","COPY",BODY,{"derivedFrom":makeQuery(id+"F7.opPattern","COPY",BODY,{"derivedFrom":makeQuery(id+"F6.opPattern","COPY",BODY,{"derivedFrom":makeQuery(id+"F5.opPattern","COPY",BODY,{"derivedFrom":makeQuery(id+"F4.opPattern","COPY",BODY,{"derivedFrom":makeQuery(id+"F1.opExtrude","SWEPT_BODY",BODY,{"disambiguationData":[OSD([sQuery(id+"F0.wireOp",EDGE,"E1.0"),sQuery(id+"F0.wireOp",EDGE,"E1.1"),sQuery(id+"F0.wireOp",EDGE,"E1.2"),sQuery(id+"F0.wireOp",EDGE,"E1.3"),sQuery(id+"F0.wireOp",EDGE,"E1.4"),sQuery(id+"F0.wireOp",EDGE,"E1.5"),sQuery(id+"F0.wireOp",EDGE,"E3.0"),sQuery(id+"F0.wireOp",EDGE,"E3.1"),sQuery(id+"F0.wireOp",EDGE,"E3.2"),sQuery(id+"F0.wireOp",EDGE,"E3.3"),sQuery(id+"F0.wireOp",EDGE,"E3.4"),sQuery(id+"F0.wireOp",EDGE,"E3.5")])]}),"instanceName":"1"}),"instanceName":"1"}),"instanceName":"1"}),"instanceName":"1"}),"instanceName":"1"}),"instanceName":"1"});
            var Q99;
            Q99=makeQuery(id+"F9.opPattern","COPY",BODY,{"derivedFrom":makeQuery(id+"F8.opPattern","COPY",BODY,{"derivedFrom":makeQuery(id+"F7.opPattern","COPY",BODY,{"derivedFrom":makeQuery(id+"F6.opPattern","COPY",BODY,{"derivedFrom":makeQuery(id+"F4.opPattern","COPY",BODY,{"derivedFrom":makeQuery(id+"F3.opPattern","COPY",BODY,{"derivedFrom":makeQuery(id+"F1.opExtrude","SWEPT_BODY",BODY,{"disambiguationData":[OSD([sQuery(id+"F0.wireOp",EDGE,"E1.0"),sQuery(id+"F0.wireOp",EDGE,"E1.1"),sQuery(id+"F0.wireOp",EDGE,"E1.2"),sQuery(id+"F0.wireOp",EDGE,"E1.3"),sQuery(id+"F0.wireOp",EDGE,"E1.4"),sQuery(id+"F0.wireOp",EDGE,"E1.5"),sQuery(id+"F0.wireOp",EDGE,"E3.0"),sQuery(id+"F0.wireOp",EDGE,"E3.1"),sQuery(id+"F0.wireOp",EDGE,"E3.2"),sQuery(id+"F0.wireOp",EDGE,"E3.3"),sQuery(id+"F0.wireOp",EDGE,"E3.4"),sQuery(id+"F0.wireOp",EDGE,"E3.5")])]}),"instanceName":"1"}),"instanceName":"1"}),"instanceName":"1"}),"instanceName":"1"}),"instanceName":"1"}),"instanceName":"1"});
            var Q100;
            Q100=makeQuery(id+"F9.opPattern","COPY",BODY,{"derivedFrom":makeQuery(id+"F8.opPattern","COPY",BODY,{"derivedFrom":makeQuery(id+"F7.opPattern","COPY",BODY,{"derivedFrom":makeQuery(id+"F6.opPattern","COPY",BODY,{"derivedFrom":makeQuery(id+"F4.opPattern","COPY",BODY,{"derivedFrom":makeQuery(id+"F1.opExtrude","SWEPT_BODY",BODY,{"disambiguationData":[OSD([sQuery(id+"F0.wireOp",EDGE,"E1.0"),sQuery(id+"F0.wireOp",EDGE,"E1.1"),sQuery(id+"F0.wireOp",EDGE,"E1.2"),sQuery(id+"F0.wireOp",EDGE,"E1.3"),sQuery(id+"F0.wireOp",EDGE,"E1.4"),sQuery(id+"F0.wireOp",EDGE,"E1.5"),sQuery(id+"F0.wireOp",EDGE,"E3.0"),sQuery(id+"F0.wireOp",EDGE,"E3.1"),sQuery(id+"F0.wireOp",EDGE,"E3.2"),sQuery(id+"F0.wireOp",EDGE,"E3.3"),sQuery(id+"F0.wireOp",EDGE,"E3.4"),sQuery(id+"F0.wireOp",EDGE,"E3.5")])]}),"instanceName":"1"}),"instanceName":"1"}),"instanceName":"1"}),"instanceName":"1"}),"instanceName":"1"});
            var Q101;
            Q101=makeQuery(id+"F9.opPattern","COPY",BODY,{"derivedFrom":makeQuery(id+"F8.opPattern","COPY",BODY,{"derivedFrom":makeQuery(id+"F7.opPattern","COPY",BODY,{"derivedFrom":makeQuery(id+"F6.opPattern","COPY",BODY,{"derivedFrom":makeQuery(id+"F3.opPattern","COPY",BODY,{"derivedFrom":makeQuery(id+"F1.opExtrude","SWEPT_BODY",BODY,{"disambiguationData":[OSD([sQuery(id+"F0.wireOp",EDGE,"E1.0"),sQuery(id+"F0.wireOp",EDGE,"E1.1"),sQuery(id+"F0.wireOp",EDGE,"E1.2"),sQuery(id+"F0.wireOp",EDGE,"E1.3"),sQuery(id+"F0.wireOp",EDGE,"E1.4"),sQuery(id+"F0.wireOp",EDGE,"E1.5"),sQuery(id+"F0.wireOp",EDGE,"E3.0"),sQuery(id+"F0.wireOp",EDGE,"E3.1"),sQuery(id+"F0.wireOp",EDGE,"E3.2"),sQuery(id+"F0.wireOp",EDGE,"E3.3"),sQuery(id+"F0.wireOp",EDGE,"E3.4"),sQuery(id+"F0.wireOp",EDGE,"E3.5")])]}),"instanceName":"1"}),"instanceName":"1"}),"instanceName":"1"}),"instanceName":"1"}),"instanceName":"1"});
            var Q102;
            Q102=makeQuery(id+"F9.opPattern","COPY",BODY,{"derivedFrom":makeQuery(id+"F8.opPattern","COPY",BODY,{"derivedFrom":makeQuery(id+"F7.opPattern","COPY",BODY,{"derivedFrom":makeQuery(id+"F6.opPattern","COPY",BODY,{"derivedFrom":makeQuery(id+"F1.opExtrude","SWEPT_BODY",BODY,{"disambiguationData":[OSD([sQuery(id+"F0.wireOp",EDGE,"E1.0"),sQuery(id+"F0.wireOp",EDGE,"E1.1"),sQuery(id+"F0.wireOp",EDGE,"E1.2"),sQuery(id+"F0.wireOp",EDGE,"E1.3"),sQuery(id+"F0.wireOp",EDGE,"E1.4"),sQuery(id+"F0.wireOp",EDGE,"E1.5"),sQuery(id+"F0.wireOp",EDGE,"E3.0"),sQuery(id+"F0.wireOp",EDGE,"E3.1"),sQuery(id+"F0.wireOp",EDGE,"E3.2"),sQuery(id+"F0.wireOp",EDGE,"E3.3"),sQuery(id+"F0.wireOp",EDGE,"E3.4"),sQuery(id+"F0.wireOp",EDGE,"E3.5")])]}),"instanceName":"1"}),"instanceName":"1"}),"instanceName":"1"}),"instanceName":"1"});
            var Q103;
            Q103=makeQuery(id+"F9.opPattern","COPY",BODY,{"derivedFrom":makeQuery(id+"F8.opPattern","COPY",BODY,{"derivedFrom":makeQuery(id+"F7.opPattern","COPY",BODY,{"derivedFrom":makeQuery(id+"F5.opPattern","COPY",BODY,{"derivedFrom":makeQuery(id+"F4.opPattern","COPY",BODY,{"derivedFrom":makeQuery(id+"F3.opPattern","COPY",BODY,{"derivedFrom":makeQuery(id+"F1.opExtrude","SWEPT_BODY",BODY,{"disambiguationData":[OSD([sQuery(id+"F0.wireOp",EDGE,"E1.0"),sQuery(id+"F0.wireOp",EDGE,"E1.1"),sQuery(id+"F0.wireOp",EDGE,"E1.2"),sQuery(id+"F0.wireOp",EDGE,"E1.3"),sQuery(id+"F0.wireOp",EDGE,"E1.4"),sQuery(id+"F0.wireOp",EDGE,"E1.5"),sQuery(id+"F0.wireOp",EDGE,"E3.0"),sQuery(id+"F0.wireOp",EDGE,"E3.1"),sQuery(id+"F0.wireOp",EDGE,"E3.2"),sQuery(id+"F0.wireOp",EDGE,"E3.3"),sQuery(id+"F0.wireOp",EDGE,"E3.4"),sQuery(id+"F0.wireOp",EDGE,"E3.5")])]}),"instanceName":"1"}),"instanceName":"1"}),"instanceName":"1"}),"instanceName":"1"}),"instanceName":"1"}),"instanceName":"1"});
            var Q104;
            Q104=makeQuery(id+"F9.opPattern","COPY",BODY,{"derivedFrom":makeQuery(id+"F8.opPattern","COPY",BODY,{"derivedFrom":makeQuery(id+"F7.opPattern","COPY",BODY,{"derivedFrom":makeQuery(id+"F5.opPattern","COPY",BODY,{"derivedFrom":makeQuery(id+"F4.opPattern","COPY",BODY,{"derivedFrom":makeQuery(id+"F1.opExtrude","SWEPT_BODY",BODY,{"disambiguationData":[OSD([sQuery(id+"F0.wireOp",EDGE,"E1.0"),sQuery(id+"F0.wireOp",EDGE,"E1.1"),sQuery(id+"F0.wireOp",EDGE,"E1.2"),sQuery(id+"F0.wireOp",EDGE,"E1.3"),sQuery(id+"F0.wireOp",EDGE,"E1.4"),sQuery(id+"F0.wireOp",EDGE,"E1.5"),sQuery(id+"F0.wireOp",EDGE,"E3.0"),sQuery(id+"F0.wireOp",EDGE,"E3.1"),sQuery(id+"F0.wireOp",EDGE,"E3.2"),sQuery(id+"F0.wireOp",EDGE,"E3.3"),sQuery(id+"F0.wireOp",EDGE,"E3.4"),sQuery(id+"F0.wireOp",EDGE,"E3.5")])]}),"instanceName":"1"}),"instanceName":"1"}),"instanceName":"1"}),"instanceName":"1"}),"instanceName":"1"});
            var Q105;
            Q105=makeQuery(id+"F9.opPattern","COPY",BODY,{"derivedFrom":makeQuery(id+"F8.opPattern","COPY",BODY,{"derivedFrom":makeQuery(id+"F7.opPattern","COPY",BODY,{"derivedFrom":makeQuery(id+"F4.opPattern","COPY",BODY,{"derivedFrom":makeQuery(id+"F3.opPattern","COPY",BODY,{"derivedFrom":makeQuery(id+"F1.opExtrude","SWEPT_BODY",BODY,{"disambiguationData":[OSD([sQuery(id+"F0.wireOp",EDGE,"E1.0"),sQuery(id+"F0.wireOp",EDGE,"E1.1"),sQuery(id+"F0.wireOp",EDGE,"E1.2"),sQuery(id+"F0.wireOp",EDGE,"E1.3"),sQuery(id+"F0.wireOp",EDGE,"E1.4"),sQuery(id+"F0.wireOp",EDGE,"E1.5"),sQuery(id+"F0.wireOp",EDGE,"E3.0"),sQuery(id+"F0.wireOp",EDGE,"E3.1"),sQuery(id+"F0.wireOp",EDGE,"E3.2"),sQuery(id+"F0.wireOp",EDGE,"E3.3"),sQuery(id+"F0.wireOp",EDGE,"E3.4"),sQuery(id+"F0.wireOp",EDGE,"E3.5")])]}),"instanceName":"1"}),"instanceName":"1"}),"instanceName":"1"}),"instanceName":"1"}),"instanceName":"1"});
            var Q106;
            Q106=makeQuery(id+"F9.opPattern","COPY",BODY,{"derivedFrom":makeQuery(id+"F8.opPattern","COPY",BODY,{"derivedFrom":makeQuery(id+"F7.opPattern","COPY",BODY,{"derivedFrom":makeQuery(id+"F4.opPattern","COPY",BODY,{"derivedFrom":makeQuery(id+"F1.opExtrude","SWEPT_BODY",BODY,{"disambiguationData":[OSD([sQuery(id+"F0.wireOp",EDGE,"E1.0"),sQuery(id+"F0.wireOp",EDGE,"E1.1"),sQuery(id+"F0.wireOp",EDGE,"E1.2"),sQuery(id+"F0.wireOp",EDGE,"E1.3"),sQuery(id+"F0.wireOp",EDGE,"E1.4"),sQuery(id+"F0.wireOp",EDGE,"E1.5"),sQuery(id+"F0.wireOp",EDGE,"E3.0"),sQuery(id+"F0.wireOp",EDGE,"E3.1"),sQuery(id+"F0.wireOp",EDGE,"E3.2"),sQuery(id+"F0.wireOp",EDGE,"E3.3"),sQuery(id+"F0.wireOp",EDGE,"E3.4"),sQuery(id+"F0.wireOp",EDGE,"E3.5")])]}),"instanceName":"1"}),"instanceName":"1"}),"instanceName":"1"}),"instanceName":"1"});
            var Q107;
            Q107=makeQuery(id+"F9.opPattern","COPY",BODY,{"derivedFrom":makeQuery(id+"F8.opPattern","COPY",BODY,{"derivedFrom":makeQuery(id+"F7.opPattern","COPY",BODY,{"derivedFrom":makeQuery(id+"F3.opPattern","COPY",BODY,{"derivedFrom":makeQuery(id+"F1.opExtrude","SWEPT_BODY",BODY,{"disambiguationData":[OSD([sQuery(id+"F0.wireOp",EDGE,"E1.0"),sQuery(id+"F0.wireOp",EDGE,"E1.1"),sQuery(id+"F0.wireOp",EDGE,"E1.2"),sQuery(id+"F0.wireOp",EDGE,"E1.3"),sQuery(id+"F0.wireOp",EDGE,"E1.4"),sQuery(id+"F0.wireOp",EDGE,"E1.5"),sQuery(id+"F0.wireOp",EDGE,"E3.0"),sQuery(id+"F0.wireOp",EDGE,"E3.1"),sQuery(id+"F0.wireOp",EDGE,"E3.2"),sQuery(id+"F0.wireOp",EDGE,"E3.3"),sQuery(id+"F0.wireOp",EDGE,"E3.4"),sQuery(id+"F0.wireOp",EDGE,"E3.5")])]}),"instanceName":"1"}),"instanceName":"1"}),"instanceName":"1"}),"instanceName":"1"});
            var Q108;
            Q108=makeQuery(id+"F9.opPattern","COPY",BODY,{"derivedFrom":makeQuery(id+"F8.opPattern","COPY",BODY,{"derivedFrom":makeQuery(id+"F7.opPattern","COPY",BODY,{"derivedFrom":makeQuery(id+"F1.opExtrude","SWEPT_BODY",BODY,{"disambiguationData":[OSD([sQuery(id+"F0.wireOp",EDGE,"E1.0"),sQuery(id+"F0.wireOp",EDGE,"E1.1"),sQuery(id+"F0.wireOp",EDGE,"E1.2"),sQuery(id+"F0.wireOp",EDGE,"E1.3"),sQuery(id+"F0.wireOp",EDGE,"E1.4"),sQuery(id+"F0.wireOp",EDGE,"E1.5"),sQuery(id+"F0.wireOp",EDGE,"E3.0"),sQuery(id+"F0.wireOp",EDGE,"E3.1"),sQuery(id+"F0.wireOp",EDGE,"E3.2"),sQuery(id+"F0.wireOp",EDGE,"E3.3"),sQuery(id+"F0.wireOp",EDGE,"E3.4"),sQuery(id+"F0.wireOp",EDGE,"E3.5")])]}),"instanceName":"1"}),"instanceName":"1"}),"instanceName":"1"});
            var Q109;
            Q109=makeQuery(id+"F9.opPattern","COPY",BODY,{"derivedFrom":makeQuery(id+"F8.opPattern","COPY",BODY,{"derivedFrom":makeQuery(id+"F6.opPattern","COPY",BODY,{"derivedFrom":makeQuery(id+"F5.opPattern","COPY",BODY,{"derivedFrom":makeQuery(id+"F4.opPattern","COPY",BODY,{"derivedFrom":makeQuery(id+"F3.opPattern","COPY",BODY,{"derivedFrom":makeQuery(id+"F1.opExtrude","SWEPT_BODY",BODY,{"disambiguationData":[OSD([sQuery(id+"F0.wireOp",EDGE,"E1.0"),sQuery(id+"F0.wireOp",EDGE,"E1.1"),sQuery(id+"F0.wireOp",EDGE,"E1.2"),sQuery(id+"F0.wireOp",EDGE,"E1.3"),sQuery(id+"F0.wireOp",EDGE,"E1.4"),sQuery(id+"F0.wireOp",EDGE,"E1.5"),sQuery(id+"F0.wireOp",EDGE,"E3.0"),sQuery(id+"F0.wireOp",EDGE,"E3.1"),sQuery(id+"F0.wireOp",EDGE,"E3.2"),sQuery(id+"F0.wireOp",EDGE,"E3.3"),sQuery(id+"F0.wireOp",EDGE,"E3.4"),sQuery(id+"F0.wireOp",EDGE,"E3.5")])]}),"instanceName":"1"}),"instanceName":"1"}),"instanceName":"1"}),"instanceName":"1"}),"instanceName":"1"}),"instanceName":"1"});
            var Q110;
            Q110=makeQuery(id+"F9.opPattern","COPY",BODY,{"derivedFrom":makeQuery(id+"F8.opPattern","COPY",BODY,{"derivedFrom":makeQuery(id+"F6.opPattern","COPY",BODY,{"derivedFrom":makeQuery(id+"F5.opPattern","COPY",BODY,{"derivedFrom":makeQuery(id+"F4.opPattern","COPY",BODY,{"derivedFrom":makeQuery(id+"F1.opExtrude","SWEPT_BODY",BODY,{"disambiguationData":[OSD([sQuery(id+"F0.wireOp",EDGE,"E1.0"),sQuery(id+"F0.wireOp",EDGE,"E1.1"),sQuery(id+"F0.wireOp",EDGE,"E1.2"),sQuery(id+"F0.wireOp",EDGE,"E1.3"),sQuery(id+"F0.wireOp",EDGE,"E1.4"),sQuery(id+"F0.wireOp",EDGE,"E1.5"),sQuery(id+"F0.wireOp",EDGE,"E3.0"),sQuery(id+"F0.wireOp",EDGE,"E3.1"),sQuery(id+"F0.wireOp",EDGE,"E3.2"),sQuery(id+"F0.wireOp",EDGE,"E3.3"),sQuery(id+"F0.wireOp",EDGE,"E3.4"),sQuery(id+"F0.wireOp",EDGE,"E3.5")])]}),"instanceName":"1"}),"instanceName":"1"}),"instanceName":"1"}),"instanceName":"1"}),"instanceName":"1"});
            var Q111;
            Q111=makeQuery(id+"F9.opPattern","COPY",BODY,{"derivedFrom":makeQuery(id+"F8.opPattern","COPY",BODY,{"derivedFrom":makeQuery(id+"F6.opPattern","COPY",BODY,{"derivedFrom":makeQuery(id+"F4.opPattern","COPY",BODY,{"derivedFrom":makeQuery(id+"F3.opPattern","COPY",BODY,{"derivedFrom":makeQuery(id+"F1.opExtrude","SWEPT_BODY",BODY,{"disambiguationData":[OSD([sQuery(id+"F0.wireOp",EDGE,"E1.0"),sQuery(id+"F0.wireOp",EDGE,"E1.1"),sQuery(id+"F0.wireOp",EDGE,"E1.2"),sQuery(id+"F0.wireOp",EDGE,"E1.3"),sQuery(id+"F0.wireOp",EDGE,"E1.4"),sQuery(id+"F0.wireOp",EDGE,"E1.5"),sQuery(id+"F0.wireOp",EDGE,"E3.0"),sQuery(id+"F0.wireOp",EDGE,"E3.1"),sQuery(id+"F0.wireOp",EDGE,"E3.2"),sQuery(id+"F0.wireOp",EDGE,"E3.3"),sQuery(id+"F0.wireOp",EDGE,"E3.4"),sQuery(id+"F0.wireOp",EDGE,"E3.5")])]}),"instanceName":"1"}),"instanceName":"1"}),"instanceName":"1"}),"instanceName":"1"}),"instanceName":"1"});
            var Q112;
            Q112=makeQuery(id+"F9.opPattern","COPY",BODY,{"derivedFrom":makeQuery(id+"F8.opPattern","COPY",BODY,{"derivedFrom":makeQuery(id+"F6.opPattern","COPY",BODY,{"derivedFrom":makeQuery(id+"F4.opPattern","COPY",BODY,{"derivedFrom":makeQuery(id+"F1.opExtrude","SWEPT_BODY",BODY,{"disambiguationData":[OSD([sQuery(id+"F0.wireOp",EDGE,"E1.0"),sQuery(id+"F0.wireOp",EDGE,"E1.1"),sQuery(id+"F0.wireOp",EDGE,"E1.2"),sQuery(id+"F0.wireOp",EDGE,"E1.3"),sQuery(id+"F0.wireOp",EDGE,"E1.4"),sQuery(id+"F0.wireOp",EDGE,"E1.5"),sQuery(id+"F0.wireOp",EDGE,"E3.0"),sQuery(id+"F0.wireOp",EDGE,"E3.1"),sQuery(id+"F0.wireOp",EDGE,"E3.2"),sQuery(id+"F0.wireOp",EDGE,"E3.3"),sQuery(id+"F0.wireOp",EDGE,"E3.4"),sQuery(id+"F0.wireOp",EDGE,"E3.5")])]}),"instanceName":"1"}),"instanceName":"1"}),"instanceName":"1"}),"instanceName":"1"});
            var Q113;
            Q113=makeQuery(id+"F9.opPattern","COPY",BODY,{"derivedFrom":makeQuery(id+"F8.opPattern","COPY",BODY,{"derivedFrom":makeQuery(id+"F6.opPattern","COPY",BODY,{"derivedFrom":makeQuery(id+"F3.opPattern","COPY",BODY,{"derivedFrom":makeQuery(id+"F1.opExtrude","SWEPT_BODY",BODY,{"disambiguationData":[OSD([sQuery(id+"F0.wireOp",EDGE,"E1.0"),sQuery(id+"F0.wireOp",EDGE,"E1.1"),sQuery(id+"F0.wireOp",EDGE,"E1.2"),sQuery(id+"F0.wireOp",EDGE,"E1.3"),sQuery(id+"F0.wireOp",EDGE,"E1.4"),sQuery(id+"F0.wireOp",EDGE,"E1.5"),sQuery(id+"F0.wireOp",EDGE,"E3.0"),sQuery(id+"F0.wireOp",EDGE,"E3.1"),sQuery(id+"F0.wireOp",EDGE,"E3.2"),sQuery(id+"F0.wireOp",EDGE,"E3.3"),sQuery(id+"F0.wireOp",EDGE,"E3.4"),sQuery(id+"F0.wireOp",EDGE,"E3.5")])]}),"instanceName":"1"}),"instanceName":"1"}),"instanceName":"1"}),"instanceName":"1"});
            var Q114;
            Q114=makeQuery(id+"F9.opPattern","COPY",BODY,{"derivedFrom":makeQuery(id+"F8.opPattern","COPY",BODY,{"derivedFrom":makeQuery(id+"F6.opPattern","COPY",BODY,{"derivedFrom":makeQuery(id+"F1.opExtrude","SWEPT_BODY",BODY,{"disambiguationData":[OSD([sQuery(id+"F0.wireOp",EDGE,"E1.0"),sQuery(id+"F0.wireOp",EDGE,"E1.1"),sQuery(id+"F0.wireOp",EDGE,"E1.2"),sQuery(id+"F0.wireOp",EDGE,"E1.3"),sQuery(id+"F0.wireOp",EDGE,"E1.4"),sQuery(id+"F0.wireOp",EDGE,"E1.5"),sQuery(id+"F0.wireOp",EDGE,"E3.0"),sQuery(id+"F0.wireOp",EDGE,"E3.1"),sQuery(id+"F0.wireOp",EDGE,"E3.2"),sQuery(id+"F0.wireOp",EDGE,"E3.3"),sQuery(id+"F0.wireOp",EDGE,"E3.4"),sQuery(id+"F0.wireOp",EDGE,"E3.5")])]}),"instanceName":"1"}),"instanceName":"1"}),"instanceName":"1"});
            var Q115;
            Q115=makeQuery(id+"F9.opPattern","COPY",BODY,{"derivedFrom":makeQuery(id+"F8.opPattern","COPY",BODY,{"derivedFrom":makeQuery(id+"F5.opPattern","COPY",BODY,{"derivedFrom":makeQuery(id+"F4.opPattern","COPY",BODY,{"derivedFrom":makeQuery(id+"F3.opPattern","COPY",BODY,{"derivedFrom":makeQuery(id+"F1.opExtrude","SWEPT_BODY",BODY,{"disambiguationData":[OSD([sQuery(id+"F0.wireOp",EDGE,"E1.0"),sQuery(id+"F0.wireOp",EDGE,"E1.1"),sQuery(id+"F0.wireOp",EDGE,"E1.2"),sQuery(id+"F0.wireOp",EDGE,"E1.3"),sQuery(id+"F0.wireOp",EDGE,"E1.4"),sQuery(id+"F0.wireOp",EDGE,"E1.5"),sQuery(id+"F0.wireOp",EDGE,"E3.0"),sQuery(id+"F0.wireOp",EDGE,"E3.1"),sQuery(id+"F0.wireOp",EDGE,"E3.2"),sQuery(id+"F0.wireOp",EDGE,"E3.3"),sQuery(id+"F0.wireOp",EDGE,"E3.4"),sQuery(id+"F0.wireOp",EDGE,"E3.5")])]}),"instanceName":"1"}),"instanceName":"1"}),"instanceName":"1"}),"instanceName":"1"}),"instanceName":"1"});
            var Q116;
            Q116=makeQuery(id+"F9.opPattern","COPY",BODY,{"derivedFrom":makeQuery(id+"F8.opPattern","COPY",BODY,{"derivedFrom":makeQuery(id+"F5.opPattern","COPY",BODY,{"derivedFrom":makeQuery(id+"F4.opPattern","COPY",BODY,{"derivedFrom":makeQuery(id+"F1.opExtrude","SWEPT_BODY",BODY,{"disambiguationData":[OSD([sQuery(id+"F0.wireOp",EDGE,"E1.0"),sQuery(id+"F0.wireOp",EDGE,"E1.1"),sQuery(id+"F0.wireOp",EDGE,"E1.2"),sQuery(id+"F0.wireOp",EDGE,"E1.3"),sQuery(id+"F0.wireOp",EDGE,"E1.4"),sQuery(id+"F0.wireOp",EDGE,"E1.5"),sQuery(id+"F0.wireOp",EDGE,"E3.0"),sQuery(id+"F0.wireOp",EDGE,"E3.1"),sQuery(id+"F0.wireOp",EDGE,"E3.2"),sQuery(id+"F0.wireOp",EDGE,"E3.3"),sQuery(id+"F0.wireOp",EDGE,"E3.4"),sQuery(id+"F0.wireOp",EDGE,"E3.5")])]}),"instanceName":"1"}),"instanceName":"1"}),"instanceName":"1"}),"instanceName":"1"});
            var Q117;
            Q117=makeQuery(id+"F9.opPattern","COPY",BODY,{"derivedFrom":makeQuery(id+"F8.opPattern","COPY",BODY,{"derivedFrom":makeQuery(id+"F4.opPattern","COPY",BODY,{"derivedFrom":makeQuery(id+"F3.opPattern","COPY",BODY,{"derivedFrom":makeQuery(id+"F1.opExtrude","SWEPT_BODY",BODY,{"disambiguationData":[OSD([sQuery(id+"F0.wireOp",EDGE,"E1.0"),sQuery(id+"F0.wireOp",EDGE,"E1.1"),sQuery(id+"F0.wireOp",EDGE,"E1.2"),sQuery(id+"F0.wireOp",EDGE,"E1.3"),sQuery(id+"F0.wireOp",EDGE,"E1.4"),sQuery(id+"F0.wireOp",EDGE,"E1.5"),sQuery(id+"F0.wireOp",EDGE,"E3.0"),sQuery(id+"F0.wireOp",EDGE,"E3.1"),sQuery(id+"F0.wireOp",EDGE,"E3.2"),sQuery(id+"F0.wireOp",EDGE,"E3.3"),sQuery(id+"F0.wireOp",EDGE,"E3.4"),sQuery(id+"F0.wireOp",EDGE,"E3.5")])]}),"instanceName":"1"}),"instanceName":"1"}),"instanceName":"1"}),"instanceName":"1"});
            var Q118;
            Q118=makeQuery(id+"F9.opPattern","COPY",BODY,{"derivedFrom":makeQuery(id+"F8.opPattern","COPY",BODY,{"derivedFrom":makeQuery(id+"F4.opPattern","COPY",BODY,{"derivedFrom":makeQuery(id+"F1.opExtrude","SWEPT_BODY",BODY,{"disambiguationData":[OSD([sQuery(id+"F0.wireOp",EDGE,"E1.0"),sQuery(id+"F0.wireOp",EDGE,"E1.1"),sQuery(id+"F0.wireOp",EDGE,"E1.2"),sQuery(id+"F0.wireOp",EDGE,"E1.3"),sQuery(id+"F0.wireOp",EDGE,"E1.4"),sQuery(id+"F0.wireOp",EDGE,"E1.5"),sQuery(id+"F0.wireOp",EDGE,"E3.0"),sQuery(id+"F0.wireOp",EDGE,"E3.1"),sQuery(id+"F0.wireOp",EDGE,"E3.2"),sQuery(id+"F0.wireOp",EDGE,"E3.3"),sQuery(id+"F0.wireOp",EDGE,"E3.4"),sQuery(id+"F0.wireOp",EDGE,"E3.5")])]}),"instanceName":"1"}),"instanceName":"1"}),"instanceName":"1"});
            var Q119;
            Q119=makeQuery(id+"F9.opPattern","COPY",BODY,{"derivedFrom":makeQuery(id+"F8.opPattern","COPY",BODY,{"derivedFrom":makeQuery(id+"F3.opPattern","COPY",BODY,{"derivedFrom":makeQuery(id+"F1.opExtrude","SWEPT_BODY",BODY,{"disambiguationData":[OSD([sQuery(id+"F0.wireOp",EDGE,"E1.0"),sQuery(id+"F0.wireOp",EDGE,"E1.1"),sQuery(id+"F0.wireOp",EDGE,"E1.2"),sQuery(id+"F0.wireOp",EDGE,"E1.3"),sQuery(id+"F0.wireOp",EDGE,"E1.4"),sQuery(id+"F0.wireOp",EDGE,"E1.5"),sQuery(id+"F0.wireOp",EDGE,"E3.0"),sQuery(id+"F0.wireOp",EDGE,"E3.1"),sQuery(id+"F0.wireOp",EDGE,"E3.2"),sQuery(id+"F0.wireOp",EDGE,"E3.3"),sQuery(id+"F0.wireOp",EDGE,"E3.4"),sQuery(id+"F0.wireOp",EDGE,"E3.5")])]}),"instanceName":"1"}),"instanceName":"1"}),"instanceName":"1"});
            var Q120;
            Q120=makeQuery(id+"F9.opPattern","COPY",BODY,{"derivedFrom":makeQuery(id+"F8.opPattern","COPY",BODY,{"derivedFrom":makeQuery(id+"F1.opExtrude","SWEPT_BODY",BODY,{"disambiguationData":[OSD([sQuery(id+"F0.wireOp",EDGE,"E1.0"),sQuery(id+"F0.wireOp",EDGE,"E1.1"),sQuery(id+"F0.wireOp",EDGE,"E1.2"),sQuery(id+"F0.wireOp",EDGE,"E1.3"),sQuery(id+"F0.wireOp",EDGE,"E1.4"),sQuery(id+"F0.wireOp",EDGE,"E1.5"),sQuery(id+"F0.wireOp",EDGE,"E3.0"),sQuery(id+"F0.wireOp",EDGE,"E3.1"),sQuery(id+"F0.wireOp",EDGE,"E3.2"),sQuery(id+"F0.wireOp",EDGE,"E3.3"),sQuery(id+"F0.wireOp",EDGE,"E3.4"),sQuery(id+"F0.wireOp",EDGE,"E3.5")])]}),"instanceName":"1"}),"instanceName":"1"});
            var Q121;
            Q121=makeQuery(id+"F9.opPattern","COPY",BODY,{"derivedFrom":makeQuery(id+"F7.opPattern","COPY",BODY,{"derivedFrom":makeQuery(id+"F6.opPattern","COPY",BODY,{"derivedFrom":makeQuery(id+"F5.opPattern","COPY",BODY,{"derivedFrom":makeQuery(id+"F4.opPattern","COPY",BODY,{"derivedFrom":makeQuery(id+"F3.opPattern","COPY",BODY,{"derivedFrom":makeQuery(id+"F1.opExtrude","SWEPT_BODY",BODY,{"disambiguationData":[OSD([sQuery(id+"F0.wireOp",EDGE,"E1.0"),sQuery(id+"F0.wireOp",EDGE,"E1.1"),sQuery(id+"F0.wireOp",EDGE,"E1.2"),sQuery(id+"F0.wireOp",EDGE,"E1.3"),sQuery(id+"F0.wireOp",EDGE,"E1.4"),sQuery(id+"F0.wireOp",EDGE,"E1.5"),sQuery(id+"F0.wireOp",EDGE,"E3.0"),sQuery(id+"F0.wireOp",EDGE,"E3.1"),sQuery(id+"F0.wireOp",EDGE,"E3.2"),sQuery(id+"F0.wireOp",EDGE,"E3.3"),sQuery(id+"F0.wireOp",EDGE,"E3.4"),sQuery(id+"F0.wireOp",EDGE,"E3.5")])]}),"instanceName":"1"}),"instanceName":"1"}),"instanceName":"1"}),"instanceName":"1"}),"instanceName":"1"}),"instanceName":"1"});
            var Q122;
            Q122=makeQuery(id+"F9.opPattern","COPY",BODY,{"derivedFrom":makeQuery(id+"F7.opPattern","COPY",BODY,{"derivedFrom":makeQuery(id+"F6.opPattern","COPY",BODY,{"derivedFrom":makeQuery(id+"F5.opPattern","COPY",BODY,{"derivedFrom":makeQuery(id+"F4.opPattern","COPY",BODY,{"derivedFrom":makeQuery(id+"F1.opExtrude","SWEPT_BODY",BODY,{"disambiguationData":[OSD([sQuery(id+"F0.wireOp",EDGE,"E1.0"),sQuery(id+"F0.wireOp",EDGE,"E1.1"),sQuery(id+"F0.wireOp",EDGE,"E1.2"),sQuery(id+"F0.wireOp",EDGE,"E1.3"),sQuery(id+"F0.wireOp",EDGE,"E1.4"),sQuery(id+"F0.wireOp",EDGE,"E1.5"),sQuery(id+"F0.wireOp",EDGE,"E3.0"),sQuery(id+"F0.wireOp",EDGE,"E3.1"),sQuery(id+"F0.wireOp",EDGE,"E3.2"),sQuery(id+"F0.wireOp",EDGE,"E3.3"),sQuery(id+"F0.wireOp",EDGE,"E3.4"),sQuery(id+"F0.wireOp",EDGE,"E3.5")])]}),"instanceName":"1"}),"instanceName":"1"}),"instanceName":"1"}),"instanceName":"1"}),"instanceName":"1"});
            var Q123;
            Q123=makeQuery(id+"F9.opPattern","COPY",BODY,{"derivedFrom":makeQuery(id+"F7.opPattern","COPY",BODY,{"derivedFrom":makeQuery(id+"F6.opPattern","COPY",BODY,{"derivedFrom":makeQuery(id+"F4.opPattern","COPY",BODY,{"derivedFrom":makeQuery(id+"F3.opPattern","COPY",BODY,{"derivedFrom":makeQuery(id+"F1.opExtrude","SWEPT_BODY",BODY,{"disambiguationData":[OSD([sQuery(id+"F0.wireOp",EDGE,"E1.0"),sQuery(id+"F0.wireOp",EDGE,"E1.1"),sQuery(id+"F0.wireOp",EDGE,"E1.2"),sQuery(id+"F0.wireOp",EDGE,"E1.3"),sQuery(id+"F0.wireOp",EDGE,"E1.4"),sQuery(id+"F0.wireOp",EDGE,"E1.5"),sQuery(id+"F0.wireOp",EDGE,"E3.0"),sQuery(id+"F0.wireOp",EDGE,"E3.1"),sQuery(id+"F0.wireOp",EDGE,"E3.2"),sQuery(id+"F0.wireOp",EDGE,"E3.3"),sQuery(id+"F0.wireOp",EDGE,"E3.4"),sQuery(id+"F0.wireOp",EDGE,"E3.5")])]}),"instanceName":"1"}),"instanceName":"1"}),"instanceName":"1"}),"instanceName":"1"}),"instanceName":"1"});
            var Q124;
            Q124=makeQuery(id+"F9.opPattern","COPY",BODY,{"derivedFrom":makeQuery(id+"F7.opPattern","COPY",BODY,{"derivedFrom":makeQuery(id+"F6.opPattern","COPY",BODY,{"derivedFrom":makeQuery(id+"F4.opPattern","COPY",BODY,{"derivedFrom":makeQuery(id+"F1.opExtrude","SWEPT_BODY",BODY,{"disambiguationData":[OSD([sQuery(id+"F0.wireOp",EDGE,"E1.0"),sQuery(id+"F0.wireOp",EDGE,"E1.1"),sQuery(id+"F0.wireOp",EDGE,"E1.2"),sQuery(id+"F0.wireOp",EDGE,"E1.3"),sQuery(id+"F0.wireOp",EDGE,"E1.4"),sQuery(id+"F0.wireOp",EDGE,"E1.5"),sQuery(id+"F0.wireOp",EDGE,"E3.0"),sQuery(id+"F0.wireOp",EDGE,"E3.1"),sQuery(id+"F0.wireOp",EDGE,"E3.2"),sQuery(id+"F0.wireOp",EDGE,"E3.3"),sQuery(id+"F0.wireOp",EDGE,"E3.4"),sQuery(id+"F0.wireOp",EDGE,"E3.5")])]}),"instanceName":"1"}),"instanceName":"1"}),"instanceName":"1"}),"instanceName":"1"});
            var Q125;
            Q125=makeQuery(id+"F9.opPattern","COPY",BODY,{"derivedFrom":makeQuery(id+"F7.opPattern","COPY",BODY,{"derivedFrom":makeQuery(id+"F6.opPattern","COPY",BODY,{"derivedFrom":makeQuery(id+"F3.opPattern","COPY",BODY,{"derivedFrom":makeQuery(id+"F1.opExtrude","SWEPT_BODY",BODY,{"disambiguationData":[OSD([sQuery(id+"F0.wireOp",EDGE,"E1.0"),sQuery(id+"F0.wireOp",EDGE,"E1.1"),sQuery(id+"F0.wireOp",EDGE,"E1.2"),sQuery(id+"F0.wireOp",EDGE,"E1.3"),sQuery(id+"F0.wireOp",EDGE,"E1.4"),sQuery(id+"F0.wireOp",EDGE,"E1.5"),sQuery(id+"F0.wireOp",EDGE,"E3.0"),sQuery(id+"F0.wireOp",EDGE,"E3.1"),sQuery(id+"F0.wireOp",EDGE,"E3.2"),sQuery(id+"F0.wireOp",EDGE,"E3.3"),sQuery(id+"F0.wireOp",EDGE,"E3.4"),sQuery(id+"F0.wireOp",EDGE,"E3.5")])]}),"instanceName":"1"}),"instanceName":"1"}),"instanceName":"1"}),"instanceName":"1"});
            var Q126;
            Q126=makeQuery(id+"F9.opPattern","COPY",BODY,{"derivedFrom":makeQuery(id+"F7.opPattern","COPY",BODY,{"derivedFrom":makeQuery(id+"F6.opPattern","COPY",BODY,{"derivedFrom":makeQuery(id+"F1.opExtrude","SWEPT_BODY",BODY,{"disambiguationData":[OSD([sQuery(id+"F0.wireOp",EDGE,"E1.0"),sQuery(id+"F0.wireOp",EDGE,"E1.1"),sQuery(id+"F0.wireOp",EDGE,"E1.2"),sQuery(id+"F0.wireOp",EDGE,"E1.3"),sQuery(id+"F0.wireOp",EDGE,"E1.4"),sQuery(id+"F0.wireOp",EDGE,"E1.5"),sQuery(id+"F0.wireOp",EDGE,"E3.0"),sQuery(id+"F0.wireOp",EDGE,"E3.1"),sQuery(id+"F0.wireOp",EDGE,"E3.2"),sQuery(id+"F0.wireOp",EDGE,"E3.3"),sQuery(id+"F0.wireOp",EDGE,"E3.4"),sQuery(id+"F0.wireOp",EDGE,"E3.5")])]}),"instanceName":"1"}),"instanceName":"1"}),"instanceName":"1"});
            var Q127;
            Q127=makeQuery(id+"F9.opPattern","COPY",BODY,{"derivedFrom":makeQuery(id+"F7.opPattern","COPY",BODY,{"derivedFrom":makeQuery(id+"F5.opPattern","COPY",BODY,{"derivedFrom":makeQuery(id+"F4.opPattern","COPY",BODY,{"derivedFrom":makeQuery(id+"F3.opPattern","COPY",BODY,{"derivedFrom":makeQuery(id+"F1.opExtrude","SWEPT_BODY",BODY,{"disambiguationData":[OSD([sQuery(id+"F0.wireOp",EDGE,"E1.0"),sQuery(id+"F0.wireOp",EDGE,"E1.1"),sQuery(id+"F0.wireOp",EDGE,"E1.2"),sQuery(id+"F0.wireOp",EDGE,"E1.3"),sQuery(id+"F0.wireOp",EDGE,"E1.4"),sQuery(id+"F0.wireOp",EDGE,"E1.5"),sQuery(id+"F0.wireOp",EDGE,"E3.0"),sQuery(id+"F0.wireOp",EDGE,"E3.1"),sQuery(id+"F0.wireOp",EDGE,"E3.2"),sQuery(id+"F0.wireOp",EDGE,"E3.3"),sQuery(id+"F0.wireOp",EDGE,"E3.4"),sQuery(id+"F0.wireOp",EDGE,"E3.5")])]}),"instanceName":"1"}),"instanceName":"1"}),"instanceName":"1"}),"instanceName":"1"}),"instanceName":"1"});
            var Q128;
            Q128=makeQuery(id+"F9.opPattern","COPY",BODY,{"derivedFrom":makeQuery(id+"F7.opPattern","COPY",BODY,{"derivedFrom":makeQuery(id+"F5.opPattern","COPY",BODY,{"derivedFrom":makeQuery(id+"F4.opPattern","COPY",BODY,{"derivedFrom":makeQuery(id+"F1.opExtrude","SWEPT_BODY",BODY,{"disambiguationData":[OSD([sQuery(id+"F0.wireOp",EDGE,"E1.0"),sQuery(id+"F0.wireOp",EDGE,"E1.1"),sQuery(id+"F0.wireOp",EDGE,"E1.2"),sQuery(id+"F0.wireOp",EDGE,"E1.3"),sQuery(id+"F0.wireOp",EDGE,"E1.4"),sQuery(id+"F0.wireOp",EDGE,"E1.5"),sQuery(id+"F0.wireOp",EDGE,"E3.0"),sQuery(id+"F0.wireOp",EDGE,"E3.1"),sQuery(id+"F0.wireOp",EDGE,"E3.2"),sQuery(id+"F0.wireOp",EDGE,"E3.3"),sQuery(id+"F0.wireOp",EDGE,"E3.4"),sQuery(id+"F0.wireOp",EDGE,"E3.5")])]}),"instanceName":"1"}),"instanceName":"1"}),"instanceName":"1"}),"instanceName":"1"});
            var Q129;
            Q129=makeQuery(id+"F9.opPattern","COPY",BODY,{"derivedFrom":makeQuery(id+"F7.opPattern","COPY",BODY,{"derivedFrom":makeQuery(id+"F4.opPattern","COPY",BODY,{"derivedFrom":makeQuery(id+"F3.opPattern","COPY",BODY,{"derivedFrom":makeQuery(id+"F1.opExtrude","SWEPT_BODY",BODY,{"disambiguationData":[OSD([sQuery(id+"F0.wireOp",EDGE,"E1.0"),sQuery(id+"F0.wireOp",EDGE,"E1.1"),sQuery(id+"F0.wireOp",EDGE,"E1.2"),sQuery(id+"F0.wireOp",EDGE,"E1.3"),sQuery(id+"F0.wireOp",EDGE,"E1.4"),sQuery(id+"F0.wireOp",EDGE,"E1.5"),sQuery(id+"F0.wireOp",EDGE,"E3.0"),sQuery(id+"F0.wireOp",EDGE,"E3.1"),sQuery(id+"F0.wireOp",EDGE,"E3.2"),sQuery(id+"F0.wireOp",EDGE,"E3.3"),sQuery(id+"F0.wireOp",EDGE,"E3.4"),sQuery(id+"F0.wireOp",EDGE,"E3.5")])]}),"instanceName":"1"}),"instanceName":"1"}),"instanceName":"1"}),"instanceName":"1"});
            var Q130;
            Q130=makeQuery(id+"F9.opPattern","COPY",BODY,{"derivedFrom":makeQuery(id+"F7.opPattern","COPY",BODY,{"derivedFrom":makeQuery(id+"F4.opPattern","COPY",BODY,{"derivedFrom":makeQuery(id+"F1.opExtrude","SWEPT_BODY",BODY,{"disambiguationData":[OSD([sQuery(id+"F0.wireOp",EDGE,"E1.0"),sQuery(id+"F0.wireOp",EDGE,"E1.1"),sQuery(id+"F0.wireOp",EDGE,"E1.2"),sQuery(id+"F0.wireOp",EDGE,"E1.3"),sQuery(id+"F0.wireOp",EDGE,"E1.4"),sQuery(id+"F0.wireOp",EDGE,"E1.5"),sQuery(id+"F0.wireOp",EDGE,"E3.0"),sQuery(id+"F0.wireOp",EDGE,"E3.1"),sQuery(id+"F0.wireOp",EDGE,"E3.2"),sQuery(id+"F0.wireOp",EDGE,"E3.3"),sQuery(id+"F0.wireOp",EDGE,"E3.4"),sQuery(id+"F0.wireOp",EDGE,"E3.5")])]}),"instanceName":"1"}),"instanceName":"1"}),"instanceName":"1"});
            var Q131;
            Q131=makeQuery(id+"F9.opPattern","COPY",BODY,{"derivedFrom":makeQuery(id+"F7.opPattern","COPY",BODY,{"derivedFrom":makeQuery(id+"F3.opPattern","COPY",BODY,{"derivedFrom":makeQuery(id+"F1.opExtrude","SWEPT_BODY",BODY,{"disambiguationData":[OSD([sQuery(id+"F0.wireOp",EDGE,"E1.0"),sQuery(id+"F0.wireOp",EDGE,"E1.1"),sQuery(id+"F0.wireOp",EDGE,"E1.2"),sQuery(id+"F0.wireOp",EDGE,"E1.3"),sQuery(id+"F0.wireOp",EDGE,"E1.4"),sQuery(id+"F0.wireOp",EDGE,"E1.5"),sQuery(id+"F0.wireOp",EDGE,"E3.0"),sQuery(id+"F0.wireOp",EDGE,"E3.1"),sQuery(id+"F0.wireOp",EDGE,"E3.2"),sQuery(id+"F0.wireOp",EDGE,"E3.3"),sQuery(id+"F0.wireOp",EDGE,"E3.4"),sQuery(id+"F0.wireOp",EDGE,"E3.5")])]}),"instanceName":"1"}),"instanceName":"1"}),"instanceName":"1"});
            var Q132;
            Q132=makeQuery(id+"F9.opPattern","COPY",BODY,{"derivedFrom":makeQuery(id+"F7.opPattern","COPY",BODY,{"derivedFrom":makeQuery(id+"F1.opExtrude","SWEPT_BODY",BODY,{"disambiguationData":[OSD([sQuery(id+"F0.wireOp",EDGE,"E1.0"),sQuery(id+"F0.wireOp",EDGE,"E1.1"),sQuery(id+"F0.wireOp",EDGE,"E1.2"),sQuery(id+"F0.wireOp",EDGE,"E1.3"),sQuery(id+"F0.wireOp",EDGE,"E1.4"),sQuery(id+"F0.wireOp",EDGE,"E1.5"),sQuery(id+"F0.wireOp",EDGE,"E3.0"),sQuery(id+"F0.wireOp",EDGE,"E3.1"),sQuery(id+"F0.wireOp",EDGE,"E3.2"),sQuery(id+"F0.wireOp",EDGE,"E3.3"),sQuery(id+"F0.wireOp",EDGE,"E3.4"),sQuery(id+"F0.wireOp",EDGE,"E3.5")])]}),"instanceName":"1"}),"instanceName":"1"});
            var Q133;
            Q133=makeQuery(id+"F9.opPattern","COPY",BODY,{"derivedFrom":makeQuery(id+"F6.opPattern","COPY",BODY,{"derivedFrom":makeQuery(id+"F5.opPattern","COPY",BODY,{"derivedFrom":makeQuery(id+"F4.opPattern","COPY",BODY,{"derivedFrom":makeQuery(id+"F3.opPattern","COPY",BODY,{"derivedFrom":makeQuery(id+"F1.opExtrude","SWEPT_BODY",BODY,{"disambiguationData":[OSD([sQuery(id+"F0.wireOp",EDGE,"E1.0"),sQuery(id+"F0.wireOp",EDGE,"E1.1"),sQuery(id+"F0.wireOp",EDGE,"E1.2"),sQuery(id+"F0.wireOp",EDGE,"E1.3"),sQuery(id+"F0.wireOp",EDGE,"E1.4"),sQuery(id+"F0.wireOp",EDGE,"E1.5"),sQuery(id+"F0.wireOp",EDGE,"E3.0"),sQuery(id+"F0.wireOp",EDGE,"E3.1"),sQuery(id+"F0.wireOp",EDGE,"E3.2"),sQuery(id+"F0.wireOp",EDGE,"E3.3"),sQuery(id+"F0.wireOp",EDGE,"E3.4"),sQuery(id+"F0.wireOp",EDGE,"E3.5")])]}),"instanceName":"1"}),"instanceName":"1"}),"instanceName":"1"}),"instanceName":"1"}),"instanceName":"1"});
            var Q134;
            Q134=makeQuery(id+"F9.opPattern","COPY",BODY,{"derivedFrom":makeQuery(id+"F6.opPattern","COPY",BODY,{"derivedFrom":makeQuery(id+"F5.opPattern","COPY",BODY,{"derivedFrom":makeQuery(id+"F4.opPattern","COPY",BODY,{"derivedFrom":makeQuery(id+"F1.opExtrude","SWEPT_BODY",BODY,{"disambiguationData":[OSD([sQuery(id+"F0.wireOp",EDGE,"E1.0"),sQuery(id+"F0.wireOp",EDGE,"E1.1"),sQuery(id+"F0.wireOp",EDGE,"E1.2"),sQuery(id+"F0.wireOp",EDGE,"E1.3"),sQuery(id+"F0.wireOp",EDGE,"E1.4"),sQuery(id+"F0.wireOp",EDGE,"E1.5"),sQuery(id+"F0.wireOp",EDGE,"E3.0"),sQuery(id+"F0.wireOp",EDGE,"E3.1"),sQuery(id+"F0.wireOp",EDGE,"E3.2"),sQuery(id+"F0.wireOp",EDGE,"E3.3"),sQuery(id+"F0.wireOp",EDGE,"E3.4"),sQuery(id+"F0.wireOp",EDGE,"E3.5")])]}),"instanceName":"1"}),"instanceName":"1"}),"instanceName":"1"}),"instanceName":"1"});
            var Q135;
            Q135=makeQuery(id+"F9.opPattern","COPY",BODY,{"derivedFrom":makeQuery(id+"F6.opPattern","COPY",BODY,{"derivedFrom":makeQuery(id+"F4.opPattern","COPY",BODY,{"derivedFrom":makeQuery(id+"F3.opPattern","COPY",BODY,{"derivedFrom":makeQuery(id+"F1.opExtrude","SWEPT_BODY",BODY,{"disambiguationData":[OSD([sQuery(id+"F0.wireOp",EDGE,"E1.0"),sQuery(id+"F0.wireOp",EDGE,"E1.1"),sQuery(id+"F0.wireOp",EDGE,"E1.2"),sQuery(id+"F0.wireOp",EDGE,"E1.3"),sQuery(id+"F0.wireOp",EDGE,"E1.4"),sQuery(id+"F0.wireOp",EDGE,"E1.5"),sQuery(id+"F0.wireOp",EDGE,"E3.0"),sQuery(id+"F0.wireOp",EDGE,"E3.1"),sQuery(id+"F0.wireOp",EDGE,"E3.2"),sQuery(id+"F0.wireOp",EDGE,"E3.3"),sQuery(id+"F0.wireOp",EDGE,"E3.4"),sQuery(id+"F0.wireOp",EDGE,"E3.5")])]}),"instanceName":"1"}),"instanceName":"1"}),"instanceName":"1"}),"instanceName":"1"});
            var Q136;
            Q136=makeQuery(id+"F9.opPattern","COPY",BODY,{"derivedFrom":makeQuery(id+"F6.opPattern","COPY",BODY,{"derivedFrom":makeQuery(id+"F4.opPattern","COPY",BODY,{"derivedFrom":makeQuery(id+"F1.opExtrude","SWEPT_BODY",BODY,{"disambiguationData":[OSD([sQuery(id+"F0.wireOp",EDGE,"E1.0"),sQuery(id+"F0.wireOp",EDGE,"E1.1"),sQuery(id+"F0.wireOp",EDGE,"E1.2"),sQuery(id+"F0.wireOp",EDGE,"E1.3"),sQuery(id+"F0.wireOp",EDGE,"E1.4"),sQuery(id+"F0.wireOp",EDGE,"E1.5"),sQuery(id+"F0.wireOp",EDGE,"E3.0"),sQuery(id+"F0.wireOp",EDGE,"E3.1"),sQuery(id+"F0.wireOp",EDGE,"E3.2"),sQuery(id+"F0.wireOp",EDGE,"E3.3"),sQuery(id+"F0.wireOp",EDGE,"E3.4"),sQuery(id+"F0.wireOp",EDGE,"E3.5")])]}),"instanceName":"1"}),"instanceName":"1"}),"instanceName":"1"});
            var Q137;
            Q137=makeQuery(id+"F9.opPattern","COPY",BODY,{"derivedFrom":makeQuery(id+"F6.opPattern","COPY",BODY,{"derivedFrom":makeQuery(id+"F3.opPattern","COPY",BODY,{"derivedFrom":makeQuery(id+"F1.opExtrude","SWEPT_BODY",BODY,{"disambiguationData":[OSD([sQuery(id+"F0.wireOp",EDGE,"E1.0"),sQuery(id+"F0.wireOp",EDGE,"E1.1"),sQuery(id+"F0.wireOp",EDGE,"E1.2"),sQuery(id+"F0.wireOp",EDGE,"E1.3"),sQuery(id+"F0.wireOp",EDGE,"E1.4"),sQuery(id+"F0.wireOp",EDGE,"E1.5"),sQuery(id+"F0.wireOp",EDGE,"E3.0"),sQuery(id+"F0.wireOp",EDGE,"E3.1"),sQuery(id+"F0.wireOp",EDGE,"E3.2"),sQuery(id+"F0.wireOp",EDGE,"E3.3"),sQuery(id+"F0.wireOp",EDGE,"E3.4"),sQuery(id+"F0.wireOp",EDGE,"E3.5")])]}),"instanceName":"1"}),"instanceName":"1"}),"instanceName":"1"});
            var Q138;
            Q138=makeQuery(id+"F9.opPattern","COPY",BODY,{"derivedFrom":makeQuery(id+"F6.opPattern","COPY",BODY,{"derivedFrom":makeQuery(id+"F1.opExtrude","SWEPT_BODY",BODY,{"disambiguationData":[OSD([sQuery(id+"F0.wireOp",EDGE,"E1.0"),sQuery(id+"F0.wireOp",EDGE,"E1.1"),sQuery(id+"F0.wireOp",EDGE,"E1.2"),sQuery(id+"F0.wireOp",EDGE,"E1.3"),sQuery(id+"F0.wireOp",EDGE,"E1.4"),sQuery(id+"F0.wireOp",EDGE,"E1.5"),sQuery(id+"F0.wireOp",EDGE,"E3.0"),sQuery(id+"F0.wireOp",EDGE,"E3.1"),sQuery(id+"F0.wireOp",EDGE,"E3.2"),sQuery(id+"F0.wireOp",EDGE,"E3.3"),sQuery(id+"F0.wireOp",EDGE,"E3.4"),sQuery(id+"F0.wireOp",EDGE,"E3.5")])]}),"instanceName":"1"}),"instanceName":"1"});
            var Q139;
            Q139=makeQuery(id+"F9.opPattern","COPY",BODY,{"derivedFrom":makeQuery(id+"F5.opPattern","COPY",BODY,{"derivedFrom":makeQuery(id+"F4.opPattern","COPY",BODY,{"derivedFrom":makeQuery(id+"F3.opPattern","COPY",BODY,{"derivedFrom":makeQuery(id+"F1.opExtrude","SWEPT_BODY",BODY,{"disambiguationData":[OSD([sQuery(id+"F0.wireOp",EDGE,"E1.0"),sQuery(id+"F0.wireOp",EDGE,"E1.1"),sQuery(id+"F0.wireOp",EDGE,"E1.2"),sQuery(id+"F0.wireOp",EDGE,"E1.3"),sQuery(id+"F0.wireOp",EDGE,"E1.4"),sQuery(id+"F0.wireOp",EDGE,"E1.5"),sQuery(id+"F0.wireOp",EDGE,"E3.0"),sQuery(id+"F0.wireOp",EDGE,"E3.1"),sQuery(id+"F0.wireOp",EDGE,"E3.2"),sQuery(id+"F0.wireOp",EDGE,"E3.3"),sQuery(id+"F0.wireOp",EDGE,"E3.4"),sQuery(id+"F0.wireOp",EDGE,"E3.5")])]}),"instanceName":"1"}),"instanceName":"1"}),"instanceName":"1"}),"instanceName":"1"});
            var Q140;
            Q140=makeQuery(id+"F9.opPattern","COPY",BODY,{"derivedFrom":makeQuery(id+"F5.opPattern","COPY",BODY,{"derivedFrom":makeQuery(id+"F4.opPattern","COPY",BODY,{"derivedFrom":makeQuery(id+"F1.opExtrude","SWEPT_BODY",BODY,{"disambiguationData":[OSD([sQuery(id+"F0.wireOp",EDGE,"E1.0"),sQuery(id+"F0.wireOp",EDGE,"E1.1"),sQuery(id+"F0.wireOp",EDGE,"E1.2"),sQuery(id+"F0.wireOp",EDGE,"E1.3"),sQuery(id+"F0.wireOp",EDGE,"E1.4"),sQuery(id+"F0.wireOp",EDGE,"E1.5"),sQuery(id+"F0.wireOp",EDGE,"E3.0"),sQuery(id+"F0.wireOp",EDGE,"E3.1"),sQuery(id+"F0.wireOp",EDGE,"E3.2"),sQuery(id+"F0.wireOp",EDGE,"E3.3"),sQuery(id+"F0.wireOp",EDGE,"E3.4"),sQuery(id+"F0.wireOp",EDGE,"E3.5")])]}),"instanceName":"1"}),"instanceName":"1"}),"instanceName":"1"});
            var Q141;
            Q141=makeQuery(id+"F9.opPattern","COPY",BODY,{"derivedFrom":makeQuery(id+"F4.opPattern","COPY",BODY,{"derivedFrom":makeQuery(id+"F3.opPattern","COPY",BODY,{"derivedFrom":makeQuery(id+"F1.opExtrude","SWEPT_BODY",BODY,{"disambiguationData":[OSD([sQuery(id+"F0.wireOp",EDGE,"E1.0"),sQuery(id+"F0.wireOp",EDGE,"E1.1"),sQuery(id+"F0.wireOp",EDGE,"E1.2"),sQuery(id+"F0.wireOp",EDGE,"E1.3"),sQuery(id+"F0.wireOp",EDGE,"E1.4"),sQuery(id+"F0.wireOp",EDGE,"E1.5"),sQuery(id+"F0.wireOp",EDGE,"E3.0"),sQuery(id+"F0.wireOp",EDGE,"E3.1"),sQuery(id+"F0.wireOp",EDGE,"E3.2"),sQuery(id+"F0.wireOp",EDGE,"E3.3"),sQuery(id+"F0.wireOp",EDGE,"E3.4"),sQuery(id+"F0.wireOp",EDGE,"E3.5")])]}),"instanceName":"1"}),"instanceName":"1"}),"instanceName":"1"});
            var Q142;
            Q142=makeQuery(id+"F9.opPattern","COPY",BODY,{"derivedFrom":makeQuery(id+"F4.opPattern","COPY",BODY,{"derivedFrom":makeQuery(id+"F1.opExtrude","SWEPT_BODY",BODY,{"disambiguationData":[OSD([sQuery(id+"F0.wireOp",EDGE,"E1.0"),sQuery(id+"F0.wireOp",EDGE,"E1.1"),sQuery(id+"F0.wireOp",EDGE,"E1.2"),sQuery(id+"F0.wireOp",EDGE,"E1.3"),sQuery(id+"F0.wireOp",EDGE,"E1.4"),sQuery(id+"F0.wireOp",EDGE,"E1.5"),sQuery(id+"F0.wireOp",EDGE,"E3.0"),sQuery(id+"F0.wireOp",EDGE,"E3.1"),sQuery(id+"F0.wireOp",EDGE,"E3.2"),sQuery(id+"F0.wireOp",EDGE,"E3.3"),sQuery(id+"F0.wireOp",EDGE,"E3.4"),sQuery(id+"F0.wireOp",EDGE,"E3.5")])]}),"instanceName":"1"}),"instanceName":"1"});
            var Q143;
            Q143=makeQuery(id+"F9.opPattern","COPY",BODY,{"derivedFrom":makeQuery(id+"F3.opPattern","COPY",BODY,{"derivedFrom":makeQuery(id+"F1.opExtrude","SWEPT_BODY",BODY,{"disambiguationData":[OSD([sQuery(id+"F0.wireOp",EDGE,"E1.0"),sQuery(id+"F0.wireOp",EDGE,"E1.1"),sQuery(id+"F0.wireOp",EDGE,"E1.2"),sQuery(id+"F0.wireOp",EDGE,"E1.3"),sQuery(id+"F0.wireOp",EDGE,"E1.4"),sQuery(id+"F0.wireOp",EDGE,"E1.5"),sQuery(id+"F0.wireOp",EDGE,"E3.0"),sQuery(id+"F0.wireOp",EDGE,"E3.1"),sQuery(id+"F0.wireOp",EDGE,"E3.2"),sQuery(id+"F0.wireOp",EDGE,"E3.3"),sQuery(id+"F0.wireOp",EDGE,"E3.4"),sQuery(id+"F0.wireOp",EDGE,"E3.5")])]}),"instanceName":"1"}),"instanceName":"1"});
            var Q144;
            Q144=makeQuery(id+"F9.opPattern","COPY",BODY,{"derivedFrom":makeQuery(id+"F1.opExtrude","SWEPT_BODY",BODY,{"disambiguationData":[OSD([sQuery(id+"F0.wireOp",EDGE,"E1.0"),sQuery(id+"F0.wireOp",EDGE,"E1.1"),sQuery(id+"F0.wireOp",EDGE,"E1.2"),sQuery(id+"F0.wireOp",EDGE,"E1.3"),sQuery(id+"F0.wireOp",EDGE,"E1.4"),sQuery(id+"F0.wireOp",EDGE,"E1.5"),sQuery(id+"F0.wireOp",EDGE,"E3.0"),sQuery(id+"F0.wireOp",EDGE,"E3.1"),sQuery(id+"F0.wireOp",EDGE,"E3.2"),sQuery(id+"F0.wireOp",EDGE,"E3.3"),sQuery(id+"F0.wireOp",EDGE,"E3.4"),sQuery(id+"F0.wireOp",EDGE,"E3.5")])]}),"instanceName":"1"});
            var Q145;
            Q145=makeQuery(id+"F8.opPattern","COPY",BODY,{"derivedFrom":makeQuery(id+"F7.opPattern","COPY",BODY,{"derivedFrom":makeQuery(id+"F6.opPattern","COPY",BODY,{"derivedFrom":makeQuery(id+"F5.opPattern","COPY",BODY,{"derivedFrom":makeQuery(id+"F4.opPattern","COPY",BODY,{"derivedFrom":makeQuery(id+"F1.opExtrude","SWEPT_BODY",BODY,{"disambiguationData":[OSD([sQuery(id+"F0.wireOp",EDGE,"E1.0"),sQuery(id+"F0.wireOp",EDGE,"E1.1"),sQuery(id+"F0.wireOp",EDGE,"E1.2"),sQuery(id+"F0.wireOp",EDGE,"E1.3"),sQuery(id+"F0.wireOp",EDGE,"E1.4"),sQuery(id+"F0.wireOp",EDGE,"E1.5"),sQuery(id+"F0.wireOp",EDGE,"E3.0"),sQuery(id+"F0.wireOp",EDGE,"E3.1"),sQuery(id+"F0.wireOp",EDGE,"E3.2"),sQuery(id+"F0.wireOp",EDGE,"E3.3"),sQuery(id+"F0.wireOp",EDGE,"E3.4"),sQuery(id+"F0.wireOp",EDGE,"E3.5")])]}),"instanceName":"1"}),"instanceName":"1"}),"instanceName":"1"}),"instanceName":"1"}),"instanceName":"1"});
            var Q146;
            Q146=makeQuery(id+"F8.opPattern","COPY",BODY,{"derivedFrom":makeQuery(id+"F7.opPattern","COPY",BODY,{"derivedFrom":makeQuery(id+"F6.opPattern","COPY",BODY,{"derivedFrom":makeQuery(id+"F4.opPattern","COPY",BODY,{"derivedFrom":makeQuery(id+"F3.opPattern","COPY",BODY,{"derivedFrom":makeQuery(id+"F1.opExtrude","SWEPT_BODY",BODY,{"disambiguationData":[OSD([sQuery(id+"F0.wireOp",EDGE,"E1.0"),sQuery(id+"F0.wireOp",EDGE,"E1.1"),sQuery(id+"F0.wireOp",EDGE,"E1.2"),sQuery(id+"F0.wireOp",EDGE,"E1.3"),sQuery(id+"F0.wireOp",EDGE,"E1.4"),sQuery(id+"F0.wireOp",EDGE,"E1.5"),sQuery(id+"F0.wireOp",EDGE,"E3.0"),sQuery(id+"F0.wireOp",EDGE,"E3.1"),sQuery(id+"F0.wireOp",EDGE,"E3.2"),sQuery(id+"F0.wireOp",EDGE,"E3.3"),sQuery(id+"F0.wireOp",EDGE,"E3.4"),sQuery(id+"F0.wireOp",EDGE,"E3.5")])]}),"instanceName":"1"}),"instanceName":"1"}),"instanceName":"1"}),"instanceName":"1"}),"instanceName":"1"});
            var Q147;
            Q147=makeQuery(id+"F8.opPattern","COPY",BODY,{"derivedFrom":makeQuery(id+"F7.opPattern","COPY",BODY,{"derivedFrom":makeQuery(id+"F6.opPattern","COPY",BODY,{"derivedFrom":makeQuery(id+"F4.opPattern","COPY",BODY,{"derivedFrom":makeQuery(id+"F1.opExtrude","SWEPT_BODY",BODY,{"disambiguationData":[OSD([sQuery(id+"F0.wireOp",EDGE,"E1.0"),sQuery(id+"F0.wireOp",EDGE,"E1.1"),sQuery(id+"F0.wireOp",EDGE,"E1.2"),sQuery(id+"F0.wireOp",EDGE,"E1.3"),sQuery(id+"F0.wireOp",EDGE,"E1.4"),sQuery(id+"F0.wireOp",EDGE,"E1.5"),sQuery(id+"F0.wireOp",EDGE,"E3.0"),sQuery(id+"F0.wireOp",EDGE,"E3.1"),sQuery(id+"F0.wireOp",EDGE,"E3.2"),sQuery(id+"F0.wireOp",EDGE,"E3.3"),sQuery(id+"F0.wireOp",EDGE,"E3.4"),sQuery(id+"F0.wireOp",EDGE,"E3.5")])]}),"instanceName":"1"}),"instanceName":"1"}),"instanceName":"1"}),"instanceName":"1"});
            var Q148;
            Q148=makeQuery(id+"F8.opPattern","COPY",BODY,{"derivedFrom":makeQuery(id+"F7.opPattern","COPY",BODY,{"derivedFrom":makeQuery(id+"F6.opPattern","COPY",BODY,{"derivedFrom":makeQuery(id+"F3.opPattern","COPY",BODY,{"derivedFrom":makeQuery(id+"F1.opExtrude","SWEPT_BODY",BODY,{"disambiguationData":[OSD([sQuery(id+"F0.wireOp",EDGE,"E1.0"),sQuery(id+"F0.wireOp",EDGE,"E1.1"),sQuery(id+"F0.wireOp",EDGE,"E1.2"),sQuery(id+"F0.wireOp",EDGE,"E1.3"),sQuery(id+"F0.wireOp",EDGE,"E1.4"),sQuery(id+"F0.wireOp",EDGE,"E1.5"),sQuery(id+"F0.wireOp",EDGE,"E3.0"),sQuery(id+"F0.wireOp",EDGE,"E3.1"),sQuery(id+"F0.wireOp",EDGE,"E3.2"),sQuery(id+"F0.wireOp",EDGE,"E3.3"),sQuery(id+"F0.wireOp",EDGE,"E3.4"),sQuery(id+"F0.wireOp",EDGE,"E3.5")])]}),"instanceName":"1"}),"instanceName":"1"}),"instanceName":"1"}),"instanceName":"1"});
            var Q149;
            Q149=makeQuery(id+"F8.opPattern","COPY",BODY,{"derivedFrom":makeQuery(id+"F7.opPattern","COPY",BODY,{"derivedFrom":makeQuery(id+"F6.opPattern","COPY",BODY,{"derivedFrom":makeQuery(id+"F1.opExtrude","SWEPT_BODY",BODY,{"disambiguationData":[OSD([sQuery(id+"F0.wireOp",EDGE,"E1.0"),sQuery(id+"F0.wireOp",EDGE,"E1.1"),sQuery(id+"F0.wireOp",EDGE,"E1.2"),sQuery(id+"F0.wireOp",EDGE,"E1.3"),sQuery(id+"F0.wireOp",EDGE,"E1.4"),sQuery(id+"F0.wireOp",EDGE,"E1.5"),sQuery(id+"F0.wireOp",EDGE,"E3.0"),sQuery(id+"F0.wireOp",EDGE,"E3.1"),sQuery(id+"F0.wireOp",EDGE,"E3.2"),sQuery(id+"F0.wireOp",EDGE,"E3.3"),sQuery(id+"F0.wireOp",EDGE,"E3.4"),sQuery(id+"F0.wireOp",EDGE,"E3.5")])]}),"instanceName":"1"}),"instanceName":"1"}),"instanceName":"1"});
            var Q150;
            Q150=makeQuery(id+"F8.opPattern","COPY",BODY,{"derivedFrom":makeQuery(id+"F7.opPattern","COPY",BODY,{"derivedFrom":makeQuery(id+"F5.opPattern","COPY",BODY,{"derivedFrom":makeQuery(id+"F4.opPattern","COPY",BODY,{"derivedFrom":makeQuery(id+"F3.opPattern","COPY",BODY,{"derivedFrom":makeQuery(id+"F1.opExtrude","SWEPT_BODY",BODY,{"disambiguationData":[OSD([sQuery(id+"F0.wireOp",EDGE,"E1.0"),sQuery(id+"F0.wireOp",EDGE,"E1.1"),sQuery(id+"F0.wireOp",EDGE,"E1.2"),sQuery(id+"F0.wireOp",EDGE,"E1.3"),sQuery(id+"F0.wireOp",EDGE,"E1.4"),sQuery(id+"F0.wireOp",EDGE,"E1.5"),sQuery(id+"F0.wireOp",EDGE,"E3.0"),sQuery(id+"F0.wireOp",EDGE,"E3.1"),sQuery(id+"F0.wireOp",EDGE,"E3.2"),sQuery(id+"F0.wireOp",EDGE,"E3.3"),sQuery(id+"F0.wireOp",EDGE,"E3.4"),sQuery(id+"F0.wireOp",EDGE,"E3.5")])]}),"instanceName":"1"}),"instanceName":"1"}),"instanceName":"1"}),"instanceName":"1"}),"instanceName":"1"});
            var Q151;
            Q151=makeQuery(id+"F8.opPattern","COPY",BODY,{"derivedFrom":makeQuery(id+"F7.opPattern","COPY",BODY,{"derivedFrom":makeQuery(id+"F5.opPattern","COPY",BODY,{"derivedFrom":makeQuery(id+"F4.opPattern","COPY",BODY,{"derivedFrom":makeQuery(id+"F1.opExtrude","SWEPT_BODY",BODY,{"disambiguationData":[OSD([sQuery(id+"F0.wireOp",EDGE,"E1.0"),sQuery(id+"F0.wireOp",EDGE,"E1.1"),sQuery(id+"F0.wireOp",EDGE,"E1.2"),sQuery(id+"F0.wireOp",EDGE,"E1.3"),sQuery(id+"F0.wireOp",EDGE,"E1.4"),sQuery(id+"F0.wireOp",EDGE,"E1.5"),sQuery(id+"F0.wireOp",EDGE,"E3.0"),sQuery(id+"F0.wireOp",EDGE,"E3.1"),sQuery(id+"F0.wireOp",EDGE,"E3.2"),sQuery(id+"F0.wireOp",EDGE,"E3.3"),sQuery(id+"F0.wireOp",EDGE,"E3.4"),sQuery(id+"F0.wireOp",EDGE,"E3.5")])]}),"instanceName":"1"}),"instanceName":"1"}),"instanceName":"1"}),"instanceName":"1"});
            var Q152;
            Q152=makeQuery(id+"F8.opPattern","COPY",BODY,{"derivedFrom":makeQuery(id+"F7.opPattern","COPY",BODY,{"derivedFrom":makeQuery(id+"F4.opPattern","COPY",BODY,{"derivedFrom":makeQuery(id+"F3.opPattern","COPY",BODY,{"derivedFrom":makeQuery(id+"F1.opExtrude","SWEPT_BODY",BODY,{"disambiguationData":[OSD([sQuery(id+"F0.wireOp",EDGE,"E1.0"),sQuery(id+"F0.wireOp",EDGE,"E1.1"),sQuery(id+"F0.wireOp",EDGE,"E1.2"),sQuery(id+"F0.wireOp",EDGE,"E1.3"),sQuery(id+"F0.wireOp",EDGE,"E1.4"),sQuery(id+"F0.wireOp",EDGE,"E1.5"),sQuery(id+"F0.wireOp",EDGE,"E3.0"),sQuery(id+"F0.wireOp",EDGE,"E3.1"),sQuery(id+"F0.wireOp",EDGE,"E3.2"),sQuery(id+"F0.wireOp",EDGE,"E3.3"),sQuery(id+"F0.wireOp",EDGE,"E3.4"),sQuery(id+"F0.wireOp",EDGE,"E3.5")])]}),"instanceName":"1"}),"instanceName":"1"}),"instanceName":"1"}),"instanceName":"1"});
            var Q153;
            Q153=makeQuery(id+"F8.opPattern","COPY",BODY,{"derivedFrom":makeQuery(id+"F7.opPattern","COPY",BODY,{"derivedFrom":makeQuery(id+"F4.opPattern","COPY",BODY,{"derivedFrom":makeQuery(id+"F1.opExtrude","SWEPT_BODY",BODY,{"disambiguationData":[OSD([sQuery(id+"F0.wireOp",EDGE,"E1.0"),sQuery(id+"F0.wireOp",EDGE,"E1.1"),sQuery(id+"F0.wireOp",EDGE,"E1.2"),sQuery(id+"F0.wireOp",EDGE,"E1.3"),sQuery(id+"F0.wireOp",EDGE,"E1.4"),sQuery(id+"F0.wireOp",EDGE,"E1.5"),sQuery(id+"F0.wireOp",EDGE,"E3.0"),sQuery(id+"F0.wireOp",EDGE,"E3.1"),sQuery(id+"F0.wireOp",EDGE,"E3.2"),sQuery(id+"F0.wireOp",EDGE,"E3.3"),sQuery(id+"F0.wireOp",EDGE,"E3.4"),sQuery(id+"F0.wireOp",EDGE,"E3.5")])]}),"instanceName":"1"}),"instanceName":"1"}),"instanceName":"1"});
            var Q154;
            Q154=makeQuery(id+"F8.opPattern","COPY",BODY,{"derivedFrom":makeQuery(id+"F7.opPattern","COPY",BODY,{"derivedFrom":makeQuery(id+"F3.opPattern","COPY",BODY,{"derivedFrom":makeQuery(id+"F1.opExtrude","SWEPT_BODY",BODY,{"disambiguationData":[OSD([sQuery(id+"F0.wireOp",EDGE,"E1.0"),sQuery(id+"F0.wireOp",EDGE,"E1.1"),sQuery(id+"F0.wireOp",EDGE,"E1.2"),sQuery(id+"F0.wireOp",EDGE,"E1.3"),sQuery(id+"F0.wireOp",EDGE,"E1.4"),sQuery(id+"F0.wireOp",EDGE,"E1.5"),sQuery(id+"F0.wireOp",EDGE,"E3.0"),sQuery(id+"F0.wireOp",EDGE,"E3.1"),sQuery(id+"F0.wireOp",EDGE,"E3.2"),sQuery(id+"F0.wireOp",EDGE,"E3.3"),sQuery(id+"F0.wireOp",EDGE,"E3.4"),sQuery(id+"F0.wireOp",EDGE,"E3.5")])]}),"instanceName":"1"}),"instanceName":"1"}),"instanceName":"1"});
            var Q155;
            Q155=makeQuery(id+"F8.opPattern","COPY",BODY,{"derivedFrom":makeQuery(id+"F7.opPattern","COPY",BODY,{"derivedFrom":makeQuery(id+"F1.opExtrude","SWEPT_BODY",BODY,{"disambiguationData":[OSD([sQuery(id+"F0.wireOp",EDGE,"E1.0"),sQuery(id+"F0.wireOp",EDGE,"E1.1"),sQuery(id+"F0.wireOp",EDGE,"E1.2"),sQuery(id+"F0.wireOp",EDGE,"E1.3"),sQuery(id+"F0.wireOp",EDGE,"E1.4"),sQuery(id+"F0.wireOp",EDGE,"E1.5"),sQuery(id+"F0.wireOp",EDGE,"E3.0"),sQuery(id+"F0.wireOp",EDGE,"E3.1"),sQuery(id+"F0.wireOp",EDGE,"E3.2"),sQuery(id+"F0.wireOp",EDGE,"E3.3"),sQuery(id+"F0.wireOp",EDGE,"E3.4"),sQuery(id+"F0.wireOp",EDGE,"E3.5")])]}),"instanceName":"1"}),"instanceName":"1"});
            var Q156;
            Q156=makeQuery(id+"F8.opPattern","COPY",BODY,{"derivedFrom":makeQuery(id+"F6.opPattern","COPY",BODY,{"derivedFrom":makeQuery(id+"F5.opPattern","COPY",BODY,{"derivedFrom":makeQuery(id+"F4.opPattern","COPY",BODY,{"derivedFrom":makeQuery(id+"F3.opPattern","COPY",BODY,{"derivedFrom":makeQuery(id+"F1.opExtrude","SWEPT_BODY",BODY,{"disambiguationData":[OSD([sQuery(id+"F0.wireOp",EDGE,"E1.0"),sQuery(id+"F0.wireOp",EDGE,"E1.1"),sQuery(id+"F0.wireOp",EDGE,"E1.2"),sQuery(id+"F0.wireOp",EDGE,"E1.3"),sQuery(id+"F0.wireOp",EDGE,"E1.4"),sQuery(id+"F0.wireOp",EDGE,"E1.5"),sQuery(id+"F0.wireOp",EDGE,"E3.0"),sQuery(id+"F0.wireOp",EDGE,"E3.1"),sQuery(id+"F0.wireOp",EDGE,"E3.2"),sQuery(id+"F0.wireOp",EDGE,"E3.3"),sQuery(id+"F0.wireOp",EDGE,"E3.4"),sQuery(id+"F0.wireOp",EDGE,"E3.5")])]}),"instanceName":"1"}),"instanceName":"1"}),"instanceName":"1"}),"instanceName":"1"}),"instanceName":"1"});
            var Q157;
            Q157=makeQuery(id+"F8.opPattern","COPY",BODY,{"derivedFrom":makeQuery(id+"F6.opPattern","COPY",BODY,{"derivedFrom":makeQuery(id+"F5.opPattern","COPY",BODY,{"derivedFrom":makeQuery(id+"F4.opPattern","COPY",BODY,{"derivedFrom":makeQuery(id+"F1.opExtrude","SWEPT_BODY",BODY,{"disambiguationData":[OSD([sQuery(id+"F0.wireOp",EDGE,"E1.0"),sQuery(id+"F0.wireOp",EDGE,"E1.1"),sQuery(id+"F0.wireOp",EDGE,"E1.2"),sQuery(id+"F0.wireOp",EDGE,"E1.3"),sQuery(id+"F0.wireOp",EDGE,"E1.4"),sQuery(id+"F0.wireOp",EDGE,"E1.5"),sQuery(id+"F0.wireOp",EDGE,"E3.0"),sQuery(id+"F0.wireOp",EDGE,"E3.1"),sQuery(id+"F0.wireOp",EDGE,"E3.2"),sQuery(id+"F0.wireOp",EDGE,"E3.3"),sQuery(id+"F0.wireOp",EDGE,"E3.4"),sQuery(id+"F0.wireOp",EDGE,"E3.5")])]}),"instanceName":"1"}),"instanceName":"1"}),"instanceName":"1"}),"instanceName":"1"});
            var Q158;
            Q158=makeQuery(id+"F8.opPattern","COPY",BODY,{"derivedFrom":makeQuery(id+"F6.opPattern","COPY",BODY,{"derivedFrom":makeQuery(id+"F4.opPattern","COPY",BODY,{"derivedFrom":makeQuery(id+"F3.opPattern","COPY",BODY,{"derivedFrom":makeQuery(id+"F1.opExtrude","SWEPT_BODY",BODY,{"disambiguationData":[OSD([sQuery(id+"F0.wireOp",EDGE,"E1.0"),sQuery(id+"F0.wireOp",EDGE,"E1.1"),sQuery(id+"F0.wireOp",EDGE,"E1.2"),sQuery(id+"F0.wireOp",EDGE,"E1.3"),sQuery(id+"F0.wireOp",EDGE,"E1.4"),sQuery(id+"F0.wireOp",EDGE,"E1.5"),sQuery(id+"F0.wireOp",EDGE,"E3.0"),sQuery(id+"F0.wireOp",EDGE,"E3.1"),sQuery(id+"F0.wireOp",EDGE,"E3.2"),sQuery(id+"F0.wireOp",EDGE,"E3.3"),sQuery(id+"F0.wireOp",EDGE,"E3.4"),sQuery(id+"F0.wireOp",EDGE,"E3.5")])]}),"instanceName":"1"}),"instanceName":"1"}),"instanceName":"1"}),"instanceName":"1"});
            var Q159;
            Q159=makeQuery(id+"F8.opPattern","COPY",BODY,{"derivedFrom":makeQuery(id+"F6.opPattern","COPY",BODY,{"derivedFrom":makeQuery(id+"F4.opPattern","COPY",BODY,{"derivedFrom":makeQuery(id+"F1.opExtrude","SWEPT_BODY",BODY,{"disambiguationData":[OSD([sQuery(id+"F0.wireOp",EDGE,"E1.0"),sQuery(id+"F0.wireOp",EDGE,"E1.1"),sQuery(id+"F0.wireOp",EDGE,"E1.2"),sQuery(id+"F0.wireOp",EDGE,"E1.3"),sQuery(id+"F0.wireOp",EDGE,"E1.4"),sQuery(id+"F0.wireOp",EDGE,"E1.5"),sQuery(id+"F0.wireOp",EDGE,"E3.0"),sQuery(id+"F0.wireOp",EDGE,"E3.1"),sQuery(id+"F0.wireOp",EDGE,"E3.2"),sQuery(id+"F0.wireOp",EDGE,"E3.3"),sQuery(id+"F0.wireOp",EDGE,"E3.4"),sQuery(id+"F0.wireOp",EDGE,"E3.5")])]}),"instanceName":"1"}),"instanceName":"1"}),"instanceName":"1"});
            var Q160;
            Q160=makeQuery(id+"F8.opPattern","COPY",BODY,{"derivedFrom":makeQuery(id+"F6.opPattern","COPY",BODY,{"derivedFrom":makeQuery(id+"F3.opPattern","COPY",BODY,{"derivedFrom":makeQuery(id+"F1.opExtrude","SWEPT_BODY",BODY,{"disambiguationData":[OSD([sQuery(id+"F0.wireOp",EDGE,"E1.0"),sQuery(id+"F0.wireOp",EDGE,"E1.1"),sQuery(id+"F0.wireOp",EDGE,"E1.2"),sQuery(id+"F0.wireOp",EDGE,"E1.3"),sQuery(id+"F0.wireOp",EDGE,"E1.4"),sQuery(id+"F0.wireOp",EDGE,"E1.5"),sQuery(id+"F0.wireOp",EDGE,"E3.0"),sQuery(id+"F0.wireOp",EDGE,"E3.1"),sQuery(id+"F0.wireOp",EDGE,"E3.2"),sQuery(id+"F0.wireOp",EDGE,"E3.3"),sQuery(id+"F0.wireOp",EDGE,"E3.4"),sQuery(id+"F0.wireOp",EDGE,"E3.5")])]}),"instanceName":"1"}),"instanceName":"1"}),"instanceName":"1"});
            var Q161;
            Q161=makeQuery(id+"F8.opPattern","COPY",BODY,{"derivedFrom":makeQuery(id+"F6.opPattern","COPY",BODY,{"derivedFrom":makeQuery(id+"F1.opExtrude","SWEPT_BODY",BODY,{"disambiguationData":[OSD([sQuery(id+"F0.wireOp",EDGE,"E1.0"),sQuery(id+"F0.wireOp",EDGE,"E1.1"),sQuery(id+"F0.wireOp",EDGE,"E1.2"),sQuery(id+"F0.wireOp",EDGE,"E1.3"),sQuery(id+"F0.wireOp",EDGE,"E1.4"),sQuery(id+"F0.wireOp",EDGE,"E1.5"),sQuery(id+"F0.wireOp",EDGE,"E3.0"),sQuery(id+"F0.wireOp",EDGE,"E3.1"),sQuery(id+"F0.wireOp",EDGE,"E3.2"),sQuery(id+"F0.wireOp",EDGE,"E3.3"),sQuery(id+"F0.wireOp",EDGE,"E3.4"),sQuery(id+"F0.wireOp",EDGE,"E3.5")])]}),"instanceName":"1"}),"instanceName":"1"});
            var Q162;
            Q162=makeQuery(id+"F8.opPattern","COPY",BODY,{"derivedFrom":makeQuery(id+"F5.opPattern","COPY",BODY,{"derivedFrom":makeQuery(id+"F4.opPattern","COPY",BODY,{"derivedFrom":makeQuery(id+"F3.opPattern","COPY",BODY,{"derivedFrom":makeQuery(id+"F1.opExtrude","SWEPT_BODY",BODY,{"disambiguationData":[OSD([sQuery(id+"F0.wireOp",EDGE,"E1.0"),sQuery(id+"F0.wireOp",EDGE,"E1.1"),sQuery(id+"F0.wireOp",EDGE,"E1.2"),sQuery(id+"F0.wireOp",EDGE,"E1.3"),sQuery(id+"F0.wireOp",EDGE,"E1.4"),sQuery(id+"F0.wireOp",EDGE,"E1.5"),sQuery(id+"F0.wireOp",EDGE,"E3.0"),sQuery(id+"F0.wireOp",EDGE,"E3.1"),sQuery(id+"F0.wireOp",EDGE,"E3.2"),sQuery(id+"F0.wireOp",EDGE,"E3.3"),sQuery(id+"F0.wireOp",EDGE,"E3.4"),sQuery(id+"F0.wireOp",EDGE,"E3.5")])]}),"instanceName":"1"}),"instanceName":"1"}),"instanceName":"1"}),"instanceName":"1"});
            var Q163;
            Q163=makeQuery(id+"F8.opPattern","COPY",BODY,{"derivedFrom":makeQuery(id+"F5.opPattern","COPY",BODY,{"derivedFrom":makeQuery(id+"F4.opPattern","COPY",BODY,{"derivedFrom":makeQuery(id+"F1.opExtrude","SWEPT_BODY",BODY,{"disambiguationData":[OSD([sQuery(id+"F0.wireOp",EDGE,"E1.0"),sQuery(id+"F0.wireOp",EDGE,"E1.1"),sQuery(id+"F0.wireOp",EDGE,"E1.2"),sQuery(id+"F0.wireOp",EDGE,"E1.3"),sQuery(id+"F0.wireOp",EDGE,"E1.4"),sQuery(id+"F0.wireOp",EDGE,"E1.5"),sQuery(id+"F0.wireOp",EDGE,"E3.0"),sQuery(id+"F0.wireOp",EDGE,"E3.1"),sQuery(id+"F0.wireOp",EDGE,"E3.2"),sQuery(id+"F0.wireOp",EDGE,"E3.3"),sQuery(id+"F0.wireOp",EDGE,"E3.4"),sQuery(id+"F0.wireOp",EDGE,"E3.5")])]}),"instanceName":"1"}),"instanceName":"1"}),"instanceName":"1"});
            var Q164;
            Q164=makeQuery(id+"F8.opPattern","COPY",BODY,{"derivedFrom":makeQuery(id+"F4.opPattern","COPY",BODY,{"derivedFrom":makeQuery(id+"F3.opPattern","COPY",BODY,{"derivedFrom":makeQuery(id+"F1.opExtrude","SWEPT_BODY",BODY,{"disambiguationData":[OSD([sQuery(id+"F0.wireOp",EDGE,"E1.0"),sQuery(id+"F0.wireOp",EDGE,"E1.1"),sQuery(id+"F0.wireOp",EDGE,"E1.2"),sQuery(id+"F0.wireOp",EDGE,"E1.3"),sQuery(id+"F0.wireOp",EDGE,"E1.4"),sQuery(id+"F0.wireOp",EDGE,"E1.5"),sQuery(id+"F0.wireOp",EDGE,"E3.0"),sQuery(id+"F0.wireOp",EDGE,"E3.1"),sQuery(id+"F0.wireOp",EDGE,"E3.2"),sQuery(id+"F0.wireOp",EDGE,"E3.3"),sQuery(id+"F0.wireOp",EDGE,"E3.4"),sQuery(id+"F0.wireOp",EDGE,"E3.5")])]}),"instanceName":"1"}),"instanceName":"1"}),"instanceName":"1"});
            var Q165;
            Q165=makeQuery(id+"F8.opPattern","COPY",BODY,{"derivedFrom":makeQuery(id+"F4.opPattern","COPY",BODY,{"derivedFrom":makeQuery(id+"F1.opExtrude","SWEPT_BODY",BODY,{"disambiguationData":[OSD([sQuery(id+"F0.wireOp",EDGE,"E1.0"),sQuery(id+"F0.wireOp",EDGE,"E1.1"),sQuery(id+"F0.wireOp",EDGE,"E1.2"),sQuery(id+"F0.wireOp",EDGE,"E1.3"),sQuery(id+"F0.wireOp",EDGE,"E1.4"),sQuery(id+"F0.wireOp",EDGE,"E1.5"),sQuery(id+"F0.wireOp",EDGE,"E3.0"),sQuery(id+"F0.wireOp",EDGE,"E3.1"),sQuery(id+"F0.wireOp",EDGE,"E3.2"),sQuery(id+"F0.wireOp",EDGE,"E3.3"),sQuery(id+"F0.wireOp",EDGE,"E3.4"),sQuery(id+"F0.wireOp",EDGE,"E3.5")])]}),"instanceName":"1"}),"instanceName":"1"});
            var Q166;
            Q166=makeQuery(id+"F8.opPattern","COPY",BODY,{"derivedFrom":makeQuery(id+"F3.opPattern","COPY",BODY,{"derivedFrom":makeQuery(id+"F1.opExtrude","SWEPT_BODY",BODY,{"disambiguationData":[OSD([sQuery(id+"F0.wireOp",EDGE,"E1.0"),sQuery(id+"F0.wireOp",EDGE,"E1.1"),sQuery(id+"F0.wireOp",EDGE,"E1.2"),sQuery(id+"F0.wireOp",EDGE,"E1.3"),sQuery(id+"F0.wireOp",EDGE,"E1.4"),sQuery(id+"F0.wireOp",EDGE,"E1.5"),sQuery(id+"F0.wireOp",EDGE,"E3.0"),sQuery(id+"F0.wireOp",EDGE,"E3.1"),sQuery(id+"F0.wireOp",EDGE,"E3.2"),sQuery(id+"F0.wireOp",EDGE,"E3.3"),sQuery(id+"F0.wireOp",EDGE,"E3.4"),sQuery(id+"F0.wireOp",EDGE,"E3.5")])]}),"instanceName":"1"}),"instanceName":"1"});
            var Q167;
            Q167=makeQuery(id+"F8.opPattern","COPY",BODY,{"derivedFrom":makeQuery(id+"F1.opExtrude","SWEPT_BODY",BODY,{"disambiguationData":[OSD([sQuery(id+"F0.wireOp",EDGE,"E1.0"),sQuery(id+"F0.wireOp",EDGE,"E1.1"),sQuery(id+"F0.wireOp",EDGE,"E1.2"),sQuery(id+"F0.wireOp",EDGE,"E1.3"),sQuery(id+"F0.wireOp",EDGE,"E1.4"),sQuery(id+"F0.wireOp",EDGE,"E1.5"),sQuery(id+"F0.wireOp",EDGE,"E3.0"),sQuery(id+"F0.wireOp",EDGE,"E3.1"),sQuery(id+"F0.wireOp",EDGE,"E3.2"),sQuery(id+"F0.wireOp",EDGE,"E3.3"),sQuery(id+"F0.wireOp",EDGE,"E3.4"),sQuery(id+"F0.wireOp",EDGE,"E3.5")])]}),"instanceName":"1"});
            var Q168;
            Q168=makeQuery(id+"F7.opPattern","COPY",BODY,{"derivedFrom":makeQuery(id+"F6.opPattern","COPY",BODY,{"derivedFrom":makeQuery(id+"F5.opPattern","COPY",BODY,{"derivedFrom":makeQuery(id+"F4.opPattern","COPY",BODY,{"derivedFrom":makeQuery(id+"F3.opPattern","COPY",BODY,{"derivedFrom":makeQuery(id+"F1.opExtrude","SWEPT_BODY",BODY,{"disambiguationData":[OSD([sQuery(id+"F0.wireOp",EDGE,"E1.0"),sQuery(id+"F0.wireOp",EDGE,"E1.1"),sQuery(id+"F0.wireOp",EDGE,"E1.2"),sQuery(id+"F0.wireOp",EDGE,"E1.3"),sQuery(id+"F0.wireOp",EDGE,"E1.4"),sQuery(id+"F0.wireOp",EDGE,"E1.5"),sQuery(id+"F0.wireOp",EDGE,"E3.0"),sQuery(id+"F0.wireOp",EDGE,"E3.1"),sQuery(id+"F0.wireOp",EDGE,"E3.2"),sQuery(id+"F0.wireOp",EDGE,"E3.3"),sQuery(id+"F0.wireOp",EDGE,"E3.4"),sQuery(id+"F0.wireOp",EDGE,"E3.5")])]}),"instanceName":"1"}),"instanceName":"1"}),"instanceName":"1"}),"instanceName":"1"}),"instanceName":"1"});
            var Q169;
            Q169=makeQuery(id+"F7.opPattern","COPY",BODY,{"derivedFrom":makeQuery(id+"F6.opPattern","COPY",BODY,{"derivedFrom":makeQuery(id+"F5.opPattern","COPY",BODY,{"derivedFrom":makeQuery(id+"F4.opPattern","COPY",BODY,{"derivedFrom":makeQuery(id+"F1.opExtrude","SWEPT_BODY",BODY,{"disambiguationData":[OSD([sQuery(id+"F0.wireOp",EDGE,"E1.0"),sQuery(id+"F0.wireOp",EDGE,"E1.1"),sQuery(id+"F0.wireOp",EDGE,"E1.2"),sQuery(id+"F0.wireOp",EDGE,"E1.3"),sQuery(id+"F0.wireOp",EDGE,"E1.4"),sQuery(id+"F0.wireOp",EDGE,"E1.5"),sQuery(id+"F0.wireOp",EDGE,"E3.0"),sQuery(id+"F0.wireOp",EDGE,"E3.1"),sQuery(id+"F0.wireOp",EDGE,"E3.2"),sQuery(id+"F0.wireOp",EDGE,"E3.3"),sQuery(id+"F0.wireOp",EDGE,"E3.4"),sQuery(id+"F0.wireOp",EDGE,"E3.5")])]}),"instanceName":"1"}),"instanceName":"1"}),"instanceName":"1"}),"instanceName":"1"});
            var Q170;
            Q170=makeQuery(id+"F7.opPattern","COPY",BODY,{"derivedFrom":makeQuery(id+"F6.opPattern","COPY",BODY,{"derivedFrom":makeQuery(id+"F4.opPattern","COPY",BODY,{"derivedFrom":makeQuery(id+"F3.opPattern","COPY",BODY,{"derivedFrom":makeQuery(id+"F1.opExtrude","SWEPT_BODY",BODY,{"disambiguationData":[OSD([sQuery(id+"F0.wireOp",EDGE,"E1.0"),sQuery(id+"F0.wireOp",EDGE,"E1.1"),sQuery(id+"F0.wireOp",EDGE,"E1.2"),sQuery(id+"F0.wireOp",EDGE,"E1.3"),sQuery(id+"F0.wireOp",EDGE,"E1.4"),sQuery(id+"F0.wireOp",EDGE,"E1.5"),sQuery(id+"F0.wireOp",EDGE,"E3.0"),sQuery(id+"F0.wireOp",EDGE,"E3.1"),sQuery(id+"F0.wireOp",EDGE,"E3.2"),sQuery(id+"F0.wireOp",EDGE,"E3.3"),sQuery(id+"F0.wireOp",EDGE,"E3.4"),sQuery(id+"F0.wireOp",EDGE,"E3.5")])]}),"instanceName":"1"}),"instanceName":"1"}),"instanceName":"1"}),"instanceName":"1"});
            var Q171;
            Q171=makeQuery(id+"F7.opPattern","COPY",BODY,{"derivedFrom":makeQuery(id+"F6.opPattern","COPY",BODY,{"derivedFrom":makeQuery(id+"F4.opPattern","COPY",BODY,{"derivedFrom":makeQuery(id+"F1.opExtrude","SWEPT_BODY",BODY,{"disambiguationData":[OSD([sQuery(id+"F0.wireOp",EDGE,"E1.0"),sQuery(id+"F0.wireOp",EDGE,"E1.1"),sQuery(id+"F0.wireOp",EDGE,"E1.2"),sQuery(id+"F0.wireOp",EDGE,"E1.3"),sQuery(id+"F0.wireOp",EDGE,"E1.4"),sQuery(id+"F0.wireOp",EDGE,"E1.5"),sQuery(id+"F0.wireOp",EDGE,"E3.0"),sQuery(id+"F0.wireOp",EDGE,"E3.1"),sQuery(id+"F0.wireOp",EDGE,"E3.2"),sQuery(id+"F0.wireOp",EDGE,"E3.3"),sQuery(id+"F0.wireOp",EDGE,"E3.4"),sQuery(id+"F0.wireOp",EDGE,"E3.5")])]}),"instanceName":"1"}),"instanceName":"1"}),"instanceName":"1"});
            var Q172;
            Q172=makeQuery(id+"F7.opPattern","COPY",BODY,{"derivedFrom":makeQuery(id+"F6.opPattern","COPY",BODY,{"derivedFrom":makeQuery(id+"F3.opPattern","COPY",BODY,{"derivedFrom":makeQuery(id+"F1.opExtrude","SWEPT_BODY",BODY,{"disambiguationData":[OSD([sQuery(id+"F0.wireOp",EDGE,"E1.0"),sQuery(id+"F0.wireOp",EDGE,"E1.1"),sQuery(id+"F0.wireOp",EDGE,"E1.2"),sQuery(id+"F0.wireOp",EDGE,"E1.3"),sQuery(id+"F0.wireOp",EDGE,"E1.4"),sQuery(id+"F0.wireOp",EDGE,"E1.5"),sQuery(id+"F0.wireOp",EDGE,"E3.0"),sQuery(id+"F0.wireOp",EDGE,"E3.1"),sQuery(id+"F0.wireOp",EDGE,"E3.2"),sQuery(id+"F0.wireOp",EDGE,"E3.3"),sQuery(id+"F0.wireOp",EDGE,"E3.4"),sQuery(id+"F0.wireOp",EDGE,"E3.5")])]}),"instanceName":"1"}),"instanceName":"1"}),"instanceName":"1"});
            var Q173;
            Q173=makeQuery(id+"F7.opPattern","COPY",BODY,{"derivedFrom":makeQuery(id+"F6.opPattern","COPY",BODY,{"derivedFrom":makeQuery(id+"F1.opExtrude","SWEPT_BODY",BODY,{"disambiguationData":[OSD([sQuery(id+"F0.wireOp",EDGE,"E1.0"),sQuery(id+"F0.wireOp",EDGE,"E1.1"),sQuery(id+"F0.wireOp",EDGE,"E1.2"),sQuery(id+"F0.wireOp",EDGE,"E1.3"),sQuery(id+"F0.wireOp",EDGE,"E1.4"),sQuery(id+"F0.wireOp",EDGE,"E1.5"),sQuery(id+"F0.wireOp",EDGE,"E3.0"),sQuery(id+"F0.wireOp",EDGE,"E3.1"),sQuery(id+"F0.wireOp",EDGE,"E3.2"),sQuery(id+"F0.wireOp",EDGE,"E3.3"),sQuery(id+"F0.wireOp",EDGE,"E3.4"),sQuery(id+"F0.wireOp",EDGE,"E3.5")])]}),"instanceName":"1"}),"instanceName":"1"});
            var Q174;
            Q174=makeQuery(id+"F7.opPattern","COPY",BODY,{"derivedFrom":makeQuery(id+"F5.opPattern","COPY",BODY,{"derivedFrom":makeQuery(id+"F4.opPattern","COPY",BODY,{"derivedFrom":makeQuery(id+"F3.opPattern","COPY",BODY,{"derivedFrom":makeQuery(id+"F1.opExtrude","SWEPT_BODY",BODY,{"disambiguationData":[OSD([sQuery(id+"F0.wireOp",EDGE,"E1.0"),sQuery(id+"F0.wireOp",EDGE,"E1.1"),sQuery(id+"F0.wireOp",EDGE,"E1.2"),sQuery(id+"F0.wireOp",EDGE,"E1.3"),sQuery(id+"F0.wireOp",EDGE,"E1.4"),sQuery(id+"F0.wireOp",EDGE,"E1.5"),sQuery(id+"F0.wireOp",EDGE,"E3.0"),sQuery(id+"F0.wireOp",EDGE,"E3.1"),sQuery(id+"F0.wireOp",EDGE,"E3.2"),sQuery(id+"F0.wireOp",EDGE,"E3.3"),sQuery(id+"F0.wireOp",EDGE,"E3.4"),sQuery(id+"F0.wireOp",EDGE,"E3.5")])]}),"instanceName":"1"}),"instanceName":"1"}),"instanceName":"1"}),"instanceName":"1"});
            var Q175;
            Q175=makeQuery(id+"F7.opPattern","COPY",BODY,{"derivedFrom":makeQuery(id+"F5.opPattern","COPY",BODY,{"derivedFrom":makeQuery(id+"F4.opPattern","COPY",BODY,{"derivedFrom":makeQuery(id+"F1.opExtrude","SWEPT_BODY",BODY,{"disambiguationData":[OSD([sQuery(id+"F0.wireOp",EDGE,"E1.0"),sQuery(id+"F0.wireOp",EDGE,"E1.1"),sQuery(id+"F0.wireOp",EDGE,"E1.2"),sQuery(id+"F0.wireOp",EDGE,"E1.3"),sQuery(id+"F0.wireOp",EDGE,"E1.4"),sQuery(id+"F0.wireOp",EDGE,"E1.5"),sQuery(id+"F0.wireOp",EDGE,"E3.0"),sQuery(id+"F0.wireOp",EDGE,"E3.1"),sQuery(id+"F0.wireOp",EDGE,"E3.2"),sQuery(id+"F0.wireOp",EDGE,"E3.3"),sQuery(id+"F0.wireOp",EDGE,"E3.4"),sQuery(id+"F0.wireOp",EDGE,"E3.5")])]}),"instanceName":"1"}),"instanceName":"1"}),"instanceName":"1"});
            var Q176;
            Q176=makeQuery(id+"F7.opPattern","COPY",BODY,{"derivedFrom":makeQuery(id+"F4.opPattern","COPY",BODY,{"derivedFrom":makeQuery(id+"F3.opPattern","COPY",BODY,{"derivedFrom":makeQuery(id+"F1.opExtrude","SWEPT_BODY",BODY,{"disambiguationData":[OSD([sQuery(id+"F0.wireOp",EDGE,"E1.0"),sQuery(id+"F0.wireOp",EDGE,"E1.1"),sQuery(id+"F0.wireOp",EDGE,"E1.2"),sQuery(id+"F0.wireOp",EDGE,"E1.3"),sQuery(id+"F0.wireOp",EDGE,"E1.4"),sQuery(id+"F0.wireOp",EDGE,"E1.5"),sQuery(id+"F0.wireOp",EDGE,"E3.0"),sQuery(id+"F0.wireOp",EDGE,"E3.1"),sQuery(id+"F0.wireOp",EDGE,"E3.2"),sQuery(id+"F0.wireOp",EDGE,"E3.3"),sQuery(id+"F0.wireOp",EDGE,"E3.4"),sQuery(id+"F0.wireOp",EDGE,"E3.5")])]}),"instanceName":"1"}),"instanceName":"1"}),"instanceName":"1"});
            var Q177;
            Q177=makeQuery(id+"F7.opPattern","COPY",BODY,{"derivedFrom":makeQuery(id+"F4.opPattern","COPY",BODY,{"derivedFrom":makeQuery(id+"F1.opExtrude","SWEPT_BODY",BODY,{"disambiguationData":[OSD([sQuery(id+"F0.wireOp",EDGE,"E1.0"),sQuery(id+"F0.wireOp",EDGE,"E1.1"),sQuery(id+"F0.wireOp",EDGE,"E1.2"),sQuery(id+"F0.wireOp",EDGE,"E1.3"),sQuery(id+"F0.wireOp",EDGE,"E1.4"),sQuery(id+"F0.wireOp",EDGE,"E1.5"),sQuery(id+"F0.wireOp",EDGE,"E3.0"),sQuery(id+"F0.wireOp",EDGE,"E3.1"),sQuery(id+"F0.wireOp",EDGE,"E3.2"),sQuery(id+"F0.wireOp",EDGE,"E3.3"),sQuery(id+"F0.wireOp",EDGE,"E3.4"),sQuery(id+"F0.wireOp",EDGE,"E3.5")])]}),"instanceName":"1"}),"instanceName":"1"});
            var Q178;
            Q178=makeQuery(id+"F7.opPattern","COPY",BODY,{"derivedFrom":makeQuery(id+"F3.opPattern","COPY",BODY,{"derivedFrom":makeQuery(id+"F1.opExtrude","SWEPT_BODY",BODY,{"disambiguationData":[OSD([sQuery(id+"F0.wireOp",EDGE,"E1.0"),sQuery(id+"F0.wireOp",EDGE,"E1.1"),sQuery(id+"F0.wireOp",EDGE,"E1.2"),sQuery(id+"F0.wireOp",EDGE,"E1.3"),sQuery(id+"F0.wireOp",EDGE,"E1.4"),sQuery(id+"F0.wireOp",EDGE,"E1.5"),sQuery(id+"F0.wireOp",EDGE,"E3.0"),sQuery(id+"F0.wireOp",EDGE,"E3.1"),sQuery(id+"F0.wireOp",EDGE,"E3.2"),sQuery(id+"F0.wireOp",EDGE,"E3.3"),sQuery(id+"F0.wireOp",EDGE,"E3.4"),sQuery(id+"F0.wireOp",EDGE,"E3.5")])]}),"instanceName":"1"}),"instanceName":"1"});
            var Q179;
            Q179=makeQuery(id+"F7.opPattern","COPY",BODY,{"derivedFrom":makeQuery(id+"F1.opExtrude","SWEPT_BODY",BODY,{"disambiguationData":[OSD([sQuery(id+"F0.wireOp",EDGE,"E1.0"),sQuery(id+"F0.wireOp",EDGE,"E1.1"),sQuery(id+"F0.wireOp",EDGE,"E1.2"),sQuery(id+"F0.wireOp",EDGE,"E1.3"),sQuery(id+"F0.wireOp",EDGE,"E1.4"),sQuery(id+"F0.wireOp",EDGE,"E1.5"),sQuery(id+"F0.wireOp",EDGE,"E3.0"),sQuery(id+"F0.wireOp",EDGE,"E3.1"),sQuery(id+"F0.wireOp",EDGE,"E3.2"),sQuery(id+"F0.wireOp",EDGE,"E3.3"),sQuery(id+"F0.wireOp",EDGE,"E3.4"),sQuery(id+"F0.wireOp",EDGE,"E3.5")])]}),"instanceName":"1"});
            var Q180;
            Q180=makeQuery(id+"F6.opPattern","COPY",BODY,{"derivedFrom":makeQuery(id+"F5.opPattern","COPY",BODY,{"derivedFrom":makeQuery(id+"F4.opPattern","COPY",BODY,{"derivedFrom":makeQuery(id+"F3.opPattern","COPY",BODY,{"derivedFrom":makeQuery(id+"F1.opExtrude","SWEPT_BODY",BODY,{"disambiguationData":[OSD([sQuery(id+"F0.wireOp",EDGE,"E1.0"),sQuery(id+"F0.wireOp",EDGE,"E1.1"),sQuery(id+"F0.wireOp",EDGE,"E1.2"),sQuery(id+"F0.wireOp",EDGE,"E1.3"),sQuery(id+"F0.wireOp",EDGE,"E1.4"),sQuery(id+"F0.wireOp",EDGE,"E1.5"),sQuery(id+"F0.wireOp",EDGE,"E3.0"),sQuery(id+"F0.wireOp",EDGE,"E3.1"),sQuery(id+"F0.wireOp",EDGE,"E3.2"),sQuery(id+"F0.wireOp",EDGE,"E3.3"),sQuery(id+"F0.wireOp",EDGE,"E3.4"),sQuery(id+"F0.wireOp",EDGE,"E3.5")])]}),"instanceName":"1"}),"instanceName":"1"}),"instanceName":"1"}),"instanceName":"1"});
            var Q181;
            Q181=makeQuery(id+"F6.opPattern","COPY",BODY,{"derivedFrom":makeQuery(id+"F5.opPattern","COPY",BODY,{"derivedFrom":makeQuery(id+"F4.opPattern","COPY",BODY,{"derivedFrom":makeQuery(id+"F1.opExtrude","SWEPT_BODY",BODY,{"disambiguationData":[OSD([sQuery(id+"F0.wireOp",EDGE,"E1.0"),sQuery(id+"F0.wireOp",EDGE,"E1.1"),sQuery(id+"F0.wireOp",EDGE,"E1.2"),sQuery(id+"F0.wireOp",EDGE,"E1.3"),sQuery(id+"F0.wireOp",EDGE,"E1.4"),sQuery(id+"F0.wireOp",EDGE,"E1.5"),sQuery(id+"F0.wireOp",EDGE,"E3.0"),sQuery(id+"F0.wireOp",EDGE,"E3.1"),sQuery(id+"F0.wireOp",EDGE,"E3.2"),sQuery(id+"F0.wireOp",EDGE,"E3.3"),sQuery(id+"F0.wireOp",EDGE,"E3.4"),sQuery(id+"F0.wireOp",EDGE,"E3.5")])]}),"instanceName":"1"}),"instanceName":"1"}),"instanceName":"1"});
            var Q182;
            Q182=makeQuery(id+"F6.opPattern","COPY",BODY,{"derivedFrom":makeQuery(id+"F4.opPattern","COPY",BODY,{"derivedFrom":makeQuery(id+"F3.opPattern","COPY",BODY,{"derivedFrom":makeQuery(id+"F1.opExtrude","SWEPT_BODY",BODY,{"disambiguationData":[OSD([sQuery(id+"F0.wireOp",EDGE,"E1.0"),sQuery(id+"F0.wireOp",EDGE,"E1.1"),sQuery(id+"F0.wireOp",EDGE,"E1.2"),sQuery(id+"F0.wireOp",EDGE,"E1.3"),sQuery(id+"F0.wireOp",EDGE,"E1.4"),sQuery(id+"F0.wireOp",EDGE,"E1.5"),sQuery(id+"F0.wireOp",EDGE,"E3.0"),sQuery(id+"F0.wireOp",EDGE,"E3.1"),sQuery(id+"F0.wireOp",EDGE,"E3.2"),sQuery(id+"F0.wireOp",EDGE,"E3.3"),sQuery(id+"F0.wireOp",EDGE,"E3.4"),sQuery(id+"F0.wireOp",EDGE,"E3.5")])]}),"instanceName":"1"}),"instanceName":"1"}),"instanceName":"1"});
            var Q183;
            Q183=makeQuery(id+"F4.opPattern","COPY",BODY,{"derivedFrom":makeQuery(id+"F1.opExtrude","SWEPT_BODY",BODY,{"disambiguationData":[OSD([sQuery(id+"F0.wireOp",EDGE,"E1.0"),sQuery(id+"F0.wireOp",EDGE,"E1.1"),sQuery(id+"F0.wireOp",EDGE,"E1.2"),sQuery(id+"F0.wireOp",EDGE,"E1.3"),sQuery(id+"F0.wireOp",EDGE,"E1.4"),sQuery(id+"F0.wireOp",EDGE,"E1.5"),sQuery(id+"F0.wireOp",EDGE,"E3.0"),sQuery(id+"F0.wireOp",EDGE,"E3.1"),sQuery(id+"F0.wireOp",EDGE,"E3.2"),sQuery(id+"F0.wireOp",EDGE,"E3.3"),sQuery(id+"F0.wireOp",EDGE,"E3.4"),sQuery(id+"F0.wireOp",EDGE,"E3.5")])]}),"instanceName":"1"});
            var Q184;
            Q184=makeQuery(id+"F4.opPattern","COPY",BODY,{"derivedFrom":makeQuery(id+"F3.opPattern","COPY",BODY,{"derivedFrom":makeQuery(id+"F1.opExtrude","SWEPT_BODY",BODY,{"disambiguationData":[OSD([sQuery(id+"F0.wireOp",EDGE,"E1.0"),sQuery(id+"F0.wireOp",EDGE,"E1.1"),sQuery(id+"F0.wireOp",EDGE,"E1.2"),sQuery(id+"F0.wireOp",EDGE,"E1.3"),sQuery(id+"F0.wireOp",EDGE,"E1.4"),sQuery(id+"F0.wireOp",EDGE,"E1.5"),sQuery(id+"F0.wireOp",EDGE,"E3.0"),sQuery(id+"F0.wireOp",EDGE,"E3.1"),sQuery(id+"F0.wireOp",EDGE,"E3.2"),sQuery(id+"F0.wireOp",EDGE,"E3.3"),sQuery(id+"F0.wireOp",EDGE,"E3.4"),sQuery(id+"F0.wireOp",EDGE,"E3.5")])]}),"instanceName":"1"}),"instanceName":"1"});
            var Q185;
            Q185=makeQuery(id+"F5.opPattern","COPY",BODY,{"derivedFrom":makeQuery(id+"F4.opPattern","COPY",BODY,{"derivedFrom":makeQuery(id+"F1.opExtrude","SWEPT_BODY",BODY,{"disambiguationData":[OSD([sQuery(id+"F0.wireOp",EDGE,"E1.0"),sQuery(id+"F0.wireOp",EDGE,"E1.1"),sQuery(id+"F0.wireOp",EDGE,"E1.2"),sQuery(id+"F0.wireOp",EDGE,"E1.3"),sQuery(id+"F0.wireOp",EDGE,"E1.4"),sQuery(id+"F0.wireOp",EDGE,"E1.5"),sQuery(id+"F0.wireOp",EDGE,"E3.0"),sQuery(id+"F0.wireOp",EDGE,"E3.1"),sQuery(id+"F0.wireOp",EDGE,"E3.2"),sQuery(id+"F0.wireOp",EDGE,"E3.3"),sQuery(id+"F0.wireOp",EDGE,"E3.4"),sQuery(id+"F0.wireOp",EDGE,"E3.5")])]}),"instanceName":"1"}),"instanceName":"1"});
            var Q186;
            Q186=makeQuery(id+"F5.opPattern","COPY",BODY,{"derivedFrom":makeQuery(id+"F4.opPattern","COPY",BODY,{"derivedFrom":makeQuery(id+"F3.opPattern","COPY",BODY,{"derivedFrom":makeQuery(id+"F1.opExtrude","SWEPT_BODY",BODY,{"disambiguationData":[OSD([sQuery(id+"F0.wireOp",EDGE,"E1.0"),sQuery(id+"F0.wireOp",EDGE,"E1.1"),sQuery(id+"F0.wireOp",EDGE,"E1.2"),sQuery(id+"F0.wireOp",EDGE,"E1.3"),sQuery(id+"F0.wireOp",EDGE,"E1.4"),sQuery(id+"F0.wireOp",EDGE,"E1.5"),sQuery(id+"F0.wireOp",EDGE,"E3.0"),sQuery(id+"F0.wireOp",EDGE,"E3.1"),sQuery(id+"F0.wireOp",EDGE,"E3.2"),sQuery(id+"F0.wireOp",EDGE,"E3.3"),sQuery(id+"F0.wireOp",EDGE,"E3.4"),sQuery(id+"F0.wireOp",EDGE,"E3.5")])]}),"instanceName":"1"}),"instanceName":"1"}),"instanceName":"1"});
            var Q187;
            Q187=makeQuery(id+"F6.opPattern","COPY",BODY,{"derivedFrom":makeQuery(id+"F1.opExtrude","SWEPT_BODY",BODY,{"disambiguationData":[OSD([sQuery(id+"F0.wireOp",EDGE,"E1.0"),sQuery(id+"F0.wireOp",EDGE,"E1.1"),sQuery(id+"F0.wireOp",EDGE,"E1.2"),sQuery(id+"F0.wireOp",EDGE,"E1.3"),sQuery(id+"F0.wireOp",EDGE,"E1.4"),sQuery(id+"F0.wireOp",EDGE,"E1.5"),sQuery(id+"F0.wireOp",EDGE,"E3.0"),sQuery(id+"F0.wireOp",EDGE,"E3.1"),sQuery(id+"F0.wireOp",EDGE,"E3.2"),sQuery(id+"F0.wireOp",EDGE,"E3.3"),sQuery(id+"F0.wireOp",EDGE,"E3.4"),sQuery(id+"F0.wireOp",EDGE,"E3.5")])]}),"instanceName":"1"});
            var Q188;
            Q188=makeQuery(id+"F6.opPattern","COPY",BODY,{"derivedFrom":makeQuery(id+"F3.opPattern","COPY",BODY,{"derivedFrom":makeQuery(id+"F1.opExtrude","SWEPT_BODY",BODY,{"disambiguationData":[OSD([sQuery(id+"F0.wireOp",EDGE,"E1.0"),sQuery(id+"F0.wireOp",EDGE,"E1.1"),sQuery(id+"F0.wireOp",EDGE,"E1.2"),sQuery(id+"F0.wireOp",EDGE,"E1.3"),sQuery(id+"F0.wireOp",EDGE,"E1.4"),sQuery(id+"F0.wireOp",EDGE,"E1.5"),sQuery(id+"F0.wireOp",EDGE,"E3.0"),sQuery(id+"F0.wireOp",EDGE,"E3.1"),sQuery(id+"F0.wireOp",EDGE,"E3.2"),sQuery(id+"F0.wireOp",EDGE,"E3.3"),sQuery(id+"F0.wireOp",EDGE,"E3.4"),sQuery(id+"F0.wireOp",EDGE,"E3.5")])]}),"instanceName":"1"}),"instanceName":"1"});
            var Q189;
            Q189=makeQuery(id+"F6.opPattern","COPY",BODY,{"derivedFrom":makeQuery(id+"F4.opPattern","COPY",BODY,{"derivedFrom":makeQuery(id+"F1.opExtrude","SWEPT_BODY",BODY,{"disambiguationData":[OSD([sQuery(id+"F0.wireOp",EDGE,"E1.0"),sQuery(id+"F0.wireOp",EDGE,"E1.1"),sQuery(id+"F0.wireOp",EDGE,"E1.2"),sQuery(id+"F0.wireOp",EDGE,"E1.3"),sQuery(id+"F0.wireOp",EDGE,"E1.4"),sQuery(id+"F0.wireOp",EDGE,"E1.5"),sQuery(id+"F0.wireOp",EDGE,"E3.0"),sQuery(id+"F0.wireOp",EDGE,"E3.1"),sQuery(id+"F0.wireOp",EDGE,"E3.2"),sQuery(id+"F0.wireOp",EDGE,"E3.3"),sQuery(id+"F0.wireOp",EDGE,"E3.4"),sQuery(id+"F0.wireOp",EDGE,"E3.5")])]}),"instanceName":"1"}),"instanceName":"1"});
            var Q190;
            Q190=makeQuery(id+"F3.opPattern","COPY",BODY,{"derivedFrom":makeQuery(id+"F1.opExtrude","SWEPT_BODY",BODY,{"disambiguationData":[OSD([sQuery(id+"F0.wireOp",EDGE,"E1.0"),sQuery(id+"F0.wireOp",EDGE,"E1.1"),sQuery(id+"F0.wireOp",EDGE,"E1.2"),sQuery(id+"F0.wireOp",EDGE,"E1.3"),sQuery(id+"F0.wireOp",EDGE,"E1.4"),sQuery(id+"F0.wireOp",EDGE,"E1.5"),sQuery(id+"F0.wireOp",EDGE,"E3.0"),sQuery(id+"F0.wireOp",EDGE,"E3.1"),sQuery(id+"F0.wireOp",EDGE,"E3.2"),sQuery(id+"F0.wireOp",EDGE,"E3.3"),sQuery(id+"F0.wireOp",EDGE,"E3.4"),sQuery(id+"F0.wireOp",EDGE,"E3.5")])]}),"instanceName":"1"});
            var Q191;
            Q191=makeQuery(id+"F13.opPattern","COPY",BODY,{"derivedFrom":makeQuery(id+"F8.opPattern","COPY",BODY,{"derivedFrom":makeQuery(id+"F7.opPattern","COPY",BODY,{"derivedFrom":makeQuery(id+"F6.opPattern","COPY",BODY,{"derivedFrom":makeQuery(id+"F5.opPattern","COPY",BODY,{"derivedFrom":makeQuery(id+"F4.opPattern","COPY",BODY,{"derivedFrom":makeQuery(id+"F1.opExtrude","SWEPT_BODY",BODY,{"disambiguationData":[OSD([sQuery(id+"F0.wireOp",EDGE,"E1.0"),sQuery(id+"F0.wireOp",EDGE,"E1.1"),sQuery(id+"F0.wireOp",EDGE,"E1.2"),sQuery(id+"F0.wireOp",EDGE,"E1.3"),sQuery(id+"F0.wireOp",EDGE,"E1.4"),sQuery(id+"F0.wireOp",EDGE,"E1.5"),sQuery(id+"F0.wireOp",EDGE,"E3.0"),sQuery(id+"F0.wireOp",EDGE,"E3.1"),sQuery(id+"F0.wireOp",EDGE,"E3.2"),sQuery(id+"F0.wireOp",EDGE,"E3.3"),sQuery(id+"F0.wireOp",EDGE,"E3.4"),sQuery(id+"F0.wireOp",EDGE,"E3.5")])]}),"instanceName":"1"}),"instanceName":"1"}),"instanceName":"1"}),"instanceName":"1"}),"instanceName":"1"}),"instanceName":"1"});
            var Q192;
            Q192=makeQuery(id+"F1.opExtrude","SWEPT_BODY",BODY,{"disambiguationData":[OSD([sQuery(id+"F0.wireOp",EDGE,"E1.0"),sQuery(id+"F0.wireOp",EDGE,"E1.1"),sQuery(id+"F0.wireOp",EDGE,"E1.2"),sQuery(id+"F0.wireOp",EDGE,"E1.3"),sQuery(id+"F0.wireOp",EDGE,"E1.4"),sQuery(id+"F0.wireOp",EDGE,"E1.5"),sQuery(id+"F0.wireOp",EDGE,"E3.0"),sQuery(id+"F0.wireOp",EDGE,"E3.1"),sQuery(id+"F0.wireOp",EDGE,"E3.2"),sQuery(id+"F0.wireOp",EDGE,"E3.3"),sQuery(id+"F0.wireOp",EDGE,"E3.4"),sQuery(id+"F0.wireOp",EDGE,"E3.5")])]});
            booleanBodies(context, id + "F16", {"operationType" : BooleanOperationType.SUBTRACTION, "tools" : qUnion([Q0]), "targets" : qUnion([Q1, Q2, Q3, Q4, Q5, Q6, Q7, Q8, Q9, Q10, Q11, Q12, Q13, Q14, Q15, Q16, Q17, Q18, Q19, Q20, Q21, Q22, Q23, Q24, Q25, Q26, Q27, Q28, Q29, Q30, Q31, Q32, Q33, Q34, Q35, Q36, Q37, Q38, Q39, Q40, Q41, Q42, Q43, Q44, Q45, Q46, Q47, Q48, Q49, Q50, Q51, Q52, Q53, Q54, Q55, Q56, Q57, Q58, Q59, Q60, Q61, Q62, Q63, Q64, Q65, Q66, Q67, Q68, Q69, Q70, Q71, Q72, Q73, Q74, Q75, Q76, Q77, Q78, Q79, Q80, Q81, Q82, Q83, Q84, Q85, Q86, Q87, Q88, Q89, Q90, Q91, Q92, Q93, Q94, Q95, Q96, Q97, Q98, Q99, Q100, Q101, Q102, Q103, Q104, Q105, Q106, Q107, Q108, Q109, Q110, Q111, Q112, Q113, Q114, Q115, Q116, Q117, Q118, Q119, Q120, Q121, Q122, Q123, Q124, Q125, Q126, Q127, Q128, Q129, Q130, Q131, Q132, Q133, Q134, Q135, Q136, Q137, Q138, Q139, Q140, Q141, Q142, Q143, Q144, Q145, Q146, Q147, Q148, Q149, Q150, Q151, Q152, Q153, Q154, Q155, Q156, Q157, Q158, Q159, Q160, Q161, Q162, Q163, Q164, Q165, Q166, Q167, Q168, Q169, Q170, Q171, Q172, Q173, Q174, Q175, Q176, Q177, Q178, Q179, Q180, Q181, Q182, Q183, Q184, Q185, Q186, Q187, Q188, Q189, Q190, Q191, Q192])});
        }
    });
